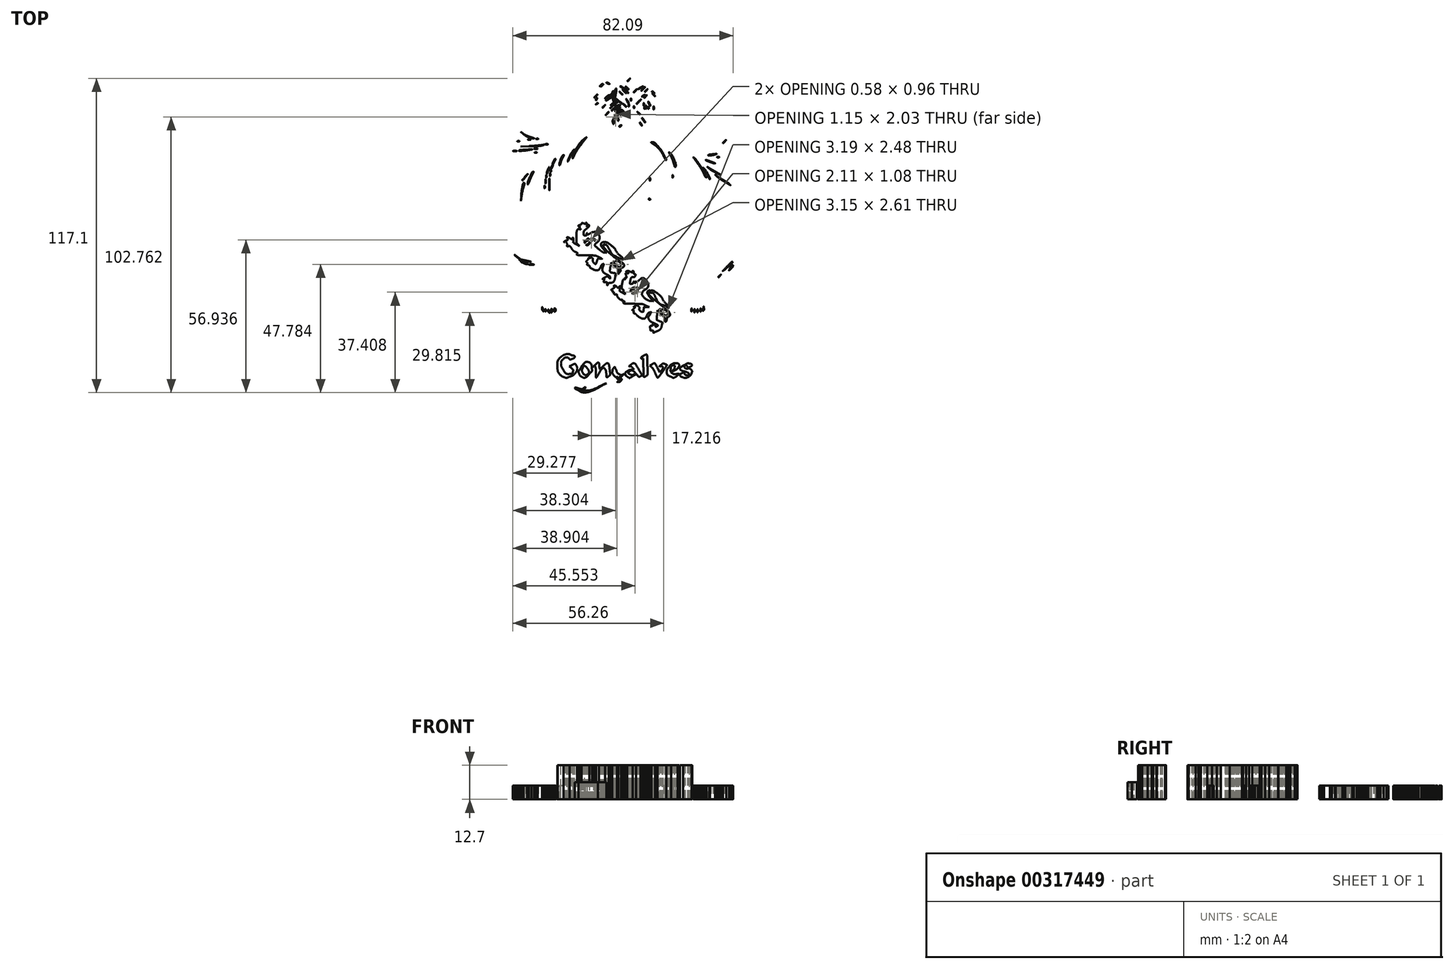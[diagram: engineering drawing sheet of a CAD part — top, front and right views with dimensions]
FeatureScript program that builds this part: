
annotation { "Feature Type Name" : "Feature", "Feature Type Description" : "" }
export const myFeature = defineFeature(function(context is Context, id is Id, definition is map)
    precondition{}
    {
        {
            var Q0;
            Q0=qCreatedBy(makeId("Top.planeOp"),FACE);
            var sketch = newSketch(context, id + "F0", { "sketchPlane" : qUnion([Q0])});
            skFitSpline(sketch, "E0", {"points": [v(-0.78, -58.9) * mm, v(-2.01, -54.71) * mm, v(-5.14, -53.63) * mm, v(-9.82, -55.77) * mm]});
            skFitSpline(sketch, "E1", {"points": [v(-9.82, -55.77) * mm, v(-12.56, -57.02) * mm, v(-15.5, -57.35) * mm, v(-17, -56.59) * mm]});
            skFitSpline(sketch, "E2", {"points": [v(-17, -56.59) * mm, v(-18.34, -55.9) * mm, v(-18.3, -55.62) * mm, v(-16.9, -55.94) * mm]});
            skFitSpline(sketch, "E3", {"points": [v(-16.9, -55.94) * mm, v(-15.84, -56.18) * mm, v(-15.54, -56.16) * mm, v(-15.17, -55.78) * mm]});
            skFitSpline(sketch, "E4", {"points": [v(-15.17, -55.78) * mm, v(-14.24, -54.85) * mm, v(-15.47, -53.87) * mm, v(-17.6, -53.87) * mm]});
            skFitSpline(sketch, "E5", {"points": [v(-17.6, -53.87) * mm, v(-18.18, -53.87) * mm, v(-20.42, -54.25) * mm, v(-22.58, -54.7) * mm]});
            skFitSpline(sketch, "E6", {"points": [v(-22.58, -54.7) * mm, v(-29.42, -56.14) * mm, v(-33.24, -56.1) * mm, v(-36.26, -54.57) * mm]});
            skFitSpline(sketch, "E7", {"points": [v(-36.26, -54.57) * mm, v(-37.83, -53.78) * mm, v(-39.63, -52.29) * mm, v(-39.63, -51.78) * mm]});
            skFitSpline(sketch, "E8", {"points": [v(-39.63, -51.78) * mm, v(-39.63, -51.6) * mm, v(-39.25, -51.16) * mm, v(-38.77, -50.8) * mm]});
            skFitSpline(sketch, "E9", {"points": [v(-38.77, -50.8) * mm, v(-36.7, -49.28) * mm, v(-35.55, -46.7) * mm, v(-34.68, -41.66) * mm]});
            skFitSpline(sketch, "E10", {"points": [v(-34.68, -41.66) * mm, v(-34, -37.71) * mm, v(-33.1, -36.66) * mm, v(-30.43, -36.66) * mm]});
            skFitSpline(sketch, "E11", {"points": [v(-30.43, -36.66) * mm, v(-28.5, -36.66) * mm, v(-26.08, -38.1) * mm, v(-26.08, -39.26) * mm]});
            skFitSpline(sketch, "E12", {"points": [v(-26.08, -39.26) * mm, v(-26.08, -39.55) * mm, v(-26.35, -40.3) * mm, v(-26.67, -40.93) * mm]});
            skFitSpline(sketch, "E13", {"points": [v(-26.67, -40.93) * mm, v(-26.99, -41.56) * mm, v(-27.17, -42.16) * mm, v(-27.07, -42.26) * mm]});
            skFitSpline(sketch, "E14", {"points": [v(-27.07, -42.26) * mm, v(-26.96, -42.36) * mm, v(-25.75, -42.44) * mm, v(-24.38, -42.44) * mm]});
            skFitSpline(sketch, "E15", {"points": [v(-24.38, -42.44) * mm, v(-22.29, -42.43) * mm, v(-21.74, -42.33) * mm, v(-21.09, -41.84) * mm]});
            skFitSpline(sketch, "E16", {"points": [v(-21.09, -41.84) * mm, v(-19.83, -40.9) * mm, v(-19.9, -40.33) * mm, v(-21.27, -40.33) * mm]});
            skFitSpline(sketch, "E17", {"points": [v(-21.27, -40.33) * mm, v(-22.5, -40.33) * mm, v(-22.69, -40) * mm, v(-22, -39.1) * mm]});
            skFitSpline(sketch, "E18", {"points": [v(-22, -39.1) * mm, v(-21.65, -38.64) * mm, v(-21.52, -38.63) * mm, v(-20.81, -38.97) * mm]});
            skFitSpline(sketch, "E19", {"points": [v(-20.81, -38.97) * mm, v(-20.14, -39.29) * mm, v(-20.02, -39.52) * mm, v(-20.02, -40.44) * mm]});
            skFitSpline(sketch, "E20", {"points": [v(-20.02, -40.44) * mm, v(-20.02, -42.1) * mm, v(-20.93, -42.65) * mm, v(-23.92, -42.8) * mm]});
            skFitSpline(sketch, "E21", {"points": [v(-23.92, -42.8) * mm, v(-28.38, -43.04) * mm, v(-33.52, -40.75) * mm, v(-33.08, -38.72) * mm]});
            skFitSpline(sketch, "E22", {"points": [v(-33.08, -38.72) * mm, v(-33.01, -38.44) * mm, v(-32.8, -38.25) * mm, v(-32.6, -38.29) * mm]});
            skFitSpline(sketch, "E23", {"points": [v(-32.6, -38.29) * mm, v(-32.41, -38.33) * mm, v(-32.33, -38.24) * mm, v(-32.42, -38.1) * mm]});
            skFitSpline(sketch, "E24", {"points": [v(-32.42, -38.1) * mm, v(-32.92, -37.29) * mm, v(-30.11, -36.95) * mm, v(-28.51, -37.62) * mm]});
            skFitSpline(sketch, "E25", {"points": [v(-28.51, -37.62) * mm, v(-27.53, -38.03) * mm, v(-26.56, -39.12) * mm, v(-26.82, -39.53) * mm]});
            skFitSpline(sketch, "E26", {"points": [v(-26.82, -39.53) * mm, v(-27.07, -39.93) * mm, v(-28.17, -39.79) * mm, v(-29.27, -39.2) * mm]});
            skLineSegment(sketch, "E27", {"start": v(-29.27, -39.2) * mm, "end": v(-30.33, -38.63) * mm});
            skLineSegment(sketch, "E28", {"start": v(-30.33, -38.63) * mm, "end": v(-30.61, -39.4) * mm});
            skFitSpline(sketch, "E29", {"points": [v(-30.61, -39.4) * mm, v(-30.77, -39.84) * mm, v(-30.95, -40.33) * mm, v(-31, -40.5) * mm]});
            skFitSpline(sketch, "E30", {"points": [v(-31, -40.5) * mm, v(-31.15, -40.9) * mm, v(-29.82, -41.53) * mm, v(-29.4, -41.28) * mm]});
            skFitSpline(sketch, "E31", {"points": [v(-29.4, -41.28) * mm, v(-29.21, -41.15) * mm, v(-29.18, -41.22) * mm, v(-29.33, -41.46) * mm]});
            skFitSpline(sketch, "E32", {"points": [v(-29.33, -41.46) * mm, v(-29.5, -41.74) * mm, v(-29.43, -41.78) * mm, v(-29.07, -41.65) * mm]});
            skFitSpline(sketch, "E33", {"points": [v(-29.07, -41.65) * mm, v(-28.8, -41.54) * mm, v(-28.27, -41.46) * mm, v(-27.9, -41.46) * mm]});
            skFitSpline(sketch, "E34", {"points": [v(-27.9, -41.46) * mm, v(-27.52, -41.46) * mm, v(-27.21, -41.31) * mm, v(-27.21, -41.14) * mm]});
            skFitSpline(sketch, "E35", {"points": [v(-27.21, -41.14) * mm, v(-27.21, -40.93) * mm, v(-27.53, -40.88) * mm, v(-28.13, -41) * mm]});
            skFitSpline(sketch, "E36", {"points": [v(-28.13, -41) * mm, v(-28.78, -41.12) * mm, v(-28.93, -41.1) * mm, v(-28.62, -40.9) * mm]});
            skFitSpline(sketch, "E37", {"points": [v(-28.62, -40.9) * mm, v(-28.4, -40.74) * mm, v(-27.9, -40.62) * mm, v(-27.55, -40.61) * mm]});
            skFitSpline(sketch, "E38", {"points": [v(-27.55, -40.61) * mm, v(-27.2, -40.61) * mm, v(-26.97, -40.5) * mm, v(-27.05, -40.36) * mm]});
            skFitSpline(sketch, "E39", {"points": [v(-27.05, -40.36) * mm, v(-27.14, -40.22) * mm, v(-27.02, -40.03) * mm, v(-26.79, -39.94) * mm]});
            skFitSpline(sketch, "E40", {"points": [v(-26.79, -39.94) * mm, v(-26.15, -39.7) * mm, v(-26.28, -39.1) * mm, v(-27.14, -38.28) * mm]});
            skFitSpline(sketch, "E41", {"points": [v(-27.14, -38.28) * mm, v(-29.26, -36.26) * mm, v(-32.86, -36.6) * mm, v(-33.66, -38.9) * mm]});
            skFitSpline(sketch, "E42", {"points": [v(-33.66, -38.9) * mm, v(-33.83, -39.39) * mm, v(-33.87, -39.75) * mm, v(-33.76, -39.7) * mm]});
            skFitSpline(sketch, "E43", {"points": [v(-33.76, -39.7) * mm, v(-33.65, -39.65) * mm, v(-33.08, -40.1) * mm, v(-32.5, -40.67) * mm]});
            skFitSpline(sketch, "E44", {"points": [v(-32.5, -40.67) * mm, v(-31.9, -41.26) * mm, v(-31.6, -41.66) * mm, v(-31.84, -41.57) * mm]});
            skFitSpline(sketch, "E45", {"points": [v(-31.84, -41.57) * mm, v(-32.16, -41.45) * mm, v(-32.24, -41.56) * mm, v(-32.16, -41.98) * mm]});
            skFitSpline(sketch, "E46", {"points": [v(-32.16, -41.98) * mm, v(-32.08, -42.38) * mm, v(-32.17, -42.5) * mm, v(-32.44, -42.4) * mm]});
            skFitSpline(sketch, "E47", {"points": [v(-32.44, -42.4) * mm, v(-32.72, -42.3) * mm, v(-32.8, -42.43) * mm, v(-32.71, -42.88) * mm]});
            skFitSpline(sketch, "E48", {"points": [v(-32.71, -42.88) * mm, v(-32.65, -43.23) * mm, v(-32.68, -43.42) * mm, v(-32.8, -43.3) * mm]});
            skFitSpline(sketch, "E49", {"points": [v(-32.8, -43.3) * mm, v(-32.9, -43.2) * mm, v(-33, -42.96) * mm, v(-33, -42.78) * mm]});
            skFitSpline(sketch, "E50", {"points": [v(-33, -42.78) * mm, v(-33, -42.6) * mm, v(-33.38, -42.43) * mm, v(-33.85, -42.4) * mm]});
            skFitSpline(sketch, "E51", {"points": [v(-33.85, -42.4) * mm, v(-34.31, -42.38) * mm, v(-34.53, -42.42) * mm, v(-34.34, -42.5) * mm]});
            skFitSpline(sketch, "E52", {"points": [v(-34.34, -42.5) * mm, v(-34.14, -42.57) * mm, v(-34.08, -42.78) * mm, v(-34.2, -42.96) * mm]});
            skFitSpline(sketch, "E53", {"points": [v(-34.2, -42.96) * mm, v(-34.31, -43.14) * mm, v(-34.41, -43.55) * mm, v(-34.42, -43.86) * mm]});
            skFitSpline(sketch, "E54", {"points": [v(-34.42, -43.86) * mm, v(-34.42, -44.17) * mm, v(-34.53, -44.58) * mm, v(-34.65, -44.77) * mm]});
            skFitSpline(sketch, "E55", {"points": [v(-34.65, -44.77) * mm, v(-34.77, -44.97) * mm, v(-34.78, -45.13) * mm, v(-34.66, -45.13) * mm]});
            skFitSpline(sketch, "E56", {"points": [v(-34.66, -45.13) * mm, v(-34.55, -45.13) * mm, v(-34.7, -45.4) * mm, v(-35, -45.74) * mm]});
            skFitSpline(sketch, "E57", {"points": [v(-35, -45.74) * mm, v(-35.3, -46.08) * mm, v(-35.38, -46.26) * mm, v(-35.19, -46.15) * mm]});
            skFitSpline(sketch, "E58", {"points": [v(-35.19, -46.15) * mm, v(-34.63, -45.82) * mm, v(-34.77, -46.3) * mm, v(-35.47, -47.06) * mm]});
            skFitSpline(sketch, "E59", {"points": [v(-35.47, -47.06) * mm, v(-35.82, -47.44) * mm, v(-35.94, -47.67) * mm, v(-35.75, -47.55) * mm]});
            skFitSpline(sketch, "E60", {"points": [v(-35.75, -47.55) * mm, v(-35.14, -47.2) * mm, v(-35.37, -47.82) * mm, v(-36.1, -48.51) * mm]});
            skFitSpline(sketch, "E61", {"points": [v(-36.1, -48.51) * mm, v(-36.5, -48.88) * mm, v(-36.8, -49.3) * mm, v(-36.8, -49.46) * mm]});
            skFitSpline(sketch, "E62", {"points": [v(-36.8, -49.46) * mm, v(-36.8, -49.6) * mm, v(-36.72, -49.65) * mm, v(-36.62, -49.55) * mm]});
            skFitSpline(sketch, "E63", {"points": [v(-36.62, -49.55) * mm, v(-36.45, -49.38) * mm, v(-35.59, -50.37) * mm, v(-35.5, -50.84) * mm]});
            skFitSpline(sketch, "E64", {"points": [v(-35.5, -50.84) * mm, v(-35.48, -50.96) * mm, v(-35.44, -51.08) * mm, v(-35.4, -51.12) * mm]});
            skFitSpline(sketch, "E65", {"points": [v(-35.4, -51.12) * mm, v(-35.22, -51.33) * mm, v(-35.23, -52.79) * mm, v(-35.43, -52.9) * mm]});
            skFitSpline(sketch, "E66", {"points": [v(-35.43, -52.9) * mm, v(-35.55, -52.98) * mm, v(-35.6, -52.78) * mm, v(-35.54, -52.45) * mm]});
            skFitSpline(sketch, "E67", {"points": [v(-35.54, -52.45) * mm, v(-35.46, -52.08) * mm, v(-35.55, -51.9) * mm, v(-35.76, -51.97) * mm]});
            skFitSpline(sketch, "E68", {"points": [v(-35.76, -51.97) * mm, v(-35.95, -52.04) * mm, v(-36.1, -52.34) * mm, v(-36.1, -52.66) * mm]});
            skFitSpline(sketch, "E69", {"points": [v(-36.1, -52.66) * mm, v(-36.1, -52.97) * mm, v(-36.28, -53.43) * mm, v(-36.5, -53.69) * mm]});
            skFitSpline(sketch, "E70", {"points": [v(-36.5, -53.69) * mm, v(-36.94, -54.23) * mm, v(-36.54, -54.32) * mm, v(-35.96, -53.8) * mm]});
            skFitSpline(sketch, "E71", {"points": [v(-35.96, -53.8) * mm, v(-35.65, -53.53) * mm, v(-35.65, -53.57) * mm, v(-35.98, -54) * mm]});
            skFitSpline(sketch, "E72", {"points": [v(-35.98, -54) * mm, v(-36.34, -54.5) * mm, v(-36.34, -54.53) * mm, v(-35.9, -54.36) * mm]});
            skFitSpline(sketch, "E73", {"points": [v(-35.9, -54.36) * mm, v(-35.62, -54.26) * mm, v(-35.4, -54.28) * mm, v(-35.4, -54.41) * mm]});
            skFitSpline(sketch, "E74", {"points": [v(-35.4, -54.41) * mm, v(-35.4, -54.88) * mm, v(-32.86, -55.29) * mm, v(-29.98, -55.28) * mm]});
            skFitSpline(sketch, "E75", {"points": [v(-29.98, -55.28) * mm, v(-27.92, -55.28) * mm, v(-26.1, -55.07) * mm, v(-23.69, -54.55) * mm]});
            skFitSpline(sketch, "E76", {"points": [v(-23.69, -54.55) * mm, v(-21.82, -54.14) * mm, v(-19.35, -53.76) * mm, v(-18.18, -53.7) * mm]});
            skFitSpline(sketch, "E77", {"points": [v(-18.18, -53.7) * mm, v(-15.67, -53.55) * mm, v(-14.7, -53.92) * mm, v(-14.56, -55.09) * mm]});
            skFitSpline(sketch, "E78", {"points": [v(-14.56, -55.09) * mm, v(-14.49, -55.73) * mm, v(-14.63, -55.93) * mm, v(-15.41, -56.27) * mm]});
            skLineSegment(sketch, "E79", {"start": v(-15.41, -56.27) * mm, "end": v(-16.35, -56.67) * mm});
            skLineSegment(sketch, "E80", {"start": v(-16.35, -56.67) * mm, "end": v(-14.77, -56.69) * mm});
            skFitSpline(sketch, "E81", {"points": [v(-14.77, -56.69) * mm, v(-13.2, -56.7) * mm, v(-11.19, -56.13) * mm, v(-9, -55.07) * mm]});
            skFitSpline(sketch, "E82", {"points": [v(-9, -55.07) * mm, v(-7.1, -54.14) * mm, v(-5.09, -54.06) * mm, v(-3.21, -54.84) * mm]});
            skFitSpline(sketch, "E83", {"points": [v(-3.21, -54.84) * mm, v(-2.94, -54.95) * mm, v(-2.41, -54.7) * mm, v(-1.82, -54.16) * mm]});
            skFitSpline(sketch, "E84", {"points": [v(-1.82, -54.16) * mm, v(-0.8, -53.25) * mm, v(0.28, -53.05) * mm, v(0.55, -53.73) * mm]});
            skFitSpline(sketch, "E85", {"points": [v(0.55, -53.73) * mm, v(0.64, -53.97) * mm, v(0.85, -54.16) * mm, v(1.02, -54.16) * mm]});
            skFitSpline(sketch, "E86", {"points": [v(1.02, -54.16) * mm, v(1.2, -54.16) * mm, v(1.5, -54.33) * mm, v(1.72, -54.54) * mm]});
            skFitSpline(sketch, "E87", {"points": [v(1.72, -54.54) * mm, v(2.04, -54.87) * mm, v(2.34, -54.87) * mm, v(3.55, -54.55) * mm]});
            skFitSpline(sketch, "E88", {"points": [v(3.55, -54.55) * mm, v(5.37, -54.08) * mm, v(6.94, -54.35) * mm, v(9.57, -55.59) * mm]});
            skFitSpline(sketch, "E89", {"points": [v(9.57, -55.59) * mm, v(11.05, -56.28) * mm, v(11.99, -56.52) * mm, v(13.53, -56.6) * mm]});
            skFitSpline(sketch, "E90", {"points": [v(13.53, -56.6) * mm, v(15.18, -56.68) * mm, v(15.4, -56.64) * mm, v(14.78, -56.4) * mm]});
            skFitSpline(sketch, "E91", {"points": [v(14.78, -56.4) * mm, v(13.63, -55.94) * mm, v(13.47, -55.04) * mm, v(14.4, -54.24) * mm]});
            skFitSpline(sketch, "E92", {"points": [v(14.4, -54.24) * mm, v(15.01, -53.71) * mm, v(15.48, -53.6) * mm, v(16.9, -53.6) * mm]});
            skFitSpline(sketch, "E93", {"points": [v(16.9, -53.6) * mm, v(17.86, -53.6) * mm, v(19.47, -53.8) * mm, v(20.48, -54.04) * mm]});
            skFitSpline(sketch, "E94", {"points": [v(20.48, -54.04) * mm, v(24.13, -54.91) * mm, v(26.89, -55.28) * mm, v(29.67, -55.29) * mm]});
            skFitSpline(sketch, "E95", {"points": [v(29.67, -55.29) * mm, v(33, -55.29) * mm, v(35.6, -54.68) * mm, v(35.32, -53.96) * mm]});
            skFitSpline(sketch, "E96", {"points": [v(35.32, -53.96) * mm, v(35.18, -53.6) * mm, v(35.22, -53.58) * mm, v(35.55, -53.85) * mm]});
            skFitSpline(sketch, "E97", {"points": [v(35.55, -53.85) * mm, v(35.9, -54.14) * mm, v(35.95, -54.05) * mm, v(35.9, -53.27) * mm]});
            skFitSpline(sketch, "E98", {"points": [v(35.9, -53.27) * mm, v(35.85, -52.77) * mm, v(35.66, -52.3) * mm, v(35.45, -52.23) * mm]});
            skFitSpline(sketch, "E99", {"points": [v(35.45, -52.23) * mm, v(35.2, -52.15) * mm, v(35.15, -52.24) * mm, v(35.3, -52.5) * mm]});
            skFitSpline(sketch, "E100", {"points": [v(35.3, -52.5) * mm, v(35.48, -52.81) * mm, v(35.45, -52.82) * mm, v(35.14, -52.53) * mm]});
            skFitSpline(sketch, "E101", {"points": [v(35.14, -52.53) * mm, v(34.57, -52) * mm, v(34.19, -52.1) * mm, v(34.63, -52.67) * mm]});
            skFitSpline(sketch, "E102", {"points": [v(34.63, -52.67) * mm, v(34.98, -53.13) * mm, v(34.97, -53.14) * mm, v(34.5, -52.76) * mm]});
            skFitSpline(sketch, "E103", {"points": [v(34.5, -52.76) * mm, v(34, -52.36) * mm, v(34, -52.34) * mm, v(34.5, -51.97) * mm]});
            skFitSpline(sketch, "E104", {"points": [v(34.5, -51.97) * mm, v(34.78, -51.76) * mm, v(35.02, -51.44) * mm, v(35.03, -51.25) * mm]});
            skFitSpline(sketch, "E105", {"points": [v(35.03, -51.25) * mm, v(35.04, -51.06) * mm, v(35.23, -50.95) * mm, v(35.45, -51) * mm]});
            skFitSpline(sketch, "E106", {"points": [v(35.45, -51) * mm, v(35.77, -51.07) * mm, v(35.79, -51.02) * mm, v(35.52, -50.75) * mm]});
            skFitSpline(sketch, "E107", {"points": [v(35.52, -50.75) * mm, v(35.26, -50.47) * mm, v(35.1, -50.47) * mm, v(34.77, -50.74) * mm]});
            skFitSpline(sketch, "E108", {"points": [v(34.77, -50.74) * mm, v(34.44, -51.02) * mm, v(34.37, -51) * mm, v(34.42, -50.65) * mm]});
            skFitSpline(sketch, "E109", {"points": [v(34.42, -50.65) * mm, v(34.45, -50.42) * mm, v(34.56, -50.14) * mm, v(34.66, -50.05) * mm]});
            skFitSpline(sketch, "E110", {"points": [v(34.66, -50.05) * mm, v(34.92, -49.78) * mm, v(34.58, -49.05) * mm, v(34.28, -49.24) * mm]});
            skFitSpline(sketch, "E111", {"points": [v(34.28, -49.24) * mm, v(34.14, -49.33) * mm, v(34.09, -49.5) * mm, v(34.17, -49.64) * mm]});
            skFitSpline(sketch, "E112", {"points": [v(34.17, -49.64) * mm, v(34.25, -49.77) * mm, v(34.17, -49.98) * mm, v(34, -50.09) * mm]});
            skFitSpline(sketch, "E113", {"points": [v(34, -50.09) * mm, v(33.77, -50.23) * mm, v(33.74, -50.17) * mm, v(33.9, -49.92) * mm]});
            skFitSpline(sketch, "E114", {"points": [v(33.9, -49.92) * mm, v(34.06, -49.65) * mm, v(34, -49.6) * mm, v(33.65, -49.73) * mm]});
            skFitSpline(sketch, "E115", {"points": [v(33.65, -49.73) * mm, v(32.97, -49.99) * mm, v(33.07, -49.83) * mm, v(34.07, -49.1) * mm]});
            skFitSpline(sketch, "E116", {"points": [v(34.07, -49.1) * mm, v(34.56, -48.73) * mm, v(34.86, -48.6) * mm, v(34.73, -48.8) * mm]});
            skFitSpline(sketch, "E117", {"points": [v(34.73, -48.8) * mm, v(34.57, -49.06) * mm, v(34.62, -49.1) * mm, v(34.88, -48.93) * mm]});
            skFitSpline(sketch, "E118", {"points": [v(34.88, -48.93) * mm, v(35.15, -48.76) * mm, v(35.2, -48.83) * mm, v(35.07, -49.19) * mm]});
            skFitSpline(sketch, "E119", {"points": [v(35.07, -49.19) * mm, v(34.97, -49.45) * mm, v(35, -49.6) * mm, v(35.14, -49.51) * mm]});
            skFitSpline(sketch, "E120", {"points": [v(35.14, -49.51) * mm, v(35.28, -49.42) * mm, v(35.5, -49.5) * mm, v(35.6, -49.68) * mm]});
            skFitSpline(sketch, "E121", {"points": [v(35.6, -49.68) * mm, v(35.73, -49.89) * mm, v(35.69, -49.93) * mm, v(35.49, -49.81) * mm]});
            skFitSpline(sketch, "E122", {"points": [v(35.49, -49.81) * mm, v(35.28, -49.68) * mm, v(35.22, -49.77) * mm, v(35.33, -50.05) * mm]});
            skFitSpline(sketch, "E123", {"points": [v(35.33, -50.05) * mm, v(35.42, -50.29) * mm, v(35.6, -50.42) * mm, v(35.73, -50.34) * mm]});
            skFitSpline(sketch, "E124", {"points": [v(35.73, -50.34) * mm, v(35.86, -50.26) * mm, v(36.06, -50.35) * mm, v(36.17, -50.53) * mm]});
            skFitSpline(sketch, "E125", {"points": [v(36.17, -50.53) * mm, v(36.3, -50.73) * mm, v(36.25, -50.78) * mm, v(36.05, -50.66) * mm]});
            skFitSpline(sketch, "E126", {"points": [v(36.05, -50.66) * mm, v(35.83, -50.52) * mm, v(35.8, -50.62) * mm, v(35.92, -50.95) * mm]});
            skFitSpline(sketch, "E127", {"points": [v(35.92, -50.95) * mm, v(36.04, -51.28) * mm, v(36.15, -51.33) * mm, v(36.23, -51.1) * mm]});
            skFitSpline(sketch, "E128", {"points": [v(36.23, -51.1) * mm, v(36.3, -50.84) * mm, v(36.46, -50.9) * mm, v(36.74, -51.25) * mm]});
            skFitSpline(sketch, "E129", {"points": [v(36.74, -51.25) * mm, v(37.11, -51.73) * mm, v(37.12, -51.73) * mm, v(36.95, -51.2) * mm]});
            skFitSpline(sketch, "E130", {"points": [v(36.95, -51.2) * mm, v(36.85, -50.88) * mm, v(36.86, -50.71) * mm, v(36.97, -50.82) * mm]});
            skFitSpline(sketch, "E131", {"points": [v(36.97, -50.82) * mm, v(37.3, -51.11) * mm, v(37.38, -52.47) * mm, v(37.05, -52.27) * mm]});
            skFitSpline(sketch, "E132", {"points": [v(37.05, -52.27) * mm, v(36.88, -52.16) * mm, v(36.85, -52.24) * mm, v(37, -52.46) * mm]});
            skFitSpline(sketch, "E133", {"points": [v(37, -52.46) * mm, v(37.14, -52.7) * mm, v(37.11, -52.76) * mm, v(36.9, -52.64) * mm]});
            skFitSpline(sketch, "E134", {"points": [v(36.9, -52.64) * mm, v(36.73, -52.53) * mm, v(36.68, -52.23) * mm, v(36.78, -51.96) * mm]});
            skFitSpline(sketch, "E135", {"points": [v(36.78, -51.96) * mm, v(36.94, -51.53) * mm, v(36.9, -51.52) * mm, v(36.47, -51.87) * mm]});
            skFitSpline(sketch, "E136", {"points": [v(36.47, -51.87) * mm, v(35.93, -52.31) * mm, v(36.15, -52.7) * mm, v(37.06, -52.87) * mm]});
            skFitSpline(sketch, "E137", {"points": [v(37.06, -52.87) * mm, v(37.56, -52.97) * mm, v(37.64, -52.87) * mm, v(37.53, -52.23) * mm]});
            skFitSpline(sketch, "E138", {"points": [v(37.53, -52.23) * mm, v(37.42, -51.5) * mm, v(37.43, -51.5) * mm, v(37.84, -52.02) * mm]});
            skFitSpline(sketch, "E139", {"points": [v(37.84, -52.02) * mm, v(38.07, -52.32) * mm, v(38.26, -52.42) * mm, v(38.26, -52.24) * mm]});
            skFitSpline(sketch, "E140", {"points": [v(38.26, -52.24) * mm, v(38.26, -52.05) * mm, v(38.26, -51.84) * mm, v(38.26, -51.76) * mm]});
            skFitSpline(sketch, "E141", {"points": [v(38.26, -51.76) * mm, v(38.26, -51.68) * mm, v(38.19, -51.63) * mm, v(38.1, -51.64) * mm]});
            skFitSpline(sketch, "E142", {"points": [v(38.1, -51.64) * mm, v(38, -51.65) * mm, v(37.76, -51.42) * mm, v(37.55, -51.14) * mm]});
            skFitSpline(sketch, "E143", {"points": [v(37.55, -51.14) * mm, v(37.35, -50.86) * mm, v(37.05, -50.63) * mm, v(36.9, -50.63) * mm]});
            skFitSpline(sketch, "E144", {"points": [v(36.9, -50.63) * mm, v(36.63, -50.63) * mm, v(34.88, -48.42) * mm, v(34.88, -48.07) * mm]});
            skFitSpline(sketch, "E145", {"points": [v(34.88, -48.07) * mm, v(34.88, -47.99) * mm, v(35.03, -48) * mm, v(35.23, -48.12) * mm]});
            skFitSpline(sketch, "E146", {"points": [v(35.23, -48.12) * mm, v(35.42, -48.23) * mm, v(35.3, -48) * mm, v(34.95, -47.62) * mm]});
            skFitSpline(sketch, "E147", {"points": [v(34.95, -47.62) * mm, v(34.25, -46.86) * mm, v(34.1, -46.4) * mm, v(34.66, -46.7) * mm]});
            skFitSpline(sketch, "E148", {"points": [v(34.66, -46.7) * mm, v(34.86, -46.8) * mm, v(34.74, -46.6) * mm, v(34.4, -46.24) * mm]});
            skFitSpline(sketch, "E149", {"points": [v(34.4, -46.24) * mm, v(34.05, -45.88) * mm, v(33.5, -45.57) * mm, v(33.15, -45.54) * mm]});
            skFitSpline(sketch, "E150", {"points": [v(33.15, -45.54) * mm, v(32.58, -45.5) * mm, v(32.58, -45.53) * mm, v(33.3, -46.05) * mm]});
            skFitSpline(sketch, "E151", {"points": [v(33.3, -46.05) * mm, v(33.93, -46.51) * mm, v(34, -46.67) * mm, v(33.69, -47.04) * mm]});
            skFitSpline(sketch, "E152", {"points": [v(33.69, -47.04) * mm, v(33.37, -47.43) * mm, v(33.4, -47.46) * mm, v(33.88, -47.28) * mm]});
            skFitSpline(sketch, "E153", {"points": [v(33.88, -47.28) * mm, v(34.19, -47.17) * mm, v(34.34, -47.16) * mm, v(34.23, -47.27) * mm]});
            skFitSpline(sketch, "E154", {"points": [v(34.23, -47.27) * mm, v(34.12, -47.38) * mm, v(34.16, -47.62) * mm, v(34.31, -47.8) * mm]});
            skFitSpline(sketch, "E155", {"points": [v(34.31, -47.8) * mm, v(34.5, -48.04) * mm, v(34.4, -48.3) * mm, v(33.98, -48.68) * mm]});
            skFitSpline(sketch, "E156", {"points": [v(33.98, -48.68) * mm, v(33.64, -48.98) * mm, v(33.47, -49.04) * mm, v(33.6, -48.82) * mm]});
            skFitSpline(sketch, "E157", {"points": [v(33.6, -48.82) * mm, v(33.78, -48.52) * mm, v(33.72, -48.46) * mm, v(33.39, -48.59) * mm]});
            skFitSpline(sketch, "E158", {"points": [v(33.39, -48.59) * mm, v(33.05, -48.72) * mm, v(32.97, -48.62) * mm, v(33.05, -48.2) * mm]});
            skFitSpline(sketch, "E159", {"points": [v(33.05, -48.2) * mm, v(33.14, -47.74) * mm, v(33.04, -47.67) * mm, v(32.53, -47.81) * mm]});
            skFitSpline(sketch, "E160", {"points": [v(32.53, -47.81) * mm, v(32.1, -47.93) * mm, v(32.03, -47.9) * mm, v(32.3, -47.72) * mm]});
            skFitSpline(sketch, "E161", {"points": [v(32.3, -47.72) * mm, v(32.62, -47.5) * mm, v(32.62, -47.43) * mm, v(32.3, -47.3) * mm]});
            skFitSpline(sketch, "E162", {"points": [v(32.3, -47.3) * mm, v(31.99, -47.17) * mm, v(32, -47.14) * mm, v(32.32, -47.12) * mm]});
            skFitSpline(sketch, "E163", {"points": [v(32.32, -47.12) * mm, v(32.62, -47.1) * mm, v(32.58, -46.99) * mm, v(32.18, -46.68) * mm]});
            skFitSpline(sketch, "E164", {"points": [v(32.18, -46.68) * mm, v(31.81, -46.4) * mm, v(31.78, -46.3) * mm, v(32.08, -46.4) * mm]});
            skFitSpline(sketch, "E165", {"points": [v(32.08, -46.4) * mm, v(32.36, -46.5) * mm, v(32.52, -46.4) * mm, v(32.52, -46.11) * mm]});
            skFitSpline(sketch, "E166", {"points": [v(32.52, -46.11) * mm, v(32.52, -45.83) * mm, v(32.36, -45.72) * mm, v(32.08, -45.82) * mm]});
            skFitSpline(sketch, "E167", {"points": [v(32.08, -45.82) * mm, v(31.78, -45.92) * mm, v(31.81, -45.83) * mm, v(32.18, -45.55) * mm]});
            skFitSpline(sketch, "E168", {"points": [v(32.18, -45.55) * mm, v(32.82, -45.05) * mm, v(33.05, -44.16) * mm, v(32.47, -44.38) * mm]});
            skFitSpline(sketch, "E169", {"points": [v(32.47, -44.38) * mm, v(32.21, -44.48) * mm, v(32.13, -44.35) * mm, v(32.2, -43.95) * mm]});
            skFitSpline(sketch, "E170", {"points": [v(32.2, -43.95) * mm, v(32.28, -43.53) * mm, v(32.2, -43.42) * mm, v(31.89, -43.54) * mm]});
            skFitSpline(sketch, "E171", {"points": [v(31.89, -43.54) * mm, v(31.65, -43.63) * mm, v(31.53, -43.6) * mm, v(31.62, -43.45) * mm]});
            skFitSpline(sketch, "E172", {"points": [v(31.62, -43.45) * mm, v(31.7, -43.31) * mm, v(31.62, -43.15) * mm, v(31.43, -43.08) * mm]});
            skFitSpline(sketch, "E173", {"points": [v(31.43, -43.08) * mm, v(31.22, -43.01) * mm, v(31.28, -42.9) * mm, v(31.59, -42.78) * mm]});
            skFitSpline(sketch, "E174", {"points": [v(31.59, -42.78) * mm, v(31.92, -42.66) * mm, v(32.02, -42.7) * mm, v(31.89, -42.9) * mm]});
            skFitSpline(sketch, "E175", {"points": [v(31.89, -42.9) * mm, v(31.77, -43.1) * mm, v(31.84, -43.17) * mm, v(32.06, -43.1) * mm]});
            skFitSpline(sketch, "E176", {"points": [v(32.06, -43.1) * mm, v(32.26, -43.03) * mm, v(32.46, -42.75) * mm, v(32.5, -42.48) * mm]});
            skFitSpline(sketch, "E177", {"points": [v(32.5, -42.48) * mm, v(32.55, -42.17) * mm, v(32.44, -42.03) * mm, v(32.22, -42.11) * mm]});
            skFitSpline(sketch, "E178", {"points": [v(32.22, -42.11) * mm, v(31.72, -42.3) * mm, v(31.82, -41.18) * mm, v(32.37, -40.4) * mm]});
            skFitSpline(sketch, "E179", {"points": [v(32.37, -40.4) * mm, v(32.61, -40.05) * mm, v(32.9, -39.85) * mm, v(33, -39.95) * mm]});
            skFitSpline(sketch, "E180", {"points": [v(33, -39.95) * mm, v(33.32, -40.28) * mm, v(33.2, -40.65) * mm, v(32.83, -40.43) * mm]});
            skFitSpline(sketch, "E181", {"points": [v(32.83, -40.43) * mm, v(32.55, -40.27) * mm, v(32.55, -40.3) * mm, v(32.81, -40.64) * mm]});
            skFitSpline(sketch, "E182", {"points": [v(32.81, -40.64) * mm, v(33.07, -40.96) * mm, v(33.14, -42.16) * mm, v(32.9, -42.16) * mm]});
            skFitSpline(sketch, "E183", {"points": [v(32.9, -42.16) * mm, v(32.88, -42.16) * mm, v(32.81, -42.4) * mm, v(32.76, -42.67) * mm]});
            skFitSpline(sketch, "E184", {"points": [v(32.76, -42.67) * mm, v(32.69, -43.05) * mm, v(32.75, -43.1) * mm, v(33.02, -42.89) * mm]});
            skFitSpline(sketch, "E185", {"points": [v(33.02, -42.89) * mm, v(33.22, -42.72) * mm, v(33.45, -42.66) * mm, v(33.54, -42.75) * mm]});
            skFitSpline(sketch, "E186", {"points": [v(33.54, -42.75) * mm, v(33.77, -42.99) * mm, v(33.64, -42.24) * mm, v(33.37, -41.8) * mm]});
            skFitSpline(sketch, "E187", {"points": [v(33.37, -41.8) * mm, v(33.24, -41.6) * mm, v(33.3, -41.46) * mm, v(33.5, -41.46) * mm]});
            skFitSpline(sketch, "E188", {"points": [v(33.5, -41.46) * mm, v(33.77, -41.46) * mm, v(33.78, -41.37) * mm, v(33.54, -41.14) * mm]});
            skFitSpline(sketch, "E189", {"points": [v(33.54, -41.14) * mm, v(33.37, -40.97) * mm, v(33.29, -40.66) * mm, v(33.36, -40.46) * mm]});
            skFitSpline(sketch, "E190", {"points": [v(33.36, -40.46) * mm, v(33.44, -40.26) * mm, v(33.37, -40.02) * mm, v(33.2, -39.92) * mm]});
            skFitSpline(sketch, "E191", {"points": [v(33.2, -39.92) * mm, v(33.04, -39.81) * mm, v(32.9, -39.44) * mm, v(32.9, -39.08) * mm]});
            skFitSpline(sketch, "E192", {"points": [v(32.9, -39.08) * mm, v(32.9, -38.72) * mm, v(32.7, -38.26) * mm, v(32.48, -38.07) * mm]});
            skFitSpline(sketch, "E193", {"points": [v(32.48, -38.07) * mm, v(32.16, -37.8) * mm, v(32.05, -37.8) * mm, v(32.05, -38.05) * mm]});
            skFitSpline(sketch, "E194", {"points": [v(32.05, -38.05) * mm, v(32.05, -38.24) * mm, v(31.9, -38.3) * mm, v(31.73, -38.18) * mm]});
            skFitSpline(sketch, "E195", {"points": [v(31.73, -38.18) * mm, v(31.52, -38.06) * mm, v(31.48, -38.1) * mm, v(31.6, -38.31) * mm]});
            skFitSpline(sketch, "E196", {"points": [v(31.6, -38.31) * mm, v(31.72, -38.5) * mm, v(31.93, -38.57) * mm, v(32.07, -38.48) * mm]});
            skFitSpline(sketch, "E197", {"points": [v(32.07, -38.48) * mm, v(32.22, -38.4) * mm, v(32.34, -38.63) * mm, v(32.34, -39.02) * mm]});
            skFitSpline(sketch, "E198", {"points": [v(32.34, -39.02) * mm, v(32.34, -40.78) * mm, v(27.73, -42.87) * mm, v(23.87, -42.86) * mm]});
            skFitSpline(sketch, "E199", {"points": [v(23.87, -42.86) * mm, v(20.4, -42.85) * mm, v(18.6, -41.67) * mm, v(19.2, -39.8) * mm]});
            skFitSpline(sketch, "E200", {"points": [v(19.2, -39.8) * mm, v(19.3, -39.48) * mm, v(19.65, -39.14) * mm, v(19.97, -39.04) * mm]});
            skFitSpline(sketch, "E201", {"points": [v(19.97, -39.04) * mm, v(20.91, -38.74) * mm, v(20, -38.36) * mm, v(18.34, -38.36) * mm]});
            skFitSpline(sketch, "E202", {"points": [v(18.34, -38.36) * mm, v(16.62, -38.35) * mm, v(15.97, -38.55) * mm, v(11.73, -40.42) * mm]});
            skFitSpline(sketch, "E203", {"points": [v(11.73, -40.42) * mm, v(8.77, -41.73) * mm, v(8.26, -41.86) * mm, v(5.92, -41.97) * mm]});
            skFitSpline(sketch, "E204", {"points": [v(5.92, -41.97) * mm, v(3.75, -42.07) * mm, v(3.14, -42) * mm, v(2, -41.48) * mm]});
            skFitSpline(sketch, "E205", {"points": [v(2, -41.48) * mm, v(1.24, -41.15) * mm, v(0.45, -40.63) * mm, v(0.23, -40.31) * mm]});
            skFitSpline(sketch, "E206", {"points": [v(0.23, -40.31) * mm, v(-0.16, -39.75) * mm, v(-0.18, -39.76) * mm, v(-1.1, -40.57) * mm]});
            skFitSpline(sketch, "E207", {"points": [v(-1.1, -40.57) * mm, v(-2.5, -41.79) * mm, v(-3.76, -42.1) * mm, v(-6.71, -41.97) * mm]});
            skFitSpline(sketch, "E208", {"points": [v(-6.71, -41.97) * mm, v(-9.1, -41.86) * mm, v(-9.52, -41.75) * mm, v(-12.47, -40.39) * mm]});
            skFitSpline(sketch, "E209", {"points": [v(-12.47, -40.39) * mm, v(-16.3, -38.62) * mm, v(-17.7, -38.24) * mm, v(-19.73, -38.41) * mm]});
            skFitSpline(sketch, "E210", {"points": [v(-19.73, -38.41) * mm, v(-21.38, -38.55) * mm, v(-21.6, -38.25) * mm, v(-20.07, -37.96) * mm]});
            skFitSpline(sketch, "E211", {"points": [v(-20.07, -37.96) * mm, v(-18.6, -37.68) * mm, v(-16.32, -38.25) * mm, v(-13.25, -39.65) * mm]});
            skFitSpline(sketch, "E212", {"points": [v(-13.25, -39.65) * mm, v(-9.9, -41.18) * mm, v(-8.06, -41.73) * mm, v(-6.33, -41.73) * mm]});
            skFitSpline(sketch, "E213", {"points": [v(-6.33, -41.73) * mm, v(-5.1, -41.73) * mm, v(-5.14, -41.7) * mm, v(-7.6, -40.87) * mm]});
            skFitSpline(sketch, "E214", {"points": [v(-7.6, -40.87) * mm, v(-15.53, -38.2) * mm, v(-20.56, -32.24) * mm, v(-22.46, -23.25) * mm]});
            skFitSpline(sketch, "E215", {"points": [v(-22.46, -23.25) * mm, v(-22.85, -21.4) * mm, v(-23.04, -18.95) * mm, v(-23.17, -14.17) * mm]});
            skLineSegment(sketch, "E216", {"start": v(-23.17, -14.17) * mm, "end": v(-23.35, -7.63) * mm});
            skLineSegment(sketch, "E217", {"start": v(-23.35, -7.63) * mm, "end": v(-24.18, -8.87) * mm});
            skFitSpline(sketch, "E218", {"points": [v(-24.18, -8.87) * mm, v(-25.72, -11.2) * mm, v(-28.2, -12.66) * mm, v(-31.37, -13.09) * mm]});
            skFitSpline(sketch, "E219", {"points": [v(-31.37, -13.09) * mm, v(-32.83, -13.28) * mm, v(-32.84, -13.29) * mm, v(-32.4, -13.95) * mm]});
            skFitSpline(sketch, "E220", {"points": [v(-32.4, -13.95) * mm, v(-32.16, -14.31) * mm, v(-32, -14.9) * mm, v(-32.06, -15.26) * mm]});
            skFitSpline(sketch, "E221", {"points": [v(-32.06, -15.26) * mm, v(-32.15, -15.87) * mm, v(-32.28, -15.92) * mm, v(-34.05, -15.92) * mm]});
            skLineSegment(sketch, "E222", {"start": v(-34.05, -15.92) * mm, "end": v(-35.95, -15.92) * mm});
            skLineSegment(sketch, "E223", {"start": v(-35.95, -15.92) * mm, "end": v(-37.42, -18.84) * mm});
            skFitSpline(sketch, "E224", {"points": [v(-37.42, -18.84) * mm, v(-38.77, -21.52) * mm, v(-38.9, -21.92) * mm, v(-38.9, -23.77) * mm]});
            skFitSpline(sketch, "E225", {"points": [v(-38.9, -23.77) * mm, v(-38.92, -25.68) * mm, v(-38.89, -25.8) * mm, v(-38.26, -25.89) * mm]});
            skFitSpline(sketch, "E226", {"points": [v(-38.26, -25.89) * mm, v(-37.15, -26.04) * mm, v(-35.41, -23.9) * mm, v(-33.32, -19.79) * mm]});
            skFitSpline(sketch, "E227", {"points": [v(-33.32, -19.79) * mm, v(-31.1, -15.42) * mm, v(-30.3, -14.36) * mm, v(-29.2, -14.36) * mm]});
            skFitSpline(sketch, "E228", {"points": [v(-29.2, -14.36) * mm, v(-27.86, -14.36) * mm, v(-27.33, -15.61) * mm, v(-27.04, -19.52) * mm]});
            skFitSpline(sketch, "E229", {"points": [v(-27.04, -19.52) * mm, v(-26.87, -21.77) * mm, v(-26.73, -22.25) * mm, v(-25.97, -23.35) * mm]});
            skFitSpline(sketch, "E230", {"points": [v(-25.97, -23.35) * mm, v(-25.49, -24.04) * mm, v(-24.8, -24.91) * mm, v(-24.44, -25.28) * mm]});
            skFitSpline(sketch, "E231", {"points": [v(-24.44, -25.28) * mm, v(-24, -25.73) * mm, v(-23.85, -26.13) * mm, v(-23.97, -26.5) * mm]});
            skFitSpline(sketch, "E232", {"points": [v(-23.97, -26.5) * mm, v(-24.21, -27.27) * mm, v(-23.4, -28.52) * mm, v(-21.3, -30.58) * mm]});
            skFitSpline(sketch, "E233", {"points": [v(-21.3, -30.58) * mm, v(-20.36, -31.5) * mm, v(-19.6, -32.4) * mm, v(-19.6, -32.56) * mm]});
            skFitSpline(sketch, "E234", {"points": [v(-19.6, -32.56) * mm, v(-19.62, -32.96) * mm, v(-21.5, -34.12) * mm, v(-22.14, -34.12) * mm]});
            skFitSpline(sketch, "E235", {"points": [v(-22.14, -34.12) * mm, v(-22.43, -34.12) * mm, v(-22.74, -34.25) * mm, v(-22.84, -34.4) * mm]});
            skFitSpline(sketch, "E236", {"points": [v(-22.84, -34.4) * mm, v(-22.93, -34.55) * mm, v(-23.42, -34.68) * mm, v(-23.91, -34.68) * mm]});
            skFitSpline(sketch, "E237", {"points": [v(-23.91, -34.68) * mm, v(-24.4, -34.68) * mm, v(-25.7, -34.74) * mm, v(-26.79, -34.82) * mm]});
            skFitSpline(sketch, "E238", {"points": [v(-26.79, -34.82) * mm, v(-27.88, -34.9) * mm, v(-29.65, -34.83) * mm, v(-30.74, -34.67) * mm]});
            skFitSpline(sketch, "E239", {"points": [v(-30.74, -34.67) * mm, v(-32.4, -34.42) * mm, v(-32.92, -34.2) * mm, v(-33.99, -33.3) * mm]});
            skFitSpline(sketch, "E240", {"points": [v(-33.99, -33.3) * mm, v(-34.68, -32.7) * mm, v(-35.3, -32.04) * mm, v(-35.34, -31.8) * mm]});
            skFitSpline(sketch, "E241", {"points": [v(-35.34, -31.8) * mm, v(-35.39, -31.57) * mm, v(-34.53, -30.7) * mm, v(-33.32, -29.78) * mm]});
            skFitSpline(sketch, "E242", {"points": [v(-33.32, -29.78) * mm, v(-31.16, -28.13) * mm, v(-30.65, -27.47) * mm, v(-31.16, -26.96) * mm]});
            skFitSpline(sketch, "E243", {"points": [v(-31.16, -26.96) * mm, v(-31.6, -26.52) * mm, v(-31.5, -25.49) * mm, v(-31, -25.07) * mm]});
            skFitSpline(sketch, "E244", {"points": [v(-31, -25.07) * mm, v(-30.76, -24.87) * mm, v(-30.32, -24.23) * mm, v(-30.03, -23.66) * mm]});
            skFitSpline(sketch, "E245", {"points": [v(-30.03, -23.66) * mm, v(-29.73, -23.09) * mm, v(-29.28, -22.54) * mm, v(-29.02, -22.44) * mm]});
            skFitSpline(sketch, "E246", {"points": [v(-29.02, -22.44) * mm, v(-28.6, -22.28) * mm, v(-28.57, -21.97) * mm, v(-28.74, -20.07) * mm]});
            skFitSpline(sketch, "E247", {"points": [v(-28.74, -20.07) * mm, v(-28.97, -17.53) * mm, v(-29.16, -16.62) * mm, v(-29.47, -16.62) * mm]});
            skFitSpline(sketch, "E248", {"points": [v(-29.47, -16.62) * mm, v(-29.6, -16.62) * mm, v(-30.6, -18.38) * mm, v(-31.7, -20.53) * mm]});
            skFitSpline(sketch, "E249", {"points": [v(-31.7, -20.53) * mm, v(-33.91, -24.82) * mm, v(-35.18, -26.52) * mm, v(-36.83, -27.36) * mm]});
            skFitSpline(sketch, "E250", {"points": [v(-36.83, -27.36) * mm, v(-38.2, -28.06) * mm, v(-38.8, -28.05) * mm, v(-39.73, -27.33) * mm]});
            skFitSpline(sketch, "E251", {"points": [v(-39.73, -27.33) * mm, v(-41.56, -25.89) * mm, v(-41.33, -22.83) * mm, v(-39.03, -18.07) * mm]});
            skFitSpline(sketch, "E252", {"points": [v(-39.03, -18.07) * mm, v(-38.25, -16.47) * mm, v(-37.66, -15.12) * mm, v(-37.7, -15.09) * mm]});
            skFitSpline(sketch, "E253", {"points": [v(-37.7, -15.09) * mm, v(-37.76, -15.05) * mm, v(-38.27, -14.74) * mm, v(-38.84, -14.4) * mm]});
            skFitSpline(sketch, "E254", {"points": [v(-38.84, -14.4) * mm, v(-40.24, -13.56) * mm, v(-43.5, -10.01) * mm, v(-44.67, -8.06) * mm]});
            skFitSpline(sketch, "E255", {"points": [v(-44.67, -8.06) * mm, v(-46.84, -4.43) * mm, v(-47.82, -0.62) * mm, v(-47.82, 4.27) * mm]});
            skFitSpline(sketch, "E256", {"points": [v(-47.82, 4.27) * mm, v(-47.82, 7.67) * mm, v(-47.3, 10.55) * mm, v(-46.26, 12.9) * mm]});
            skLineSegment(sketch, "E257", {"start": v(-46.26, 12.9) * mm, "end": v(-45.62, 14.36) * mm});
            skLineSegment(sketch, "E258", {"start": v(-45.62, 14.36) * mm, "end": v(-46.79, 13.69) * mm});
            skFitSpline(sketch, "E259", {"points": [v(-46.79, 13.69) * mm, v(-47.43, 13.32) * mm, v(-48.12, 13.02) * mm, v(-48.32, 13.02) * mm]});
            skFitSpline(sketch, "E260", {"points": [v(-48.32, 13.02) * mm, v(-49, 13) * mm, v(-49.17, 14.24) * mm, v(-48.77, 16.4) * mm]});
            skFitSpline(sketch, "E261", {"points": [v(-48.77, 16.4) * mm, v(-48.27, 19.12) * mm, v(-48.02, 19.67) * mm, v(-46.95, 20.32) * mm]});
            skFitSpline(sketch, "E262", {"points": [v(-46.95, 20.32) * mm, v(-46.43, 20.64) * mm, v(-46.2, 20.93) * mm, v(-46.38, 21.04) * mm]});
            skFitSpline(sketch, "E263", {"points": [v(-46.38, 21.04) * mm, v(-46.83, 21.32) * mm, v(-46.75, 22.8) * mm, v(-46.22, 23.82) * mm]});
            skFitSpline(sketch, "E264", {"points": [v(-46.22, 23.82) * mm, v(-45.46, 25.31) * mm, v(-43.6, 27.38) * mm, v(-42.35, 28.1) * mm]});
            skFitSpline(sketch, "E265", {"points": [v(-42.35, 28.1) * mm, v(-41.61, 28.53) * mm, v(-40.5, 28.85) * mm, v(-39.35, 28.96) * mm]});
            skFitSpline(sketch, "E266", {"points": [v(-39.35, 28.96) * mm, v(-37.05, 29.19) * mm, v(-36.03, 29.57) * mm, v(-35.8, 30.28) * mm]});
            skFitSpline(sketch, "E267", {"points": [v(-35.8, 30.28) * mm, v(-35.52, 31.17) * mm, v(-35.81, 31.16) * mm, v(-37.44, 30.25) * mm]});
            skFitSpline(sketch, "E268", {"points": [v(-37.44, 30.25) * mm, v(-39.32, 29.18) * mm, v(-40.27, 29.16) * mm, v(-42.22, 30.14) * mm]});
            skFitSpline(sketch, "E269", {"points": [v(-42.22, 30.14) * mm, v(-44.1, 31.09) * mm, v(-44.71, 31.6) * mm, v(-44.71, 32.2) * mm]});
            skFitSpline(sketch, "E270", {"points": [v(-44.71, 32.2) * mm, v(-44.71, 32.87) * mm, v(-43.6, 33.82) * mm, v(-42.32, 34.27) * mm]});
            skFitSpline(sketch, "E271", {"points": [v(-42.32, 34.27) * mm, v(-40.67, 34.84) * mm, v(-40.74, 35.27) * mm, v(-42.41, 34.93) * mm]});
            skFitSpline(sketch, "E272", {"points": [v(-42.41, 34.93) * mm, v(-44.12, 34.58) * mm, v(-45.2, 34.96) * mm, v(-46.41, 36.35) * mm]});
            skLineSegment(sketch, "E273", {"start": v(-46.41, 36.35) * mm, "end": v(-47.27, 37.32) * mm});
            skLineSegment(sketch, "E274", {"start": v(-47.27, 37.32) * mm, "end": v(-46.2, 38.05) * mm});
            skFitSpline(sketch, "E275", {"points": [v(-46.2, 38.05) * mm, v(-45.61, 38.44) * mm, v(-44.83, 39) * mm, v(-44.46, 39.3) * mm]});
            skFitSpline(sketch, "E276", {"points": [v(-44.46, 39.3) * mm, v(-43.58, 39.99) * mm, v(-42.14, 39.96) * mm, v(-40.73, 39.24) * mm]});
            skFitSpline(sketch, "E277", {"points": [v(-40.73, 39.24) * mm, v(-40.1, 38.92) * mm, v(-39.44, 38.71) * mm, v(-39.26, 38.77) * mm]});
            skFitSpline(sketch, "E278", {"points": [v(-39.26, 38.77) * mm, v(-39.07, 38.83) * mm, v(-39.52, 39.15) * mm, v(-40.24, 39.47) * mm]});
            skFitSpline(sketch, "E279", {"points": [v(-40.24, 39.47) * mm, v(-41.36, 39.96) * mm, v(-42.17, 40.76) * mm, v(-42.17, 41.35) * mm]});
            skFitSpline(sketch, "E280", {"points": [v(-42.17, 41.35) * mm, v(-42.17, 41.6) * mm, v(-39.41, 42.93) * mm, v(-38.9, 42.93) * mm]});
            skFitSpline(sketch, "E281", {"points": [v(-38.9, 42.93) * mm, v(-38.64, 42.93) * mm, v(-38.26, 43.15) * mm, v(-38.07, 43.42) * mm]});
            skFitSpline(sketch, "E282", {"points": [v(-38.07, 43.42) * mm, v(-37.73, 43.87) * mm, v(-37.65, 43.88) * mm, v(-36.72, 43.43) * mm]});
            skFitSpline(sketch, "E283", {"points": [v(-36.72, 43.43) * mm, v(-36, 43.09) * mm, v(-35.64, 42.68) * mm, v(-35.4, 41.89) * mm]});
            skFitSpline(sketch, "E284", {"points": [v(-35.4, 41.89) * mm, v(-34.93, 40.43) * mm, v(-34.34, 39.54) * mm, v(-33.84, 39.54) * mm]});
            skFitSpline(sketch, "E285", {"points": [v(-33.84, 39.54) * mm, v(-33.23, 39.54) * mm, v(-33.33, 40.05) * mm, v(-34.13, 41) * mm]});
            skFitSpline(sketch, "E286", {"points": [v(-34.13, 41) * mm, v(-35.06, 42.1) * mm, v(-35.02, 42.53) * mm, v(-33.94, 42.9) * mm]});
            skFitSpline(sketch, "E287", {"points": [v(-33.94, 42.9) * mm, v(-31.9, 43.61) * mm, v(-30.7, 43.26) * mm, v(-26.8, 40.86) * mm]});
            skFitSpline(sketch, "E288", {"points": [v(-26.8, 40.86) * mm, v(-25.38, 39.98) * mm, v(-24.88, 39.82) * mm, v(-23.5, 39.82) * mm]});
            skFitSpline(sketch, "E289", {"points": [v(-23.5, 39.82) * mm, v(-22.04, 39.82) * mm, v(-21.7, 39.95) * mm, v(-19.96, 41.15) * mm]});
            skFitSpline(sketch, "E290", {"points": [v(-19.96, 41.15) * mm, v(-18.9, 41.87) * mm, v(-17.55, 42.75) * mm, v(-16.96, 43.09) * mm]});
            skLineSegment(sketch, "E291", {"start": v(-16.96, 43.09) * mm, "end": v(-15.87, 43.7) * mm});
            skLineSegment(sketch, "E292", {"start": v(-15.87, 43.7) * mm, "end": v(-16.73, 44.14) * mm});
            skFitSpline(sketch, "E293", {"points": [v(-16.73, 44.14) * mm, v(-17.46, 44.5) * mm, v(-17.66, 44.5) * mm, v(-18.1, 44.18) * mm]});
            skFitSpline(sketch, "E294", {"points": [v(-18.1, 44.18) * mm, v(-19.32, 43.25) * mm, v(-22.13, 44.05) * mm, v(-22.13, 45.33) * mm]});
            skFitSpline(sketch, "E295", {"points": [v(-22.13, 45.33) * mm, v(-22.13, 45.98) * mm, v(-22.24, 46.03) * mm, v(-23.43, 46.03) * mm]});
            skFitSpline(sketch, "E296", {"points": [v(-23.43, 46.03) * mm, v(-25.2, 46.03) * mm, v(-26.4, 46.67) * mm, v(-27.47, 48.15) * mm]});
            skFitSpline(sketch, "E297", {"points": [v(-27.47, 48.15) * mm, v(-28, 48.9) * mm, v(-28.95, 49.7) * mm, v(-29.83, 50.18) * mm]});
            skFitSpline(sketch, "E298", {"points": [v(-29.83, 50.18) * mm, v(-31.36, 51) * mm, v(-31.55, 51.27) * mm, v(-33.26, 55.05) * mm]});
            skFitSpline(sketch, "E299", {"points": [v(-33.26, 55.05) * mm, v(-33.65, 55.9) * mm, v(-33.9, 56.65) * mm, v(-33.84, 56.71) * mm]});
            skFitSpline(sketch, "E300", {"points": [v(-33.84, 56.71) * mm, v(-33.64, 56.92) * mm, v(-31.9, 54.95) * mm, v(-31.02, 53.5) * mm]});
            skFitSpline(sketch, "E301", {"points": [v(-31.02, 53.5) * mm, v(-30.33, 52.36) * mm, v(-29.92, 52.02) * mm, v(-28.77, 51.6) * mm]});
            skFitSpline(sketch, "E302", {"points": [v(-28.77, 51.6) * mm, v(-27.93, 51.3) * mm, v(-26.93, 50.63) * mm, v(-26.3, 49.97) * mm]});
            skFitSpline(sketch, "E303", {"points": [v(-26.3, 49.97) * mm, v(-25.18, 48.77) * mm, v(-24.13, 48.4) * mm, v(-24.66, 49.4) * mm]});
            skFitSpline(sketch, "E304", {"points": [v(-24.66, 49.4) * mm, v(-25.04, 50.1) * mm, v(-25.04, 50.14) * mm, v(-24.51, 50.67) * mm]});
            skFitSpline(sketch, "E305", {"points": [v(-24.51, 50.67) * mm, v(-24.2, 50.97) * mm, v(-23.54, 51.11) * mm, v(-22.4, 51.11) * mm]});
            skFitSpline(sketch, "E306", {"points": [v(-22.4, 51.11) * mm, v(-20.92, 51.11) * mm, v(-20.72, 51.18) * mm, v(-20.72, 51.67) * mm]});
            skFitSpline(sketch, "E307", {"points": [v(-20.72, 51.67) * mm, v(-20.72, 52.92) * mm, v(-17.87, 52.63) * mm, v(-15.18, 51.1) * mm]});
            skFitSpline(sketch, "E308", {"points": [v(-15.18, 51.1) * mm, v(-13.68, 50.23) * mm, v(-12.93, 50.03) * mm, v(-13.27, 50.59) * mm]});
            skFitSpline(sketch, "E309", {"points": [v(-13.27, 50.59) * mm, v(-13.6, 51.12) * mm, v(-13.45, 52.44) * mm, v(-13, 53.14) * mm]});
            skFitSpline(sketch, "E310", {"points": [v(-13, 53.14) * mm, v(-12.7, 53.59) * mm, v(-12.65, 53.93) * mm, v(-12.83, 54.22) * mm]});
            skFitSpline(sketch, "E311", {"points": [v(-12.83, 54.22) * mm, v(-13.48, 55.25) * mm, v(-13.11, 56) * mm, v(-10.98, 58.08) * mm]});
            skFitSpline(sketch, "E312", {"points": [v(-10.98, 58.08) * mm, v(-8.6, 60.39) * mm, v(-7.97, 60.57) * mm, v(-5.41, 59.7) * mm]});
            skFitSpline(sketch, "E313", {"points": [v(-5.41, 59.7) * mm, v(-4.44, 59.37) * mm, v(-3.97, 59.33) * mm, v(-3.54, 59.56) * mm]});
            skFitSpline(sketch, "E314", {"points": [v(-3.54, 59.56) * mm, v(-2.75, 59.98) * mm, v(-1.65, 59.93) * mm, v(-0.67, 59.43) * mm]});
            skFitSpline(sketch, "E315", {"points": [v(-0.67, 59.43) * mm, v(0.11, 59.03) * mm, v(0.22, 59.04) * mm, v(1.28, 59.75) * mm]});
            skFitSpline(sketch, "E316", {"points": [v(1.28, 59.75) * mm, v(3.58, 61.27) * mm, v(6.53, 60.48) * mm, v(8.82, 57.71) * mm]});
            skFitSpline(sketch, "E317", {"points": [v(8.82, 57.71) * mm, v(9.41, 57) * mm, v(10.22, 56.1) * mm, v(10.6, 55.74) * mm]});
            skFitSpline(sketch, "E318", {"points": [v(10.6, 55.74) * mm, v(11, 55.36) * mm, v(11.6, 54.79) * mm, v(11.94, 54.46) * mm]});
            skFitSpline(sketch, "E319", {"points": [v(11.94, 54.46) * mm, v(12.29, 54.13) * mm, v(12.64, 53.46) * mm, v(12.74, 52.97) * mm]});
            skFitSpline(sketch, "E320", {"points": [v(12.74, 52.97) * mm, v(12.84, 52.4) * mm, v(13.19, 51.92) * mm, v(13.73, 51.61) * mm]});
            skFitSpline(sketch, "E321", {"points": [v(13.73, 51.61) * mm, v(14.5, 51.17) * mm, v(14.62, 51.17) * mm, v(15.81, 51.7) * mm]});
            skFitSpline(sketch, "E322", {"points": [v(15.81, 51.7) * mm, v(17.1, 52.27) * mm, v(18.31, 52.21) * mm, v(18.72, 51.57) * mm]});
            skFitSpline(sketch, "E323", {"points": [v(18.72, 51.57) * mm, v(18.92, 51.26) * mm, v(20.89, 50.62) * mm, v(22.52, 50.34) * mm]});
            skFitSpline(sketch, "E324", {"points": [v(22.52, 50.34) * mm, v(23.03, 50.25) * mm, v(23.73, 50.46) * mm, v(24.6, 50.97) * mm]});
            skFitSpline(sketch, "E325", {"points": [v(24.6, 50.97) * mm, v(25.72, 51.63) * mm, v(26.11, 51.71) * mm, v(27.25, 51.56) * mm]});
            skFitSpline(sketch, "E326", {"points": [v(27.25, 51.56) * mm, v(28, 51.46) * mm, v(28.8, 51.46) * mm, v(29.04, 51.55) * mm]});
            skFitSpline(sketch, "E327", {"points": [v(29.04, 51.55) * mm, v(29.28, 51.65) * mm, v(29.82, 52.61) * mm, v(30.24, 53.7) * mm]});
            skFitSpline(sketch, "E328", {"points": [v(30.24, 53.7) * mm, v(31, 55.7) * mm, v(31.8, 56.46) * mm, v(32.74, 56.1) * mm]});
            skFitSpline(sketch, "E329", {"points": [v(32.74, 56.1) * mm, v(33.4, 55.85) * mm, v(33.3, 54.78) * mm, v(32.64, 54.78) * mm]});
            skFitSpline(sketch, "E330", {"points": [v(32.64, 54.78) * mm, v(32.24, 54.78) * mm, v(31.94, 54.37) * mm, v(31.5, 53.2) * mm]});
            skFitSpline(sketch, "E331", {"points": [v(31.5, 53.2) * mm, v(30.33, 50.06) * mm, v(30.26, 49.98) * mm, v(28.5, 49.98) * mm]});
            skFitSpline(sketch, "E332", {"points": [v(28.5, 49.98) * mm, v(26.65, 49.98) * mm, v(26.03, 49.7) * mm, v(24.72, 48.22) * mm]});
            skFitSpline(sketch, "E333", {"points": [v(24.72, 48.22) * mm, v(23.91, 47.31) * mm, v(23.5, 47.08) * mm, v(22.45, 46.96) * mm]});
            skFitSpline(sketch, "E334", {"points": [v(22.45, 46.96) * mm, v(21.4, 46.85) * mm, v(21.08, 46.66) * mm, v(20.7, 46.01) * mm]});
            skFitSpline(sketch, "E335", {"points": [v(20.7, 46.01) * mm, v(20.1, 44.98) * mm, v(19.11, 44.74) * mm, v(17.21, 45.17) * mm]});
            skFitSpline(sketch, "E336", {"points": [v(17.21, 45.17) * mm, v(15.97, 45.44) * mm, v(15.6, 45.44) * mm, v(15.14, 45.12) * mm]});
            skFitSpline(sketch, "E337", {"points": [v(15.14, 45.12) * mm, v(14.63, 44.76) * mm, v(14.73, 44.64) * mm, v(16.82, 43.26) * mm]});
            skFitSpline(sketch, "E338", {"points": [v(16.82, 43.26) * mm, v(18.95, 41.85) * mm, v(20.43, 40.38) * mm, v(23.1, 37) * mm]});
            skFitSpline(sketch, "E339", {"points": [v(23.1, 37) * mm, v(24.97, 34.63) * mm, v(25.86, 34.77) * mm, v(27.52, 37.72) * mm]});
            skFitSpline(sketch, "E340", {"points": [v(27.52, 37.72) * mm, v(28.2, 38.94) * mm, v(28.59, 39.3) * mm, v(29.67, 39.7) * mm]});
            skFitSpline(sketch, "E341", {"points": [v(29.67, 39.7) * mm, v(31.15, 40.27) * mm, v(31.46, 40.08) * mm, v(31.5, 38.55) * mm]});
            skFitSpline(sketch, "E342", {"points": [v(31.5, 38.55) * mm, v(31.52, 37.82) * mm, v(31.56, 37.78) * mm, v(31.77, 38.27) * mm]});
            skFitSpline(sketch, "E343", {"points": [v(31.77, 38.27) * mm, v(31.9, 38.58) * mm, v(32.1, 39.3) * mm, v(32.18, 39.87) * mm]});
            skFitSpline(sketch, "E344", {"points": [v(32.18, 39.87) * mm, v(32.28, 40.43) * mm, v(32.6, 41.21) * mm, v(32.9, 41.6) * mm]});
            skFitSpline(sketch, "E345", {"points": [v(32.9, 41.6) * mm, v(33.49, 42.34) * mm, v(35.16, 43.1) * mm, v(35.16, 42.63) * mm]});
            skFitSpline(sketch, "E346", {"points": [v(35.16, 42.63) * mm, v(35.16, 42.48) * mm, v(35.05, 42.36) * mm, v(34.92, 42.36) * mm]});
            skFitSpline(sketch, "E347", {"points": [v(34.92, 42.36) * mm, v(34.79, 42.36) * mm, v(34.8, 41.63) * mm, v(34.93, 40.74) * mm]});
            skFitSpline(sketch, "E348", {"points": [v(34.93, 40.74) * mm, v(35.07, 39.85) * mm, v(35.13, 38.92) * mm, v(35.07, 38.67) * mm]});
            skFitSpline(sketch, "E349", {"points": [v(35.07, 38.67) * mm, v(34.97, 38.28) * mm, v(35.11, 38.26) * mm, v(36.11, 38.47) * mm]});
            skFitSpline(sketch, "E350", {"points": [v(36.11, 38.47) * mm, v(37.52, 38.78) * mm, v(37.84, 38.8) * mm, v(39.13, 38.74) * mm]});
            skLineSegment(sketch, "E351", {"start": v(39.13, 38.74) * mm, "end": v(40.14, 38.7) * mm});
            skLineSegment(sketch, "E352", {"start": v(40.14, 38.7) * mm, "end": v(39.95, 37.35) * mm});
            skFitSpline(sketch, "E353", {"points": [v(39.95, 37.35) * mm, v(39.84, 36.62) * mm, v(39.66, 35.8) * mm, v(39.55, 35.55) * mm]});
            skFitSpline(sketch, "E354", {"points": [v(39.55, 35.55) * mm, v(39.44, 35.3) * mm, v(39.49, 35) * mm, v(39.65, 34.9) * mm]});
            skFitSpline(sketch, "E355", {"points": [v(39.65, 34.9) * mm, v(39.85, 34.78) * mm, v(39.8, 34.47) * mm, v(39.48, 34) * mm]});
            skFitSpline(sketch, "E356", {"points": [v(39.48, 34) * mm, v(39.23, 33.6) * mm, v(38.98, 32.95) * mm, v(38.94, 32.53) * mm]});
            skFitSpline(sketch, "E357", {"points": [v(38.94, 32.53) * mm, v(38.82, 31.31) * mm, v(38.34, 29.68) * mm, v(37.99, 29.25) * mm]});
            skFitSpline(sketch, "E358", {"points": [v(37.99, 29.25) * mm, v(37.8, 29.03) * mm, v(37.38, 28.8) * mm, v(37.04, 28.73) * mm]});
            skFitSpline(sketch, "E359", {"points": [v(37.04, 28.73) * mm, v(36.65, 28.65) * mm, v(36.78, 28.6) * mm, v(37.4, 28.57) * mm]});
            skFitSpline(sketch, "E360", {"points": [v(37.4, 28.57) * mm, v(38.63, 28.52) * mm, v(40.29, 27.39) * mm, v(40.96, 26.14) * mm]});
            skFitSpline(sketch, "E361", {"points": [v(40.96, 26.14) * mm, v(41.4, 25.34) * mm, v(41.42, 25.06) * mm, v(41.13, 24.44) * mm]});
            skFitSpline(sketch, "E362", {"points": [v(41.13, 24.44) * mm, v(40.83, 23.78) * mm, v(40.88, 23.59) * mm, v(41.5, 22.84) * mm]});
            skFitSpline(sketch, "E363", {"points": [v(41.5, 22.84) * mm, v(41.9, 22.38) * mm, v(42.21, 21.77) * mm, v(42.21, 21.48) * mm]});
            skFitSpline(sketch, "E364", {"points": [v(42.21, 21.48) * mm, v(42.21, 21.2) * mm, v(42.6, 20.58) * mm, v(43.06, 20.11) * mm]});
            skFitSpline(sketch, "E365", {"points": [v(43.06, 20.11) * mm, v(43.98, 19.19) * mm, v(44.15, 18.1) * mm, v(43.57, 16.82) * mm]});
            skFitSpline(sketch, "E366", {"points": [v(43.57, 16.82) * mm, v(43.32, 16.27) * mm, v(43.09, 16.12) * mm, v(42.65, 16.24) * mm]});
            skFitSpline(sketch, "E367", {"points": [v(42.65, 16.24) * mm, v(42.33, 16.32) * mm, v(41.84, 16.4) * mm, v(41.57, 16.4) * mm]});
            skFitSpline(sketch, "E368", {"points": [v(41.57, 16.4) * mm, v(41.29, 16.4) * mm, v(40.75, 16.71) * mm, v(40.37, 17.1) * mm]});
            skFitSpline(sketch, "E369", {"points": [v(40.37, 17.1) * mm, v(39.72, 17.74) * mm, v(39.67, 17.75) * mm, v(39.67, 17.22) * mm]});
            skFitSpline(sketch, "E370", {"points": [v(39.67, 17.22) * mm, v(39.67, 16.14) * mm, v(40.62, 14.85) * mm, v(43.91, 11.43) * mm]});
            skFitSpline(sketch, "E371", {"points": [v(43.91, 11.43) * mm, v(46.36, 8.89) * mm, v(47.47, 7.5) * mm, v(48.14, 6.13) * mm]});
            skFitSpline(sketch, "E372", {"points": [v(48.14, 6.13) * mm, v(49.04, 4.3) * mm, v(49.06, 4.23) * mm, v(48.93, 1.1) * mm]});
            skFitSpline(sketch, "E373", {"points": [v(48.93, 1.1) * mm, v(48.78, -2.55) * mm, v(48.25, -4.1) * mm, v(45.5, -8.95) * mm]});
            skFitSpline(sketch, "E374", {"points": [v(45.5, -8.95) * mm, v(44.64, -10.45) * mm, v(43.79, -12.32) * mm, v(43.6, -13.1) * mm]});
            skFitSpline(sketch, "E375", {"points": [v(43.6, -13.1) * mm, v(43.15, -14.95) * mm, v(42.86, -15.5) * mm, v(42.3, -15.5) * mm]});
            skFitSpline(sketch, "E376", {"points": [v(42.3, -15.5) * mm, v(41.62, -15.5) * mm, v(39.37, -14.35) * mm, v(39.2, -13.93) * mm]});
            skFitSpline(sketch, "E377", {"points": [v(39.2, -13.93) * mm, v(39.11, -13.69) * mm, v(38.74, -13.93) * mm, v(38.11, -14.62) * mm]});
            skLineSegment(sketch, "E378", {"start": v(38.11, -14.62) * mm, "end": v(37.16, -15.67) * mm});
            skLineSegment(sketch, "E379", {"start": v(37.16, -15.67) * mm, "end": v(38.44, -18.23) * mm});
            skFitSpline(sketch, "E380", {"points": [v(38.44, -18.23) * mm, v(40.9, -23.17) * mm, v(40.77, -27.13) * mm, v(38.14, -27.8) * mm]});
            skFitSpline(sketch, "E381", {"points": [v(38.14, -27.8) * mm, v(37.68, -27.9) * mm, v(36.97, -27.74) * mm, v(36.12, -27.33) * mm]});
            skFitSpline(sketch, "E382", {"points": [v(36.12, -27.33) * mm, v(34.44, -26.52) * mm, v(32.82, -24.34) * mm, v(30.6, -19.9) * mm]});
            skFitSpline(sketch, "E383", {"points": [v(30.6, -19.9) * mm, v(28.63, -16) * mm, v(28.35, -15.96) * mm, v(28.16, -19.57) * mm]});
            skFitSpline(sketch, "E384", {"points": [v(28.16, -19.57) * mm, v(28.04, -21.83) * mm, v(28.07, -22) * mm, v(28.77, -22.84) * mm]});
            skFitSpline(sketch, "E385", {"points": [v(28.77, -22.84) * mm, v(29.18, -23.32) * mm, v(29.51, -23.88) * mm, v(29.51, -24.08) * mm]});
            skFitSpline(sketch, "E386", {"points": [v(29.51, -24.08) * mm, v(29.51, -24.27) * mm, v(29.77, -24.67) * mm, v(30.08, -24.95) * mm]});
            skFitSpline(sketch, "E387", {"points": [v(30.08, -24.95) * mm, v(30.7, -25.5) * mm, v(30.8, -26.25) * mm, v(30.37, -27.05) * mm]});
            skFitSpline(sketch, "E388", {"points": [v(30.37, -27.05) * mm, v(30.14, -27.47) * mm, v(30.32, -27.78) * mm, v(31.32, -28.7) * mm]});
            skFitSpline(sketch, "E389", {"points": [v(31.32, -28.7) * mm, v(32, -29.32) * mm, v(33.06, -30.17) * mm, v(33.7, -30.6) * mm]});
            skFitSpline(sketch, "E390", {"points": [v(33.7, -30.6) * mm, v(35.01, -31.46) * mm, v(34.99, -31.7) * mm, v(33.42, -33.23) * mm]});
            skFitSpline(sketch, "E391", {"points": [v(33.42, -33.23) * mm, v(32.18, -34.44) * mm, v(30.8, -34.78) * mm, v(27.11, -34.77) * mm]});
            skFitSpline(sketch, "E392", {"points": [v(27.11, -34.77) * mm, v(22.86, -34.76) * mm, v(22.52, -34.73) * mm, v(22.32, -34.4) * mm]});
            skFitSpline(sketch, "E393", {"points": [v(22.32, -34.4) * mm, v(22.22, -34.25) * mm, v(21.8, -34.12) * mm, v(21.38, -34.11) * mm]});
            skFitSpline(sketch, "E394", {"points": [v(21.38, -34.11) * mm, v(20.97, -34.1) * mm, v(20.18, -33.74) * mm, v(19.64, -33.3) * mm]});
            skLineSegment(sketch, "E395", {"start": v(19.64, -33.3) * mm, "end": v(18.66, -32.48) * mm});
            skLineSegment(sketch, "E396", {"start": v(18.66, -32.48) * mm, "end": v(20.98, -30.06) * mm});
            skFitSpline(sketch, "E397", {"points": [v(20.98, -30.06) * mm, v(23.1, -27.85) * mm, v(23.3, -27.54) * mm, v(23.3, -26.51) * mm]});
            skFitSpline(sketch, "E398", {"points": [v(23.3, -26.51) * mm, v(23.3, -25.65) * mm, v(23.46, -25.28) * mm, v(23.94, -24.97) * mm]});
            skFitSpline(sketch, "E399", {"points": [v(23.94, -24.97) * mm, v(24.29, -24.74) * mm, v(24.82, -24.1) * mm, v(25.11, -23.55) * mm]});
            skFitSpline(sketch, "E400", {"points": [v(25.11, -23.55) * mm, v(25.4, -23) * mm, v(25.75, -22.55) * mm, v(25.86, -22.55) * mm]});
            skFitSpline(sketch, "E401", {"points": [v(25.86, -22.55) * mm, v(25.98, -22.55) * mm, v(26.16, -21.44) * mm, v(26.27, -20.08) * mm]});
            skFitSpline(sketch, "E402", {"points": [v(26.27, -20.08) * mm, v(26.59, -15.9) * mm, v(27.2, -14.36) * mm, v(28.54, -14.36) * mm]});
            skFitSpline(sketch, "E403", {"points": [v(28.54, -14.36) * mm, v(29.5, -14.36) * mm, v(30.75, -16) * mm, v(32.49, -19.5) * mm]});
            skFitSpline(sketch, "E404", {"points": [v(32.49, -19.5) * mm, v(34.81, -24.17) * mm, v(36.24, -25.93) * mm, v(37.68, -25.93) * mm]});
            skFitSpline(sketch, "E405", {"points": [v(37.68, -25.93) * mm, v(39.11, -25.93) * mm, v(38.59, -22.45) * mm, v(36.56, -18.5) * mm]});
            skFitSpline(sketch, "E406", {"points": [v(36.56, -18.5) * mm, v(35.24, -15.94) * mm, v(35.22, -15.92) * mm, v(34.2, -15.95) * mm]});
            skLineSegment(sketch, "E407", {"start": v(34.2, -15.95) * mm, "end": v(33.18, -15.98) * mm});
            skLineSegment(sketch, "E408", {"start": v(33.18, -15.98) * mm, "end": v(33.18, -14.39) * mm});
            skFitSpline(sketch, "E409", {"points": [v(33.18, -14.39) * mm, v(33.18, -12.44) * mm, v(33.61, -11.76) * mm, v(35.44, -10.84) * mm]});
            skFitSpline(sketch, "E410", {"points": [v(35.44, -10.84) * mm, v(36.95, -10.07) * mm, v(37.44, -9.57) * mm, v(36.67, -9.57) * mm]});
            skFitSpline(sketch, "E411", {"points": [v(36.67, -9.57) * mm, v(36.4, -9.57) * mm, v(35.46, -10.07) * mm, v(34.58, -10.68) * mm]});
            skFitSpline(sketch, "E412", {"points": [v(34.58, -10.68) * mm, v(31.01, -13.18) * mm, v(26.95, -12.83) * mm, v(23.76, -9.72) * mm]});
            skLineSegment(sketch, "E413", {"start": v(23.76, -9.72) * mm, "end": v(22.54, -8.54) * mm});
            skLineSegment(sketch, "E414", {"start": v(22.54, -8.54) * mm, "end": v(22.34, -14.6) * mm});
            skFitSpline(sketch, "E415", {"points": [v(22.34, -14.6) * mm, v(22.23, -17.94) * mm, v(21.96, -21.65) * mm, v(21.73, -22.84) * mm]});
            skFitSpline(sketch, "E416", {"points": [v(21.73, -22.84) * mm, v(19.98, -32.11) * mm, v(14.68, -38.33) * mm, v(6.24, -41.07) * mm]});
            skLineSegment(sketch, "E417", {"start": v(6.24, -41.07) * mm, "end": v(4.25, -41.71) * mm});
            skLineSegment(sketch, "E418", {"start": v(4.25, -41.71) * mm, "end": v(5.67, -41.72) * mm});
            skFitSpline(sketch, "E419", {"points": [v(5.67, -41.72) * mm, v(7.5, -41.74) * mm, v(8.76, -41.38) * mm, v(12.02, -39.88) * mm]});
            skFitSpline(sketch, "E420", {"points": [v(12.02, -39.88) * mm, v(17.05, -37.58) * mm, v(19.5, -37.33) * mm, v(21.1, -38.93) * mm]});
            skFitSpline(sketch, "E421", {"points": [v(21.1, -38.93) * mm, v(22.11, -39.94) * mm, v(21.93, -40.33) * mm, v(20.47, -40.33) * mm]});
            skFitSpline(sketch, "E422", {"points": [v(20.47, -40.33) * mm, v(19.24, -40.33) * mm, v(19.15, -40.47) * mm, v(19.78, -41.37) * mm]});
            skFitSpline(sketch, "E423", {"points": [v(19.78, -41.37) * mm, v(20.43, -42.3) * mm, v(24.15, -42.92) * mm, v(26.04, -42.41) * mm]});
            skLineSegment(sketch, "E424", {"start": v(26.04, -42.41) * mm, "end": v(26.66, -42.25) * mm});
            skLineSegment(sketch, "E425", {"start": v(26.66, -42.25) * mm, "end": v(25.93, -40.77) * mm});
            skFitSpline(sketch, "E426", {"points": [v(25.93, -40.77) * mm, v(25.23, -39.34) * mm, v(25.23, -39.26) * mm, v(25.7, -38.55) * mm]});
            skFitSpline(sketch, "E427", {"points": [v(25.7, -38.55) * mm, v(26.4, -37.48) * mm, v(28.29, -36.66) * mm, v(30.05, -36.66) * mm]});
            skFitSpline(sketch, "E428", {"points": [v(30.05, -36.66) * mm, v(31.36, -36.66) * mm, v(31.66, -36.77) * mm, v(32.47, -37.58) * mm]});
            skFitSpline(sketch, "E429", {"points": [v(32.47, -37.58) * mm, v(33.42, -38.54) * mm, v(33.47, -38.67) * mm, v(34.45, -43.86) * mm]});
            skFitSpline(sketch, "E430", {"points": [v(34.45, -43.86) * mm, v(35.13, -47.43) * mm, v(37.08, -50.75) * mm, v(38.87, -51.4) * mm]});
            skFitSpline(sketch, "E431", {"points": [v(38.87, -51.4) * mm, v(39.46, -51.62) * mm, v(37.22, -53.8) * mm, v(35.58, -54.59) * mm]});
            skFitSpline(sketch, "E432", {"points": [v(35.58, -54.59) * mm, v(32.4, -56.13) * mm, v(27.94, -56.12) * mm, v(21.33, -54.58) * mm]});
            skFitSpline(sketch, "E433", {"points": [v(21.33, -54.58) * mm, v(19.7, -54.2) * mm, v(17.77, -53.88) * mm, v(17.04, -53.88) * mm]});
            skFitSpline(sketch, "E434", {"points": [v(17.04, -53.88) * mm, v(14.79, -53.87) * mm, v(13.53, -54.78) * mm, v(14.48, -55.73) * mm]});
            skFitSpline(sketch, "E435", {"points": [v(14.48, -55.73) * mm, v(14.93, -56.18) * mm, v(15.86, -56.17) * mm, v(17.24, -55.7) * mm]});
            skFitSpline(sketch, "E436", {"points": [v(17.24, -55.7) * mm, v(17.7, -55.55) * mm, v(17.67, -55.62) * mm, v(17.1, -56.1) * mm]});
            skFitSpline(sketch, "E437", {"points": [v(17.1, -56.1) * mm, v(15.52, -57.4) * mm, v(12.34, -57.26) * mm, v(8.9, -55.7) * mm]});
            skFitSpline(sketch, "E438", {"points": [v(8.9, -55.7) * mm, v(6.86, -54.78) * mm, v(6.38, -54.67) * mm, v(4.84, -54.77) * mm]});
            skFitSpline(sketch, "E439", {"points": [v(4.84, -54.77) * mm, v(2.12, -54.94) * mm, v(0.83, -56.14) * mm, v(0.02, -59.24) * mm]});
            skLineSegment(sketch, "E440", {"start": v(0.02, -59.24) * mm, "end": v(-0.3, -60.5) * mm});
            skLineSegment(sketch, "E441", {"start": v(-0.3, -60.5) * mm, "end": v(-0.78, -58.9) * mm});
            skLineSegment(sketch, "E442", {"start": v(-0.78, -58.9) * mm, "end": v(-0.78, -58.9) * mm});
            skFitSpline(sketch, "E443", {"points": [v(1.1, -56) * mm, v(1.56, -55.36) * mm, v(1.6, -55.22) * mm, v(1.24, -55.35) * mm]});
            skFitSpline(sketch, "E444", {"points": [v(1.24, -55.35) * mm, v(0.9, -55.49) * mm, v(0.83, -55.39) * mm, v(0.94, -54.94) * mm]});
            skFitSpline(sketch, "E445", {"points": [v(0.94, -54.94) * mm, v(1.04, -54.57) * mm, v(0.99, -54.42) * mm, v(0.8, -54.53) * mm]});
            skFitSpline(sketch, "E446", {"points": [v(0.8, -54.53) * mm, v(0.64, -54.63) * mm, v(0.44, -54.45) * mm, v(0.36, -54.13) * mm]});
            skFitSpline(sketch, "E447", {"points": [v(0.36, -54.13) * mm, v(0.18, -53.46) * mm, v(-0.82, -53.48) * mm, v(-0.83, -54.16) * mm]});
            skFitSpline(sketch, "E448", {"points": [v(-0.83, -54.16) * mm, v(-0.84, -54.41) * mm, v(-1.05, -54.54) * mm, v(-1.36, -54.49) * mm]});
            skFitSpline(sketch, "E449", {"points": [v(-1.36, -54.49) * mm, v(-1.74, -54.42) * mm, v(-1.84, -54.52) * mm, v(-1.72, -54.84) * mm]});
            skFitSpline(sketch, "E450", {"points": [v(-1.72, -54.84) * mm, v(-1.6, -55.13) * mm, v(-1.7, -55.29) * mm, v(-1.98, -55.29) * mm]});
            skFitSpline(sketch, "E451", {"points": [v(-1.98, -55.29) * mm, v(-2.22, -55.29) * mm, v(-2.33, -55.41) * mm, v(-2.23, -55.57) * mm]});
            skFitSpline(sketch, "E452", {"points": [v(-2.23, -55.57) * mm, v(-2.14, -55.73) * mm, v(-1.93, -55.78) * mm, v(-1.79, -55.7) * mm]});
            skFitSpline(sketch, "E453", {"points": [v(-1.79, -55.7) * mm, v(-1.64, -55.6) * mm, v(-1.55, -55.63) * mm, v(-1.58, -55.76) * mm]});
            skFitSpline(sketch, "E454", {"points": [v(-1.58, -55.76) * mm, v(-1.62, -55.89) * mm, v(-1.42, -56.37) * mm, v(-1.15, -56.84) * mm]});
            skLineSegment(sketch, "E455", {"start": v(-1.15, -56.84) * mm, "end": v(-0.65, -57.68) * mm});
            skLineSegment(sketch, "E456", {"start": v(-0.65, -57.68) * mm, "end": v(-0.8, -56.7) * mm});
            skFitSpline(sketch, "E457", {"points": [v(-0.8, -56.7) * mm, v(-0.92, -56) * mm, v(-0.89, -55.83) * mm, v(-0.69, -56.13) * mm]});
            skFitSpline(sketch, "E458", {"points": [v(-0.69, -56.13) * mm, v(-0.47, -56.47) * mm, v(-0.4, -56.41) * mm, v(-0.39, -55.85) * mm]});
            skLineSegment(sketch, "E459", {"start": v(-0.39, -55.85) * mm, "end": v(-0.37, -55.14) * mm});
            skLineSegment(sketch, "E460", {"start": v(-0.37, -55.14) * mm, "end": v(-0.1, -55.8) * mm});
            skFitSpline(sketch, "E461", {"points": [v(-0.1, -55.8) * mm, v(0.04, -56.16) * mm, v(0.1, -56.8) * mm, v(0, -57.21) * mm]});
            skFitSpline(sketch, "E462", {"points": [v(0, -57.21) * mm, v(-0.14, -57.9) * mm, v(-0.13, -57.92) * mm, v(0.19, -57.4) * mm]});
            skFitSpline(sketch, "E463", {"points": [v(0.19, -57.4) * mm, v(0.38, -57.1) * mm, v(0.8, -56.47) * mm, v(1.1, -56) * mm]});
            skFitSpline(sketch, "E464", {"points": [v(-36.39, -52.73) * mm, v(-36.45, -52.42) * mm, v(-36.25, -52.02) * mm, v(-35.92, -51.8) * mm]});
            skFitSpline(sketch, "E465", {"points": [v(-35.92, -51.8) * mm, v(-35.56, -51.54) * mm, v(-35.47, -51.32) * mm, v(-35.66, -51.2) * mm]});
            skFitSpline(sketch, "E466", {"points": [v(-35.66, -51.2) * mm, v(-35.83, -51.1) * mm, v(-35.9, -50.9) * mm, v(-35.83, -50.78) * mm]});
            skFitSpline(sketch, "E467", {"points": [v(-35.83, -50.78) * mm, v(-35.75, -50.66) * mm, v(-35.88, -50.4) * mm, v(-36.1, -50.2) * mm]});
            skFitSpline(sketch, "E468", {"points": [v(-36.1, -50.2) * mm, v(-36.34, -50.01) * mm, v(-36.53, -49.97) * mm, v(-36.53, -50.1) * mm]});
            skFitSpline(sketch, "E469", {"points": [v(-36.53, -50.1) * mm, v(-36.53, -50.24) * mm, v(-36.64, -50.17) * mm, v(-36.78, -49.96) * mm]});
            skFitSpline(sketch, "E470", {"points": [v(-36.78, -49.96) * mm, v(-36.96, -49.67) * mm, v(-37.14, -49.78) * mm, v(-37.53, -50.44) * mm]});
            skFitSpline(sketch, "E471", {"points": [v(-37.53, -50.44) * mm, v(-37.81, -50.92) * mm, v(-38.11, -51.26) * mm, v(-38.2, -51.2) * mm]});
            skFitSpline(sketch, "E472", {"points": [v(-38.2, -51.2) * mm, v(-38.3, -51.15) * mm, v(-38.58, -51.26) * mm, v(-38.85, -51.45) * mm]});
            skFitSpline(sketch, "E473", {"points": [v(-38.85, -51.45) * mm, v(-39.29, -51.78) * mm, v(-39.25, -51.89) * mm, v(-38.38, -52.72) * mm]});
            skFitSpline(sketch, "E474", {"points": [v(-38.38, -52.72) * mm, v(-37.84, -53.25) * mm, v(-37.36, -53.52) * mm, v(-37.26, -53.35) * mm]});
            skFitSpline(sketch, "E475", {"points": [v(-37.26, -53.35) * mm, v(-37.16, -53.2) * mm, v(-37.21, -52.99) * mm, v(-37.37, -52.89) * mm]});
            skFitSpline(sketch, "E476", {"points": [v(-37.37, -52.89) * mm, v(-37.53, -52.79) * mm, v(-37.58, -52.57) * mm, v(-37.48, -52.4) * mm]});
            skFitSpline(sketch, "E477", {"points": [v(-37.48, -52.4) * mm, v(-37.35, -52.2) * mm, v(-37.42, -52.18) * mm, v(-37.66, -52.32) * mm]});
            skFitSpline(sketch, "E478", {"points": [v(-37.66, -52.32) * mm, v(-37.92, -52.48) * mm, v(-37.96, -52.44) * mm, v(-37.8, -52.18) * mm]});
            skFitSpline(sketch, "E479", {"points": [v(-37.8, -52.18) * mm, v(-37.64, -51.92) * mm, v(-37.68, -51.88) * mm, v(-37.94, -52.04) * mm]});
            skFitSpline(sketch, "E480", {"points": [v(-37.94, -52.04) * mm, v(-38.19, -52.2) * mm, v(-38.24, -52.16) * mm, v(-38.1, -51.92) * mm]});
            skFitSpline(sketch, "E481", {"points": [v(-38.1, -51.92) * mm, v(-37.73, -51.33) * mm, v(-36.83, -52.39) * mm, v(-36.99, -53.24) * mm]});
            skFitSpline(sketch, "E482", {"points": [v(-36.99, -53.24) * mm, v(-37.1, -53.86) * mm, v(-37.05, -53.91) * mm, v(-36.7, -53.62) * mm]});
            skFitSpline(sketch, "E483", {"points": [v(-36.7, -53.62) * mm, v(-36.47, -53.43) * mm, v(-36.33, -53.03) * mm, v(-36.39, -52.73) * mm]});
            skFitSpline(sketch, "E484", {"points": [v(-38.22, -52.6) * mm, v(-38.77, -52.02) * mm, v(-38.82, -51.83) * mm, v(-38.52, -51.54) * mm]});
            skFitSpline(sketch, "E485", {"points": [v(-38.52, -51.54) * mm, v(-38.22, -51.26) * mm, v(-38.18, -51.28) * mm, v(-38.29, -51.62) * mm]});
            skFitSpline(sketch, "E486", {"points": [v(-38.29, -51.62) * mm, v(-38.37, -51.85) * mm, v(-38.17, -52.33) * mm, v(-37.85, -52.68) * mm]});
            skFitSpline(sketch, "E487", {"points": [v(-37.85, -52.68) * mm, v(-37.53, -53.02) * mm, v(-37.34, -53.31) * mm, v(-37.42, -53.31) * mm]});
            skFitSpline(sketch, "E488", {"points": [v(-37.42, -53.31) * mm, v(-37.5, -53.31) * mm, v(-37.86, -53) * mm, v(-38.22, -52.6) * mm]});
            skFitSpline(sketch, "E489", {"points": [v(-37.17, -51.69) * mm, v(-37.56, -51.26) * mm, v(-37.56, -51.12) * mm, v(-37.21, -50.65) * mm]});
            skFitSpline(sketch, "E490", {"points": [v(-37.21, -50.65) * mm, v(-36.92, -50.26) * mm, v(-36.8, -50.21) * mm, v(-36.8, -50.5) * mm]});
            skFitSpline(sketch, "E491", {"points": [v(-36.8, -50.5) * mm, v(-36.8, -50.84) * mm, v(-36.76, -50.84) * mm, v(-36.56, -50.53) * mm]});
            skFitSpline(sketch, "E492", {"points": [v(-36.56, -50.53) * mm, v(-36.39, -50.26) * mm, v(-36.26, -50.24) * mm, v(-36.12, -50.46) * mm]});
            skFitSpline(sketch, "E493", {"points": [v(-36.12, -50.46) * mm, v(-36.02, -50.63) * mm, v(-36.08, -50.77) * mm, v(-36.26, -50.77) * mm]});
            skFitSpline(sketch, "E494", {"points": [v(-36.26, -50.77) * mm, v(-36.51, -50.77) * mm, v(-36.52, -50.87) * mm, v(-36.28, -51.16) * mm]});
            skFitSpline(sketch, "E495", {"points": [v(-36.28, -51.16) * mm, v(-35.74, -51.8) * mm, v(-36.6, -52.31) * mm, v(-37.17, -51.69) * mm]});
            skFitSpline(sketch, "E496", {"points": [v(-36.54, -51.17) * mm, v(-36.73, -50.95) * mm, v(-37, -50.85) * mm, v(-37.14, -50.94) * mm]});
            skFitSpline(sketch, "E497", {"points": [v(-37.14, -50.94) * mm, v(-37.3, -51.04) * mm, v(-37.27, -51.26) * mm, v(-37.07, -51.5) * mm]});
            skFitSpline(sketch, "E498", {"points": [v(-37.07, -51.5) * mm, v(-36.9, -51.71) * mm, v(-36.63, -51.82) * mm, v(-36.48, -51.73) * mm]});
            skFitSpline(sketch, "E499", {"points": [v(-36.48, -51.73) * mm, v(-36.32, -51.63) * mm, v(-36.35, -51.4) * mm, v(-36.54, -51.17) * mm]});
            skFitSpline(sketch, "E500", {"points": [v(36.7, -53.62) * mm, v(36.78, -53.49) * mm, v(36.67, -53.23) * mm, v(36.45, -53.04) * mm]});
            skFitSpline(sketch, "E501", {"points": [v(36.45, -53.04) * mm, v(36.13, -52.78) * mm, v(36.07, -52.81) * mm, v(36.15, -53.22) * mm]});
            skFitSpline(sketch, "E502", {"points": [v(36.15, -53.22) * mm, v(36.2, -53.5) * mm, v(36.25, -53.77) * mm, v(36.27, -53.8) * mm]});
            skFitSpline(sketch, "E503", {"points": [v(36.27, -53.8) * mm, v(36.31, -53.96) * mm, v(36.54, -53.86) * mm, v(36.7, -53.62) * mm]});
            skFitSpline(sketch, "E504", {"points": [v(36.3, -51.67) * mm, v(36.45, -51.49) * mm, v(36.5, -51.4) * mm, v(36.4, -51.47) * mm]});
            skFitSpline(sketch, "E505", {"points": [v(36.4, -51.47) * mm, v(36.3, -51.54) * mm, v(35.94, -51.46) * mm, v(35.61, -51.29) * mm]});
            skFitSpline(sketch, "E506", {"points": [v(35.61, -51.29) * mm, v(35.29, -51.12) * mm, v(35.11, -51.08) * mm, v(35.23, -51.2) * mm]});
            skFitSpline(sketch, "E507", {"points": [v(35.23, -51.2) * mm, v(35.34, -51.32) * mm, v(35.31, -51.57) * mm, v(35.16, -51.75) * mm]});
            skFitSpline(sketch, "E508", {"points": [v(35.16, -51.75) * mm, v(34.96, -52) * mm, v(35.05, -52.07) * mm, v(35.45, -52.04) * mm]});
            skFitSpline(sketch, "E509", {"points": [v(35.45, -52.04) * mm, v(35.76, -52.02) * mm, v(36.14, -51.85) * mm, v(36.3, -51.67) * mm]});
            skFitSpline(sketch, "E510", {"points": [v(33.78, -47.69) * mm, v(33.32, -47.35) * mm, v(33.25, -47.15) * mm, v(33.49, -46.9) * mm]});
            skFitSpline(sketch, "E511", {"points": [v(33.49, -46.9) * mm, v(33.73, -46.67) * mm, v(33.67, -46.51) * mm, v(33.25, -46.3) * mm]});
            skFitSpline(sketch, "E512", {"points": [v(33.25, -46.3) * mm, v(32.77, -46.03) * mm, v(32.7, -46.08) * mm, v(32.73, -46.62) * mm]});
            skFitSpline(sketch, "E513", {"points": [v(32.73, -46.62) * mm, v(32.74, -46.96) * mm, v(32.95, -47.4) * mm, v(33.18, -47.59) * mm]});
            skFitSpline(sketch, "E514", {"points": [v(33.18, -47.59) * mm, v(33.42, -47.78) * mm, v(33.48, -47.94) * mm, v(33.32, -47.94) * mm]});
            skFitSpline(sketch, "E515", {"points": [v(33.32, -47.94) * mm, v(33.17, -47.95) * mm, v(33.23, -48.07) * mm, v(33.45, -48.22) * mm]});
            skFitSpline(sketch, "E516", {"points": [v(33.45, -48.22) * mm, v(34.14, -48.65) * mm, v(34.43, -48.18) * mm, v(33.78, -47.69) * mm]});
            skFitSpline(sketch, "E517", {"points": [v(34, -45.2) * mm, v(34.38, -45.5) * mm, v(34.4, -45.48) * mm, v(34.14, -45.13) * mm]});
            skFitSpline(sketch, "E518", {"points": [v(34.14, -45.13) * mm, v(33.96, -44.9) * mm, v(33.86, -44.48) * mm, v(33.9, -44.2) * mm]});
            skFitSpline(sketch, "E519", {"points": [v(33.9, -44.2) * mm, v(33.98, -43.68) * mm, v(33.6, -43.34) * mm, v(32.88, -43.28) * mm]});
            skFitSpline(sketch, "E520", {"points": [v(32.88, -43.28) * mm, v(32.34, -43.24) * mm, v(32.27, -43.91) * mm, v(32.8, -44.11) * mm]});
            skFitSpline(sketch, "E521", {"points": [v(32.8, -44.11) * mm, v(33, -44.19) * mm, v(33.1, -44.53) * mm, v(33.03, -44.88) * mm]});
            skFitSpline(sketch, "E522", {"points": [v(33.03, -44.88) * mm, v(32.94, -45.35) * mm, v(33, -45.43) * mm, v(33.24, -45.18) * mm]});
            skFitSpline(sketch, "E523", {"points": [v(33.24, -45.18) * mm, v(33.48, -44.94) * mm, v(33.67, -44.94) * mm, v(34, -45.2) * mm]});
            skFitSpline(sketch, "E524", {"points": [v(33.25, -44.7) * mm, v(33.37, -44.58) * mm, v(33.33, -44.31) * mm, v(33.17, -44.12) * mm]});
            skFitSpline(sketch, "E525", {"points": [v(33.17, -44.12) * mm, v(32.96, -43.87) * mm, v(32.96, -43.7) * mm, v(33.17, -43.58) * mm]});
            skFitSpline(sketch, "E526", {"points": [v(33.17, -43.58) * mm, v(33.33, -43.48) * mm, v(33.47, -43.44) * mm, v(33.49, -43.49) * mm]});
            skFitSpline(sketch, "E527", {"points": [v(33.49, -43.49) * mm, v(33.67, -44.24) * mm, v(33.64, -44.6) * mm, v(33.37, -44.75) * mm]});
            skFitSpline(sketch, "E528", {"points": [v(33.37, -44.75) * mm, v(33.19, -44.85) * mm, v(33.14, -44.83) * mm, v(33.25, -44.7) * mm]});
            skLineSegment(sketch, "E529", {"start": v(33.25, -44.7) * mm, "end": v(33.25, -44.7) * mm});
            skFitSpline(sketch, "E530", {"points": [v(-32.4, -41.6) * mm, v(-32.44, -41.38) * mm, v(-32.7, -40.94) * mm, v(-32.99, -40.62) * mm]});
            skFitSpline(sketch, "E531", {"points": [v(-32.99, -40.62) * mm, v(-33.37, -40.2) * mm, v(-33.6, -40.13) * mm, v(-33.87, -40.35) * mm]});
            skFitSpline(sketch, "E532", {"points": [v(-33.87, -40.35) * mm, v(-34.23, -40.65) * mm, v(-34.32, -41.8) * mm, v(-33.96, -41.58) * mm]});
            skFitSpline(sketch, "E533", {"points": [v(-33.96, -41.58) * mm, v(-33.85, -41.52) * mm, v(-33.62, -41.64) * mm, v(-33.43, -41.87) * mm]});
            skFitSpline(sketch, "E534", {"points": [v(-33.43, -41.87) * mm, v(-33.04, -42.34) * mm, v(-32.32, -42.15) * mm, v(-32.4, -41.6) * mm]});
            skFitSpline(sketch, "E535", {"points": [v(-33.55, -41.47) * mm, v(-33.82, -41.17) * mm, v(-33.95, -40.78) * mm, v(-33.83, -40.6) * mm]});
            skFitSpline(sketch, "E536", {"points": [v(-33.83, -40.6) * mm, v(-33.62, -40.25) * mm, v(-33.09, -40.91) * mm, v(-32.96, -41.67) * mm]});
            skFitSpline(sketch, "E537", {"points": [v(-32.96, -41.67) * mm, v(-32.89, -42.14) * mm, v(-32.97, -42.12) * mm, v(-33.55, -41.47) * mm]});
            skFitSpline(sketch, "E538", {"points": [v(32.8, -41.45) * mm, v(32.76, -40.84) * mm, v(32.2, -40.65) * mm, v(32.19, -41.25) * mm]});
            skFitSpline(sketch, "E539", {"points": [v(32.19, -41.25) * mm, v(32.18, -41.52) * mm, v(32.54, -41.98) * mm, v(32.8, -42.02) * mm]});
            skFitSpline(sketch, "E540", {"points": [v(32.8, -42.02) * mm, v(32.8, -42.02) * mm, v(32.8, -41.77) * mm, v(32.8, -41.45) * mm]});
            skFitSpline(sketch, "E541", {"points": [v(29.41, -41.32) * mm, v(30.14, -41.01) * mm, v(30.37, -40.77) * mm, v(30.25, -40.44) * mm]});
            skFitSpline(sketch, "E542", {"points": [v(30.25, -40.44) * mm, v(30.15, -40.2) * mm, v(30, -39.69) * mm, v(29.9, -39.31) * mm]});
            skFitSpline(sketch, "E543", {"points": [v(29.9, -39.31) * mm, v(29.7, -38.5) * mm, v(29.75, -38.5) * mm, v(28.6, -39.2) * mm]});
            skFitSpline(sketch, "E544", {"points": [v(28.6, -39.2) * mm, v(27.41, -39.92) * mm, v(26.13, -39.95) * mm, v(26.13, -39.26) * mm]});
            skFitSpline(sketch, "E545", {"points": [v(26.13, -39.26) * mm, v(26.13, -38.7) * mm, v(26.64, -38.07) * mm, v(27.08, -38.07) * mm]});
            skFitSpline(sketch, "E546", {"points": [v(27.08, -38.07) * mm, v(27.23, -38.07) * mm, v(27.27, -38.15) * mm, v(27.16, -38.26) * mm]});
            skFitSpline(sketch, "E547", {"points": [v(27.16, -38.26) * mm, v(26.86, -38.56) * mm, v(27.54, -39.18) * mm, v(27.99, -39) * mm]});
            skFitSpline(sketch, "E548", {"points": [v(27.99, -39) * mm, v(28.33, -38.88) * mm, v(28.33, -38.77) * mm, v(28.04, -38.39) * mm]});
            skFitSpline(sketch, "E549", {"points": [v(28.04, -38.39) * mm, v(27.72, -37.97) * mm, v(27.73, -37.97) * mm, v(28.2, -38.33) * mm]});
            skFitSpline(sketch, "E550", {"points": [v(28.2, -38.33) * mm, v(28.5, -38.58) * mm, v(28.78, -38.63) * mm, v(28.9, -38.47) * mm]});
            skFitSpline(sketch, "E551", {"points": [v(28.9, -38.47) * mm, v(29.32, -37.86) * mm, v(29.91, -38.28) * mm, v(30.3, -39.46) * mm]});
            skFitSpline(sketch, "E552", {"points": [v(30.3, -39.46) * mm, v(30.67, -40.54) * mm, v(30.77, -40.64) * mm, v(31.06, -40.24) * mm]});
            skFitSpline(sketch, "E553", {"points": [v(31.06, -40.24) * mm, v(31.25, -39.98) * mm, v(31.5, -39.87) * mm, v(31.63, -39.98) * mm]});
            skFitSpline(sketch, "E554", {"points": [v(31.63, -39.98) * mm, v(31.76, -40.1) * mm, v(31.77, -40.02) * mm, v(31.65, -39.82) * mm]});
            skFitSpline(sketch, "E555", {"points": [v(31.65, -39.82) * mm, v(31.53, -39.61) * mm, v(31.4, -39.13) * mm, v(31.36, -38.75) * mm]});
            skFitSpline(sketch, "E556", {"points": [v(31.36, -38.75) * mm, v(31.32, -38.37) * mm, v(31.21, -37.98) * mm, v(31.12, -37.9) * mm]});
            skFitSpline(sketch, "E557", {"points": [v(31.12, -37.9) * mm, v(30.87, -37.64) * mm, v(28.67, -37.48) * mm, v(28.67, -37.72) * mm]});
            skFitSpline(sketch, "E558", {"points": [v(28.67, -37.72) * mm, v(28.67, -37.83) * mm, v(28.35, -37.95) * mm, v(27.96, -37.97) * mm]});
            skFitSpline(sketch, "E559", {"points": [v(27.96, -37.97) * mm, v(27.54, -38) * mm, v(27.33, -37.9) * mm, v(27.44, -37.71) * mm]});
            skFitSpline(sketch, "E560", {"points": [v(27.44, -37.71) * mm, v(27.66, -37.36) * mm, v(27.06, -37.68) * mm, v(26.34, -38.3) * mm]});
            skFitSpline(sketch, "E561", {"points": [v(26.34, -38.3) * mm, v(25.8, -38.76) * mm, v(25.66, -40.05) * mm, v(26.14, -40.05) * mm]});
            skFitSpline(sketch, "E562", {"points": [v(26.14, -40.05) * mm, v(26.3, -40.05) * mm, v(26.36, -40.17) * mm, v(26.27, -40.33) * mm]});
            skFitSpline(sketch, "E563", {"points": [v(26.27, -40.33) * mm, v(26.17, -40.5) * mm, v(26.45, -40.61) * mm, v(26.94, -40.61) * mm]});
            skFitSpline(sketch, "E564", {"points": [v(26.94, -40.61) * mm, v(27.4, -40.61) * mm, v(27.87, -40.74) * mm, v(27.97, -40.9) * mm]});
            skFitSpline(sketch, "E565", {"points": [v(27.97, -40.9) * mm, v(28.09, -41.1) * mm, v(27.9, -41.13) * mm, v(27.42, -41.01) * mm]});
            skFitSpline(sketch, "E566", {"points": [v(27.42, -41.01) * mm, v(26.99, -40.9) * mm, v(26.7, -40.95) * mm, v(26.7, -41.13) * mm]});
            skFitSpline(sketch, "E567", {"points": [v(26.7, -41.13) * mm, v(26.7, -41.29) * mm, v(27.04, -41.47) * mm, v(27.47, -41.54) * mm]});
            skFitSpline(sketch, "E568", {"points": [v(27.47, -41.54) * mm, v(27.9, -41.6) * mm, v(28.28, -41.67) * mm, v(28.32, -41.7) * mm]});
            skFitSpline(sketch, "E569", {"points": [v(28.32, -41.7) * mm, v(28.37, -41.72) * mm, v(28.86, -41.55) * mm, v(29.41, -41.32) * mm]});
            skFitSpline(sketch, "E570", {"points": [v(-30.9, -39.13) * mm, v(-30.53, -38) * mm, v(-30.35, -37.87) * mm, v(-29.8, -38.41) * mm]});
            skFitSpline(sketch, "E571", {"points": [v(-29.8, -38.41) * mm, v(-29.54, -38.68) * mm, v(-29.36, -38.64) * mm, v(-28.97, -38.23) * mm]});
            skFitSpline(sketch, "E572", {"points": [v(-28.97, -38.23) * mm, v(-28.5, -37.73) * mm, v(-28.5, -37.72) * mm, v(-28.98, -37.88) * mm]});
            skFitSpline(sketch, "E573", {"points": [v(-28.98, -37.88) * mm, v(-29.25, -37.97) * mm, v(-29.47, -37.93) * mm, v(-29.47, -37.78) * mm]});
            skFitSpline(sketch, "E574", {"points": [v(-29.47, -37.78) * mm, v(-29.47, -37.25) * mm, v(-31.43, -37.48) * mm, v(-31.94, -38.08) * mm]});
            skFitSpline(sketch, "E575", {"points": [v(-31.94, -38.08) * mm, v(-32.43, -38.65) * mm, v(-32.7, -39.87) * mm, v(-32.27, -39.61) * mm]});
            skFitSpline(sketch, "E576", {"points": [v(-32.27, -39.61) * mm, v(-32.15, -39.53) * mm, v(-31.97, -39.74) * mm, v(-31.86, -40.07) * mm]});
            skFitSpline(sketch, "E577", {"points": [v(-31.86, -40.07) * mm, v(-31.63, -40.8) * mm, v(-31.34, -40.52) * mm, v(-30.9, -39.13) * mm]});
            skFitSpline(sketch, "E578", {"points": [v(-20.44, -39.75) * mm, v(-20.44, -39.23) * mm, v(-21.32, -39.11) * mm, v(-21.8, -39.58) * mm]});
            skFitSpline(sketch, "E579", {"points": [v(-21.8, -39.58) * mm, v(-22.22, -40.01) * mm, v(-22.19, -40.05) * mm, v(-21.35, -40.05) * mm]});
            skFitSpline(sketch, "E580", {"points": [v(-21.35, -40.05) * mm, v(-20.85, -40.05) * mm, v(-20.44, -39.91) * mm, v(-20.44, -39.75) * mm]});
            skFitSpline(sketch, "E581", {"points": [v(21.26, -39.7) * mm, v(21.2, -39.5) * mm, v(20.9, -39.34) * mm, v(20.62, -39.34) * mm]});
            skFitSpline(sketch, "E582", {"points": [v(20.62, -39.34) * mm, v(20.34, -39.34) * mm, v(20.05, -39.5) * mm, v(19.99, -39.7) * mm]});
            skFitSpline(sketch, "E583", {"points": [v(19.99, -39.7) * mm, v(19.91, -39.92) * mm, v(20.15, -40.05) * mm, v(20.62, -40.05) * mm]});
            skFitSpline(sketch, "E584", {"points": [v(20.62, -40.05) * mm, v(21.1, -40.05) * mm, v(21.33, -39.92) * mm, v(21.26, -39.7) * mm]});
            skFitSpline(sketch, "E585", {"points": [v(-27.65, -38.9) * mm, v(-27.74, -38.75) * mm, v(-27.94, -38.7) * mm, v(-28.08, -38.8) * mm]});
            skFitSpline(sketch, "E586", {"points": [v(-28.08, -38.8) * mm, v(-28.23, -38.88) * mm, v(-28.28, -39.08) * mm, v(-28.19, -39.22) * mm]});
            skFitSpline(sketch, "E587", {"points": [v(-28.19, -39.22) * mm, v(-28.1, -39.37) * mm, v(-27.9, -39.42) * mm, v(-27.75, -39.33) * mm]});
            skFitSpline(sketch, "E588", {"points": [v(-27.75, -39.33) * mm, v(-27.6, -39.23) * mm, v(-27.56, -39.04) * mm, v(-27.65, -38.9) * mm]});
            skFitSpline(sketch, "E589", {"points": [v(-28.3, -38.42) * mm, v(-27.95, -37.98) * mm, v(-27.96, -37.97) * mm, v(-28.41, -38.32) * mm]});
            skFitSpline(sketch, "E590", {"points": [v(-28.41, -38.32) * mm, v(-28.68, -38.53) * mm, v(-28.9, -38.75) * mm, v(-28.9, -38.81) * mm]});
            skFitSpline(sketch, "E591", {"points": [v(-28.9, -38.81) * mm, v(-28.9, -39.04) * mm, v(-28.67, -38.9) * mm, v(-28.3, -38.42) * mm]});
            skFitSpline(sketch, "E592", {"points": [v(13.62, -36.6) * mm, v(16.63, -34.1) * mm, v(19.58, -29.52) * mm, v(20.53, -25.86) * mm]});
            skLineSegment(sketch, "E593", {"start": v(20.53, -25.86) * mm, "end": v(20.89, -24.5) * mm});
            skLineSegment(sketch, "E594", {"start": v(20.89, -24.5) * mm, "end": v(16.38, -19.93) * mm});
            skFitSpline(sketch, "E595", {"points": [v(16.38, -19.93) * mm, v(13.9, -17.41) * mm, v(5.9, -9.35) * mm, v(-1.39, -2.02) * mm]});
            skLineSegment(sketch, "E596", {"start": v(-1.39, -2.02) * mm, "end": v(-14.65, 11.32) * mm});
            skLineSegment(sketch, "E597", {"start": v(-14.65, 11.32) * mm, "end": v(-18.67, 11.32) * mm});
            skLineSegment(sketch, "E598", {"start": v(-18.67, 11.32) * mm, "end": v(-22.7, 11.32) * mm});
            skLineSegment(sketch, "E599", {"start": v(-22.7, 11.32) * mm, "end": v(-22.7, 3.06) * mm});
            skLineSegment(sketch, "E600", {"start": v(-22.7, 3.06) * mm, "end": v(-22.7, -5.19) * mm});
            skLineSegment(sketch, "E601", {"start": v(-22.7, -5.19) * mm, "end": v(-6, -21.9) * mm});
            skFitSpline(sketch, "E602", {"points": [v(-6, -21.9) * mm, v(10.57, -38.46) * mm, v(10.71, -38.6) * mm, v(11.43, -38.2) * mm]});
            skFitSpline(sketch, "E603", {"points": [v(11.43, -38.2) * mm, v(11.83, -38) * mm, v(12.82, -37.27) * mm, v(13.62, -36.6) * mm]});
            skFitSpline(sketch, "E604", {"points": [v(10.89, -34.8) * mm, v(10.89, -34.45) * mm, v(10.56, -34.29) * mm, v(10, -34.36) * mm]});
            skFitSpline(sketch, "E605", {"points": [v(10, -34.36) * mm, v(9.9, -34.37) * mm, v(9.76, -34) * mm, v(9.7, -33.54) * mm]});
            skFitSpline(sketch, "E606", {"points": [v(9.7, -33.54) * mm, v(9.6, -32.84) * mm, v(9.68, -32.67) * mm, v(10.23, -32.53) * mm]});
            skFitSpline(sketch, "E607", {"points": [v(10.23, -32.53) * mm, v(10.59, -32.44) * mm, v(10.8, -32.24) * mm, v(10.7, -32.09) * mm]});
            skFitSpline(sketch, "E608", {"points": [v(10.7, -32.09) * mm, v(10.61, -31.93) * mm, v(10.8, -31.95) * mm, v(11.14, -32.13) * mm]});
            skFitSpline(sketch, "E609", {"points": [v(11.14, -32.13) * mm, v(11.46, -32.3) * mm, v(11.73, -32.58) * mm, v(11.73, -32.73) * mm]});
            skFitSpline(sketch, "E610", {"points": [v(11.73, -32.73) * mm, v(11.73, -32.9) * mm, v(11.86, -32.94) * mm, v(12.02, -32.85) * mm]});
            skFitSpline(sketch, "E611", {"points": [v(12.02, -32.85) * mm, v(12.54, -32.52) * mm, v(12.3, -32.16) * mm, v(11.17, -31.58) * mm]});
            skFitSpline(sketch, "E612", {"points": [v(11.17, -31.58) * mm, v(9.77, -30.87) * mm, v(9, -29.53) * mm, v(9.44, -28.58) * mm]});
            skFitSpline(sketch, "E613", {"points": [v(9.44, -28.58) * mm, v(9.97, -27.42) * mm, v(9.08, -27.82) * mm, v(8.26, -29.1) * mm]});
            skFitSpline(sketch, "E614", {"points": [v(8.26, -29.1) * mm, v(8, -29.54) * mm, v(7.6, -29.89) * mm, v(7.4, -29.89) * mm]});
            skFitSpline(sketch, "E615", {"points": [v(7.4, -29.89) * mm, v(6.87, -29.89) * mm, v(5.2, -29.03) * mm, v(4.55, -28.42) * mm]});
            skFitSpline(sketch, "E616", {"points": [v(4.55, -28.42) * mm, v(4.25, -28.14) * mm, v(3.9, -27.91) * mm, v(3.78, -27.91) * mm]});
            skFitSpline(sketch, "E617", {"points": [v(3.78, -27.91) * mm, v(3.65, -27.91) * mm, v(3.55, -27.66) * mm, v(3.55, -27.35) * mm]});
            skFitSpline(sketch, "E618", {"points": [v(3.55, -27.35) * mm, v(3.55, -27.04) * mm, v(3.4, -26.78) * mm, v(3.2, -26.77) * mm]});
            skFitSpline(sketch, "E619", {"points": [v(3.2, -26.77) * mm, v(3, -26.77) * mm, v(3.13, -26.52) * mm, v(3.48, -26.23) * mm]});
            skFitSpline(sketch, "E620", {"points": [v(3.48, -26.23) * mm, v(3.91, -25.87) * mm, v(4, -25.66) * mm, v(3.76, -25.57) * mm]});
            skFitSpline(sketch, "E621", {"points": [v(3.76, -25.57) * mm, v(3.55, -25.49) * mm, v(3.7, -25.32) * mm, v(4.11, -25.15) * mm]});
            skFitSpline(sketch, "E622", {"points": [v(4.11, -25.15) * mm, v(4.66, -24.93) * mm, v(4.94, -24.97) * mm, v(5.32, -25.31) * mm]});
            skFitSpline(sketch, "E623", {"points": [v(5.32, -25.31) * mm, v(5.6, -25.56) * mm, v(5.76, -25.92) * mm, v(5.69, -26.12) * mm]});
            skFitSpline(sketch, "E624", {"points": [v(5.69, -26.12) * mm, v(5.56, -26.45) * mm, v(6.5, -27.35) * mm, v(6.98, -27.35) * mm]});
            skFitSpline(sketch, "E625", {"points": [v(6.98, -27.35) * mm, v(7.1, -27.35) * mm, v(7.22, -26.93) * mm, v(7.27, -26.43) * mm]});
            skFitSpline(sketch, "E626", {"points": [v(7.27, -26.43) * mm, v(7.35, -25.57) * mm, v(7.43, -25.51) * mm, v(8.35, -25.56) * mm]});
            skLineSegment(sketch, "E627", {"start": v(8.35, -25.56) * mm, "end": v(9.33, -25.62) * mm});
            skLineSegment(sketch, "E628", {"start": v(9.33, -25.62) * mm, "end": v(8.06, -25) * mm});
            skFitSpline(sketch, "E629", {"points": [v(8.06, -25) * mm, v(7.05, -24.52) * mm, v(6.22, -24.39) * mm, v(3.94, -24.35) * mm]});
            skFitSpline(sketch, "E630", {"points": [v(3.94, -24.35) * mm, v(0.94, -24.3) * mm, v(-0.24, -24.1) * mm, v(0.03, -23.66) * mm]});
            skFitSpline(sketch, "E631", {"points": [v(0.03, -23.66) * mm, v(0.12, -23.51) * mm, v(0, -23.4) * mm, v(-0.24, -23.4) * mm]});
            skFitSpline(sketch, "E632", {"points": [v(-0.24, -23.4) * mm, v(-0.49, -23.4) * mm, v(-0.68, -23.27) * mm, v(-0.68, -23.11) * mm]});
            skFitSpline(sketch, "E633", {"points": [v(-0.68, -23.11) * mm, v(-0.68, -22.96) * mm, v(-0.83, -22.83) * mm, v(-1, -22.83) * mm]});
            skFitSpline(sketch, "E634", {"points": [v(-1, -22.83) * mm, v(-1.34, -22.83) * mm, v(-2.66, -21.43) * mm, v(-2.66, -21.07) * mm]});
            skFitSpline(sketch, "E635", {"points": [v(-2.66, -21.07) * mm, v(-2.66, -20.95) * mm, v(-2.91, -20.85) * mm, v(-3.22, -20.85) * mm]});
            skFitSpline(sketch, "E636", {"points": [v(-3.22, -20.85) * mm, v(-3.54, -20.85) * mm, v(-3.79, -20.67) * mm, v(-3.79, -20.43) * mm]});
            skFitSpline(sketch, "E637", {"points": [v(-3.79, -20.43) * mm, v(-3.79, -20.2) * mm, v(-3.92, -20) * mm, v(-4.07, -20) * mm]});
            skFitSpline(sketch, "E638", {"points": [v(-4.07, -20) * mm, v(-4.23, -20) * mm, v(-4.35, -19.82) * mm, v(-4.35, -19.58) * mm]});
            skFitSpline(sketch, "E639", {"points": [v(-4.35, -19.58) * mm, v(-4.35, -19.35) * mm, v(-4.51, -19.16) * mm, v(-4.7, -19.15) * mm]});
            skFitSpline(sketch, "E640", {"points": [v(-4.7, -19.15) * mm, v(-4.9, -19.14) * mm, v(-4.7, -18.95) * mm, v(-4.27, -18.71) * mm]});
            skFitSpline(sketch, "E641", {"points": [v(-4.27, -18.71) * mm, v(-3.84, -18.48) * mm, v(-3.56, -18.17) * mm, v(-3.66, -18.02) * mm]});
            skFitSpline(sketch, "E642", {"points": [v(-3.66, -18.02) * mm, v(-3.9, -17.64) * mm, v(-3.12, -17.68) * mm, v(-2.73, -18.08) * mm]});
            skFitSpline(sketch, "E643", {"points": [v(-2.73, -18.08) * mm, v(-2.48, -18.32) * mm, v(-2.3, -18.32) * mm, v(-1.98, -18.05) * mm]});
            skFitSpline(sketch, "E644", {"points": [v(-1.98, -18.05) * mm, v(-1.6, -17.75) * mm, v(-1.56, -17.83) * mm, v(-1.63, -18.66) * mm]});
            skFitSpline(sketch, "E645", {"points": [v(-1.63, -18.66) * mm, v(-1.7, -19.52) * mm, v(-1.58, -19.7) * mm, v(-0.65, -20.2) * mm]});
            skFitSpline(sketch, "E646", {"points": [v(-0.65, -20.2) * mm, v(0.08, -20.6) * mm, v(0.35, -20.66) * mm, v(0.25, -20.4) * mm]});
            skFitSpline(sketch, "E647", {"points": [v(0.25, -20.4) * mm, v(0.17, -20.18) * mm, v(-0.02, -20) * mm, v(-0.18, -20) * mm]});
            skFitSpline(sketch, "E648", {"points": [v(-0.18, -20) * mm, v(-0.34, -20) * mm, v(-0.4, -19.82) * mm, v(-0.3, -19.6) * mm]});
            skFitSpline(sketch, "E649", {"points": [v(-0.3, -19.6) * mm, v(-0.22, -19.37) * mm, v(-0.26, -19.11) * mm, v(-0.4, -19.03) * mm]});
            skFitSpline(sketch, "E650", {"points": [v(-0.4, -19.03) * mm, v(-0.82, -18.76) * mm, v(-0.27, -15.21) * mm, v(0.2, -15.21) * mm]});
            skFitSpline(sketch, "E651", {"points": [v(0.2, -15.21) * mm, v(0.35, -15.21) * mm, v(0.4, -15.08) * mm, v(0.3, -14.93) * mm]});
            skFitSpline(sketch, "E652", {"points": [v(0.3, -14.93) * mm, v(0.2, -14.77) * mm, v(0.32, -14.65) * mm, v(0.55, -14.65) * mm]});
            skFitSpline(sketch, "E653", {"points": [v(0.55, -14.65) * mm, v(0.88, -14.65) * mm, v(0.92, -14.47) * mm, v(0.73, -13.8) * mm]});
            skFitSpline(sketch, "E654", {"points": [v(0.73, -13.8) * mm, v(0.51, -13.04) * mm, v(0.55, -12.95) * mm, v(1.1, -12.95) * mm]});
            skFitSpline(sketch, "E655", {"points": [v(1.1, -12.95) * mm, v(1.55, -12.94) * mm, v(1.61, -12.88) * mm, v(1.33, -12.7) * mm]});
            skFitSpline(sketch, "E656", {"points": [v(1.33, -12.7) * mm, v(0.72, -12.31) * mm, v(1.43, -12.07) * mm, v(2.26, -12.38) * mm]});
            skFitSpline(sketch, "E657", {"points": [v(2.26, -12.38) * mm, v(2.73, -12.56) * mm, v(2.98, -12.56) * mm, v(2.98, -12.38) * mm]});
            skFitSpline(sketch, "E658", {"points": [v(2.98, -12.38) * mm, v(2.98, -12.23) * mm, v(3.11, -12.1) * mm, v(3.27, -12.1) * mm]});
            skFitSpline(sketch, "E659", {"points": [v(3.27, -12.1) * mm, v(3.42, -12.1) * mm, v(3.55, -12.35) * mm, v(3.55, -12.65) * mm]});
            skFitSpline(sketch, "E660", {"points": [v(3.55, -12.65) * mm, v(3.55, -12.94) * mm, v(3.68, -13.23) * mm, v(3.85, -13.29) * mm]});
            skFitSpline(sketch, "E661", {"points": [v(3.85, -13.29) * mm, v(4.25, -13.42) * mm, v(3.87, -14.36) * mm, v(3.41, -14.36) * mm]});
            skFitSpline(sketch, "E662", {"points": [v(3.41, -14.36) * mm, v(2.9, -14.36) * mm, v(2.45, -15) * mm, v(2.25, -16.01) * mm]});
            skFitSpline(sketch, "E663", {"points": [v(2.25, -16.01) * mm, v(2.1, -16.78) * mm, v(2.15, -16.9) * mm, v(2.64, -16.9) * mm]});
            skFitSpline(sketch, "E664", {"points": [v(2.64, -16.9) * mm, v(2.95, -16.9) * mm, v(3.3, -16.68) * mm, v(3.4, -16.42) * mm]});
            skFitSpline(sketch, "E665", {"points": [v(3.4, -16.42) * mm, v(3.55, -16) * mm, v(3.62, -16) * mm, v(3.84, -16.35) * mm]});
            skFitSpline(sketch, "E666", {"points": [v(3.84, -16.35) * mm, v(4.06, -16.7) * mm, v(4.1, -16.7) * mm, v(4.1, -16.36) * mm]});
            skFitSpline(sketch, "E667", {"points": [v(4.1, -16.36) * mm, v(4.11, -16.14) * mm, v(4.19, -16.04) * mm, v(4.27, -16.12) * mm]});
            skFitSpline(sketch, "E668", {"points": [v(4.27, -16.12) * mm, v(4.36, -16.21) * mm, v(4.75, -16.12) * mm, v(5.14, -15.92) * mm]});
            skFitSpline(sketch, "E669", {"points": [v(5.14, -15.92) * mm, v(7.28, -14.8) * mm, v(9.01, -17.62) * mm, v(7.28, -19.4) * mm]});
            skFitSpline(sketch, "E670", {"points": [v(7.28, -19.4) * mm, v(7.01, -19.67) * mm, v(6.76, -20.08) * mm, v(6.73, -20.31) * mm]});
            skFitSpline(sketch, "E671", {"points": [v(6.73, -20.31) * mm, v(6.61, -21.01) * mm, v(8.99, -23.13) * mm, v(10.07, -23.3) * mm]});
            skLineSegment(sketch, "E672", {"start": v(10.07, -23.3) * mm, "end": v(11.03, -23.44) * mm});
            skLineSegment(sketch, "E673", {"start": v(11.03, -23.44) * mm, "end": v(10.14, -22.5) * mm});
            skFitSpline(sketch, "E674", {"points": [v(10.14, -22.5) * mm, v(9.66, -21.98) * mm, v(9.13, -21.3) * mm, v(8.97, -20.99) * mm]});
            skFitSpline(sketch, "E675", {"points": [v(8.97, -20.99) * mm, v(8.57, -20.21) * mm, v(9.04, -19.44) * mm, v(9.9, -19.44) * mm]});
            skFitSpline(sketch, "E676", {"points": [v(9.9, -19.44) * mm, v(10.7, -19.44) * mm, v(13.83, -21.72) * mm, v(14.32, -22.64) * mm]});
            skFitSpline(sketch, "E677", {"points": [v(14.32, -22.64) * mm, v(14.5, -22.98) * mm, v(15, -23.67) * mm, v(15.44, -24.18) * mm]});
            skFitSpline(sketch, "E678", {"points": [v(15.44, -24.18) * mm, v(16.27, -25.13) * mm, v(16.57, -25.98) * mm, v(15.9, -25.44) * mm]});
            skFitSpline(sketch, "E679", {"points": [v(15.9, -25.44) * mm, v(15.7, -25.29) * mm, v(15.07, -25) * mm, v(14.48, -24.82) * mm]});
            skFitSpline(sketch, "E680", {"points": [v(14.48, -24.82) * mm, v(13.36, -24.46) * mm, v(12.48, -23.48) * mm, v(11.48, -21.49) * mm]});
            skFitSpline(sketch, "E681", {"points": [v(11.48, -21.49) * mm, v(11.1, -20.74) * mm, v(10.68, -20.29) * mm, v(10.36, -20.29) * mm]});
            skFitSpline(sketch, "E682", {"points": [v(10.36, -20.29) * mm, v(8.84, -20.29) * mm, v(9.74, -21.51) * mm, v(13.7, -24.8) * mm]});
            skFitSpline(sketch, "E683", {"points": [v(13.7, -24.8) * mm, v(15.38, -26.21) * mm, v(16.83, -27.55) * mm, v(16.92, -27.78) * mm]});
            skFitSpline(sketch, "E684", {"points": [v(16.92, -27.78) * mm, v(17.12, -28.3) * mm, v(16.88, -28.95) * mm, v(16.4, -29.13) * mm]});
            skFitSpline(sketch, "E685", {"points": [v(16.4, -29.13) * mm, v(16.2, -29.21) * mm, v(15.97, -29.66) * mm, v(15.87, -30.14) * mm]});
            skFitSpline(sketch, "E686", {"points": [v(15.87, -30.14) * mm, v(15.78, -30.62) * mm, v(15.58, -31.01) * mm, v(15.44, -31.01) * mm]});
            skFitSpline(sketch, "E687", {"points": [v(15.44, -31.01) * mm, v(15.3, -31.01) * mm, v(15.23, -30.78) * mm, v(15.3, -30.5) * mm]});
            skFitSpline(sketch, "E688", {"points": [v(15.3, -30.5) * mm, v(15.4, -30.15) * mm, v(14.95, -29.43) * mm, v(13.94, -28.33) * mm]});
            skLineSegment(sketch, "E689", {"start": v(13.94, -28.33) * mm, "end": v(12.44, -26.68) * mm});
            skLineSegment(sketch, "E690", {"start": v(12.44, -26.68) * mm, "end": v(12.3, -28.21) * mm});
            skFitSpline(sketch, "E691", {"points": [v(12.3, -28.21) * mm, v(12.1, -30.19) * mm, v(12.18, -30.4) * mm, v(13.29, -30.86) * mm]});
            skFitSpline(sketch, "E692", {"points": [v(13.29, -30.86) * mm, v(14.09, -31.2) * mm, v(14.19, -31.34) * mm, v(14.06, -32.04) * mm]});
            skFitSpline(sketch, "E693", {"points": [v(14.06, -32.04) * mm, v(13.83, -33.27) * mm, v(13.17, -34.1) * mm, v(11.97, -34.67) * mm]});
            skFitSpline(sketch, "E694", {"points": [v(11.97, -34.67) * mm, v(11.1, -35.1) * mm, v(10.89, -35.12) * mm, v(10.89, -34.8) * mm]});
            skLineSegment(sketch, "E695", {"start": v(10.89, -34.8) * mm, "end": v(10.89, -34.8) * mm});
            skFitSpline(sketch, "E696", {"points": [v(16.25, -28.23) * mm, v(16.25, -27.56) * mm, v(15.05, -26.55) * mm, v(14.14, -26.45) * mm]});
            skFitSpline(sketch, "E697", {"points": [v(14.14, -26.45) * mm, v(13.6, -26.38) * mm, v(13.14, -26.4) * mm, v(13.14, -26.47) * mm]});
            skFitSpline(sketch, "E698", {"points": [v(13.14, -26.47) * mm, v(13.14, -26.55) * mm, v(13.55, -27.03) * mm, v(14.05, -27.54) * mm]});
            skFitSpline(sketch, "E699", {"points": [v(14.05, -27.54) * mm, v(14.87, -28.4) * mm, v(16.25, -28.83) * mm, v(16.25, -28.23) * mm]});
            skFitSpline(sketch, "E700", {"points": [v(4.4, -20.01) * mm, v(5.08, -19.48) * mm, v(5.08, -19.47) * mm, v(4.47, -19.63) * mm]});
            skFitSpline(sketch, "E701", {"points": [v(4.47, -19.63) * mm, v(4.12, -19.72) * mm, v(3.83, -19.9) * mm, v(3.83, -20.02) * mm]});
            skFitSpline(sketch, "E702", {"points": [v(3.83, -20.02) * mm, v(3.83, -20.15) * mm, v(3.6, -20.3) * mm, v(3.34, -20.38) * mm]});
            skFitSpline(sketch, "E703", {"points": [v(3.34, -20.38) * mm, v(2.99, -20.47) * mm, v(2.97, -20.51) * mm, v(3.27, -20.53) * mm]});
            skFitSpline(sketch, "E704", {"points": [v(3.27, -20.53) * mm, v(3.5, -20.55) * mm, v(4, -20.31) * mm, v(4.4, -20.01) * mm]});
            skFitSpline(sketch, "E705", {"points": [v(3.65, -18.79) * mm, v(3.75, -18.9) * mm, v(3.83, -18.82) * mm, v(3.83, -18.64) * mm]});
            skFitSpline(sketch, "E706", {"points": [v(3.83, -18.64) * mm, v(3.83, -18.46) * mm, v(3.75, -18.31) * mm, v(3.64, -18.31) * mm]});
            skFitSpline(sketch, "E707", {"points": [v(3.64, -18.31) * mm, v(3.33, -18.31) * mm, v(2.42, -19.22) * mm, v(2.42, -19.53) * mm]});
            skFitSpline(sketch, "E708", {"points": [v(2.42, -19.53) * mm, v(2.42, -19.69) * mm, v(2.66, -19.54) * mm, v(2.94, -19.2) * mm]});
            skFitSpline(sketch, "E709", {"points": [v(2.94, -19.2) * mm, v(3.23, -18.88) * mm, v(3.55, -18.69) * mm, v(3.65, -18.79) * mm]});
            skFitSpline(sketch, "E710", {"points": [v(5.06, -18.44) * mm, v(4.97, -18.2) * mm, v(4.83, -18.07) * mm, v(4.76, -18.14) * mm]});
            skFitSpline(sketch, "E711", {"points": [v(4.76, -18.14) * mm, v(4.68, -18.22) * mm, v(4.7, -18.41) * mm, v(4.8, -18.58) * mm]});
            skFitSpline(sketch, "E712", {"points": [v(4.8, -18.58) * mm, v(5.09, -19.03) * mm, v(5.25, -18.94) * mm, v(5.06, -18.44) * mm]});
            skFitSpline(sketch, "E713", {"points": [v(-6.33, -17.19) * mm, v(-6.37, -16.95) * mm, v(-6.38, -16.67) * mm, v(-6.36, -16.55) * mm]});
            skFitSpline(sketch, "E714", {"points": [v(-6.36, -16.55) * mm, v(-6.33, -16.37) * mm, v(-6.94, -16.23) * mm, v(-7.49, -16.3) * mm]});
            skFitSpline(sketch, "E715", {"points": [v(-7.49, -16.3) * mm, v(-7.58, -16.3) * mm, v(-7.6, -15.98) * mm, v(-7.52, -15.58) * mm]});
            skFitSpline(sketch, "E716", {"points": [v(-7.52, -15.58) * mm, v(-7.42, -15.07) * mm, v(-7.48, -14.9) * mm, v(-7.7, -15.04) * mm]});
            skFitSpline(sketch, "E717", {"points": [v(-7.7, -15.04) * mm, v(-7.88, -15.15) * mm, v(-8.02, -15.18) * mm, v(-8.02, -15.1) * mm]});
            skFitSpline(sketch, "E718", {"points": [v(-8.02, -15.1) * mm, v(-8.02, -15.01) * mm, v(-7.63, -14.74) * mm, v(-7.15, -14.5) * mm]});
            skFitSpline(sketch, "E719", {"points": [v(-7.15, -14.5) * mm, v(-6.34, -14.07) * mm, v(-6.24, -14.08) * mm, v(-5.74, -14.53) * mm]});
            skFitSpline(sketch, "E720", {"points": [v(-5.74, -14.53) * mm, v(-5.26, -14.96) * mm, v(-5.2, -14.96) * mm, v(-5.2, -14.57) * mm]});
            skFitSpline(sketch, "E721", {"points": [v(-5.2, -14.57) * mm, v(-5.2, -14.32) * mm, v(-5.7, -13.84) * mm, v(-6.31, -13.5) * mm]});
            skFitSpline(sketch, "E722", {"points": [v(-6.31, -13.5) * mm, v(-7.55, -12.8) * mm, v(-8.18, -11.64) * mm, v(-7.9, -10.56) * mm]});
            skFitSpline(sketch, "E723", {"points": [v(-7.9, -10.56) * mm, v(-7.65, -9.52) * mm, v(-8.22, -9.68) * mm, v(-8.9, -10.84) * mm]});
            skFitSpline(sketch, "E724", {"points": [v(-8.9, -10.84) * mm, v(-9.27, -11.44) * mm, v(-9.7, -11.82) * mm, v(-10.06, -11.82) * mm]});
            skFitSpline(sketch, "E725", {"points": [v(-10.06, -11.82) * mm, v(-10.7, -11.82) * mm, v(-12.82, -10.71) * mm, v(-12.82, -10.38) * mm]});
            skFitSpline(sketch, "E726", {"points": [v(-12.82, -10.38) * mm, v(-12.82, -10.26) * mm, v(-13.07, -10.09) * mm, v(-13.37, -10) * mm]});
            skFitSpline(sketch, "E727", {"points": [v(-13.37, -10) * mm, v(-13.68, -9.9) * mm, v(-13.86, -9.65) * mm, v(-13.77, -9.44) * mm]});
            skFitSpline(sketch, "E728", {"points": [v(-13.77, -9.44) * mm, v(-13.7, -9.23) * mm, v(-13.77, -8.97) * mm, v(-13.95, -8.86) * mm]});
            skFitSpline(sketch, "E729", {"points": [v(-13.95, -8.86) * mm, v(-14.18, -8.72) * mm, v(-14.15, -8.53) * mm, v(-13.85, -8.2) * mm]});
            skFitSpline(sketch, "E730", {"points": [v(-13.85, -8.2) * mm, v(-13.61, -7.94) * mm, v(-13.4, -7.6) * mm, v(-13.39, -7.45) * mm]});
            skFitSpline(sketch, "E731", {"points": [v(-13.39, -7.45) * mm, v(-13.36, -7.3) * mm, v(-13.15, -7.2) * mm, v(-12.91, -7.26) * mm]});
            skFitSpline(sketch, "E732", {"points": [v(-12.91, -7.26) * mm, v(-12.64, -7.31) * mm, v(-12.56, -7.22) * mm, v(-12.68, -7.02) * mm]});
            skFitSpline(sketch, "E733", {"points": [v(-12.68, -7.02) * mm, v(-12.84, -6.77) * mm, v(-12.74, -6.76) * mm, v(-12.29, -7) * mm]});
            skFitSpline(sketch, "E734", {"points": [v(-12.29, -7) * mm, v(-11.95, -7.19) * mm, v(-11.7, -7.6) * mm, v(-11.7, -7.96) * mm]});
            skFitSpline(sketch, "E735", {"points": [v(-11.7, -7.96) * mm, v(-11.7, -8.47) * mm, v(-10.64, -9.55) * mm, v(-10.45, -9.23) * mm]});
            skFitSpline(sketch, "E736", {"points": [v(-10.45, -9.23) * mm, v(-10.42, -9.18) * mm, v(-10.27, -8.76) * mm, v(-10.11, -8.3) * mm]});
            skFitSpline(sketch, "E737", {"points": [v(-10.11, -8.3) * mm, v(-9.88, -7.59) * mm, v(-9.7, -7.46) * mm, v(-9, -7.5) * mm]});
            skFitSpline(sketch, "E738", {"points": [v(-9, -7.5) * mm, v(-8.24, -7.56) * mm, v(-8.28, -7.5) * mm, v(-9.43, -6.95) * mm]});
            skFitSpline(sketch, "E739", {"points": [v(-9.43, -6.95) * mm, v(-10.45, -6.46) * mm, v(-11.26, -6.33) * mm, v(-13.53, -6.3) * mm]});
            skFitSpline(sketch, "E740", {"points": [v(-13.53, -6.3) * mm, v(-16.39, -6.25) * mm, v(-17.72, -6.02) * mm, v(-17.47, -5.6) * mm]});
            skFitSpline(sketch, "E741", {"points": [v(-17.47, -5.6) * mm, v(-17.4, -5.48) * mm, v(-17.7, -5.22) * mm, v(-18.14, -5.02) * mm]});
            skFitSpline(sketch, "E742", {"points": [v(-18.14, -5.02) * mm, v(-18.58, -4.83) * mm, v(-19.24, -4.24) * mm, v(-19.6, -3.7) * mm]});
            skFitSpline(sketch, "E743", {"points": [v(-19.6, -3.7) * mm, v(-20.05, -3.05) * mm, v(-20.42, -2.8) * mm, v(-20.77, -2.89) * mm]});
            skFitSpline(sketch, "E744", {"points": [v(-20.77, -2.89) * mm, v(-21.11, -2.98) * mm, v(-21.29, -2.87) * mm, v(-21.3, -2.55) * mm]});
            skFitSpline(sketch, "E745", {"points": [v(-21.3, -2.55) * mm, v(-21.3, -1.96) * mm, v(-21.99, -1.05) * mm, v(-22.23, -1.3) * mm]});
            skFitSpline(sketch, "E746", {"points": [v(-22.23, -1.3) * mm, v(-22.33, -1.4) * mm, v(-22.42, -1.39) * mm, v(-22.42, -1.28) * mm]});
            skFitSpline(sketch, "E747", {"points": [v(-22.42, -1.28) * mm, v(-22.42, -1.17) * mm, v(-22.08, -0.96) * mm, v(-21.68, -0.8) * mm]});
            skFitSpline(sketch, "E748", {"points": [v(-21.68, -0.8) * mm, v(-21.2, -0.62) * mm, v(-21, -0.38) * mm, v(-21.1, -0.1) * mm]});
            skFitSpline(sketch, "E749", {"points": [v(-21.1, -0.1) * mm, v(-21.3, 0.39) * mm, v(-20.9, 0.43) * mm, v(-20.1, 0) * mm]});
            skFitSpline(sketch, "E750", {"points": [v(-20.1, 0) * mm, v(-19.66, -0.24) * mm, v(-19.47, -0.22) * mm, v(-19.28, 0.07) * mm]});
            skFitSpline(sketch, "E751", {"points": [v(-19.28, 0.07) * mm, v(-19.1, 0.35) * mm, v(-19.03, 0.26) * mm, v(-19, -0.25) * mm]});
            skFitSpline(sketch, "E752", {"points": [v(-19, -0.25) * mm, v(-18.98, -0.64) * mm, v(-18.98, -1.1) * mm, v(-19, -1.26) * mm]});
            skFitSpline(sketch, "E753", {"points": [v(-19, -1.26) * mm, v(-19.01, -1.42) * mm, v(-18.49, -1.86) * mm, v(-17.83, -2.22) * mm]});
            skLineSegment(sketch, "E754", {"start": v(-17.83, -2.22) * mm, "end": v(-16.63, -2.88) * mm});
            skLineSegment(sketch, "E755", {"start": v(-16.63, -2.88) * mm, "end": v(-17.24, -2.2) * mm});
            skFitSpline(sketch, "E756", {"points": [v(-17.24, -2.2) * mm, v(-17.76, -1.62) * mm, v(-17.84, -1.22) * mm, v(-17.8, 0.49) * mm]});
            skFitSpline(sketch, "E757", {"points": [v(-17.8, 0.49) * mm, v(-17.73, 2.48) * mm, v(-17.31, 3.42) * mm, v(-16.47, 3.42) * mm]});
            skFitSpline(sketch, "E758", {"points": [v(-16.47, 3.42) * mm, v(-16.22, 3.42) * mm, v(-16.22, 3.52) * mm, v(-16.49, 3.84) * mm]});
            skFitSpline(sketch, "E759", {"points": [v(-16.49, 3.84) * mm, v(-16.68, 4.07) * mm, v(-16.73, 4.27) * mm, v(-16.6, 4.27) * mm]});
            skFitSpline(sketch, "E760", {"points": [v(-16.6, 4.27) * mm, v(-16.46, 4.27) * mm, v(-16.54, 4.4) * mm, v(-16.76, 4.54) * mm]});
            skFitSpline(sketch, "E761", {"points": [v(-16.76, 4.54) * mm, v(-17.1, 4.75) * mm, v(-17.08, 4.84) * mm, v(-16.57, 5.02) * mm]});
            skFitSpline(sketch, "E762", {"points": [v(-16.57, 5.02) * mm, v(-16.23, 5.15) * mm, v(-15.92, 5.38) * mm, v(-15.87, 5.53) * mm]});
            skFitSpline(sketch, "E763", {"points": [v(-15.87, 5.53) * mm, v(-15.82, 5.69) * mm, v(-15.72, 5.8) * mm, v(-15.64, 5.78) * mm]});
            skFitSpline(sketch, "E764", {"points": [v(-15.64, 5.78) * mm, v(-15.56, 5.76) * mm, v(-15.22, 5.65) * mm, v(-14.87, 5.55) * mm]});
            skFitSpline(sketch, "E765", {"points": [v(-14.87, 5.55) * mm, v(-14.43, 5.42) * mm, v(-14.23, 5.47) * mm, v(-14.22, 5.73) * mm]});
            skFitSpline(sketch, "E766", {"points": [v(-14.22, 5.73) * mm, v(-14.22, 5.96) * mm, v(-14.1, 5.91) * mm, v(-13.92, 5.6) * mm]});
            skFitSpline(sketch, "E767", {"points": [v(-13.92, 5.6) * mm, v(-13.77, 5.33) * mm, v(-13.73, 4.95) * mm, v(-13.85, 4.75) * mm]});
            skFitSpline(sketch, "E768", {"points": [v(-13.85, 4.75) * mm, v(-13.99, 4.52) * mm, v(-13.9, 4.53) * mm, v(-13.58, 4.8) * mm]});
            skFitSpline(sketch, "E769", {"points": [v(-13.58, 4.8) * mm, v(-13.27, 5.04) * mm, v(-13.1, 5.07) * mm, v(-13.1, 4.86) * mm]});
            skFitSpline(sketch, "E770", {"points": [v(-13.1, 4.86) * mm, v(-13.1, 4.57) * mm, v(-13.54, 4.1) * mm, v(-14.63, 3.2) * mm]});
            skFitSpline(sketch, "E771", {"points": [v(-14.63, 3.2) * mm, v(-14.88, 3) * mm, v(-15.08, 2.45) * mm, v(-15.08, 2) * mm]});
            skFitSpline(sketch, "E772", {"points": [v(-15.08, 2) * mm, v(-15.08, 1.35) * mm, v(-14.95, 1.16) * mm, v(-14.51, 1.16) * mm]});
            skFitSpline(sketch, "E773", {"points": [v(-14.51, 1.16) * mm, v(-14.17, 1.16) * mm, v(-13.95, 1.35) * mm, v(-13.94, 1.65) * mm]});
            skFitSpline(sketch, "E774", {"points": [v(-13.94, 1.65) * mm, v(-13.94, 2) * mm, v(-13.87, 2.04) * mm, v(-13.72, 1.8) * mm]});
            skFitSpline(sketch, "E775", {"points": [v(-13.72, 1.8) * mm, v(-13.55, 1.54) * mm, v(-13.35, 1.54) * mm, v(-12.8, 1.83) * mm]});
            skFitSpline(sketch, "E776", {"points": [v(-12.8, 1.83) * mm, v(-11.75, 2.37) * mm, v(-10.24, 2.34) * mm, v(-9.81, 1.78) * mm]});
            skFitSpline(sketch, "E777", {"points": [v(-9.81, 1.78) * mm, v(-9.28, 1.07) * mm, v(-9.35, -0.62) * mm, v(-9.94, -1.26) * mm]});
            skFitSpline(sketch, "E778", {"points": [v(-9.94, -1.26) * mm, v(-10.96, -2.36) * mm, v(-10.9, -2.71) * mm, v(-9.44, -3.97) * mm]});
            skFitSpline(sketch, "E779", {"points": [v(-9.44, -3.97) * mm, v(-8.68, -4.62) * mm, v(-7.72, -5.2) * mm, v(-7.3, -5.26) * mm]});
            skLineSegment(sketch, "E780", {"start": v(-7.3, -5.26) * mm, "end": v(-6.54, -5.36) * mm});
            skLineSegment(sketch, "E781", {"start": v(-6.54, -5.36) * mm, "end": v(-7.56, -4.17) * mm});
            skFitSpline(sketch, "E782", {"points": [v(-7.56, -4.17) * mm, v(-8.13, -3.51) * mm, v(-8.59, -2.77) * mm, v(-8.59, -2.52) * mm]});
            skFitSpline(sketch, "E783", {"points": [v(-8.59, -2.52) * mm, v(-8.59, -1.92) * mm, v(-8.04, -1.38) * mm, v(-7.44, -1.38) * mm]});
            skFitSpline(sketch, "E784", {"points": [v(-7.44, -1.38) * mm, v(-6.68, -1.38) * mm, v(-3.72, -3.54) * mm, v(-3.1, -4.56) * mm]});
            skFitSpline(sketch, "E785", {"points": [v(-3.1, -4.56) * mm, v(-2.78, -5.07) * mm, v(-2.23, -5.78) * mm, v(-1.88, -6.12) * mm]});
            skFitSpline(sketch, "E786", {"points": [v(-1.88, -6.12) * mm, v(-0.6, -7.39) * mm, v(-1.3, -7.56) * mm, v(-3.48, -6.5) * mm]});
            skFitSpline(sketch, "E787", {"points": [v(-3.48, -6.5) * mm, v(-4.17, -6.17) * mm, v(-4.75, -5.5) * mm, v(-5.47, -4.2) * mm]});
            skFitSpline(sketch, "E788", {"points": [v(-5.47, -4.2) * mm, v(-6.18, -2.93) * mm, v(-6.69, -2.34) * mm, v(-7.12, -2.28) * mm]});
            skFitSpline(sketch, "E789", {"points": [v(-7.12, -2.28) * mm, v(-7.51, -2.22) * mm, v(-7.74, -2.34) * mm, v(-7.74, -2.6) * mm]});
            skFitSpline(sketch, "E790", {"points": [v(-7.74, -2.6) * mm, v(-7.74, -3.08) * mm, v(-3.93, -6.77) * mm, v(-2.02, -8.14) * mm]});
            skFitSpline(sketch, "E791", {"points": [v(-2.02, -8.14) * mm, v(-0.4, -9.3) * mm, v(-0.03, -10.28) * mm, v(-0.95, -11.02) * mm]});
            skFitSpline(sketch, "E792", {"points": [v(-0.95, -11.02) * mm, v(-1.3, -11.3) * mm, v(-1.5, -11.64) * mm, v(-1.41, -11.79) * mm]});
            skFitSpline(sketch, "E793", {"points": [v(-1.41, -11.79) * mm, v(-1.32, -11.93) * mm, v(-1.5, -12.35) * mm, v(-1.79, -12.71) * mm]});
            skLineSegment(sketch, "E794", {"start": v(-1.79, -12.71) * mm, "end": v(-2.33, -13.37) * mm});
            skLineSegment(sketch, "E795", {"start": v(-2.33, -13.37) * mm, "end": v(-2.18, -12.6) * mm});
            skFitSpline(sketch, "E796", {"points": [v(-2.18, -12.6) * mm, v(-2.06, -11.98) * mm, v(-2.28, -11.58) * mm, v(-3.44, -10.38) * mm]});
            skLineSegment(sketch, "E797", {"start": v(-3.44, -10.38) * mm, "end": v(-4.84, -8.9) * mm});
            skLineSegment(sketch, "E798", {"start": v(-4.84, -8.9) * mm, "end": v(-5.04, -10.23) * mm});
            skFitSpline(sketch, "E799", {"points": [v(-5.04, -10.23) * mm, v(-5.3, -12) * mm, v(-5.07, -12.6) * mm, v(-4.03, -12.82) * mm]});
            skFitSpline(sketch, "E800", {"points": [v(-4.03, -12.82) * mm, v(-3.22, -13) * mm, v(-3.17, -13.08) * mm, v(-3.32, -14) * mm]});
            skFitSpline(sketch, "E801", {"points": [v(-3.32, -14) * mm, v(-3.55, -15.4) * mm, v(-4.24, -16.33) * mm, v(-5.2, -16.52) * mm]});
            skFitSpline(sketch, "E802", {"points": [v(-5.2, -16.52) * mm, v(-5.65, -16.61) * mm, v(-6.07, -16.9) * mm, v(-6.14, -17.15) * mm]});
            skFitSpline(sketch, "E803", {"points": [v(-6.14, -17.15) * mm, v(-6.24, -17.52) * mm, v(-6.28, -17.53) * mm, v(-6.33, -17.19) * mm]});
            skFitSpline(sketch, "E804", {"points": [v(-1.34, -10.25) * mm, v(-1.07, -9.53) * mm, v(-2.42, -8.37) * mm, v(-3.39, -8.48) * mm]});
            skLineSegment(sketch, "E805", {"start": v(-3.39, -8.48) * mm, "end": v(-4.2, -8.58) * mm});
            skLineSegment(sketch, "E806", {"start": v(-4.2, -8.58) * mm, "end": v(-3.14, -9.64) * mm});
            skFitSpline(sketch, "E807", {"points": [v(-3.14, -9.64) * mm, v(-1.97, -10.8) * mm, v(-1.6, -10.92) * mm, v(-1.34, -10.25) * mm]});
            skFitSpline(sketch, "E808", {"points": [v(-13.1, -2.08) * mm, v(-12.9, -1.84) * mm, v(-12.82, -1.57) * mm, v(-12.92, -1.47) * mm]});
            skFitSpline(sketch, "E809", {"points": [v(-12.92, -1.47) * mm, v(-13.02, -1.37) * mm, v(-13.1, -1.44) * mm, v(-13.1, -1.63) * mm]});
            skFitSpline(sketch, "E810", {"points": [v(-13.1, -1.63) * mm, v(-13.1, -1.81) * mm, v(-13.39, -2.08) * mm, v(-13.74, -2.22) * mm]});
            skFitSpline(sketch, "E811", {"points": [v(-13.74, -2.22) * mm, v(-14.17, -2.4) * mm, v(-14.22, -2.48) * mm, v(-13.91, -2.5) * mm]});
            skFitSpline(sketch, "E812", {"points": [v(-13.91, -2.5) * mm, v(-13.66, -2.5) * mm, v(-13.3, -2.32) * mm, v(-13.1, -2.08) * mm]});
            skFitSpline(sketch, "E813", {"points": [v(-14.6, -1.05) * mm, v(-14.7, -0.82) * mm, v(-14.76, -0.89) * mm, v(-14.77, -1.22) * mm]});
            skFitSpline(sketch, "E814", {"points": [v(-14.77, -1.22) * mm, v(-14.79, -1.51) * mm, v(-14.72, -1.68) * mm, v(-14.62, -1.59) * mm]});
            skFitSpline(sketch, "E815", {"points": [v(-14.62, -1.59) * mm, v(-14.53, -1.5) * mm, v(-14.52, -1.25) * mm, v(-14.6, -1.05) * mm]});
            skLineSegment(sketch, "E816", {"start": v(-14.6, -1.05) * mm, "end": v(-14.6, -1.05) * mm});
            skFitSpline(sketch, "E817", {"points": [v(-13.64, -0.7) * mm, v(-13.5, -0.78) * mm, v(-13.38, -0.64) * mm, v(-13.38, -0.38) * mm]});
            skFitSpline(sketch, "E818", {"points": [v(-13.38, -0.38) * mm, v(-13.38, 0.01) * mm, v(-13.46, 0.04) * mm, v(-13.8, -0.25) * mm]});
            skFitSpline(sketch, "E819", {"points": [v(-13.8, -0.25) * mm, v(-14.04, -0.45) * mm, v(-14.22, -0.75) * mm, v(-14.2, -0.92) * mm]});
            skFitSpline(sketch, "E820", {"points": [v(-14.2, -0.92) * mm, v(-14.2, -1.12) * mm, v(-14.13, -1.1) * mm, v(-14.04, -0.89) * mm]});
            skFitSpline(sketch, "E821", {"points": [v(-14.04, -0.89) * mm, v(-13.96, -0.7) * mm, v(-13.78, -0.6) * mm, v(-13.64, -0.7) * mm]});
            skFitSpline(sketch, "E822", {"points": [v(-12.16, -0.38) * mm, v(-12.25, -0.14) * mm, v(-12.39, 0) * mm, v(-12.46, -0.08) * mm]});
            skFitSpline(sketch, "E823", {"points": [v(-12.46, -0.08) * mm, v(-12.53, -0.15) * mm, v(-12.51, -0.35) * mm, v(-12.4, -0.52) * mm]});
            skFitSpline(sketch, "E824", {"points": [v(-12.4, -0.52) * mm, v(-12.13, -0.97) * mm, v(-11.97, -0.88) * mm, v(-12.16, -0.38) * mm]});
            skFitSpline(sketch, "E825", {"points": [v(-10.84, -0.53) * mm, v(-10.84, -0.38) * mm, v(-10.98, -0.25) * mm, v(-11.14, -0.25) * mm]});
            skFitSpline(sketch, "E826", {"points": [v(-11.14, -0.25) * mm, v(-11.3, -0.25) * mm, v(-11.36, -0.38) * mm, v(-11.27, -0.53) * mm]});
            skFitSpline(sketch, "E827", {"points": [v(-11.27, -0.53) * mm, v(-11.17, -0.69) * mm, v(-11.04, -0.82) * mm, v(-10.97, -0.82) * mm]});
            skFitSpline(sketch, "E828", {"points": [v(-10.97, -0.82) * mm, v(-10.9, -0.82) * mm, v(-10.84, -0.69) * mm, v(-10.84, -0.53) * mm]});
            skFitSpline(sketch, "E829", {"points": [v(31.65, -37.36) * mm, v(31.33, -37.11) * mm, v(30.56, -36.96) * mm, v(29.81, -36.98) * mm]});
            skLineSegment(sketch, "E830", {"start": v(29.81, -36.98) * mm, "end": v(28.53, -37.02) * mm});
            skLineSegment(sketch, "E831", {"start": v(28.53, -37.02) * mm, "end": v(29.85, -37.2) * mm});
            skFitSpline(sketch, "E832", {"points": [v(29.85, -37.2) * mm, v(30.59, -37.3) * mm, v(31.27, -37.48) * mm, v(31.38, -37.59) * mm]});
            skFitSpline(sketch, "E833", {"points": [v(31.38, -37.59) * mm, v(31.5, -37.7) * mm, v(31.72, -37.78) * mm, v(31.89, -37.78) * mm]});
            skFitSpline(sketch, "E834", {"points": [v(31.89, -37.78) * mm, v(32.06, -37.77) * mm, v(31.95, -37.58) * mm, v(31.65, -37.36) * mm]});
            skFitSpline(sketch, "E835", {"points": [v(-28.4, -34.13) * mm, v(-28.1, -33.29) * mm, v(-28.16, -31.22) * mm, v(-28.51, -31.1) * mm]});
            skFitSpline(sketch, "E836", {"points": [v(-28.51, -31.1) * mm, v(-28.85, -30.99) * mm, v(-29.83, -34.05) * mm, v(-29.59, -34.44) * mm]});
            skFitSpline(sketch, "E837", {"points": [v(-29.59, -34.44) * mm, v(-29.32, -34.88) * mm, v(-28.6, -34.7) * mm, v(-28.4, -34.13) * mm]});
            skFitSpline(sketch, "E838", {"points": [v(-26.61, -32) * mm, v(-26.66, -30.6) * mm, v(-26.64, -29.53) * mm, v(-26.56, -29.6) * mm]});
            skFitSpline(sketch, "E839", {"points": [v(-26.56, -29.6) * mm, v(-26.43, -29.73) * mm, v(-26.12, -32.62) * mm, v(-26.1, -33.93) * mm]});
            skFitSpline(sketch, "E840", {"points": [v(-26.1, -33.93) * mm, v(-26.09, -34.3) * mm, v(-25.9, -34.41) * mm, v(-25.45, -34.35) * mm]});
            skFitSpline(sketch, "E841", {"points": [v(-25.45, -34.35) * mm, v(-24.93, -34.28) * mm, v(-24.83, -34.11) * mm, v(-24.9, -33.42) * mm]});
            skFitSpline(sketch, "E842", {"points": [v(-24.9, -33.42) * mm, v(-24.96, -32.95) * mm, v(-25.13, -32.41) * mm, v(-25.3, -32.21) * mm]});
            skFitSpline(sketch, "E843", {"points": [v(-25.3, -32.21) * mm, v(-25.46, -32.01) * mm, v(-25.53, -31.78) * mm, v(-25.44, -31.69) * mm]});
            skFitSpline(sketch, "E844", {"points": [v(-25.44, -31.69) * mm, v(-25.35, -31.6) * mm, v(-25.45, -30.97) * mm, v(-25.65, -30.28) * mm]});
            skFitSpline(sketch, "E845", {"points": [v(-25.65, -30.28) * mm, v(-25.87, -29.57) * mm, v(-25.92, -28.97) * mm, v(-25.77, -28.88) * mm]});
            skFitSpline(sketch, "E846", {"points": [v(-25.77, -28.88) * mm, v(-25.63, -28.8) * mm, v(-25.52, -28.94) * mm, v(-25.52, -29.2) * mm]});
            skFitSpline(sketch, "E847", {"points": [v(-25.52, -29.2) * mm, v(-25.52, -29.9) * mm, v(-24.38, -33.63) * mm, v(-24.05, -34.04) * mm]});
            skFitSpline(sketch, "E848", {"points": [v(-24.05, -34.04) * mm, v(-23.85, -34.3) * mm, v(-23.61, -34.3) * mm, v(-23.23, -34.1) * mm]});
            skFitSpline(sketch, "E849", {"points": [v(-23.23, -34.1) * mm, v(-22.72, -33.83) * mm, v(-22.74, -33.73) * mm, v(-23.65, -31.92) * mm]});
            skFitSpline(sketch, "E850", {"points": [v(-23.65, -31.92) * mm, v(-24.18, -30.88) * mm, v(-24.77, -29.55) * mm, v(-24.95, -28.97) * mm]});
            skFitSpline(sketch, "E851", {"points": [v(-24.95, -28.97) * mm, v(-25.16, -28.3) * mm, v(-25.4, -27.98) * mm, v(-25.6, -28.1) * mm]});
            skFitSpline(sketch, "E852", {"points": [v(-25.6, -28.1) * mm, v(-25.78, -28.21) * mm, v(-26.37, -28.35) * mm, v(-26.92, -28.4) * mm]});
            skFitSpline(sketch, "E853", {"points": [v(-26.92, -28.4) * mm, v(-27.47, -28.46) * mm, v(-28, -28.6) * mm, v(-28.12, -28.7) * mm]});
            skFitSpline(sketch, "E854", {"points": [v(-28.12, -28.7) * mm, v(-28.49, -29.07) * mm, v(-28.5, -30.8) * mm, v(-28.13, -30.94) * mm]});
            skFitSpline(sketch, "E855", {"points": [v(-28.13, -30.94) * mm, v(-27.88, -31.02) * mm, v(-27.78, -30.7) * mm, v(-27.78, -29.86) * mm]});
            skFitSpline(sketch, "E856", {"points": [v(-27.78, -29.86) * mm, v(-27.78, -29.2) * mm, v(-27.71, -28.73) * mm, v(-27.63, -28.81) * mm]});
            skFitSpline(sketch, "E857", {"points": [v(-27.63, -28.81) * mm, v(-27.33, -29.1) * mm, v(-27.23, -30.99) * mm, v(-27.5, -31.16) * mm]});
            skFitSpline(sketch, "E858", {"points": [v(-27.5, -31.16) * mm, v(-27.81, -31.35) * mm, v(-27.88, -34.2) * mm, v(-27.58, -34.5) * mm]});
            skFitSpline(sketch, "E859", {"points": [v(-27.58, -34.5) * mm, v(-27.47, -34.61) * mm, v(-27.19, -34.67) * mm, v(-26.95, -34.62) * mm]});
            skFitSpline(sketch, "E860", {"points": [v(-26.95, -34.62) * mm, v(-26.6, -34.55) * mm, v(-26.54, -34.1) * mm, v(-26.61, -32) * mm]});
            skFitSpline(sketch, "E861", {"points": [v(26.9, -34.46) * mm, v(27.15, -34.3) * mm, v(27.17, -33.63) * mm, v(26.97, -31.71) * mm]});
            skFitSpline(sketch, "E862", {"points": [v(26.97, -31.71) * mm, v(26.82, -30.32) * mm, v(26.7, -29.02) * mm, v(26.7, -28.83) * mm]});
            skFitSpline(sketch, "E863", {"points": [v(26.7, -28.83) * mm, v(26.7, -28.63) * mm, v(26.56, -28.47) * mm, v(26.4, -28.47) * mm]});
            skFitSpline(sketch, "E864", {"points": [v(26.4, -28.47) * mm, v(26.23, -28.47) * mm, v(26.1, -29.06) * mm, v(26.1, -29.82) * mm]});
            skFitSpline(sketch, "E865", {"points": [v(26.1, -29.82) * mm, v(26.1, -30.55) * mm, v(26.04, -31.76) * mm, v(25.95, -32.5) * mm]});
            skFitSpline(sketch, "E866", {"points": [v(25.95, -32.5) * mm, v(25.72, -34.4) * mm, v(26.02, -35.01) * mm, v(26.9, -34.46) * mm]});
            skFitSpline(sketch, "E867", {"points": [v(28.74, -34.53) * mm, v(29.08, -34.4) * mm, v(29.04, -34.04) * mm, v(28.49, -32.36) * mm]});
            skFitSpline(sketch, "E868", {"points": [v(28.49, -32.36) * mm, v(28.12, -31.25) * mm, v(27.75, -29.93) * mm, v(27.65, -29.41) * mm]});
            skFitSpline(sketch, "E869", {"points": [v(27.65, -29.41) * mm, v(27.55, -28.9) * mm, v(27.36, -28.47) * mm, v(27.22, -28.47) * mm]});
            skFitSpline(sketch, "E870", {"points": [v(27.22, -28.47) * mm, v(26.91, -28.47) * mm, v(26.91, -28.41) * mm, v(27.27, -31.3) * mm]});
            skFitSpline(sketch, "E871", {"points": [v(27.27, -31.3) * mm, v(27.7, -34.77) * mm, v(27.75, -34.9) * mm, v(28.74, -34.53) * mm]});
            skFitSpline(sketch, "E872", {"points": [v(-29.47, -32) * mm, v(-28.28, -28.44) * mm, v(-28.24, -28.2) * mm, v(-28.88, -28.2) * mm]});
            skFitSpline(sketch, "E873", {"points": [v(-28.88, -28.2) * mm, v(-29.5, -28.2) * mm, v(-31.02, -30.62) * mm, v(-30.56, -30.9) * mm]});
            skFitSpline(sketch, "E874", {"points": [v(-30.56, -30.9) * mm, v(-30.2, -31.12) * mm, v(-30.17, -31.09) * mm, v(-29.49, -29.6) * mm]});
            skFitSpline(sketch, "E875", {"points": [v(-29.49, -29.6) * mm, v(-29.17, -28.9) * mm, v(-29, -28.65) * mm, v(-29.1, -29.04) * mm]});
            skFitSpline(sketch, "E876", {"points": [v(-29.1, -29.04) * mm, v(-29.2, -29.43) * mm, v(-29.3, -29.96) * mm, v(-29.3, -30.22) * mm]});
            skFitSpline(sketch, "E877", {"points": [v(-29.3, -30.22) * mm, v(-29.3, -30.48) * mm, v(-29.39, -30.64) * mm, v(-29.48, -30.59) * mm]});
            skFitSpline(sketch, "E878", {"points": [v(-29.48, -30.59) * mm, v(-29.72, -30.43) * mm, v(-31.45, -34.03) * mm, v(-31.23, -34.24) * mm]});
            skFitSpline(sketch, "E879", {"points": [v(-31.23, -34.24) * mm, v(-30.71, -34.76) * mm, v(-30.16, -34.06) * mm, v(-29.47, -32) * mm]});
            skFitSpline(sketch, "E880", {"points": [v(23.98, -32.55) * mm, v(24.43, -31.12) * mm, v(24.4, -30.45) * mm, v(23.91, -30.45) * mm]});
            skFitSpline(sketch, "E881", {"points": [v(23.91, -30.45) * mm, v(23.8, -30.45) * mm, v(23.36, -31.16) * mm, v(22.93, -32.03) * mm]});
            skFitSpline(sketch, "E882", {"points": [v(22.93, -32.03) * mm, v(22.34, -33.23) * mm, v(22.23, -33.7) * mm, v(22.47, -33.99) * mm]});
            skFitSpline(sketch, "E883", {"points": [v(22.47, -33.99) * mm, v(23, -34.62) * mm, v(23.47, -34.17) * mm, v(23.98, -32.55) * mm]});
            skFitSpline(sketch, "E884", {"points": [v(25.43, -33.75) * mm, v(25.52, -33.4) * mm, v(25.53, -32.76) * mm, v(25.46, -32.35) * mm]});
            skFitSpline(sketch, "E885", {"points": [v(25.46, -32.35) * mm, v(25.38, -31.93) * mm, v(25.44, -31.52) * mm, v(25.58, -31.43) * mm]});
            skFitSpline(sketch, "E886", {"points": [v(25.58, -31.43) * mm, v(25.95, -31.2) * mm, v(25.92, -28.2) * mm, v(25.55, -28.2) * mm]});
            skFitSpline(sketch, "E887", {"points": [v(25.55, -28.2) * mm, v(25.38, -28.2) * mm, v(25.32, -28.31) * mm, v(25.4, -28.45) * mm]});
            skFitSpline(sketch, "E888", {"points": [v(25.4, -28.45) * mm, v(25.5, -28.6) * mm, v(25.44, -28.8) * mm, v(25.28, -28.9) * mm]});
            skFitSpline(sketch, "E889", {"points": [v(25.28, -28.9) * mm, v(25.13, -29) * mm, v(25, -28.81) * mm, v(25, -28.5) * mm]});
            skFitSpline(sketch, "E890", {"points": [v(25, -28.5) * mm, v(25, -27.97) * mm, v(24.84, -27.86) * mm, v(24.25, -27.93) * mm]});
            skFitSpline(sketch, "E891", {"points": [v(24.25, -27.93) * mm, v(24.15, -27.95) * mm, v(23.97, -27.79) * mm, v(23.83, -27.58) * mm]});
            skFitSpline(sketch, "E892", {"points": [v(23.83, -27.58) * mm, v(23.65, -27.3) * mm, v(23.6, -27.3) * mm, v(23.6, -27.56) * mm]});
            skFitSpline(sketch, "E893", {"points": [v(23.6, -27.56) * mm, v(23.59, -27.76) * mm, v(22.61, -28.94) * mm, v(21.42, -30.18) * mm]});
            skFitSpline(sketch, "E894", {"points": [v(21.42, -30.18) * mm, v(19.8, -31.87) * mm, v(19.34, -32.53) * mm, v(19.58, -32.77) * mm]});
            skFitSpline(sketch, "E895", {"points": [v(19.58, -32.77) * mm, v(19.82, -33) * mm, v(20.06, -32.88) * mm, v(20.54, -32.27) * mm]});
            skFitSpline(sketch, "E896", {"points": [v(20.54, -32.27) * mm, v(20.9, -31.82) * mm, v(21.15, -31.34) * mm, v(21.11, -31.21) * mm]});
            skFitSpline(sketch, "E897", {"points": [v(21.11, -31.21) * mm, v(21.07, -31.08) * mm, v(21.14, -31.04) * mm, v(21.26, -31.11) * mm]});
            skFitSpline(sketch, "E898", {"points": [v(21.26, -31.11) * mm, v(21.39, -31.2) * mm, v(22.03, -30.48) * mm, v(22.68, -29.52) * mm]});
            skFitSpline(sketch, "E899", {"points": [v(22.68, -29.52) * mm, v(23.33, -28.57) * mm, v(23.87, -27.91) * mm, v(23.86, -28.06) * mm]});
            skFitSpline(sketch, "E900", {"points": [v(23.86, -28.06) * mm, v(23.86, -28.21) * mm, v(23.67, -28.57) * mm, v(23.46, -28.85) * mm]});
            skFitSpline(sketch, "E901", {"points": [v(23.46, -28.85) * mm, v(23.24, -29.14) * mm, v(23.14, -29.59) * mm, v(23.23, -29.84) * mm]});
            skFitSpline(sketch, "E902", {"points": [v(23.23, -29.84) * mm, v(23.32, -30.1) * mm, v(23.3, -30.22) * mm, v(23.17, -30.1) * mm]});
            skFitSpline(sketch, "E903", {"points": [v(23.17, -30.1) * mm, v(23.05, -30) * mm, v(22.59, -30.38) * mm, v(22.14, -30.95) * mm]});
            skFitSpline(sketch, "E904", {"points": [v(22.14, -30.95) * mm, v(21.7, -31.53) * mm, v(21.13, -32.22) * mm, v(20.88, -32.48) * mm]});
            skFitSpline(sketch, "E905", {"points": [v(20.88, -32.48) * mm, v(20.38, -33) * mm, v(20.52, -33.84) * mm, v(21.1, -33.84) * mm]});
            skFitSpline(sketch, "E906", {"points": [v(21.1, -33.84) * mm, v(21.56, -33.84) * mm, v(22.75, -31.93) * mm, v(23.6, -29.82) * mm]});
            skFitSpline(sketch, "E907", {"points": [v(23.6, -29.82) * mm, v(24.24, -28.23) * mm, v(24.73, -27.66) * mm, v(24.16, -29.16) * mm]});
            skFitSpline(sketch, "E908", {"points": [v(24.16, -29.16) * mm, v(23.86, -29.95) * mm, v(23.97, -30.45) * mm, v(24.45, -30.45) * mm]});
            skFitSpline(sketch, "E909", {"points": [v(24.45, -30.45) * mm, v(24.6, -30.45) * mm, v(24.72, -30.16) * mm, v(24.72, -29.81) * mm]});
            skFitSpline(sketch, "E910", {"points": [v(24.72, -29.81) * mm, v(24.72, -29.32) * mm, v(24.78, -29.27) * mm, v(24.98, -29.59) * mm]});
            skFitSpline(sketch, "E911", {"points": [v(24.98, -29.59) * mm, v(25.13, -29.82) * mm, v(25.18, -30.1) * mm, v(25.1, -30.23) * mm]});
            skFitSpline(sketch, "E912", {"points": [v(25.1, -30.23) * mm, v(24.78, -30.75) * mm, v(23.93, -34.09) * mm, v(24.08, -34.24) * mm]});
            skFitSpline(sketch, "E913", {"points": [v(24.08, -34.24) * mm, v(24.48, -34.64) * mm, v(25.28, -34.35) * mm, v(25.43, -33.75) * mm]});
            skFitSpline(sketch, "E914", {"points": [v(30.64, -33.96) * mm, v(30.64, -33.73) * mm, v(30.34, -33.22) * mm, v(29.97, -32.85) * mm]});
            skFitSpline(sketch, "E915", {"points": [v(29.97, -32.85) * mm, v(29.6, -32.48) * mm, v(29.35, -32.12) * mm, v(29.42, -32.05) * mm]});
            skFitSpline(sketch, "E916", {"points": [v(29.42, -32.05) * mm, v(29.49, -31.98) * mm, v(29.3, -31.37) * mm, v(29, -30.7) * mm]});
            skFitSpline(sketch, "E917", {"points": [v(29, -30.7) * mm, v(28.7, -30.02) * mm, v(28.33, -29.14) * mm, v(28.16, -28.76) * mm]});
            skFitSpline(sketch, "E918", {"points": [v(28.16, -28.76) * mm, v(27.45, -27.1) * mm, v(27.85, -29.28) * mm, v(28.7, -31.8) * mm]});
            skFitSpline(sketch, "E919", {"points": [v(28.7, -31.8) * mm, v(29.4, -33.81) * mm, v(29.72, -34.4) * mm, v(30.12, -34.4) * mm]});
            skFitSpline(sketch, "E920", {"points": [v(30.12, -34.4) * mm, v(30.4, -34.4) * mm, v(30.64, -34.2) * mm, v(30.64, -33.96) * mm]});
            skFitSpline(sketch, "E921", {"points": [v(-31.77, -33.74) * mm, v(-31.6, -33.53) * mm, v(-31.53, -33.28) * mm, v(-31.64, -33.18) * mm]});
            skFitSpline(sketch, "E922", {"points": [v(-31.64, -33.18) * mm, v(-31.74, -33.07) * mm, v(-31.7, -33) * mm, v(-31.55, -33) * mm]});
            skFitSpline(sketch, "E923", {"points": [v(-31.55, -33) * mm, v(-31.17, -33) * mm, v(-30.26, -31.36) * mm, v(-30.55, -31.18) * mm]});
            skFitSpline(sketch, "E924", {"points": [v(-30.55, -31.18) * mm, v(-30.69, -31.1) * mm, v(-31.09, -31.38) * mm, v(-31.44, -31.8) * mm]});
            skFitSpline(sketch, "E925", {"points": [v(-31.44, -31.8) * mm, v(-31.8, -32.22) * mm, v(-32.28, -32.78) * mm, v(-32.5, -33.04) * mm]});
            skFitSpline(sketch, "E926", {"points": [v(-32.5, -33.04) * mm, v(-32.9, -33.5) * mm, v(-32.79, -34.12) * mm, v(-32.31, -34.12) * mm]});
            skFitSpline(sketch, "E927", {"points": [v(-32.31, -34.12) * mm, v(-32.18, -34.12) * mm, v(-31.94, -33.95) * mm, v(-31.77, -33.74) * mm]});
            skFitSpline(sketch, "E928", {"points": [v(31.96, -33.9) * mm, v(32.19, -33.75) * mm, v(31.92, -33.19) * mm, v(31.09, -32.08) * mm]});
            skFitSpline(sketch, "E929", {"points": [v(31.09, -32.08) * mm, v(30.42, -31.19) * mm, v(29.78, -30.55) * mm, v(29.65, -30.67) * mm]});
            skFitSpline(sketch, "E930", {"points": [v(29.65, -30.67) * mm, v(29.53, -30.78) * mm, v(29.52, -30.7) * mm, v(29.63, -30.5) * mm]});
            skFitSpline(sketch, "E931", {"points": [v(29.63, -30.5) * mm, v(29.75, -30.3) * mm, v(29.63, -29.82) * mm, v(29.37, -29.43) * mm]});
            skFitSpline(sketch, "E932", {"points": [v(29.37, -29.43) * mm, v(29.12, -29.03) * mm, v(28.97, -28.64) * mm, v(29.05, -28.56) * mm]});
            skFitSpline(sketch, "E933", {"points": [v(29.05, -28.56) * mm, v(29.13, -28.49) * mm, v(29.4, -28.82) * mm, v(29.65, -29.3) * mm]});
            skFitSpline(sketch, "E934", {"points": [v(29.65, -29.3) * mm, v(29.9, -29.79) * mm, v(30.23, -30.1) * mm, v(30.4, -30) * mm]});
            skFitSpline(sketch, "E935", {"points": [v(30.4, -30) * mm, v(30.58, -29.9) * mm, v(30.54, -29.66) * mm, v(30.28, -29.36) * mm]});
            skFitSpline(sketch, "E936", {"points": [v(30.28, -29.36) * mm, v(29.14, -28.03) * mm, v(29.64, -28.28) * mm, v(30.9, -29.67) * mm]});
            skFitSpline(sketch, "E937", {"points": [v(30.9, -29.67) * mm, v(31.72, -30.57) * mm, v(32.52, -31.3) * mm, v(32.68, -31.3) * mm]});
            skFitSpline(sketch, "E938", {"points": [v(32.68, -31.3) * mm, v(32.84, -31.3) * mm, v(33.14, -31.52) * mm, v(33.34, -31.8) * mm]});
            skFitSpline(sketch, "E939", {"points": [v(33.34, -31.8) * mm, v(33.63, -32.18) * mm, v(33.78, -32.21) * mm, v(34.06, -31.94) * mm]});
            skFitSpline(sketch, "E940", {"points": [v(34.06, -31.94) * mm, v(34.26, -31.74) * mm, v(34.36, -31.55) * mm, v(34.3, -31.5) * mm]});
            skFitSpline(sketch, "E941", {"points": [v(34.3, -31.5) * mm, v(34.23, -31.44) * mm, v(33.54, -30.95) * mm, v(32.76, -30.39) * mm]});
            skFitSpline(sketch, "E942", {"points": [v(32.76, -30.39) * mm, v(31.98, -29.83) * mm, v(30.98, -28.98) * mm, v(30.53, -28.51) * mm]});
            skFitSpline(sketch, "E943", {"points": [v(30.53, -28.51) * mm, v(29.75, -27.7) * mm, v(29.28, -27.65) * mm, v(28.44, -28.34) * mm]});
            skFitSpline(sketch, "E944", {"points": [v(28.44, -28.34) * mm, v(28.32, -28.44) * mm, v(29.74, -31.58) * mm, v(30.53, -32.92) * mm]});
            skFitSpline(sketch, "E945", {"points": [v(30.53, -32.92) * mm, v(31.25, -34.16) * mm, v(31.4, -34.26) * mm, v(31.96, -33.9) * mm]});
            skFitSpline(sketch, "E946", {"points": [v(-21.32, -33.45) * mm, v(-21.07, -33.16) * mm, v(-21.1, -32.98) * mm, v(-21.43, -32.7) * mm]});
            skFitSpline(sketch, "E947", {"points": [v(-21.43, -32.7) * mm, v(-22.01, -32.22) * mm, v(-24.67, -28.22) * mm, v(-24.67, -27.83) * mm]});
            skFitSpline(sketch, "E948", {"points": [v(-24.67, -27.83) * mm, v(-24.67, -27.66) * mm, v(-24.28, -28.15) * mm, v(-23.79, -28.91) * mm]});
            skFitSpline(sketch, "E949", {"points": [v(-23.79, -28.91) * mm, v(-22.82, -30.44) * mm, v(-21.57, -32.02) * mm, v(-21.57, -31.7) * mm]});
            skFitSpline(sketch, "E950", {"points": [v(-21.57, -31.7) * mm, v(-21.57, -31.6) * mm, v(-21.38, -31.66) * mm, v(-21.15, -31.85) * mm]});
            skFitSpline(sketch, "E951", {"points": [v(-21.15, -31.85) * mm, v(-20.93, -32.04) * mm, v(-20.77, -32.3) * mm, v(-20.8, -32.42) * mm]});
            skFitSpline(sketch, "E952", {"points": [v(-20.8, -32.42) * mm, v(-20.86, -32.65) * mm, v(-20.73, -32.7) * mm, v(-20.1, -32.7) * mm]});
            skFitSpline(sketch, "E953", {"points": [v(-20.1, -32.7) * mm, v(-19.93, -32.7) * mm, v(-20.67, -31.79) * mm, v(-21.76, -30.66) * mm]});
            skFitSpline(sketch, "E954", {"points": [v(-21.76, -30.66) * mm, v(-22.85, -29.54) * mm, v(-23.9, -28.32) * mm, v(-24.1, -27.95) * mm]});
            skFitSpline(sketch, "E955", {"points": [v(-24.1, -27.95) * mm, v(-24.34, -27.49) * mm, v(-24.53, -27.37) * mm, v(-24.74, -27.58) * mm]});
            skFitSpline(sketch, "E956", {"points": [v(-24.74, -27.58) * mm, v(-25.11, -27.95) * mm, v(-24.11, -30.74) * mm, v(-22.95, -32.56) * mm]});
            skFitSpline(sketch, "E957", {"points": [v(-22.95, -32.56) * mm, v(-22.1, -33.92) * mm, v(-21.83, -34.06) * mm, v(-21.32, -33.45) * mm]});
            skFitSpline(sketch, "E958", {"points": [v(-31.84, -31.5) * mm, v(-30.43, -29.59) * mm, v(-29.64, -28.21) * mm, v(-29.84, -28.01) * mm]});
            skFitSpline(sketch, "E959", {"points": [v(-29.84, -28.01) * mm, v(-29.9, -27.94) * mm, v(-30.2, -28.26) * mm, v(-30.5, -28.71) * mm]});
            skFitSpline(sketch, "E960", {"points": [v(-30.5, -28.71) * mm, v(-31.24, -29.88) * mm, v(-33.09, -31.86) * mm, v(-33.42, -31.86) * mm]});
            skFitSpline(sketch, "E961", {"points": [v(-33.42, -31.86) * mm, v(-33.58, -31.86) * mm, v(-33.7, -32.06) * mm, v(-33.7, -32.3) * mm]});
            skFitSpline(sketch, "E962", {"points": [v(-33.7, -32.3) * mm, v(-33.7, -32.58) * mm, v(-33.84, -32.66) * mm, v(-34.06, -32.53) * mm]});
            skFitSpline(sketch, "E963", {"points": [v(-34.06, -32.53) * mm, v(-34.3, -32.39) * mm, v(-34.29, -32.47) * mm, v(-34.02, -32.8) * mm]});
            skFitSpline(sketch, "E964", {"points": [v(-34.02, -32.8) * mm, v(-33.8, -33.06) * mm, v(-33.52, -33.27) * mm, v(-33.39, -33.27) * mm]});
            skFitSpline(sketch, "E965", {"points": [v(-33.39, -33.27) * mm, v(-33.25, -33.27) * mm, v(-32.55, -32.48) * mm, v(-31.84, -31.5) * mm]});
            skFitSpline(sketch, "E966", {"points": [v(33.14, -32.9) * mm, v(33.58, -32.37) * mm, v(31.65, -30.46) * mm, v(31.17, -30.94) * mm]});
            skFitSpline(sketch, "E967", {"points": [v(31.17, -30.94) * mm, v(30.92, -31.19) * mm, v(31.05, -31.51) * mm, v(31.66, -32.25) * mm]});
            skFitSpline(sketch, "E968", {"points": [v(31.66, -32.25) * mm, v(32.59, -33.36) * mm, v(32.71, -33.42) * mm, v(33.14, -32.9) * mm]});
            skFitSpline(sketch, "E969", {"points": [v(-33.56, -31.5) * mm, v(-33.26, -31.16) * mm, v(-33.04, -30.77) * mm, v(-33.08, -30.64) * mm]});
            skFitSpline(sketch, "E970", {"points": [v(-33.08, -30.64) * mm, v(-33.12, -30.51) * mm, v(-33.04, -30.48) * mm, v(-32.9, -30.57) * mm]});
            skFitSpline(sketch, "E971", {"points": [v(-32.9, -30.57) * mm, v(-32.61, -30.74) * mm, v(-30.32, -28.38) * mm, v(-30.32, -27.9) * mm]});
            skFitSpline(sketch, "E972", {"points": [v(-30.32, -27.9) * mm, v(-30.32, -27.74) * mm, v(-30.75, -28.04) * mm, v(-31.28, -28.57) * mm]});
            skFitSpline(sketch, "E973", {"points": [v(-31.28, -28.57) * mm, v(-31.8, -29.1) * mm, v(-32.82, -29.95) * mm, v(-33.53, -30.46) * mm]});
            skFitSpline(sketch, "E974", {"points": [v(-33.53, -30.46) * mm, v(-34.79, -31.36) * mm, v(-35.22, -32.14) * mm, v(-34.47, -32.14) * mm]});
            skFitSpline(sketch, "E975", {"points": [v(-34.47, -32.14) * mm, v(-34.27, -32.14) * mm, v(-33.86, -31.86) * mm, v(-33.56, -31.5) * mm]});
            skFitSpline(sketch, "E976", {"points": [v(31.01, -30.28) * mm, v(30.88, -29.93) * mm, v(30.8, -29.92) * mm, v(30.62, -30.2) * mm]});
            skFitSpline(sketch, "E977", {"points": [v(30.62, -30.2) * mm, v(30.36, -30.63) * mm, v(30.57, -31.1) * mm, v(30.93, -30.87) * mm]});
            skFitSpline(sketch, "E978", {"points": [v(30.93, -30.87) * mm, v(31.07, -30.78) * mm, v(31.1, -30.52) * mm, v(31.01, -30.28) * mm]});
            skFitSpline(sketch, "E979", {"points": [v(-25.13, -27.33) * mm, v(-24.34, -26.7) * mm, v(-24.18, -25.97) * mm, v(-24.73, -25.43) * mm]});
            skFitSpline(sketch, "E980", {"points": [v(-24.73, -25.43) * mm, v(-25.28, -24.88) * mm, v(-25.65, -25.04) * mm, v(-25.14, -25.6) * mm]});
            skFitSpline(sketch, "E981", {"points": [v(-25.14, -25.6) * mm, v(-24.62, -26.18) * mm, v(-24.54, -26.67) * mm, v(-24.93, -26.9) * mm]});
            skFitSpline(sketch, "E982", {"points": [v(-24.93, -26.9) * mm, v(-25.07, -27) * mm, v(-25.12, -26.82) * mm, v(-25.05, -26.53) * mm]});
            skFitSpline(sketch, "E983", {"points": [v(-25.05, -26.53) * mm, v(-24.85, -25.78) * mm, v(-25.33, -25.58) * mm, v(-27.46, -25.51) * mm]});
            skFitSpline(sketch, "E984", {"points": [v(-27.46, -25.51) * mm, v(-28.5, -25.48) * mm, v(-29.6, -25.36) * mm, v(-29.94, -25.24) * mm]});
            skFitSpline(sketch, "E985", {"points": [v(-29.94, -25.24) * mm, v(-30.4, -25.08) * mm, v(-30.63, -25.18) * mm, v(-30.87, -25.63) * mm]});
            skFitSpline(sketch, "E986", {"points": [v(-30.87, -25.63) * mm, v(-31.15, -26.15) * mm, v(-31.07, -26.35) * mm, v(-30.35, -27.07) * mm]});
            skFitSpline(sketch, "E987", {"points": [v(-30.35, -27.07) * mm, v(-29.6, -27.83) * mm, v(-29.34, -27.91) * mm, v(-27.7, -27.91) * mm]});
            skFitSpline(sketch, "E988", {"points": [v(-27.7, -27.91) * mm, v(-26.28, -27.91) * mm, v(-25.71, -27.78) * mm, v(-25.13, -27.33) * mm]});
            skFitSpline(sketch, "E989", {"points": [v(-28.15, -27.44) * mm, v(-28.26, -27.34) * mm, v(-28.34, -27.05) * mm, v(-28.33, -26.8) * mm]});
            skFitSpline(sketch, "E990", {"points": [v(-28.33, -26.8) * mm, v(-28.33, -26.44) * mm, v(-28.27, -26.45) * mm, v(-28.03, -26.87) * mm]});
            skFitSpline(sketch, "E991", {"points": [v(-28.03, -26.87) * mm, v(-27.72, -27.4) * mm, v(-27.8, -27.78) * mm, v(-28.15, -27.44) * mm]});
            skFitSpline(sketch, "E992", {"points": [v(-27.2, -26.94) * mm, v(-27.21, -26.33) * mm, v(-27.13, -26.19) * mm, v(-26.9, -26.42) * mm]});
            skFitSpline(sketch, "E993", {"points": [v(-26.9, -26.42) * mm, v(-26.68, -26.64) * mm, v(-26.68, -26.87) * mm, v(-26.9, -27.25) * mm]});
            skFitSpline(sketch, "E994", {"points": [v(-26.9, -27.25) * mm, v(-27.16, -27.7) * mm, v(-27.2, -27.67) * mm, v(-27.2, -26.94) * mm]});
            skFitSpline(sketch, "E995", {"points": [v(-29.43, -26.78) * mm, v(-29.43, -26.4) * mm, v(-29.36, -26.23) * mm, v(-29.28, -26.43) * mm]});
            skFitSpline(sketch, "E996", {"points": [v(-29.28, -26.43) * mm, v(-29.2, -26.62) * mm, v(-29.2, -26.94) * mm, v(-29.28, -27.13) * mm]});
            skFitSpline(sketch, "E997", {"points": [v(-29.28, -27.13) * mm, v(-29.36, -27.33) * mm, v(-29.43, -27.17) * mm, v(-29.43, -26.78) * mm]});
            skFitSpline(sketch, "E998", {"points": [v(-26.08, -26.64) * mm, v(-26.08, -26.22) * mm, v(-25.96, -25.98) * mm, v(-25.8, -26.08) * mm]});
            skFitSpline(sketch, "E999", {"points": [v(-25.8, -26.08) * mm, v(-25.65, -26.17) * mm, v(-25.52, -26.43) * mm, v(-25.52, -26.64) * mm]});
            skFitSpline(sketch, "E1000", {"points": [v(-25.52, -26.64) * mm, v(-25.52, -26.85) * mm, v(-25.65, -27.1) * mm, v(-25.8, -27.2) * mm]});
            skFitSpline(sketch, "E1001", {"points": [v(-25.8, -27.2) * mm, v(-25.96, -27.3) * mm, v(-26.08, -27.06) * mm, v(-26.08, -26.64) * mm]});
            skFitSpline(sketch, "E1002", {"points": [v(-30.41, -26.88) * mm, v(-30.52, -26.77) * mm, v(-30.6, -26.42) * mm, v(-30.58, -26.1) * mm]});
            skFitSpline(sketch, "E1003", {"points": [v(-30.58, -26.1) * mm, v(-30.57, -25.56) * mm, v(-30.54, -25.57) * mm, v(-30.3, -26.19) * mm]});
            skFitSpline(sketch, "E1004", {"points": [v(-30.3, -26.19) * mm, v(-30.02, -26.88) * mm, v(-30.07, -27.21) * mm, v(-30.41, -26.88) * mm]});
            skFitSpline(sketch, "E1005", {"points": [v(29.23, -27.49) * mm, v(30.23, -26.97) * mm, v(30.58, -26.03) * mm, v(29.98, -25.44) * mm]});
            skFitSpline(sketch, "E1006", {"points": [v(29.98, -25.44) * mm, v(29.62, -25.07) * mm, v(29.42, -25.06) * mm, v(28.7, -25.36) * mm]});
            skFitSpline(sketch, "E1007", {"points": [v(28.7, -25.36) * mm, v(28.23, -25.55) * mm, v(27.12, -25.67) * mm, v(26.22, -25.61) * mm]});
            skFitSpline(sketch, "E1008", {"points": [v(26.22, -25.61) * mm, v(24.6, -25.51) * mm, v(24.58, -25.52) * mm, v(24.43, -26.36) * mm]});
            skFitSpline(sketch, "E1009", {"points": [v(24.43, -26.36) * mm, v(24.3, -27.07) * mm, v(24.24, -27.12) * mm, v(24.07, -26.67) * mm]});
            skFitSpline(sketch, "E1010", {"points": [v(24.07, -26.67) * mm, v(23.93, -26.32) * mm, v(24.03, -25.94) * mm, v(24.36, -25.57) * mm]});
            skFitSpline(sketch, "E1011", {"points": [v(24.36, -25.57) * mm, v(24.72, -25.16) * mm, v(24.74, -25.04) * mm, v(24.45, -25.13) * mm]});
            skFitSpline(sketch, "E1012", {"points": [v(24.45, -25.13) * mm, v(23.24, -25.52) * mm, v(23.4, -26.86) * mm, v(24.74, -27.55) * mm]});
            skFitSpline(sketch, "E1013", {"points": [v(24.74, -27.55) * mm, v(25.68, -28.03) * mm, v(28.24, -28) * mm, v(29.23, -27.49) * mm]});
            skFitSpline(sketch, "E1014", {"points": [v(26.18, -26.92) * mm, v(26.19, -26.46) * mm, v(26.25, -26.3) * mm, v(26.32, -26.57) * mm]});
            skFitSpline(sketch, "E1015", {"points": [v(26.32, -26.57) * mm, v(26.4, -26.85) * mm, v(26.39, -27.23) * mm, v(26.31, -27.42) * mm]});
            skFitSpline(sketch, "E1016", {"points": [v(26.31, -27.42) * mm, v(26.23, -27.61) * mm, v(26.18, -27.39) * mm, v(26.18, -26.92) * mm]});
            skLineSegment(sketch, "E1017", {"start": v(26.18, -26.92) * mm, "end": v(26.18, -26.92) * mm});
            skFitSpline(sketch, "E1018", {"points": [v(27.31, -26.92) * mm, v(27.32, -26.46) * mm, v(27.38, -26.3) * mm, v(27.45, -26.57) * mm]});
            skFitSpline(sketch, "E1019", {"points": [v(27.45, -26.57) * mm, v(27.52, -26.85) * mm, v(27.52, -27.23) * mm, v(27.44, -27.42) * mm]});
            skFitSpline(sketch, "E1020", {"points": [v(27.44, -27.42) * mm, v(27.36, -27.61) * mm, v(27.3, -27.39) * mm, v(27.31, -26.92) * mm]});
            skFitSpline(sketch, "E1021", {"points": [v(25.05, -26.64) * mm, v(25.06, -26.17) * mm, v(25.12, -26.02) * mm, v(25.2, -26.3) * mm]});
            skFitSpline(sketch, "E1022", {"points": [v(25.2, -26.3) * mm, v(25.27, -26.57) * mm, v(25.26, -26.95) * mm, v(25.18, -27.14) * mm]});
            skFitSpline(sketch, "E1023", {"points": [v(25.18, -27.14) * mm, v(25.1, -27.33) * mm, v(25.05, -27.1) * mm, v(25.05, -26.64) * mm]});
            skFitSpline(sketch, "E1024", {"points": [v(28.44, -26.64) * mm, v(28.45, -26.17) * mm, v(28.5, -26.02) * mm, v(28.58, -26.3) * mm]});
            skFitSpline(sketch, "E1025", {"points": [v(28.58, -26.3) * mm, v(28.65, -26.57) * mm, v(28.65, -26.95) * mm, v(28.57, -27.14) * mm]});
            skFitSpline(sketch, "E1026", {"points": [v(28.57, -27.14) * mm, v(28.5, -27.33) * mm, v(28.43, -27.1) * mm, v(28.44, -26.64) * mm]});
            skLineSegment(sketch, "E1027", {"start": v(28.44, -26.64) * mm, "end": v(28.44, -26.64) * mm});
            skFitSpline(sketch, "E1028", {"points": [v(29.48, -26.15) * mm, v(29.6, -25.37) * mm, v(29.65, -25.33) * mm, v(29.74, -25.9) * mm]});
            skFitSpline(sketch, "E1029", {"points": [v(29.74, -25.9) * mm, v(29.8, -26.26) * mm, v(29.73, -26.68) * mm, v(29.59, -26.82) * mm]});
            skFitSpline(sketch, "E1030", {"points": [v(29.59, -26.82) * mm, v(29.43, -26.98) * mm, v(29.39, -26.72) * mm, v(29.48, -26.15) * mm]});
            skFitSpline(sketch, "E1031", {"points": [v(-26.44, -25.2) * mm, v(-25.64, -24.98) * mm, v(-25.62, -24.26) * mm, v(-26.39, -23.3) * mm]});
            skFitSpline(sketch, "E1032", {"points": [v(-26.39, -23.3) * mm, v(-26.96, -22.56) * mm, v(-27.8, -22.36) * mm, v(-28.75, -22.72) * mm]});
            skFitSpline(sketch, "E1033", {"points": [v(-28.75, -22.72) * mm, v(-29.26, -22.92) * mm, v(-30.17, -24.49) * mm, v(-29.92, -24.74) * mm]});
            skFitSpline(sketch, "E1034", {"points": [v(-29.92, -24.74) * mm, v(-29.83, -24.83) * mm, v(-29.75, -24.72) * mm, v(-29.75, -24.5) * mm]});
            skFitSpline(sketch, "E1035", {"points": [v(-29.75, -24.5) * mm, v(-29.75, -24.17) * mm, v(-29.7, -24.17) * mm, v(-29.45, -24.52) * mm]});
            skFitSpline(sketch, "E1036", {"points": [v(-29.45, -24.52) * mm, v(-29.21, -24.86) * mm, v(-29.19, -24.82) * mm, v(-29.32, -24.34) * mm]});
            skFitSpline(sketch, "E1037", {"points": [v(-29.32, -24.34) * mm, v(-29.42, -23.99) * mm, v(-29.35, -23.63) * mm, v(-29.16, -23.52) * mm]});
            skFitSpline(sketch, "E1038", {"points": [v(-29.16, -23.52) * mm, v(-28.95, -23.39) * mm, v(-28.9, -23.43) * mm, v(-29, -23.6) * mm]});
            skFitSpline(sketch, "E1039", {"points": [v(-29, -23.6) * mm, v(-29.1, -23.78) * mm, v(-29.07, -24.24) * mm, v(-28.92, -24.64) * mm]});
            skFitSpline(sketch, "E1040", {"points": [v(-28.92, -24.64) * mm, v(-28.63, -25.4) * mm, v(-27.85, -25.57) * mm, v(-26.44, -25.2) * mm]});
            skLineSegment(sketch, "E1041", {"start": v(-26.44, -25.2) * mm, "end": v(-26.44, -25.2) * mm});
            skFitSpline(sketch, "E1042", {"points": [v(27.92, -25.2) * mm, v(28.17, -25.1) * mm, v(28.28, -24.86) * mm, v(28.18, -24.6) * mm]});
            skFitSpline(sketch, "E1043", {"points": [v(28.18, -24.6) * mm, v(28.06, -24.28) * mm, v(28.11, -24.22) * mm, v(28.37, -24.37) * mm]});
            skFitSpline(sketch, "E1044", {"points": [v(28.37, -24.37) * mm, v(28.64, -24.54) * mm, v(28.68, -24.42) * mm, v(28.54, -23.92) * mm]});
            skFitSpline(sketch, "E1045", {"points": [v(28.54, -23.92) * mm, v(28.36, -23.25) * mm, v(28.36, -23.25) * mm, v(28.79, -23.96) * mm]});
            skFitSpline(sketch, "E1046", {"points": [v(28.79, -23.96) * mm, v(29.02, -24.35) * mm, v(29.22, -24.52) * mm, v(29.22, -24.35) * mm]});
            skFitSpline(sketch, "E1047", {"points": [v(29.22, -24.35) * mm, v(29.23, -24.18) * mm, v(28.97, -23.7) * mm, v(28.65, -23.3) * mm]});
            skFitSpline(sketch, "E1048", {"points": [v(28.65, -23.3) * mm, v(28.07, -22.56) * mm, v(26.91, -22.3) * mm, v(26.25, -22.76) * mm]});
            skFitSpline(sketch, "E1049", {"points": [v(26.25, -22.76) * mm, v(25.8, -23.08) * mm, v(25, -24.32) * mm, v(25, -24.7) * mm]});
            skFitSpline(sketch, "E1050", {"points": [v(25, -24.7) * mm, v(25, -25.23) * mm, v(26.97, -25.57) * mm, v(27.92, -25.2) * mm]});
            skFitSpline(sketch, "E1051", {"points": [v(-32.58, -14.83) * mm, v(-32.58, -14.09) * mm, v(-33.11, -13.53) * mm, v(-34.51, -12.82) * mm]});
            skFitSpline(sketch, "E1052", {"points": [v(-34.51, -12.82) * mm, v(-35.73, -12.2) * mm, v(-35.39, -11.88) * mm, v(-33.42, -11.77) * mm]});
            skLineSegment(sketch, "E1053", {"start": v(-33.42, -11.77) * mm, "end": v(-31.87, -11.68) * mm});
            skLineSegment(sketch, "E1054", {"start": v(-31.87, -11.68) * mm, "end": v(-31.91, -10.7) * mm});
            skFitSpline(sketch, "E1055", {"points": [v(-31.91, -10.7) * mm, v(-31.94, -10.15) * mm, v(-32.05, -9.36) * mm, v(-32.16, -8.94) * mm]});
            skFitSpline(sketch, "E1056", {"points": [v(-32.16, -8.94) * mm, v(-32.27, -8.51) * mm, v(-32.27, -7.83) * mm, v(-32.17, -7.43) * mm]});
            skFitSpline(sketch, "E1057", {"points": [v(-32.17, -7.43) * mm, v(-32, -6.73) * mm, v(-31.9, -6.7) * mm, v(-30.45, -6.79) * mm]});
            skLineSegment(sketch, "E1058", {"start": v(-30.45, -6.79) * mm, "end": v(-28.9, -6.88) * mm});
            skLineSegment(sketch, "E1059", {"start": v(-28.9, -6.88) * mm, "end": v(-28.9, -5.98) * mm});
            skFitSpline(sketch, "E1060", {"points": [v(-28.9, -5.98) * mm, v(-28.9, -4.85) * mm, v(-28.37, -3.64) * mm, v(-27.87, -3.64) * mm]});
            skFitSpline(sketch, "E1061", {"points": [v(-27.87, -3.64) * mm, v(-27.44, -3.64) * mm, v(-27.4, -3.38) * mm, v(-27.75, -2.83) * mm]});
            skFitSpline(sketch, "E1062", {"points": [v(-27.75, -2.83) * mm, v(-27.95, -2.52) * mm, v(-28.04, -2.56) * mm, v(-28.19, -3.04) * mm]});
            skFitSpline(sketch, "E1063", {"points": [v(-28.19, -3.04) * mm, v(-28.43, -3.8) * mm, v(-28.7, -3.8) * mm, v(-29.05, -3) * mm]});
            skFitSpline(sketch, "E1064", {"points": [v(-29.05, -3) * mm, v(-29.52, -1.94) * mm, v(-30.14, -2.24) * mm, v(-30.5, -3.7) * mm]});
            skFitSpline(sketch, "E1065", {"points": [v(-30.5, -3.7) * mm, v(-30.88, -5.2) * mm, v(-31.08, -5.61) * mm, v(-31.47, -5.61) * mm]});
            skFitSpline(sketch, "E1066", {"points": [v(-31.47, -5.61) * mm, v(-31.61, -5.61) * mm, v(-31.58, -5.36) * mm, v(-31.39, -5.06) * mm]});
            skFitSpline(sketch, "E1067", {"points": [v(-31.39, -5.06) * mm, v(-30.95, -4.36) * mm, v(-31.5, -3.61) * mm, v(-32.12, -4.07) * mm]});
            skFitSpline(sketch, "E1068", {"points": [v(-32.12, -4.07) * mm, v(-33.71, -5.24) * mm, v(-34.2, -5.46) * mm, v(-35.16, -5.46) * mm]});
            skFitSpline(sketch, "E1069", {"points": [v(-35.16, -5.46) * mm, v(-35.8, -5.46) * mm, v(-36.43, -5.26) * mm, v(-36.72, -4.97) * mm]});
            skFitSpline(sketch, "E1070", {"points": [v(-36.72, -4.97) * mm, v(-37.19, -4.51) * mm, v(-37.16, -4.49) * mm, v(-36.2, -4.49) * mm]});
            skFitSpline(sketch, "E1071", {"points": [v(-36.2, -4.49) * mm, v(-34.95, -4.49) * mm, v(-33.99, -3.58) * mm, v(-34.46, -2.85) * mm]});
            skFitSpline(sketch, "E1072", {"points": [v(-34.46, -2.85) * mm, v(-34.63, -2.58) * mm, v(-34.98, -2.4) * mm, v(-35.24, -2.45) * mm]});
            skFitSpline(sketch, "E1073", {"points": [v(-35.24, -2.45) * mm, v(-35.5, -2.5) * mm, v(-36.09, -2.22) * mm, v(-36.56, -1.82) * mm]});
            skFitSpline(sketch, "E1074", {"points": [v(-36.56, -1.82) * mm, v(-37.03, -1.42) * mm, v(-37.52, -1.1) * mm, v(-37.66, -1.1) * mm]});
            skFitSpline(sketch, "E1075", {"points": [v(-37.66, -1.1) * mm, v(-37.79, -1.1) * mm, v(-38.27, -0.78) * mm, v(-38.73, -0.4) * mm]});
            skLineSegment(sketch, "E1076", {"start": v(-38.73, -0.4) * mm, "end": v(-39.56, 0.3) * mm});
            skLineSegment(sketch, "E1077", {"start": v(-39.56, 0.3) * mm, "end": v(-39.5, -0.6) * mm});
            skFitSpline(sketch, "E1078", {"points": [v(-39.5, -0.6) * mm, v(-39.45, -1.35) * mm, v(-39.19, -1.7) * mm, v(-38.1, -2.44) * mm]});
            skFitSpline(sketch, "E1079", {"points": [v(-38.1, -2.44) * mm, v(-37.35, -2.94) * mm, v(-36.92, -3.36) * mm, v(-37.14, -3.36) * mm]});
            skFitSpline(sketch, "E1080", {"points": [v(-37.14, -3.36) * mm, v(-37.36, -3.36) * mm, v(-38.08, -2.96) * mm, v(-38.73, -2.49) * mm]});
            skFitSpline(sketch, "E1081", {"points": [v(-38.73, -2.49) * mm, v(-39.38, -2) * mm, v(-39.91, -1.77) * mm, v(-39.91, -1.95) * mm]});
            skFitSpline(sketch, "E1082", {"points": [v(-39.91, -1.95) * mm, v(-39.91, -2.3) * mm, v(-41, -2.23) * mm, v(-41.96, -1.81) * mm]});
            skFitSpline(sketch, "E1083", {"points": [v(-41.96, -1.81) * mm, v(-42.41, -1.62) * mm, v(-42.43, -1.68) * mm, v(-42.16, -2.4) * mm]});
            skFitSpline(sketch, "E1084", {"points": [v(-42.16, -2.4) * mm, v(-41.4, -4.39) * mm, v(-39.37, -6.07) * mm, v(-36.73, -6.9) * mm]});
            skFitSpline(sketch, "E1085", {"points": [v(-36.73, -6.9) * mm, v(-36.07, -7.1) * mm, v(-35.76, -7.28) * mm, v(-36.02, -7.29) * mm]});
            skFitSpline(sketch, "E1086", {"points": [v(-36.02, -7.29) * mm, v(-37.15, -7.33) * mm, v(-39.68, -6.09) * mm, v(-40.86, -4.9) * mm]});
            skFitSpline(sketch, "E1087", {"points": [v(-40.86, -4.9) * mm, v(-41.8, -3.96) * mm, v(-42.24, -3.7) * mm, v(-42.72, -3.83) * mm]});
            skFitSpline(sketch, "E1088", {"points": [v(-42.72, -3.83) * mm, v(-43.33, -4) * mm, v(-43.33, -4) * mm, v(-42.52, -4.88) * mm]});
            skFitSpline(sketch, "E1089", {"points": [v(-42.52, -4.88) * mm, v(-42.07, -5.36) * mm, v(-41.36, -6.35) * mm, v(-40.95, -7.07) * mm]});
            skFitSpline(sketch, "E1090", {"points": [v(-40.95, -7.07) * mm, v(-40.54, -7.8) * mm, v(-39.66, -8.85) * mm, v(-39, -9.42) * mm]});
            skFitSpline(sketch, "E1091", {"points": [v(-39, -9.42) * mm, v(-37.72, -10.53) * mm, v(-38.03, -10.5) * mm, v(-39.56, -9.37) * mm]});
            skFitSpline(sketch, "E1092", {"points": [v(-39.56, -9.37) * mm, v(-40.48, -8.7) * mm, v(-40.48, -8.7) * mm, v(-40.48, -9.3) * mm]});
            skFitSpline(sketch, "E1093", {"points": [v(-40.48, -9.3) * mm, v(-40.48, -10.2) * mm, v(-39.45, -11.48) * mm, v(-38.23, -12.1) * mm]});
            skFitSpline(sketch, "E1094", {"points": [v(-38.23, -12.1) * mm, v(-37.64, -12.4) * mm, v(-36.75, -13.16) * mm, v(-36.26, -13.77) * mm]});
            skFitSpline(sketch, "E1095", {"points": [v(-36.26, -13.77) * mm, v(-35.45, -14.8) * mm, v(-34.64, -15.2) * mm, v(-32.79, -15.46) * mm]});
            skFitSpline(sketch, "E1096", {"points": [v(-32.79, -15.46) * mm, v(-32.67, -15.48) * mm, v(-32.58, -15.2) * mm, v(-32.58, -14.83) * mm]});
            skFitSpline(sketch, "E1097", {"points": [v(-35.19, -9.65) * mm, v(-34.84, -9.58) * mm, v(-34.27, -9.58) * mm, v(-33.92, -9.65) * mm]});
            skFitSpline(sketch, "E1098", {"points": [v(-33.92, -9.65) * mm, v(-33.57, -9.72) * mm, v(-33.85, -9.77) * mm, v(-34.55, -9.77) * mm]});
            skFitSpline(sketch, "E1099", {"points": [v(-34.55, -9.77) * mm, v(-35.25, -9.77) * mm, v(-35.54, -9.72) * mm, v(-35.19, -9.65) * mm]});
            skFitSpline(sketch, "E1100", {"points": [v(-37.58, -9.14) * mm, v(-38.09, -8.93) * mm, v(-38.5, -8.68) * mm, v(-38.5, -8.6) * mm]});
            skFitSpline(sketch, "E1101", {"points": [v(-38.5, -8.6) * mm, v(-38.5, -8.53) * mm, v(-38.09, -8.63) * mm, v(-37.58, -8.84) * mm]});
            skFitSpline(sketch, "E1102", {"points": [v(-37.58, -8.84) * mm, v(-37.08, -9.04) * mm, v(-36.48, -9.28) * mm, v(-36.24, -9.37) * mm]});
            skFitSpline(sketch, "E1103", {"points": [v(-36.24, -9.37) * mm, v(-35.87, -9.5) * mm, v(-35.87, -9.52) * mm, v(-36.24, -9.53) * mm]});
            skFitSpline(sketch, "E1104", {"points": [v(-36.24, -9.53) * mm, v(-36.48, -9.54) * mm, v(-37.08, -9.36) * mm, v(-37.58, -9.14) * mm]});
            skFitSpline(sketch, "E1105", {"points": [v(-36.39, -8.58) * mm, v(-36.54, -8.53) * mm, v(-37.03, -8.4) * mm, v(-37.48, -8.3) * mm]});
            skFitSpline(sketch, "E1106", {"points": [v(-37.48, -8.3) * mm, v(-39.08, -7.95) * mm, v(-38.03, -7.94) * mm, v(-36.24, -8.3) * mm]});
            skFitSpline(sketch, "E1107", {"points": [v(-36.24, -8.3) * mm, v(-35.24, -8.5) * mm, v(-34.8, -8.67) * mm, v(-35.26, -8.67) * mm]});
            skFitSpline(sketch, "E1108", {"points": [v(-35.26, -8.67) * mm, v(-35.72, -8.67) * mm, v(-36.23, -8.63) * mm, v(-36.39, -8.58) * mm]});
            skFitSpline(sketch, "E1109", {"points": [v(-40.08, -6.86) * mm, v(-40.8, -6.2) * mm, v(-40.88, -6.07) * mm, v(-40.3, -6.5) * mm]});
            skFitSpline(sketch, "E1110", {"points": [v(-40.3, -6.5) * mm, v(-39.82, -6.87) * mm, v(-39.19, -7.32) * mm, v(-38.9, -7.5) * mm]});
            skFitSpline(sketch, "E1111", {"points": [v(-38.9, -7.5) * mm, v(-38.6, -7.69) * mm, v(-38.5, -7.85) * mm, v(-38.67, -7.86) * mm]});
            skFitSpline(sketch, "E1112", {"points": [v(-38.67, -7.86) * mm, v(-38.83, -7.86) * mm, v(-39.47, -7.42) * mm, v(-40.08, -6.86) * mm]});
            skFitSpline(sketch, "E1113", {"points": [v(37.65, -14.55) * mm, v(38.02, -14.21) * mm, v(38.52, -13.56) * mm, v(38.77, -13.1) * mm]});
            skLineSegment(sketch, "E1114", {"start": v(38.77, -13.1) * mm, "end": v(39.21, -12.25) * mm});
            skLineSegment(sketch, "E1115", {"start": v(39.21, -12.25) * mm, "end": v(39.47, -13.13) * mm});
            skFitSpline(sketch, "E1116", {"points": [v(39.47, -13.13) * mm, v(39.65, -13.72) * mm, v(40.05, -14.16) * mm, v(40.7, -14.47) * mm]});
            skFitSpline(sketch, "E1117", {"points": [v(40.7, -14.47) * mm, v(41.23, -14.72) * mm, v(41.71, -14.93) * mm, v(41.77, -14.93) * mm]});
            skFitSpline(sketch, "E1118", {"points": [v(41.77, -14.93) * mm, v(42.15, -14.93) * mm, v(42.15, -13.8) * mm, v(41.77, -12.5) * mm]});
            skFitSpline(sketch, "E1119", {"points": [v(41.77, -12.5) * mm, v(41.53, -11.67) * mm, v(41.4, -10.86) * mm, v(41.5, -10.72) * mm]});
            skFitSpline(sketch, "E1120", {"points": [v(41.5, -10.72) * mm, v(41.58, -10.57) * mm, v(41.4, -10.37) * mm, v(41.08, -10.27) * mm]});
            skFitSpline(sketch, "E1121", {"points": [v(41.08, -10.27) * mm, v(40.74, -10.16) * mm, v(40.6, -9.96) * mm, v(40.71, -9.76) * mm]});
            skFitSpline(sketch, "E1122", {"points": [v(40.71, -9.76) * mm, v(40.82, -9.57) * mm, v(39.84, -10.37) * mm, v(38.53, -11.52) * mm]});
            skLineSegment(sketch, "E1123", {"start": v(38.53, -11.52) * mm, "end": v(36.15, -13.62) * mm});
            skLineSegment(sketch, "E1124", {"start": v(36.15, -13.62) * mm, "end": v(38.37, -11.34) * mm});
            skFitSpline(sketch, "E1125", {"points": [v(38.37, -11.34) * mm, v(39.59, -10.09) * mm, v(40.51, -8.94) * mm, v(40.42, -8.79) * mm]});
            skFitSpline(sketch, "E1126", {"points": [v(40.42, -8.79) * mm, v(40.33, -8.64) * mm, v(40.5, -8) * mm, v(40.8, -7.38) * mm]});
            skFitSpline(sketch, "E1127", {"points": [v(40.8, -7.38) * mm, v(41.2, -6.55) * mm, v(41.85, -5.92) * mm, v(43.17, -5.1) * mm]});
            skFitSpline(sketch, "E1128", {"points": [v(43.17, -5.1) * mm, v(44.17, -4.46) * mm, v(45.09, -3.78) * mm, v(45.2, -3.58) * mm]});
            skFitSpline(sketch, "E1129", {"points": [v(45.2, -3.58) * mm, v(45.32, -3.38) * mm, v(45.16, -3.44) * mm, v(44.85, -3.7) * mm]});
            skFitSpline(sketch, "E1130", {"points": [v(44.85, -3.7) * mm, v(44.06, -4.4) * mm, v(43.39, -4.33) * mm, v(43.02, -3.51) * mm]});
            skLineSegment(sketch, "E1131", {"start": v(43.02, -3.51) * mm, "end": v(42.7, -2.82) * mm});
            skLineSegment(sketch, "E1132", {"start": v(42.7, -2.82) * mm, "end": v(41.54, -4.02) * mm});
            skFitSpline(sketch, "E1133", {"points": [v(41.54, -4.02) * mm, v(40.9, -4.68) * mm, v(40.7, -4.84) * mm, v(41.1, -4.36) * mm]});
            skFitSpline(sketch, "E1134", {"points": [v(41.1, -4.36) * mm, v(41.94, -3.36) * mm, v(42.6, -2.33) * mm, v(42.88, -1.52) * mm]});
            skFitSpline(sketch, "E1135", {"points": [v(42.88, -1.52) * mm, v(43, -1.21) * mm, v(42.67, -1.47) * mm, v(42.17, -2.09) * mm]});
            skFitSpline(sketch, "E1136", {"points": [v(42.17, -2.09) * mm, v(40.98, -3.56) * mm, v(39, -5.5) * mm, v(38.3, -5.87) * mm]});
            skFitSpline(sketch, "E1137", {"points": [v(38.3, -5.87) * mm, v(38, -6.04) * mm, v(38.78, -5.16) * mm, v(40.04, -3.92) * mm]});
            skFitSpline(sketch, "E1138", {"points": [v(40.04, -3.92) * mm, v(41.3, -2.69) * mm, v(42.24, -1.6) * mm, v(42.14, -1.5) * mm]});
            skFitSpline(sketch, "E1139", {"points": [v(42.14, -1.5) * mm, v(42.03, -1.39) * mm, v(41.36, -1.93) * mm, v(40.64, -2.68) * mm]});
            skFitSpline(sketch, "E1140", {"points": [v(40.64, -2.68) * mm, v(39.86, -3.5) * mm, v(39.68, -3.63) * mm, v(40.2, -3) * mm]});
            skFitSpline(sketch, "E1141", {"points": [v(40.2, -3) * mm, v(41.03, -2) * mm, v(41.06, -1.89) * mm, v(40.65, -1.27) * mm]});
            skFitSpline(sketch, "E1142", {"points": [v(40.65, -1.27) * mm, v(40.42, -0.9) * mm, v(40.2, -0.12) * mm, v(40.18, 0.49) * mm]});
            skLineSegment(sketch, "E1143", {"start": v(40.18, 0.49) * mm, "end": v(40.14, 1.58) * mm});
            skLineSegment(sketch, "E1144", {"start": v(40.14, 1.58) * mm, "end": v(39.74, 0.6) * mm});
            skFitSpline(sketch, "E1145", {"points": [v(39.74, 0.6) * mm, v(38.91, -1.45) * mm, v(38.1, -2.2) * mm, v(35.9, -2.91) * mm]});
            skFitSpline(sketch, "E1146", {"points": [v(35.9, -2.91) * mm, v(35.42, -3.07) * mm, v(35.41, -3.14) * mm, v(35.8, -3.71) * mm]});
            skFitSpline(sketch, "E1147", {"points": [v(35.8, -3.71) * mm, v(36.03, -4.08) * mm, v(36.62, -4.41) * mm, v(37.17, -4.5) * mm]});
            skLineSegment(sketch, "E1148", {"start": v(37.17, -4.5) * mm, "end": v(38.12, -4.66) * mm});
            skLineSegment(sketch, "E1149", {"start": v(38.12, -4.66) * mm, "end": v(37.37, -5.03) * mm});
            skFitSpline(sketch, "E1150", {"points": [v(37.37, -5.03) * mm, v(36.73, -5.35) * mm, v(36.37, -5.31) * mm, v(34.75, -4.77) * mm]});
            skFitSpline(sketch, "E1151", {"points": [v(34.75, -4.77) * mm, v(32.8, -4.13) * mm, v(31.6, -4.17) * mm, v(31.3, -4.91) * mm]});
            skFitSpline(sketch, "E1152", {"points": [v(31.3, -4.91) * mm, v(31.22, -5.13) * mm, v(31.36, -5.53) * mm, v(31.62, -5.8) * mm]});
            skFitSpline(sketch, "E1153", {"points": [v(31.62, -5.8) * mm, v(31.89, -6.05) * mm, v(32.03, -6.5) * mm, v(31.95, -6.8) * mm]});
            skFitSpline(sketch, "E1154", {"points": [v(31.95, -6.8) * mm, v(31.85, -7.2) * mm, v(31.93, -7.3) * mm, v(32.24, -7.19) * mm]});
            skFitSpline(sketch, "E1155", {"points": [v(32.24, -7.19) * mm, v(32.48, -7.1) * mm, v(33.14, -7.27) * mm, v(33.7, -7.57) * mm]});
            skFitSpline(sketch, "E1156", {"points": [v(33.7, -7.57) * mm, v(34.27, -7.87) * mm, v(35.2, -8.2) * mm, v(35.75, -8.28) * mm]});
            skFitSpline(sketch, "E1157", {"points": [v(35.75, -8.28) * mm, v(36.31, -8.37) * mm, v(37, -8.7) * mm, v(37.28, -9) * mm]});
            skFitSpline(sketch, "E1158", {"points": [v(37.28, -9) * mm, v(37.77, -9.54) * mm, v(37.77, -9.59) * mm, v(37.25, -10.16) * mm]});
            skFitSpline(sketch, "E1159", {"points": [v(37.25, -10.16) * mm, v(36.95, -10.49) * mm, v(36.1, -11.06) * mm, v(35.36, -11.44) * mm]});
            skFitSpline(sketch, "E1160", {"points": [v(35.36, -11.44) * mm, v(33.93, -12.17) * mm, v(33.47, -12.9) * mm, v(33.46, -14.45) * mm]});
            skLineSegment(sketch, "E1161", {"start": v(33.46, -14.45) * mm, "end": v(33.46, -15.35) * mm});
            skLineSegment(sketch, "E1162", {"start": v(33.46, -15.35) * mm, "end": v(35.23, -15.26) * mm});
            skFitSpline(sketch, "E1163", {"points": [v(35.23, -15.26) * mm, v(36.56, -15.18) * mm, v(37.16, -15) * mm, v(37.65, -14.55) * mm]});
            skLineSegment(sketch, "E1164", {"start": v(37.65, -14.55) * mm, "end": v(37.65, -14.55) * mm});
            skFitSpline(sketch, "E1165", {"points": [v(35.16, -14.26) * mm, v(35.16, -14.2) * mm, v(35.38, -13.98) * mm, v(35.65, -13.76) * mm]});
            skFitSpline(sketch, "E1166", {"points": [v(35.65, -13.76) * mm, v(36.1, -13.41) * mm, v(36.1, -13.42) * mm, v(35.76, -13.87) * mm]});
            skFitSpline(sketch, "E1167", {"points": [v(35.76, -13.87) * mm, v(35.39, -14.34) * mm, v(35.16, -14.49) * mm, v(35.16, -14.26) * mm]});
            skFitSpline(sketch, "E1168", {"points": [v(38.4, -10.46) * mm, v(39.32, -9.5) * mm, v(40.12, -8.72) * mm, v(40.17, -8.72) * mm]});
            skFitSpline(sketch, "E1169", {"points": [v(40.17, -8.72) * mm, v(40.48, -8.72) * mm, v(39.2, -10.17) * mm, v(38.06, -11.1) * mm]});
            skFitSpline(sketch, "E1170", {"points": [v(38.06, -11.1) * mm, v(36.76, -12.16) * mm, v(36.77, -12.14) * mm, v(38.4, -10.46) * mm]});
            skFitSpline(sketch, "E1171", {"points": [v(39.34, -11.38) * mm, v(39.7, -10.68) * mm, v(40.52, -9.95) * mm, v(40.52, -10.33) * mm]});
            skFitSpline(sketch, "E1172", {"points": [v(40.52, -10.33) * mm, v(40.52, -10.48) * mm, v(40.19, -10.9) * mm, v(39.78, -11.28) * mm]});
            skFitSpline(sketch, "E1173", {"points": [v(39.78, -11.28) * mm, v(39.11, -11.9) * mm, v(39.07, -11.9) * mm, v(39.34, -11.38) * mm]});
            skFitSpline(sketch, "E1174", {"points": [v(30.67, -4.98) * mm, v(30.86, -4.63) * mm, v(31.15, -4.25) * mm, v(31.32, -4.14) * mm]});
            skFitSpline(sketch, "E1175", {"points": [v(31.32, -4.14) * mm, v(31.85, -3.78) * mm, v(34, -3.9) * mm, v(35.04, -4.34) * mm]});
            skLineSegment(sketch, "E1176", {"start": v(35.04, -4.34) * mm, "end": v(36.03, -4.75) * mm});
            skLineSegment(sketch, "E1177", {"start": v(36.03, -4.75) * mm, "end": v(35.45, -4.02) * mm});
            skFitSpline(sketch, "E1178", {"points": [v(35.45, -4.02) * mm, v(34.72, -3.08) * mm, v(34.72, -2.51) * mm, v(35.45, -2.51) * mm]});
            skFitSpline(sketch, "E1179", {"points": [v(35.45, -2.51) * mm, v(37.2, -2.51) * mm, v(39.2, -0.38) * mm, v(39.8, 2.15) * mm]});
            skLineSegment(sketch, "E1180", {"start": v(39.8, 2.15) * mm, "end": v(40, 3) * mm});
            skLineSegment(sketch, "E1181", {"start": v(40, 3) * mm, "end": v(39.06, 2.13) * mm});
            skFitSpline(sketch, "E1182", {"points": [v(39.06, 2.13) * mm, v(38.54, 1.65) * mm, v(37.8, 1.05) * mm, v(37.42, 0.79) * mm]});
            skFitSpline(sketch, "E1183", {"points": [v(37.42, 0.79) * mm, v(37.03, 0.52) * mm, v(36.1, -0.13) * mm, v(35.34, -0.68) * mm]});
            skFitSpline(sketch, "E1184", {"points": [v(35.34, -0.68) * mm, v(33.36, -2.1) * mm, v(31.27, -1.94) * mm, v(30.4, -0.3) * mm]});
            skFitSpline(sketch, "E1185", {"points": [v(30.4, -0.3) * mm, v(30.16, 0.11) * mm, v(30.28, 0.16) * mm, v(31.37, 0.07) * mm]});
            skFitSpline(sketch, "E1186", {"points": [v(31.37, 0.07) * mm, v(32.44, -0.01) * mm, v(32.72, 0.1) * mm, v(33.46, 0.83) * mm]});
            skFitSpline(sketch, "E1187", {"points": [v(33.46, 0.83) * mm, v(34.62, 2) * mm, v(34.54, 2.29) * mm, v(33.05, 2.29) * mm]});
            skFitSpline(sketch, "E1188", {"points": [v(33.05, 2.29) * mm, v(32.35, 2.29) * mm, v(31.27, 2.5) * mm, v(30.64, 2.75) * mm]});
            skFitSpline(sketch, "E1189", {"points": [v(30.64, 2.75) * mm, v(30, 3) * mm, v(29.42, 3.13) * mm, v(29.33, 3.04) * mm]});
            skFitSpline(sketch, "E1190", {"points": [v(29.33, 3.04) * mm, v(29.24, 2.95) * mm, v(29.5, 2.8) * mm, v(29.9, 2.7) * mm]});
            skFitSpline(sketch, "E1191", {"points": [v(29.9, 2.7) * mm, v(30.77, 2.48) * mm, v(30.83, 2.05) * mm, v(30.12, 1.13) * mm]});
            skFitSpline(sketch, "E1192", {"points": [v(30.12, 1.13) * mm, v(29.58, 0.43) * mm, v(29.47, -2.1) * mm, v(29.93, -3.16) * mm]});
            skFitSpline(sketch, "E1193", {"points": [v(29.93, -3.16) * mm, v(30.05, -3.44) * mm, v(30.08, -4.1) * mm, v(29.99, -4.64) * mm]});
            skFitSpline(sketch, "E1194", {"points": [v(29.99, -4.64) * mm, v(29.8, -5.75) * mm, v(30.18, -5.93) * mm, v(30.67, -4.98) * mm]});
            skFitSpline(sketch, "E1195", {"points": [v(-33.32, -4.23) * mm, v(-32.56, -3.78) * mm, v(-31.71, -3.49) * mm, v(-31.42, -3.57) * mm]});
            skFitSpline(sketch, "E1196", {"points": [v(-31.42, -3.57) * mm, v(-31.05, -3.66) * mm, v(-30.88, -3.56) * mm, v(-30.88, -3.25) * mm]});
            skFitSpline(sketch, "E1197", {"points": [v(-30.88, -3.25) * mm, v(-30.88, -2.48) * mm, v(-29.82, -1.6) * mm, v(-29.25, -1.91) * mm]});
            skFitSpline(sketch, "E1198", {"points": [v(-29.25, -1.91) * mm, v(-28.81, -2.15) * mm, v(-28.77, -2.05) * mm, v(-28.86, -1.1) * mm]});
            skFitSpline(sketch, "E1199", {"points": [v(-28.86, -1.1) * mm, v(-28.91, -0.52) * mm, v(-28.82, 0.05) * mm, v(-28.65, 0.15) * mm]});
            skFitSpline(sketch, "E1200", {"points": [v(-28.65, 0.15) * mm, v(-28.48, 0.26) * mm, v(-28.34, 0.66) * mm, v(-28.34, 1.03) * mm]});
            skFitSpline(sketch, "E1201", {"points": [v(-28.34, 1.03) * mm, v(-28.34, 1.9) * mm, v(-27.5, 1.96) * mm, v(-26.01, 1.2) * mm]});
            skFitSpline(sketch, "E1202", {"points": [v(-26.01, 1.2) * mm, v(-25, 0.68) * mm, v(-24.98, 0.68) * mm, v(-25.25, 1.2) * mm]});
            skFitSpline(sketch, "E1203", {"points": [v(-25.25, 1.2) * mm, v(-25.72, 2.05) * mm, v(-27.07, 2.57) * mm, v(-28.82, 2.56) * mm]});
            skFitSpline(sketch, "E1204", {"points": [v(-28.82, 2.56) * mm, v(-30.22, 2.55) * mm, v(-30.6, 2.42) * mm, v(-31.44, 1.71) * mm]});
            skLineSegment(sketch, "E1205", {"start": v(-31.44, 1.71) * mm, "end": v(-32.42, 0.87) * mm});
            skLineSegment(sketch, "E1206", {"start": v(-32.42, 0.87) * mm, "end": v(-31.84, 0.3) * mm});
            skFitSpline(sketch, "E1207", {"points": [v(-31.84, 0.3) * mm, v(-30.98, -0.56) * mm, v(-30.21, -0.16) * mm, v(-30.4, 1.05) * mm]});
            skFitSpline(sketch, "E1208", {"points": [v(-30.4, 1.05) * mm, v(-30.61, 2.3) * mm, v(-30.17, 2.52) * mm, v(-29.63, 1.47) * mm]});
            skFitSpline(sketch, "E1209", {"points": [v(-29.63, 1.47) * mm, v(-28.36, -0.97) * mm, v(-32.25, -3.14) * mm, v(-34.5, -1.25) * mm]});
            skFitSpline(sketch, "E1210", {"points": [v(-34.5, -1.25) * mm, v(-35.31, -0.56) * mm, v(-35.33, -0.55) * mm, v(-35.82, -1.1) * mm]});
            skFitSpline(sketch, "E1211", {"points": [v(-35.82, -1.1) * mm, v(-36.26, -1.58) * mm, v(-36.27, -1.67) * mm, v(-35.89, -1.82) * mm]});
            skFitSpline(sketch, "E1212", {"points": [v(-35.89, -1.82) * mm, v(-35.65, -1.9) * mm, v(-35.23, -1.94) * mm, v(-34.95, -1.9) * mm]});
            skFitSpline(sketch, "E1213", {"points": [v(-34.95, -1.9) * mm, v(-34.64, -1.84) * mm, v(-34.28, -2.1) * mm, v(-34.01, -2.57) * mm]});
            skFitSpline(sketch, "E1214", {"points": [v(-34.01, -2.57) * mm, v(-33.6, -3.3) * mm, v(-33.61, -3.37) * mm, v(-34.4, -4.2) * mm]});
            skFitSpline(sketch, "E1215", {"points": [v(-34.4, -4.2) * mm, v(-35.42, -5.26) * mm, v(-35.1, -5.28) * mm, v(-33.32, -4.23) * mm]});
            skFitSpline(sketch, "E1216", {"points": [v(24.63, -3.71) * mm, v(24.56, -3.44) * mm, v(24.5, -3.6) * mm, v(24.49, -4.06) * mm]});
            skFitSpline(sketch, "E1217", {"points": [v(24.49, -4.06) * mm, v(24.48, -4.53) * mm, v(24.54, -4.75) * mm, v(24.62, -4.56) * mm]});
            skFitSpline(sketch, "E1218", {"points": [v(24.62, -4.56) * mm, v(24.7, -4.37) * mm, v(24.7, -3.99) * mm, v(24.63, -3.71) * mm]});
            skFitSpline(sketch, "E1219", {"points": [v(25.84, -1.6) * mm, v(25.84, -1.2) * mm, v(25.32, -1.63) * mm, v(24.96, -2.31) * mm]});
            skFitSpline(sketch, "E1220", {"points": [v(24.96, -2.31) * mm, v(24.64, -2.93) * mm, v(24.64, -2.93) * mm, v(25.24, -2.4) * mm]});
            skFitSpline(sketch, "E1221", {"points": [v(25.24, -2.4) * mm, v(25.57, -2.1) * mm, v(25.84, -1.74) * mm, v(25.84, -1.6) * mm]});
            skFitSpline(sketch, "E1222", {"points": [v(-27.93, -1.35) * mm, v(-28.45, -0.35) * mm, v(-28.74, -0.42) * mm, v(-28.47, -1.49) * mm]});
            skFitSpline(sketch, "E1223", {"points": [v(-28.47, -1.49) * mm, v(-28.36, -1.9) * mm, v(-28.1, -2.23) * mm, v(-27.88, -2.23) * mm]});
            skFitSpline(sketch, "E1224", {"points": [v(-27.88, -2.23) * mm, v(-27.55, -2.23) * mm, v(-27.56, -2.08) * mm, v(-27.93, -1.35) * mm]});
            skFitSpline(sketch, "E1225", {"points": [v(33.9, -1.1) * mm, v(34.12, -1.1) * mm, v(34.74, -0.7) * mm, v(35.3, -0.21) * mm]});
            skFitSpline(sketch, "E1226", {"points": [v(35.3, -0.21) * mm, v(36.28, 0.65) * mm, v(36.3, 0.68) * mm, v(35.73, 1.07) * mm]});
            skFitSpline(sketch, "E1227", {"points": [v(35.73, 1.07) * mm, v(35.42, 1.3) * mm, v(35.15, 1.75) * mm, v(35.15, 2.1) * mm]});
            skFitSpline(sketch, "E1228", {"points": [v(35.15, 2.1) * mm, v(35.14, 2.55) * mm, v(34.97, 2.37) * mm, v(34.5, 1.44) * mm]});
            skFitSpline(sketch, "E1229", {"points": [v(34.5, 1.44) * mm, v(33.95, 0.37) * mm, v(33.64, 0.1) * mm, v(32.5, -0.29) * mm]});
            skLineSegment(sketch, "E1230", {"start": v(32.5, -0.29) * mm, "end": v(31.13, -0.74) * mm});
            skLineSegment(sketch, "E1231", {"start": v(31.13, -0.74) * mm, "end": v(31.94, -1.04) * mm});
            skFitSpline(sketch, "E1232", {"points": [v(31.94, -1.04) * mm, v(32.4, -1.2) * mm, v(32.93, -1.28) * mm, v(33.13, -1.22) * mm]});
            skFitSpline(sketch, "E1233", {"points": [v(33.13, -1.22) * mm, v(33.34, -1.15) * mm, v(33.69, -1.1) * mm, v(33.9, -1.1) * mm]});
            skFitSpline(sketch, "E1234", {"points": [v(29.58, 1.2) * mm, v(30.3, 2.05) * mm, v(30.2, 2.29) * mm, v(29.1, 2.29) * mm]});
            skFitSpline(sketch, "E1235", {"points": [v(29.1, 2.29) * mm, v(28.3, 2.29) * mm, v(28.1, 2.18) * mm, v(28.1, 1.74) * mm]});
            skFitSpline(sketch, "E1236", {"points": [v(28.1, 1.74) * mm, v(28.1, 1.44) * mm, v(27.98, 1.11) * mm, v(27.82, 1.02) * mm]});
            skFitSpline(sketch, "E1237", {"points": [v(27.82, 1.02) * mm, v(27.66, 0.92) * mm, v(27.54, 0.71) * mm, v(27.54, 0.55) * mm]});
            skFitSpline(sketch, "E1238", {"points": [v(27.54, 0.55) * mm, v(27.54, 0.07) * mm, v(29.03, 0.55) * mm, v(29.58, 1.2) * mm]});
            skFitSpline(sketch, "E1239", {"points": [v(-18.1, 11.64) * mm, v(-13.95, 11.66) * mm, v(-13.26, 11.72) * mm, v(-14.51, 11.93) * mm]});
            skFitSpline(sketch, "E1240", {"points": [v(-14.51, 11.93) * mm, v(-15.37, 12.07) * mm, v(-16.44, 12.2) * mm, v(-16.89, 12.23) * mm]});
            skFitSpline(sketch, "E1241", {"points": [v(-16.89, 12.23) * mm, v(-17.34, 12.24) * mm, v(-17.93, 12.48) * mm, v(-18.2, 12.75) * mm]});
            skFitSpline(sketch, "E1242", {"points": [v(-18.2, 12.75) * mm, v(-18.46, 13.01) * mm, v(-18.9, 13.35) * mm, v(-19.17, 13.5) * mm]});
            skFitSpline(sketch, "E1243", {"points": [v(-19.17, 13.5) * mm, v(-19.8, 13.85) * mm, v(-20.31, 16.41) * mm, v(-19.82, 16.72) * mm]});
            skFitSpline(sketch, "E1244", {"points": [v(-19.82, 16.72) * mm, v(-19.63, 16.83) * mm, v(-19.35, 16.84) * mm, v(-19.18, 16.74) * mm]});
            skFitSpline(sketch, "E1245", {"points": [v(-19.18, 16.74) * mm, v(-19.02, 16.64) * mm, v(-18.55, 16.6) * mm, v(-18.14, 16.64) * mm]});
            skFitSpline(sketch, "E1246", {"points": [v(-18.14, 16.64) * mm, v(-17.73, 16.68) * mm, v(-17.3, 16.58) * mm, v(-17.2, 16.42) * mm]});
            skFitSpline(sketch, "E1247", {"points": [v(-17.2, 16.42) * mm, v(-17.1, 16.25) * mm, v(-16.58, 16.12) * mm, v(-16.05, 16.12) * mm]});
            skFitSpline(sketch, "E1248", {"points": [v(-16.05, 16.12) * mm, v(-15.51, 16.12) * mm, v(-15.08, 15.99) * mm, v(-15.08, 15.83) * mm]});
            skFitSpline(sketch, "E1249", {"points": [v(-15.08, 15.83) * mm, v(-15.08, 15.48) * mm, v(-13.92, 15.47) * mm, v(-13, 15.82) * mm]});
            skFitSpline(sketch, "E1250", {"points": [v(-13, 15.82) * mm, v(-12.59, 15.98) * mm, v(-12.26, 16.35) * mm, v(-12.2, 16.74) * mm]});
            skFitSpline(sketch, "E1251", {"points": [v(-12.2, 16.74) * mm, v(-12.14, 17.22) * mm, v(-11.93, 17.39) * mm, v(-11.4, 17.39) * mm]});
            skFitSpline(sketch, "E1252", {"points": [v(-11.4, 17.39) * mm, v(-10.22, 17.39) * mm, v(-10.27, 17.87) * mm, v(-11.54, 18.68) * mm]});
            skFitSpline(sketch, "E1253", {"points": [v(-11.54, 18.68) * mm, v(-13.01, 19.61) * mm, v(-13.57, 20.92) * mm, v(-13.14, 22.45) * mm]});
            skFitSpline(sketch, "E1254", {"points": [v(-13.14, 22.45) * mm, v(-12.79, 23.74) * mm, v(-13.02, 23.89) * mm, v(-15.46, 23.83) * mm]});
            skFitSpline(sketch, "E1255", {"points": [v(-15.46, 23.83) * mm, v(-17.23, 23.78) * mm, v(-17.38, 23.82) * mm, v(-17.25, 24.32) * mm]});
            skFitSpline(sketch, "E1256", {"points": [v(-17.25, 24.32) * mm, v(-17.13, 24.77) * mm, v(-17.2, 24.8) * mm, v(-17.63, 24.58) * mm]});
            skFitSpline(sketch, "E1257", {"points": [v(-17.63, 24.58) * mm, v(-17.92, 24.42) * mm, v(-18.35, 24.02) * mm, v(-18.59, 23.68) * mm]});
            skFitSpline(sketch, "E1258", {"points": [v(-18.59, 23.68) * mm, v(-18.95, 23.15) * mm, v(-19.14, 23.1) * mm, v(-19.8, 23.34) * mm]});
            skFitSpline(sketch, "E1259", {"points": [v(-19.8, 23.34) * mm, v(-20.52, 23.6) * mm, v(-20.64, 23.52) * mm, v(-21.39, 22.4) * mm]});
            skFitSpline(sketch, "E1260", {"points": [v(-21.39, 22.4) * mm, v(-22, 21.47) * mm, v(-22.33, 21.22) * mm, v(-22.73, 21.35) * mm]});
            skFitSpline(sketch, "E1261", {"points": [v(-22.73, 21.35) * mm, v(-23.18, 21.5) * mm, v(-23.26, 21.37) * mm, v(-23.26, 20.58) * mm]});
            skFitSpline(sketch, "E1262", {"points": [v(-23.26, 20.58) * mm, v(-23.27, 19.4) * mm, v(-23.78, 17.53) * mm, v(-24.1, 17.53) * mm]});
            skFitSpline(sketch, "E1263", {"points": [v(-24.1, 17.53) * mm, v(-24.23, 17.53) * mm, v(-24.27, 17.28) * mm, v(-24.2, 16.97) * mm]});
            skFitSpline(sketch, "E1264", {"points": [v(-24.2, 16.97) * mm, v(-24.11, 16.66) * mm, v(-24.24, 15.91) * mm, v(-24.48, 15.3) * mm]});
            skFitSpline(sketch, "E1265", {"points": [v(-24.48, 15.3) * mm, v(-24.73, 14.7) * mm, v(-24.84, 14.11) * mm, v(-24.73, 14) * mm]});
            skFitSpline(sketch, "E1266", {"points": [v(-24.73, 14) * mm, v(-24.62, 13.88) * mm, v(-24.82, 13.88) * mm, v(-25.17, 13.98) * mm]});
            skFitSpline(sketch, "E1267", {"points": [v(-25.17, 13.98) * mm, v(-25.62, 14.12) * mm, v(-25.8, 14.06) * mm, v(-25.8, 13.79) * mm]});
            skFitSpline(sketch, "E1268", {"points": [v(-25.8, 13.79) * mm, v(-25.8, 13.57) * mm, v(-26.12, 13.1) * mm, v(-26.5, 12.73) * mm]});
            skFitSpline(sketch, "E1269", {"points": [v(-26.5, 12.73) * mm, v(-27.11, 12.16) * mm, v(-27.3, 12.12) * mm, v(-27.92, 12.4) * mm]});
            skFitSpline(sketch, "E1270", {"points": [v(-27.92, 12.4) * mm, v(-28.32, 12.58) * mm, v(-28.71, 12.9) * mm, v(-28.8, 13.13) * mm]});
            skFitSpline(sketch, "E1271", {"points": [v(-28.8, 13.13) * mm, v(-28.88, 13.36) * mm, v(-29.11, 13.48) * mm, v(-29.31, 13.4) * mm]});
            skFitSpline(sketch, "E1272", {"points": [v(-29.31, 13.4) * mm, v(-29.83, 13.2) * mm, v(-30.41, 15.52) * mm, v(-30.21, 17) * mm]});
            skFitSpline(sketch, "E1273", {"points": [v(-30.21, 17) * mm, v(-30.07, 18.1) * mm, v(-30.08, 18.14) * mm, v(-30.32, 17.35) * mm]});
            skFitSpline(sketch, "E1274", {"points": [v(-30.32, 17.35) * mm, v(-30.66, 16.28) * mm, v(-31.32, 15.96) * mm, v(-32.12, 16.5) * mm]});
            skFitSpline(sketch, "E1275", {"points": [v(-32.12, 16.5) * mm, v(-32.76, 16.92) * mm, v(-32.86, 16.81) * mm, v(-33.78, 14.85) * mm]});
            skFitSpline(sketch, "E1276", {"points": [v(-33.78, 14.85) * mm, v(-34.37, 13.6) * mm, v(-35.05, 13.11) * mm, v(-35.66, 13.5) * mm]});
            skFitSpline(sketch, "E1277", {"points": [v(-35.66, 13.5) * mm, v(-36.09, 13.77) * mm, v(-36.14, 13.72) * mm, v(-36.03, 13.16) * mm]});
            skFitSpline(sketch, "E1278", {"points": [v(-36.03, 13.16) * mm, v(-35.9, 12.46) * mm, v(-36.51, 11.07) * mm, v(-37.21, 10.49) * mm]});
            skFitSpline(sketch, "E1279", {"points": [v(-37.21, 10.49) * mm, v(-37.46, 10.29) * mm, v(-37.66, 9.88) * mm, v(-37.66, 9.6) * mm]});
            skFitSpline(sketch, "E1280", {"points": [v(-37.66, 9.6) * mm, v(-37.66, 9.3) * mm, v(-37.73, 9.06) * mm, v(-37.82, 9.06) * mm]});
            skFitSpline(sketch, "E1281", {"points": [v(-37.82, 9.06) * mm, v(-38.26, 9.06) * mm, v(-39.1, 9.72) * mm, v(-39.41, 10.32) * mm]});
            skFitSpline(sketch, "E1282", {"points": [v(-39.41, 10.32) * mm, v(-39.72, 10.91) * mm, v(-39.77, 10.6) * mm, v(-39.76, 8.02) * mm]});
            skLineSegment(sketch, "E1283", {"start": v(-39.76, 8.02) * mm, "end": v(-39.75, 5.02) * mm});
            skLineSegment(sketch, "E1284", {"start": v(-39.75, 5.02) * mm, "end": v(-38.55, 4.67) * mm});
            skFitSpline(sketch, "E1285", {"points": [v(-38.55, 4.67) * mm, v(-37.9, 4.48) * mm, v(-37.06, 4.12) * mm, v(-36.7, 3.88) * mm]});
            skFitSpline(sketch, "E1286", {"points": [v(-36.7, 3.88) * mm, v(-36.06, 3.47) * mm, v(-36, 3.5) * mm, v(-35.36, 4.5) * mm]});
            skFitSpline(sketch, "E1287", {"points": [v(-35.36, 4.5) * mm, v(-34.93, 5.17) * mm, v(-34.13, 5.82) * mm, v(-33.07, 6.34) * mm]});
            skFitSpline(sketch, "E1288", {"points": [v(-33.07, 6.34) * mm, v(-31.3, 7.23) * mm, v(-31.04, 7.81) * mm, v(-32, 8.77) * mm]});
            skFitSpline(sketch, "E1289", {"points": [v(-32, 8.77) * mm, v(-32.6, 9.37) * mm, v(-33.32, 9.29) * mm, v(-33.9, 8.56) * mm]});
            skFitSpline(sketch, "E1290", {"points": [v(-33.9, 8.56) * mm, v(-34.19, 8.2) * mm, v(-34.33, 8.2) * mm, v(-34.68, 8.49) * mm]});
            skFitSpline(sketch, "E1291", {"points": [v(-34.68, 8.49) * mm, v(-35.3, 9) * mm, v(-35.22, 9.9) * mm, v(-34.5, 10.67) * mm]});
            skFitSpline(sketch, "E1292", {"points": [v(-34.5, 10.67) * mm, v(-33.74, 11.47) * mm, v(-32.79, 11.5) * mm, v(-31.57, 10.74) * mm]});
            skFitSpline(sketch, "E1293", {"points": [v(-31.57, 10.74) * mm, v(-30.73, 10.23) * mm, v(-29.47, 8.24) * mm, v(-29.47, 7.44) * mm]});
            skFitSpline(sketch, "E1294", {"points": [v(-29.47, 7.44) * mm, v(-29.47, 7.27) * mm, v(-28.76, 6.8) * mm, v(-27.9, 6.4) * mm]});
            skFitSpline(sketch, "E1295", {"points": [v(-27.9, 6.4) * mm, v(-25.97, 5.52) * mm, v(-24.37, 4.29) * mm, v(-23.82, 3.26) * mm]});
            skFitSpline(sketch, "E1296", {"points": [v(-23.82, 3.26) * mm, v(-23.44, 2.54) * mm, v(-23.4, 2.85) * mm, v(-23.33, 7.04) * mm]});
            skLineSegment(sketch, "E1297", {"start": v(-23.33, 7.04) * mm, "end": v(-23.25, 11.6) * mm});
            skLineSegment(sketch, "E1298", {"start": v(-23.25, 11.6) * mm, "end": v(-18.1, 11.64) * mm});
            skFitSpline(sketch, "E1299", {"points": [v(-31.47, 4.26) * mm, v(-31.06, 4.88) * mm, v(-31.07, 4.9) * mm, v(-31.74, 4.7) * mm]});
            skFitSpline(sketch, "E1300", {"points": [v(-31.74, 4.7) * mm, v(-32.65, 4.41) * mm, v(-33.14, 4) * mm, v(-33.14, 3.53) * mm]});
            skFitSpline(sketch, "E1301", {"points": [v(-33.14, 3.53) * mm, v(-33.14, 2.97) * mm, v(-32, 3.46) * mm, v(-31.47, 4.26) * mm]});
            skFitSpline(sketch, "E1302", {"points": [v(26.17, 7.8) * mm, v(26.47, 7.9) * mm, v(26.91, 8.48) * mm, v(27.16, 9.08) * mm]});
            skFitSpline(sketch, "E1303", {"points": [v(27.16, 9.08) * mm, v(27.97, 11.13) * mm, v(29.95, 12.14) * mm, v(31.5, 11.31) * mm]});
            skFitSpline(sketch, "E1304", {"points": [v(31.5, 11.31) * mm, v(31.96, 11.07) * mm, v(32.07, 11.15) * mm, v(32.28, 11.95) * mm]});
            skFitSpline(sketch, "E1305", {"points": [v(32.28, 11.95) * mm, v(32.59, 13.07) * mm, v(32.54, 13.18) * mm, v(31.63, 13.41) * mm]});
            skFitSpline(sketch, "E1306", {"points": [v(31.63, 13.41) * mm, v(31.14, 13.53) * mm, v(30.67, 13.4) * mm, v(30.1, 13) * mm]});
            skFitSpline(sketch, "E1307", {"points": [v(30.1, 13) * mm, v(29.66, 12.66) * mm, v(29.07, 12.44) * mm, v(28.78, 12.5) * mm]});
            skFitSpline(sketch, "E1308", {"points": [v(28.78, 12.5) * mm, v(28.12, 12.62) * mm, v(26.98, 14.6) * mm, v(26.98, 15.62) * mm]});
            skFitSpline(sketch, "E1309", {"points": [v(26.98, 15.62) * mm, v(26.97, 16.74) * mm, v(26.1, 16.63) * mm, v(25.16, 15.41) * mm]});
            skFitSpline(sketch, "E1310", {"points": [v(25.16, 15.41) * mm, v(24.74, 14.87) * mm, v(24.01, 14.22) * mm, v(23.53, 13.97) * mm]});
            skFitSpline(sketch, "E1311", {"points": [v(23.53, 13.97) * mm, v(22.7, 13.54) * mm, v(22.64, 13.55) * mm, v(21.98, 14.21) * mm]});
            skFitSpline(sketch, "E1312", {"points": [v(21.98, 14.21) * mm, v(21.56, 14.63) * mm, v(21.22, 15.36) * mm, v(21.13, 16.07) * mm]});
            skFitSpline(sketch, "E1313", {"points": [v(21.13, 16.07) * mm, v(21.03, 16.81) * mm, v(20.83, 17.25) * mm, v(20.58, 17.25) * mm]});
            skFitSpline(sketch, "E1314", {"points": [v(20.58, 17.25) * mm, v(20.36, 17.25) * mm, v(20.1, 17.63) * mm, v(20.02, 18.1) * mm]});
            skFitSpline(sketch, "E1315", {"points": [v(20.02, 18.1) * mm, v(19.9, 18.67) * mm, v(19.68, 18.94) * mm, v(19.32, 18.94) * mm]});
            skFitSpline(sketch, "E1316", {"points": [v(19.32, 18.94) * mm, v(19.03, 18.94) * mm, v(18.79, 18.82) * mm, v(18.79, 18.68) * mm]});
            skFitSpline(sketch, "E1317", {"points": [v(18.79, 18.68) * mm, v(18.79, 18.54) * mm, v(18.45, 18.01) * mm, v(18.03, 17.51) * mm]});
            skLineSegment(sketch, "E1318", {"start": v(18.03, 17.51) * mm, "end": v(17.27, 16.61) * mm});
            skLineSegment(sketch, "E1319", {"start": v(17.27, 16.61) * mm, "end": v(15.9, 18.12) * mm});
            skFitSpline(sketch, "E1320", {"points": [v(15.9, 18.12) * mm, v(14.85, 19.25) * mm, v(14.54, 19.79) * mm, v(14.64, 20.3) * mm]});
            skFitSpline(sketch, "E1321", {"points": [v(14.64, 20.3) * mm, v(14.75, 20.88) * mm, v(14.69, 20.94) * mm, v(14.07, 20.78) * mm]});
            skFitSpline(sketch, "E1322", {"points": [v(14.07, 20.78) * mm, v(13.64, 20.67) * mm, v(13.1, 20.78) * mm, v(12.7, 21.05) * mm]});
            skFitSpline(sketch, "E1323", {"points": [v(12.7, 21.05) * mm, v(12.05, 21.47) * mm, v(12.02, 21.46) * mm, v(12.02, 20.9) * mm]});
            skFitSpline(sketch, "E1324", {"points": [v(12.02, 20.9) * mm, v(12.02, 20.56) * mm, v(11.58, 19.86) * mm, v(11.04, 19.32) * mm]});
            skLineSegment(sketch, "E1325", {"start": v(11.04, 19.32) * mm, "end": v(10.07, 18.35) * mm});
            skLineSegment(sketch, "E1326", {"start": v(10.07, 18.35) * mm, "end": v(10.61, 16.6) * mm});
            skFitSpline(sketch, "E1327", {"points": [v(10.61, 16.6) * mm, v(10.9, 15.63) * mm, v(11.61, 14.12) * mm, v(12.17, 13.22) * mm]});
            skLineSegment(sketch, "E1328", {"start": v(12.17, 13.22) * mm, "end": v(13.19, 11.6) * mm});
            skLineSegment(sketch, "E1329", {"start": v(13.19, 11.6) * mm, "end": v(17.82, 11.6) * mm});
            skLineSegment(sketch, "E1330", {"start": v(17.82, 11.6) * mm, "end": v(22.46, 11.6) * mm});
            skLineSegment(sketch, "E1331", {"start": v(22.46, 11.6) * mm, "end": v(22.46, 7.95) * mm});
            skLineSegment(sketch, "E1332", {"start": v(22.46, 7.95) * mm, "end": v(22.46, 4.3) * mm});
            skLineSegment(sketch, "E1333", {"start": v(22.46, 4.3) * mm, "end": v(24.05, 5.97) * mm});
            skFitSpline(sketch, "E1334", {"points": [v(24.05, 5.97) * mm, v(24.92, 6.89) * mm, v(25.88, 7.71) * mm, v(26.17, 7.8) * mm]});
            skFitSpline(sketch, "E1335", {"points": [v(28.78, 5.62) * mm, v(28.45, 5.67) * mm, v(27.74, 5.52) * mm, v(27.22, 5.29) * mm]});
            skLineSegment(sketch, "E1336", {"start": v(27.22, 5.29) * mm, "end": v(26.27, 4.87) * mm});
            skLineSegment(sketch, "E1337", {"start": v(26.27, 4.87) * mm, "end": v(27.11, 4.85) * mm});
            skFitSpline(sketch, "E1338", {"points": [v(27.11, 4.85) * mm, v(27.58, 4.83) * mm, v(28.14, 4.7) * mm, v(28.37, 4.56) * mm]});
            skFitSpline(sketch, "E1339", {"points": [v(28.37, 4.56) * mm, v(28.66, 4.38) * mm, v(28.86, 4.47) * mm, v(29.09, 4.92) * mm]});
            skFitSpline(sketch, "E1340", {"points": [v(29.09, 4.92) * mm, v(29.35, 5.45) * mm, v(29.31, 5.54) * mm, v(28.78, 5.62) * mm]});
            skFitSpline(sketch, "E1341", {"points": [v(32.84, 4.96) * mm, v(32.8, 5) * mm, v(32.31, 5.17) * mm, v(31.77, 5.35) * mm]});
            skLineSegment(sketch, "E1342", {"start": v(31.77, 5.35) * mm, "end": v(30.78, 5.67) * mm});
            skLineSegment(sketch, "E1343", {"start": v(30.78, 5.67) * mm, "end": v(31.43, 5.12) * mm});
            skFitSpline(sketch, "E1344", {"points": [v(31.43, 5.12) * mm, v(31.79, 4.82) * mm, v(32.27, 4.65) * mm, v(32.5, 4.74) * mm]});
            skFitSpline(sketch, "E1345", {"points": [v(32.5, 4.74) * mm, v(32.73, 4.82) * mm, v(32.89, 4.93) * mm, v(32.84, 4.96) * mm]});
            skFitSpline(sketch, "E1346", {"points": [v(-40.29, 9.87) * mm, v(-40.4, 11) * mm, v(-40.35, 11.67) * mm, v(-40.1, 12.01) * mm]});
            skFitSpline(sketch, "E1347", {"points": [v(-40.1, 12.01) * mm, v(-39.77, 12.45) * mm, v(-39.7, 12.39) * mm, v(-39.4, 11.38) * mm]});
            skFitSpline(sketch, "E1348", {"points": [v(-39.4, 11.38) * mm, v(-38.93, 9.81) * mm, v(-38.46, 9.75) * mm, v(-37.41, 11.11) * mm]});
            skFitSpline(sketch, "E1349", {"points": [v(-37.41, 11.11) * mm, v(-36.4, 12.42) * mm, v(-36.33, 13.08) * mm, v(-36.99, 14.71) * mm]});
            skFitSpline(sketch, "E1350", {"points": [v(-36.99, 14.71) * mm, v(-37.33, 15.58) * mm, v(-37.37, 16.01) * mm, v(-37.15, 16.48) * mm]});
            skFitSpline(sketch, "E1351", {"points": [v(-37.15, 16.48) * mm, v(-36.87, 17.05) * mm, v(-36.85, 17.01) * mm, v(-36.83, 16.1) * mm]});
            skFitSpline(sketch, "E1352", {"points": [v(-36.83, 16.1) * mm, v(-36.8, 14.99) * mm, v(-35.72, 13.67) * mm, v(-35.04, 13.93) * mm]});
            skFitSpline(sketch, "E1353", {"points": [v(-35.04, 13.93) * mm, v(-34.83, 14.01) * mm, v(-34.34, 14.7) * mm, v(-33.94, 15.47) * mm]});
            skFitSpline(sketch, "E1354", {"points": [v(-33.94, 15.47) * mm, v(-33.28, 16.74) * mm, v(-33.24, 17) * mm, v(-33.51, 18.3) * mm]});
            skFitSpline(sketch, "E1355", {"points": [v(-33.51, 18.3) * mm, v(-33.73, 19.39) * mm, v(-33.71, 20.12) * mm, v(-33.42, 21.33) * mm]});
            skFitSpline(sketch, "E1356", {"points": [v(-33.42, 21.33) * mm, v(-33.21, 22.2) * mm, v(-32.94, 22.98) * mm, v(-32.8, 23.06) * mm]});
            skFitSpline(sketch, "E1357", {"points": [v(-32.8, 23.06) * mm, v(-32.44, 23.3) * mm, v(-32.54, 22.37) * mm, v(-33.04, 20.94) * mm]});
            skFitSpline(sketch, "E1358", {"points": [v(-33.04, 20.94) * mm, v(-33.6, 19.38) * mm, v(-33.42, 18.34) * mm, v(-32.41, 17.34) * mm]});
            skFitSpline(sketch, "E1359", {"points": [v(-32.41, 17.34) * mm, v(-31.56, 16.49) * mm, v(-31.07, 16.6) * mm, v(-30.88, 17.7) * mm]});
            skFitSpline(sketch, "E1360", {"points": [v(-30.88, 17.7) * mm, v(-30.8, 18.17) * mm, v(-30.56, 18.52) * mm, v(-30.31, 18.52) * mm]});
            skFitSpline(sketch, "E1361", {"points": [v(-30.31, 18.52) * mm, v(-30, 18.52) * mm, v(-29.89, 18.14) * mm, v(-29.88, 16.96) * mm]});
            skFitSpline(sketch, "E1362", {"points": [v(-29.88, 16.96) * mm, v(-29.85, 14.97) * mm, v(-29.52, 13.78) * mm, v(-29.03, 13.97) * mm]});
            skFitSpline(sketch, "E1363", {"points": [v(-29.03, 13.97) * mm, v(-28.82, 14.05) * mm, v(-28.58, 13.87) * mm, v(-28.48, 13.58) * mm]});
            skFitSpline(sketch, "E1364", {"points": [v(-28.48, 13.58) * mm, v(-28.39, 13.28) * mm, v(-28.04, 12.95) * mm, v(-27.71, 12.85) * mm]});
            skFitSpline(sketch, "E1365", {"points": [v(-27.71, 12.85) * mm, v(-26.97, 12.61) * mm, v(-26.08, 13.58) * mm, v(-26.08, 14.63) * mm]});
            skFitSpline(sketch, "E1366", {"points": [v(-26.08, 14.63) * mm, v(-26.08, 15.23) * mm, v(-26.02, 15.28) * mm, v(-25.66, 15) * mm]});
            skFitSpline(sketch, "E1367", {"points": [v(-25.66, 15) * mm, v(-25.32, 14.7) * mm, v(-25.2, 14.74) * mm, v(-25.05, 15.15) * mm]});
            skFitSpline(sketch, "E1368", {"points": [v(-25.05, 15.15) * mm, v(-24.79, 15.84) * mm, v(-24.8, 17.28) * mm, v(-25.06, 17.86) * mm]});
            skFitSpline(sketch, "E1369", {"points": [v(-25.06, 17.86) * mm, v(-25.24, 18.24) * mm, v(-25.17, 18.3) * mm, v(-24.71, 18.18) * mm]});
            skFitSpline(sketch, "E1370", {"points": [v(-24.71, 18.18) * mm, v(-24.24, 18.06) * mm, v(-24.1, 18.24) * mm, v(-23.83, 19.2) * mm]});
            skFitSpline(sketch, "E1371", {"points": [v(-23.83, 19.2) * mm, v(-23.46, 20.57) * mm, v(-23.64, 21.35) * mm, v(-24.54, 22.33) * mm]});
            skFitSpline(sketch, "E1372", {"points": [v(-24.54, 22.33) * mm, v(-25.16, 22.99) * mm, v(-25.38, 23.78) * mm, v(-25.28, 24.94) * mm]});
            skFitSpline(sketch, "E1373", {"points": [v(-25.28, 24.94) * mm, v(-25.2, 25.94) * mm, v(-24.75, 25.39) * mm, v(-24.78, 24.3) * mm]});
            skFitSpline(sketch, "E1374", {"points": [v(-24.78, 24.3) * mm, v(-24.8, 23.04) * mm, v(-24.18, 22.23) * mm, v(-22.93, 21.94) * mm]});
            skFitSpline(sketch, "E1375", {"points": [v(-22.93, 21.94) * mm, v(-22.26, 21.78) * mm, v(-22.12, 21.9) * mm, v(-21.6, 22.96) * mm]});
            skFitSpline(sketch, "E1376", {"points": [v(-21.6, 22.96) * mm, v(-21.26, 23.66) * mm, v(-21.09, 24.43) * mm, v(-21.19, 24.8) * mm]});
            skFitSpline(sketch, "E1377", {"points": [v(-21.19, 24.8) * mm, v(-21.39, 25.57) * mm, v(-21.1, 26.84) * mm, v(-20.71, 26.84) * mm]});
            skFitSpline(sketch, "E1378", {"points": [v(-20.71, 26.84) * mm, v(-20.55, 26.84) * mm, v(-20.5, 26.54) * mm, v(-20.6, 26.14) * mm]});
            skFitSpline(sketch, "E1379", {"points": [v(-20.6, 26.14) * mm, v(-20.86, 25.14) * mm, v(-20.53, 24.09) * mm, v(-19.91, 23.89) * mm]});
            skFitSpline(sketch, "E1380", {"points": [v(-19.91, 23.89) * mm, v(-19.56, 23.78) * mm, v(-19.05, 24.02) * mm, v(-18.36, 24.63) * mm]});
            skFitSpline(sketch, "E1381", {"points": [v(-18.36, 24.63) * mm, v(-17.5, 25.4) * mm, v(-17.34, 25.71) * mm, v(-17.34, 26.7) * mm]});
            skFitSpline(sketch, "E1382", {"points": [v(-17.34, 26.7) * mm, v(-17.34, 27.34) * mm, v(-17.15, 28.1) * mm, v(-16.92, 28.4) * mm]});
            skFitSpline(sketch, "E1383", {"points": [v(-16.92, 28.4) * mm, v(-16.52, 28.94) * mm, v(-16.5, 28.94) * mm, v(-16.5, 28.3) * mm]});
            skFitSpline(sketch, "E1384", {"points": [v(-16.5, 28.3) * mm, v(-16.5, 27.94) * mm, v(-16.36, 27.41) * mm, v(-16.2, 27.12) * mm]});
            skFitSpline(sketch, "E1385", {"points": [v(-16.2, 27.12) * mm, v(-15.93, 26.61) * mm, v(-15.85, 26.63) * mm, v(-14.52, 27.46) * mm]});
            skFitSpline(sketch, "E1386", {"points": [v(-14.52, 27.46) * mm, v(-13.75, 27.94) * mm, v(-12.95, 28.7) * mm, v(-12.76, 29.14) * mm]});
            skFitSpline(sketch, "E1387", {"points": [v(-12.76, 29.14) * mm, v(-12.34, 30.09) * mm, v(-12.1, 30.16) * mm, v(-11.9, 29.38) * mm]});
            skFitSpline(sketch, "E1388", {"points": [v(-11.9, 29.38) * mm, v(-11.68, 28.57) * mm, v(-10.95, 28.4) * mm, v(-10.1, 28.95) * mm]});
            skFitSpline(sketch, "E1389", {"points": [v(-10.1, 28.95) * mm, v(-9.43, 29.4) * mm, v(-9.38, 29.56) * mm, v(-9.5, 30.96) * mm]});
            skFitSpline(sketch, "E1390", {"points": [v(-9.5, 30.96) * mm, v(-9.64, 32.7) * mm, v(-9.92, 33.14) * mm, v(-10.38, 32.4) * mm]});
            skFitSpline(sketch, "E1391", {"points": [v(-10.38, 32.4) * mm, v(-11.07, 31.28) * mm, v(-11.42, 30.96) * mm, v(-11, 31.83) * mm]});
            skFitSpline(sketch, "E1392", {"points": [v(-11, 31.83) * mm, v(-10.76, 32.33) * mm, v(-10.44, 32.81) * mm, v(-10.28, 32.9) * mm]});
            skFitSpline(sketch, "E1393", {"points": [v(-10.28, 32.9) * mm, v(-9.89, 33.15) * mm, v(-10.23, 34.38) * mm, v(-11.05, 35.7) * mm]});
            skLineSegment(sketch, "E1394", {"start": v(-11.05, 35.7) * mm, "end": v(-11.74, 36.78) * mm});
            skLineSegment(sketch, "E1395", {"start": v(-11.74, 36.78) * mm, "end": v(-12.69, 35.86) * mm});
            skFitSpline(sketch, "E1396", {"points": [v(-12.69, 35.86) * mm, v(-13.2, 35.36) * mm, v(-14.1, 34.04) * mm, v(-14.66, 32.94) * mm]});
            skFitSpline(sketch, "E1397", {"points": [v(-14.66, 32.94) * mm, v(-15.22, 31.84) * mm, v(-15.6, 31.25) * mm, v(-15.48, 31.64) * mm]});
            skFitSpline(sketch, "E1398", {"points": [v(-15.48, 31.64) * mm, v(-15.12, 32.95) * mm, v(-14.2, 34.51) * mm, v(-13.06, 35.74) * mm]});
            skFitSpline(sketch, "E1399", {"points": [v(-13.06, 35.74) * mm, v(-11.79, 37.12) * mm, v(-11.82, 37.34) * mm, v(-13.46, 38.92) * mm]});
            skLineSegment(sketch, "E1400", {"start": v(-13.46, 38.92) * mm, "end": v(-14.43, 39.85) * mm});
            skLineSegment(sketch, "E1401", {"start": v(-14.43, 39.85) * mm, "end": v(-14.9, 38.6) * mm});
            skFitSpline(sketch, "E1402", {"points": [v(-14.9, 38.6) * mm, v(-15.46, 37.15) * mm, v(-16.51, 36.06) * mm, v(-17.24, 36.2) * mm]});
            skFitSpline(sketch, "E1403", {"points": [v(-17.24, 36.2) * mm, v(-17.53, 36.25) * mm, v(-17.98, 36.74) * mm, v(-18.25, 37.28) * mm]});
            skLineSegment(sketch, "E1404", {"start": v(-18.25, 37.28) * mm, "end": v(-18.75, 38.27) * mm});
            skLineSegment(sketch, "E1405", {"start": v(-18.75, 38.27) * mm, "end": v(-18.75, 36.57) * mm});
            skFitSpline(sketch, "E1406", {"points": [v(-18.75, 36.57) * mm, v(-18.75, 34.43) * mm, v(-19.3, 33.5) * mm, v(-20.41, 33.75) * mm]});
            skFitSpline(sketch, "E1407", {"points": [v(-20.41, 33.75) * mm, v(-21.08, 33.9) * mm, v(-21.3, 33.75) * mm, v(-22.15, 32.57) * mm]});
            skFitSpline(sketch, "E1408", {"points": [v(-22.15, 32.57) * mm, v(-22.68, 31.82) * mm, v(-23.6, 30.33) * mm, v(-24.17, 29.24) * mm]});
            skFitSpline(sketch, "E1409", {"points": [v(-24.17, 29.24) * mm, v(-24.75, 28.15) * mm, v(-25.23, 27.35) * mm, v(-25.23, 27.46) * mm]});
            skFitSpline(sketch, "E1410", {"points": [v(-25.23, 27.46) * mm, v(-25.24, 27.84) * mm, v(-24.55, 29.24) * mm, v(-23.63, 30.72) * mm]});
            skFitSpline(sketch, "E1411", {"points": [v(-23.63, 30.72) * mm, v(-23.12, 31.54) * mm, v(-22.83, 32.2) * mm, v(-22.97, 32.2) * mm]});
            skFitSpline(sketch, "E1412", {"points": [v(-22.97, 32.2) * mm, v(-23.12, 32.2) * mm, v(-23.41, 32.53) * mm, v(-23.62, 32.92) * mm]});
            skLineSegment(sketch, "E1413", {"start": v(-23.62, 32.92) * mm, "end": v(-24, 33.64) * mm});
            skLineSegment(sketch, "E1414", {"start": v(-24, 33.64) * mm, "end": v(-25.16, 32.71) * mm});
            skFitSpline(sketch, "E1415", {"points": [v(-25.16, 32.71) * mm, v(-26.7, 31.47) * mm, v(-28.62, 29.09) * mm, v(-29.86, 26.84) * mm]});
            skFitSpline(sketch, "E1416", {"points": [v(-29.86, 26.84) * mm, v(-31, 24.78) * mm, v(-31.24, 24.74) * mm, v(-30.2, 26.78) * mm]});
            skFitSpline(sketch, "E1417", {"points": [v(-30.2, 26.78) * mm, v(-29.21, 28.74) * mm, v(-27.07, 31.5) * mm, v(-25.49, 32.82) * mm]});
            skFitSpline(sketch, "E1418", {"points": [v(-25.49, 32.82) * mm, v(-24.73, 33.46) * mm, v(-24.16, 34.05) * mm, v(-24.23, 34.12) * mm]});
            skFitSpline(sketch, "E1419", {"points": [v(-24.23, 34.12) * mm, v(-24.3, 34.19) * mm, v(-24.83, 33.85) * mm, v(-25.41, 33.38) * mm]});
            skFitSpline(sketch, "E1420", {"points": [v(-25.41, 33.38) * mm, v(-26, 32.9) * mm, v(-26.59, 32.59) * mm, v(-26.74, 32.68) * mm]});
            skFitSpline(sketch, "E1421", {"points": [v(-26.74, 32.68) * mm, v(-26.9, 32.78) * mm, v(-26.94, 32.72) * mm, v(-26.84, 32.56) * mm]});
            skFitSpline(sketch, "E1422", {"points": [v(-26.84, 32.56) * mm, v(-26.54, 32.09) * mm, v(-27.42, 31.5) * mm, v(-27.87, 31.88) * mm]});
            skFitSpline(sketch, "E1423", {"points": [v(-27.87, 31.88) * mm, v(-28.16, 32.12) * mm, v(-28.25, 32.1) * mm, v(-28.25, 31.79) * mm]});
            skFitSpline(sketch, "E1424", {"points": [v(-28.25, 31.79) * mm, v(-28.25, 31.56) * mm, v(-28.11, 31.47) * mm, v(-27.94, 31.57) * mm]});
            skFitSpline(sketch, "E1425", {"points": [v(-27.94, 31.57) * mm, v(-27.59, 31.79) * mm, v(-29, 30.03) * mm, v(-30.5, 28.4) * mm]});
            skFitSpline(sketch, "E1426", {"points": [v(-30.5, 28.4) * mm, v(-31.7, 27.08) * mm, v(-31.44, 27.53) * mm, v(-29.91, 29.45) * mm]});
            skFitSpline(sketch, "E1427", {"points": [v(-29.91, 29.45) * mm, v(-28.06, 31.76) * mm, v(-29.26, 30.92) * mm, v(-32.74, 27.48) * mm]});
            skFitSpline(sketch, "E1428", {"points": [v(-32.74, 27.48) * mm, v(-34.75, 25.47) * mm, v(-35.52, 24.82) * mm, v(-34.68, 25.82) * mm]});
            skFitSpline(sketch, "E1429", {"points": [v(-34.68, 25.82) * mm, v(-33.91, 26.74) * mm, v(-32.2, 28.5) * mm, v(-30.88, 29.72) * mm]});
            skLineSegment(sketch, "E1430", {"start": v(-30.88, 29.72) * mm, "end": v(-28.48, 31.95) * mm});
            skLineSegment(sketch, "E1431", {"start": v(-28.48, 31.95) * mm, "end": v(-31.73, 30.39) * mm});
            skFitSpline(sketch, "E1432", {"points": [v(-31.73, 30.39) * mm, v(-33.51, 29.53) * mm, v(-35.1, 28.82) * mm, v(-35.24, 28.82) * mm]});
            skFitSpline(sketch, "E1433", {"points": [v(-35.24, 28.82) * mm, v(-35.38, 28.82) * mm, v(-33.3, 29.91) * mm, v(-30.63, 31.25) * mm]});
            skFitSpline(sketch, "E1434", {"points": [v(-30.63, 31.25) * mm, v(-27.96, 32.58) * mm, v(-25.81, 33.72) * mm, v(-25.86, 33.77) * mm]});
            skFitSpline(sketch, "E1435", {"points": [v(-25.86, 33.77) * mm, v(-25.91, 33.82) * mm, v(-27.2, 33.49) * mm, v(-28.74, 33.03) * mm]});
            skFitSpline(sketch, "E1436", {"points": [v(-28.74, 33.03) * mm, v(-30.27, 32.58) * mm, v(-31.72, 32.21) * mm, v(-31.98, 32.23) * mm]});
            skFitSpline(sketch, "E1437", {"points": [v(-31.98, 32.23) * mm, v(-32.23, 32.24) * mm, v(-32.3, 32.29) * mm, v(-32.15, 32.34) * mm]});
            skFitSpline(sketch, "E1438", {"points": [v(-32.15, 32.34) * mm, v(-32, 32.4) * mm, v(-30.19, 32.96) * mm, v(-28.13, 33.6) * mm]});
            skFitSpline(sketch, "E1439", {"points": [v(-28.13, 33.6) * mm, v(-26.07, 34.24) * mm, v(-24.39, 34.85) * mm, v(-24.39, 34.96) * mm]});
            skFitSpline(sketch, "E1440", {"points": [v(-24.39, 34.96) * mm, v(-24.38, 35.08) * mm, v(-24.3, 35.48) * mm, v(-24.2, 35.87) * mm]});
            skFitSpline(sketch, "E1441", {"points": [v(-24.2, 35.87) * mm, v(-24.03, 36.53) * mm, v(-24.06, 36.52) * mm, v(-24.8, 35.66) * mm]});
            skFitSpline(sketch, "E1442", {"points": [v(-24.8, 35.66) * mm, v(-25.7, 34.6) * mm, v(-26.6, 34.48) * mm, v(-28.04, 35.26) * mm]});
            skFitSpline(sketch, "E1443", {"points": [v(-28.04, 35.26) * mm, v(-28.87, 35.7) * mm, v(-29.52, 35.76) * mm, v(-32.56, 35.67) * mm]});
            skFitSpline(sketch, "E1444", {"points": [v(-32.56, 35.67) * mm, v(-34.5, 35.6) * mm, v(-36.67, 35.67) * mm, v(-37.37, 35.82) * mm]});
            skFitSpline(sketch, "E1445", {"points": [v(-37.37, 35.82) * mm, v(-38.34, 36.02) * mm, v(-37.92, 36.05) * mm, v(-35.66, 35.94) * mm]});
            skFitSpline(sketch, "E1446", {"points": [v(-35.66, 35.94) * mm, v(-34.03, 35.86) * mm, v(-31.93, 35.9) * mm, v(-31, 36.04) * mm]});
            skLineSegment(sketch, "E1447", {"start": v(-31, 36.04) * mm, "end": v(-29.33, 36.3) * mm});
            skLineSegment(sketch, "E1448", {"start": v(-29.33, 36.3) * mm, "end": v(-32.01, 36.45) * mm});
            skLineSegment(sketch, "E1449", {"start": v(-32.01, 36.45) * mm, "end": v(-34.7, 36.61) * mm});
            skLineSegment(sketch, "E1450", {"start": v(-34.7, 36.61) * mm, "end": v(-32.05, 36.66) * mm});
            skFitSpline(sketch, "E1451", {"points": [v(-32.05, 36.66) * mm, v(-29.5, 36.72) * mm, v(-29.39, 36.75) * mm, v(-28.61, 37.58) * mm]});
            skLineSegment(sketch, "E1452", {"start": v(-28.61, 37.58) * mm, "end": v(-27.8, 38.44) * mm});
            skLineSegment(sketch, "E1453", {"start": v(-27.8, 38.44) * mm, "end": v(-29.07, 38.25) * mm});
            skFitSpline(sketch, "E1454", {"points": [v(-29.07, 38.25) * mm, v(-30.6, 38.02) * mm, v(-32.84, 38.75) * mm, v(-32.88, 39.5) * mm]});
            skFitSpline(sketch, "E1455", {"points": [v(-32.88, 39.5) * mm, v(-32.9, 39.79) * mm, v(-32.96, 39.83) * mm, v(-33.04, 39.61) * mm]});
            skFitSpline(sketch, "E1456", {"points": [v(-33.04, 39.61) * mm, v(-33.22, 39.19) * mm, v(-34.1, 39.15) * mm, v(-34.83, 39.54) * mm]});
            skFitSpline(sketch, "E1457", {"points": [v(-34.83, 39.54) * mm, v(-35.13, 39.7) * mm, v(-35.55, 40.49) * mm, v(-35.8, 41.34) * mm]});
            skFitSpline(sketch, "E1458", {"points": [v(-35.8, 41.34) * mm, v(-36.12, 42.46) * mm, v(-36.4, 42.9) * mm, v(-36.86, 43.02) * mm]});
            skFitSpline(sketch, "E1459", {"points": [v(-36.86, 43.02) * mm, v(-37.59, 43.21) * mm, v(-37.94, 43.04) * mm, v(-37.94, 42.5) * mm]});
            skFitSpline(sketch, "E1460", {"points": [v(-37.94, 42.5) * mm, v(-37.94, 42.2) * mm, v(-38.16, 42.14) * mm, v(-38.77, 42.26) * mm]});
            skFitSpline(sketch, "E1461", {"points": [v(-38.77, 42.26) * mm, v(-39.76, 42.46) * mm, v(-41.67, 41.43) * mm, v(-41.43, 40.82) * mm]});
            skFitSpline(sketch, "E1462", {"points": [v(-41.43, 40.82) * mm, v(-41.35, 40.61) * mm, v(-40.66, 40.17) * mm, v(-39.9, 39.84) * mm]});
            skFitSpline(sketch, "E1463", {"points": [v(-39.9, 39.84) * mm, v(-38.53, 39.26) * mm, v(-38.1, 38.55) * mm, v(-38.9, 38.24) * mm]});
            skFitSpline(sketch, "E1464", {"points": [v(-38.9, 38.24) * mm, v(-39.12, 38.16) * mm, v(-39.95, 38.37) * mm, v(-40.76, 38.72) * mm]});
            skFitSpline(sketch, "E1465", {"points": [v(-40.76, 38.72) * mm, v(-42.77, 39.59) * mm, v(-43.56, 39.53) * mm, v(-45.02, 38.4) * mm]});
            skFitSpline(sketch, "E1466", {"points": [v(-45.02, 38.4) * mm, v(-45.7, 37.86) * mm, v(-46.33, 37.39) * mm, v(-46.4, 37.33) * mm]});
            skFitSpline(sketch, "E1467", {"points": [v(-46.4, 37.33) * mm, v(-46.48, 37.28) * mm, v(-46.06, 36.8) * mm, v(-45.46, 36.25) * mm]});
            skFitSpline(sketch, "E1468", {"points": [v(-45.46, 36.25) * mm, v(-44.43, 35.3) * mm, v(-44.32, 35.26) * mm, v(-42.5, 35.35) * mm]});
            skFitSpline(sketch, "E1469", {"points": [v(-42.5, 35.35) * mm, v(-40.8, 35.44) * mm, v(-40.62, 35.4) * mm, v(-40.62, 34.9) * mm]});
            skFitSpline(sketch, "E1470", {"points": [v(-40.62, 34.9) * mm, v(-40.62, 34.5) * mm, v(-41.02, 34.2) * mm, v(-42.14, 33.77) * mm]});
            skFitSpline(sketch, "E1471", {"points": [v(-42.14, 33.77) * mm, v(-44.4, 32.9) * mm, v(-44.83, 31.7) * mm, v(-43.1, 31.07) * mm]});
            skFitSpline(sketch, "E1472", {"points": [v(-43.1, 31.07) * mm, v(-42.66, 30.9) * mm, v(-41.83, 30.52) * mm, v(-41.24, 30.2) * mm]});
            skFitSpline(sketch, "E1473", {"points": [v(-41.24, 30.2) * mm, v(-40, 29.52) * mm, v(-39.19, 29.62) * mm, v(-37.57, 30.69) * mm]});
            skFitSpline(sketch, "E1474", {"points": [v(-37.57, 30.69) * mm, v(-36.38, 31.46) * mm, v(-35.31, 31.48) * mm, v(-35.17, 30.73) * mm]});
            skFitSpline(sketch, "E1475", {"points": [v(-35.17, 30.73) * mm, v(-35.02, 29.93) * mm, v(-36.39, 28.92) * mm, v(-38.1, 28.58) * mm]});
            skFitSpline(sketch, "E1476", {"points": [v(-38.1, 28.58) * mm, v(-39.98, 28.2) * mm, v(-41.14, 27.44) * mm, v(-41.57, 26.28) * mm]});
            skFitSpline(sketch, "E1477", {"points": [v(-41.57, 26.28) * mm, v(-41.74, 25.81) * mm, v(-42.03, 25.04) * mm, v(-42.21, 24.57) * mm]});
            skFitSpline(sketch, "E1478", {"points": [v(-42.21, 24.57) * mm, v(-42.43, 23.97) * mm, v(-42.95, 23.5) * mm, v(-43.87, 23.03) * mm]});
            skFitSpline(sketch, "E1479", {"points": [v(-43.87, 23.03) * mm, v(-45.46, 22.22) * mm, v(-45.75, 21.68) * mm, v(-44.9, 21.12) * mm]});
            skLineSegment(sketch, "E1480", {"start": v(-44.9, 21.12) * mm, "end": v(-44.3, 20.7) * mm});
            skLineSegment(sketch, "E1481", {"start": v(-44.3, 20.7) * mm, "end": v(-45.3, 19.59) * mm});
            skFitSpline(sketch, "E1482", {"points": [v(-45.3, 19.59) * mm, v(-46.08, 18.73) * mm, v(-46.36, 18.13) * mm, v(-46.51, 17.02) * mm]});
            skFitSpline(sketch, "E1483", {"points": [v(-46.51, 17.02) * mm, v(-46.64, 16.08) * mm, v(-46.96, 15.27) * mm, v(-47.44, 14.7) * mm]});
            skFitSpline(sketch, "E1484", {"points": [v(-47.44, 14.7) * mm, v(-47.84, 14.23) * mm, v(-48.1, 13.77) * mm, v(-48.02, 13.69) * mm]});
            skFitSpline(sketch, "E1485", {"points": [v(-48.02, 13.69) * mm, v(-47.65, 13.31) * mm, v(-46.1, 14.54) * mm, v(-45.3, 15.85) * mm]});
            skFitSpline(sketch, "E1486", {"points": [v(-45.3, 15.85) * mm, v(-44.11, 17.77) * mm, v(-43.5, 17.68) * mm, v(-43.3, 15.55) * mm]});
            skFitSpline(sketch, "E1487", {"points": [v(-43.3, 15.55) * mm, v(-43.21, 14.7) * mm, v(-42.91, 13.65) * mm, v(-42.63, 13.23) * mm]});
            skFitSpline(sketch, "E1488", {"points": [v(-42.63, 13.23) * mm, v(-42.3, 12.74) * mm, v(-42.17, 12.2) * mm, v(-42.28, 11.78) * mm]});
            skFitSpline(sketch, "E1489", {"points": [v(-42.28, 11.78) * mm, v(-42.4, 11.32) * mm, v(-42.27, 10.96) * mm, v(-41.86, 10.59) * mm]});
            skFitSpline(sketch, "E1490", {"points": [v(-41.86, 10.59) * mm, v(-41.54, 10.3) * mm, v(-41.1, 9.65) * mm, v(-40.9, 9.14) * mm]});
            skFitSpline(sketch, "E1491", {"points": [v(-40.9, 9.14) * mm, v(-40.31, 7.75) * mm, v(-40.1, 8.02) * mm, v(-40.29, 9.87) * mm]});
            skFitSpline(sketch, "E1492", {"points": [v(-38.36, 15.83) * mm, v(-38.25, 17.56) * mm, v(-37.47, 20.82) * mm, v(-37.22, 20.58) * mm]});
            skFitSpline(sketch, "E1493", {"points": [v(-37.22, 20.58) * mm, v(-37.16, 20.51) * mm, v(-37.3, 19.84) * mm, v(-37.53, 19.07) * mm]});
            skFitSpline(sketch, "E1494", {"points": [v(-37.53, 19.07) * mm, v(-37.76, 18.3) * mm, v(-38.07, 16.84) * mm, v(-38.22, 15.83) * mm]});
            skLineSegment(sketch, "E1495", {"start": v(-38.22, 15.83) * mm, "end": v(-38.48, 14) * mm});
            skLineSegment(sketch, "E1496", {"start": v(-38.48, 14) * mm, "end": v(-38.36, 15.83) * mm});
            skFitSpline(sketch, "E1497", {"points": [v(-27.96, 20.2) * mm, v(-27.96, 21.76) * mm, v(-27.9, 22.36) * mm, v(-27.85, 21.54) * mm]});
            skFitSpline(sketch, "E1498", {"points": [v(-27.85, 21.54) * mm, v(-27.8, 20.72) * mm, v(-27.8, 19.45) * mm, v(-27.85, 18.72) * mm]});
            skFitSpline(sketch, "E1499", {"points": [v(-27.85, 18.72) * mm, v(-27.91, 17.99) * mm, v(-27.96, 18.66) * mm, v(-27.96, 20.2) * mm]});
            skFitSpline(sketch, "E1500", {"points": [v(-29.7, 19.22) * mm, v(-29.7, 19.6) * mm, v(-29.64, 19.77) * mm, v(-29.57, 19.57) * mm]});
            skFitSpline(sketch, "E1501", {"points": [v(-29.57, 19.57) * mm, v(-29.49, 19.38) * mm, v(-29.49, 19.06) * mm, v(-29.57, 18.87) * mm]});
            skFitSpline(sketch, "E1502", {"points": [v(-29.57, 18.87) * mm, v(-29.64, 18.67) * mm, v(-29.7, 18.83) * mm, v(-29.7, 19.22) * mm]});
            skFitSpline(sketch, "E1503", {"points": [v(-35.95, 20.36) * mm, v(-35.96, 20.85) * mm, v(-34.1, 24.87) * mm, v(-33.85, 24.87) * mm]});
            skFitSpline(sketch, "E1504", {"points": [v(-33.85, 24.87) * mm, v(-33.76, 24.87) * mm, v(-33.9, 24.45) * mm, v(-34.17, 23.95) * mm]});
            skFitSpline(sketch, "E1505", {"points": [v(-34.17, 23.95) * mm, v(-34.43, 23.44) * mm, v(-34.93, 22.33) * mm, v(-35.3, 21.48) * mm]});
            skFitSpline(sketch, "E1506", {"points": [v(-35.3, 21.48) * mm, v(-35.65, 20.63) * mm, v(-35.94, 20.12) * mm, v(-35.95, 20.36) * mm]});
            skFitSpline(sketch, "E1507", {"points": [v(-29.4, 21.34) * mm, v(-29.4, 21.96) * mm, v(-29.34, 22.18) * mm, v(-29.27, 21.83) * mm]});
            skFitSpline(sketch, "E1508", {"points": [v(-29.27, 21.83) * mm, v(-29.2, 21.48) * mm, v(-29.2, 20.97) * mm, v(-29.28, 20.7) * mm]});
            skFitSpline(sketch, "E1509", {"points": [v(-29.28, 20.7) * mm, v(-29.35, 20.43) * mm, v(-29.4, 20.72) * mm, v(-29.4, 21.34) * mm]});
            skFitSpline(sketch, "E1510", {"points": [v(-37.94, 21.87) * mm, v(-37.94, 21.93) * mm, v(-37.72, 22.15) * mm, v(-37.44, 22.36) * mm]});
            skFitSpline(sketch, "E1511", {"points": [v(-37.44, 22.36) * mm, v(-37, 22.71) * mm, v(-36.99, 22.7) * mm, v(-37.34, 22.25) * mm]});
            skFitSpline(sketch, "E1512", {"points": [v(-37.34, 22.25) * mm, v(-37.7, 21.78) * mm, v(-37.94, 21.64) * mm, v(-37.94, 21.87) * mm]});
            skFitSpline(sketch, "E1513", {"points": [v(-29.14, 23.17) * mm, v(-29.14, 23.56) * mm, v(-29.08, 23.72) * mm, v(-29, 23.52) * mm]});
            skFitSpline(sketch, "E1514", {"points": [v(-29, 23.52) * mm, v(-28.92, 23.33) * mm, v(-28.92, 23.01) * mm, v(-29, 22.82) * mm]});
            skFitSpline(sketch, "E1515", {"points": [v(-29, 22.82) * mm, v(-29.08, 22.63) * mm, v(-29.14, 22.78) * mm, v(-29.14, 23.17) * mm]});
            skFitSpline(sketch, "E1516", {"points": [v(-36.67, 23.45) * mm, v(-36.39, 23.76) * mm, v(-36.1, 24.02) * mm, v(-36.02, 24.02) * mm]});
            skFitSpline(sketch, "E1517", {"points": [v(-36.02, 24.02) * mm, v(-35.94, 24.02) * mm, v(-36.1, 23.76) * mm, v(-36.39, 23.45) * mm]});
            skFitSpline(sketch, "E1518", {"points": [v(-36.39, 23.45) * mm, v(-36.67, 23.14) * mm, v(-36.96, 22.89) * mm, v(-37.04, 22.89) * mm]});
            skFitSpline(sketch, "E1519", {"points": [v(-37.04, 22.89) * mm, v(-37.11, 22.89) * mm, v(-36.95, 23.14) * mm, v(-36.67, 23.45) * mm]});
            skFitSpline(sketch, "E1520", {"points": [v(-27.72, 23.88) * mm, v(-27.72, 24.34) * mm, v(-27.65, 24.5) * mm, v(-27.58, 24.23) * mm]});
            skFitSpline(sketch, "E1521", {"points": [v(-27.58, 24.23) * mm, v(-27.51, 23.95) * mm, v(-27.52, 23.57) * mm, v(-27.6, 23.38) * mm]});
            skFitSpline(sketch, "E1522", {"points": [v(-27.6, 23.38) * mm, v(-27.67, 23.19) * mm, v(-27.73, 23.41) * mm, v(-27.72, 23.88) * mm]});
            skFitSpline(sketch, "E1523", {"points": [v(-28.87, 24.3) * mm, v(-28.88, 24.53) * mm, v(-28.7, 25.1) * mm, v(-28.5, 25.57) * mm]});
            skFitSpline(sketch, "E1524", {"points": [v(-28.5, 25.57) * mm, v(-28, 26.66) * mm, v(-27.99, 26.15) * mm, v(-28.48, 24.87) * mm]});
            skFitSpline(sketch, "E1525", {"points": [v(-28.48, 24.87) * mm, v(-28.7, 24.32) * mm, v(-28.87, 24.07) * mm, v(-28.87, 24.3) * mm]});
            skFitSpline(sketch, "E1526", {"points": [v(-27.47, 25.31) * mm, v(-27.46, 25.64) * mm, v(-27.4, 25.7) * mm, v(-27.3, 25.48) * mm]});
            skFitSpline(sketch, "E1527", {"points": [v(-27.3, 25.48) * mm, v(-27.22, 25.28) * mm, v(-27.23, 25.04) * mm, v(-27.32, 24.94) * mm]});
            skFitSpline(sketch, "E1528", {"points": [v(-27.32, 24.94) * mm, v(-27.42, 24.85) * mm, v(-27.49, 25.01) * mm, v(-27.47, 25.31) * mm]});
            skFitSpline(sketch, "E1529", {"points": [v(-27.19, 26.28) * mm, v(-27.2, 26.5) * mm, v(-27.08, 26.9) * mm, v(-26.93, 27.12) * mm]});
            skFitSpline(sketch, "E1530", {"points": [v(-26.93, 27.12) * mm, v(-26.6, 27.64) * mm, v(-26.6, 27.2) * mm, v(-26.93, 26.42) * mm]});
            skFitSpline(sketch, "E1531", {"points": [v(-26.93, 26.42) * mm, v(-27.1, 26.05) * mm, v(-27.18, 26) * mm, v(-27.19, 26.28) * mm]});
            skFitSpline(sketch, "E1532", {"points": [v(-24.09, 27.55) * mm, v(-24.1, 28.14) * mm, v(-22.84, 31.07) * mm, v(-22.56, 31.07) * mm]});
            skFitSpline(sketch, "E1533", {"points": [v(-22.56, 31.07) * mm, v(-22.47, 31.07) * mm, v(-22.62, 30.66) * mm, v(-22.88, 30.16) * mm]});
            skFitSpline(sketch, "E1534", {"points": [v(-22.88, 30.16) * mm, v(-23.14, 29.65) * mm, v(-23.52, 28.73) * mm, v(-23.71, 28.11) * mm]});
            skFitSpline(sketch, "E1535", {"points": [v(-23.71, 28.11) * mm, v(-23.91, 27.5) * mm, v(-24.08, 27.24) * mm, v(-24.09, 27.55) * mm]});
            skFitSpline(sketch, "E1536", {"points": [v(-26.65, 27.8) * mm, v(-26.65, 28.1) * mm, v(-25.8, 29.66) * mm, v(-25.65, 29.66) * mm]});
            skFitSpline(sketch, "E1537", {"points": [v(-25.65, 29.66) * mm, v(-25.57, 29.66) * mm, v(-25.72, 29.25) * mm, v(-25.97, 28.75) * mm]});
            skFitSpline(sketch, "E1538", {"points": [v(-25.97, 28.75) * mm, v(-26.5, 27.72) * mm, v(-26.65, 27.5) * mm, v(-26.65, 27.8) * mm]});
            skFitSpline(sketch, "E1539", {"points": [v(-21, 28.92) * mm, v(-21, 29.25) * mm, v(-19.39, 32.3) * mm, v(-18.9, 32.9) * mm]});
            skFitSpline(sketch, "E1540", {"points": [v(-18.9, 32.9) * mm, v(-18.64, 33.22) * mm, v(-18.97, 32.46) * mm, v(-19.63, 31.22) * mm]});
            skFitSpline(sketch, "E1541", {"points": [v(-19.63, 31.22) * mm, v(-20.92, 28.77) * mm, v(-21, 28.62) * mm, v(-21, 28.92) * mm]});
            skFitSpline(sketch, "E1542", {"points": [v(-19.13, 30.23) * mm, v(-18.69, 32) * mm, v(-16.07, 36.05) * mm, v(-14.48, 37.43) * mm]});
            skLineSegment(sketch, "E1543", {"start": v(-14.48, 37.43) * mm, "end": v(-13.84, 37.99) * mm});
            skLineSegment(sketch, "E1544", {"start": v(-13.84, 37.99) * mm, "end": v(-14.39, 37.26) * mm});
            skFitSpline(sketch, "E1545", {"points": [v(-14.39, 37.26) * mm, v(-14.69, 36.86) * mm, v(-15.56, 35.71) * mm, v(-16.31, 34.72) * mm]});
            skFitSpline(sketch, "E1546", {"points": [v(-16.31, 34.72) * mm, v(-17.07, 33.72) * mm, v(-18.06, 32.15) * mm, v(-18.5, 31.22) * mm]});
            skFitSpline(sketch, "E1547", {"points": [v(-18.5, 31.22) * mm, v(-18.95, 30.28) * mm, v(-19.23, 29.84) * mm, v(-19.13, 30.23) * mm]});
            skFitSpline(sketch, "E1548", {"points": [v(-33.2, 32.11) * mm, v(-32.99, 32.2) * mm, v(-32.75, 32.19) * mm, v(-32.65, 32.1) * mm]});
            skFitSpline(sketch, "E1549", {"points": [v(-32.65, 32.1) * mm, v(-32.56, 32) * mm, v(-32.72, 31.93) * mm, v(-33.02, 31.94) * mm]});
            skFitSpline(sketch, "E1550", {"points": [v(-33.02, 31.94) * mm, v(-33.35, 31.96) * mm, v(-33.42, 32.02) * mm, v(-33.2, 32.11) * mm]});
            skFitSpline(sketch, "E1551", {"points": [v(-41.25, 32.68) * mm, v(-40.98, 32.75) * mm, v(-40.54, 32.75) * mm, v(-40.27, 32.68) * mm]});
            skFitSpline(sketch, "E1552", {"points": [v(-40.27, 32.68) * mm, v(-40, 32.6) * mm, v(-40.22, 32.55) * mm, v(-40.76, 32.55) * mm]});
            skFitSpline(sketch, "E1553", {"points": [v(-40.76, 32.55) * mm, v(-41.3, 32.55) * mm, v(-41.53, 32.6) * mm, v(-41.25, 32.68) * mm]});
            skFitSpline(sketch, "E1554", {"points": [v(-39.04, 32.87) * mm, v(-38.98, 32.93) * mm, v(-37.78, 33.05) * mm, v(-36.39, 33.13) * mm]});
            skFitSpline(sketch, "E1555", {"points": [v(-36.39, 33.13) * mm, v(-34.51, 33.25) * mm, v(-34.22, 33.23) * mm, v(-35.26, 33.05) * mm]});
            skFitSpline(sketch, "E1556", {"points": [v(-35.26, 33.05) * mm, v(-36.73, 32.8) * mm, v(-39.25, 32.69) * mm, v(-39.04, 32.87) * mm]});
            skFitSpline(sketch, "E1557", {"points": [v(-33.35, 33.53) * mm, v(-33.07, 33.6) * mm, v(-32.7, 33.6) * mm, v(-32.5, 33.52) * mm]});
            skFitSpline(sketch, "E1558", {"points": [v(-32.5, 33.52) * mm, v(-32.3, 33.44) * mm, v(-32.53, 33.38) * mm, v(-33, 33.39) * mm]});
            skFitSpline(sketch, "E1559", {"points": [v(-33, 33.39) * mm, v(-33.46, 33.4) * mm, v(-33.62, 33.46) * mm, v(-33.35, 33.53) * mm]});
            skFitSpline(sketch, "E1560", {"points": [v(-35.4, 34.44) * mm, v(-33.61, 34.56) * mm, v(-31.58, 34.74) * mm, v(-30.88, 34.84) * mm]});
            skFitSpline(sketch, "E1561", {"points": [v(-30.88, 34.84) * mm, v(-29.77, 35) * mm, v(-29.72, 34.98) * mm, v(-30.46, 34.72) * mm]});
            skFitSpline(sketch, "E1562", {"points": [v(-30.46, 34.72) * mm, v(-30.92, 34.56) * mm, v(-32.96, 34.38) * mm, v(-34.97, 34.33) * mm]});
            skLineSegment(sketch, "E1563", {"start": v(-34.97, 34.33) * mm, "end": v(-38.64, 34.22) * mm});
            skLineSegment(sketch, "E1564", {"start": v(-38.64, 34.22) * mm, "end": v(-35.4, 34.44) * mm});
            skFitSpline(sketch, "E1565", {"points": [v(-29.26, 35.21) * mm, v(-29.07, 35.3) * mm, v(-28.75, 35.3) * mm, v(-28.55, 35.21) * mm]});
            skFitSpline(sketch, "E1566", {"points": [v(-28.55, 35.21) * mm, v(-28.36, 35.13) * mm, v(-28.52, 35.07) * mm, v(-28.9, 35.07) * mm]});
            skFitSpline(sketch, "E1567", {"points": [v(-28.9, 35.07) * mm, v(-29.3, 35.07) * mm, v(-29.45, 35.13) * mm, v(-29.26, 35.21) * mm]});
            skFitSpline(sketch, "E1568", {"points": [v(-39.68, 36.35) * mm, v(-39.48, 36.43) * mm, v(-39.24, 36.42) * mm, v(-39.14, 36.32) * mm]});
            skFitSpline(sketch, "E1569", {"points": [v(-39.14, 36.32) * mm, v(-39.05, 36.23) * mm, v(-39.22, 36.16) * mm, v(-39.51, 36.18) * mm]});
            skFitSpline(sketch, "E1570", {"points": [v(-39.51, 36.18) * mm, v(-39.84, 36.2) * mm, v(-39.9, 36.26) * mm, v(-39.68, 36.35) * mm]});
            skFitSpline(sketch, "E1571", {"points": [v(-35.75, 36.9) * mm, v(-35.56, 36.98) * mm, v(-35.24, 36.98) * mm, v(-35.04, 36.9) * mm]});
            skFitSpline(sketch, "E1572", {"points": [v(-35.04, 36.9) * mm, v(-34.85, 36.83) * mm, v(-35, 36.76) * mm, v(-35.4, 36.76) * mm]});
            skFitSpline(sketch, "E1573", {"points": [v(-35.4, 36.76) * mm, v(-35.79, 36.76) * mm, v(-35.94, 36.83) * mm, v(-35.75, 36.9) * mm]});
            skFitSpline(sketch, "E1574", {"points": [v(-32.63, 37.2) * mm, v(-32.42, 37.28) * mm, v(-32.18, 37.27) * mm, v(-32.09, 37.17) * mm]});
            skFitSpline(sketch, "E1575", {"points": [v(-32.09, 37.17) * mm, v(-32, 37.08) * mm, v(-32.16, 37.01) * mm, v(-32.46, 37.02) * mm]});
            skFitSpline(sketch, "E1576", {"points": [v(-32.46, 37.02) * mm, v(-32.79, 37.04) * mm, v(-32.85, 37.1) * mm, v(-32.63, 37.2) * mm]});
            skFitSpline(sketch, "E1577", {"points": [v(-35.56, 37.73) * mm, v(-36.19, 37.96) * mm, v(-37.14, 38.53) * mm, v(-37.67, 39) * mm]});
            skLineSegment(sketch, "E1578", {"start": v(-37.67, 39) * mm, "end": v(-38.64, 39.86) * mm});
            skLineSegment(sketch, "E1579", {"start": v(-38.64, 39.86) * mm, "end": v(-37.6, 39.1) * mm});
            skFitSpline(sketch, "E1580", {"points": [v(-37.6, 39.1) * mm, v(-37.01, 38.7) * mm, v(-35.8, 38.12) * mm, v(-34.91, 37.83) * mm]});
            skFitSpline(sketch, "E1581", {"points": [v(-34.91, 37.83) * mm, v(-34.01, 37.55) * mm, v(-33.53, 37.32) * mm, v(-33.85, 37.32) * mm]});
            skFitSpline(sketch, "E1582", {"points": [v(-33.85, 37.32) * mm, v(-34.16, 37.32) * mm, v(-34.93, 37.51) * mm, v(-35.56, 37.73) * mm]});
            skFitSpline(sketch, "E1583", {"points": [v(28.69, 8.78) * mm, v(28.83, 8.78) * mm, v(28.95, 8.94) * mm, v(28.95, 9.13) * mm]});
            skFitSpline(sketch, "E1584", {"points": [v(28.95, 9.13) * mm, v(28.96, 9.9) * mm, v(29.53, 10.3) * mm, v(30.83, 10.48) * mm]});
            skLineSegment(sketch, "E1585", {"start": v(30.83, 10.48) * mm, "end": v(32.2, 10.65) * mm});
            skLineSegment(sketch, "E1586", {"start": v(32.2, 10.65) * mm, "end": v(31.14, 10.88) * mm});
            skFitSpline(sketch, "E1587", {"points": [v(31.14, 10.88) * mm, v(29.64, 11.2) * mm, v(28.74, 10.88) * mm, v(28.1, 9.83) * mm]});
            skFitSpline(sketch, "E1588", {"points": [v(28.1, 9.83) * mm, v(27.42, 8.73) * mm, v(27.4, 8.38) * mm, v(27.98, 8.6) * mm]});
            skFitSpline(sketch, "E1589", {"points": [v(27.98, 8.6) * mm, v(28.23, 8.7) * mm, v(28.55, 8.78) * mm, v(28.69, 8.78) * mm]});
            skFitSpline(sketch, "E1590", {"points": [v(33.3, 9.23) * mm, v(33.52, 9.8) * mm, v(33.5, 9.92) * mm, v(33.25, 9.85) * mm]});
            skFitSpline(sketch, "E1591", {"points": [v(33.25, 9.85) * mm, v(33.14, 9.83) * mm, v(32.51, 9.9) * mm, v(31.86, 10.02) * mm]});
            skFitSpline(sketch, "E1592", {"points": [v(31.86, 10.02) * mm, v(31.13, 10.15) * mm, v(30.47, 10.12) * mm, v(30.1, 9.92) * mm]});
            skFitSpline(sketch, "E1593", {"points": [v(30.1, 9.92) * mm, v(29.23, 9.46) * mm, v(29.39, 9.16) * mm, v(30.43, 9.28) * mm]});
            skFitSpline(sketch, "E1594", {"points": [v(30.43, 9.28) * mm, v(30.94, 9.34) * mm, v(31.67, 9.26) * mm, v(32.05, 9.1) * mm]});
            skFitSpline(sketch, "E1595", {"points": [v(32.05, 9.1) * mm, v(33.02, 8.7) * mm, v(33.1, 8.72) * mm, v(33.3, 9.23) * mm]});
            skFitSpline(sketch, "E1596", {"points": [v(33.88, 10.6) * mm, v(34.4, 10.81) * mm, v(35.02, 11.35) * mm, v(35.25, 11.8) * mm]});
            skFitSpline(sketch, "E1597", {"points": [v(35.25, 11.8) * mm, v(35.48, 12.23) * mm, v(35.91, 12.82) * mm, v(36.22, 13.1) * mm]});
            skFitSpline(sketch, "E1598", {"points": [v(36.22, 13.1) * mm, v(36.58, 13.41) * mm, v(36.72, 13.83) * mm, v(36.64, 14.27) * mm]});
            skFitSpline(sketch, "E1599", {"points": [v(36.64, 14.27) * mm, v(36.57, 14.64) * mm, v(36.7, 15.3) * mm, v(36.92, 15.74) * mm]});
            skFitSpline(sketch, "E1600", {"points": [v(36.92, 15.74) * mm, v(37.14, 16.18) * mm, v(37.57, 17.05) * mm, v(37.86, 17.67) * mm]});
            skFitSpline(sketch, "E1601", {"points": [v(37.86, 17.67) * mm, v(38.54, 19.07) * mm, v(39.6, 19.24) * mm, v(40.17, 18.04) * mm]});
            skFitSpline(sketch, "E1602", {"points": [v(40.17, 18.04) * mm, v(40.53, 17.3) * mm, v(40.7, 17.2) * mm, v(42.29, 16.84) * mm]});
            skFitSpline(sketch, "E1603", {"points": [v(42.29, 16.84) * mm, v(42.95, 16.7) * mm, v(43.11, 16.78) * mm, v(43.35, 17.4) * mm]});
            skFitSpline(sketch, "E1604", {"points": [v(43.35, 17.4) * mm, v(43.74, 18.43) * mm, v(43.72, 18.53) * mm, v(42.81, 19.56) * mm]});
            skFitSpline(sketch, "E1605", {"points": [v(42.81, 19.56) * mm, v(42.37, 20.07) * mm, v(41.91, 20.9) * mm, v(41.8, 21.4) * mm]});
            skFitSpline(sketch, "E1606", {"points": [v(41.8, 21.4) * mm, v(41.54, 22.6) * mm, v(40.7, 23.16) * mm, v(39.12, 23.2) * mm]});
            skLineSegment(sketch, "E1607", {"start": v(39.12, 23.2) * mm, "end": v(37.84, 23.24) * mm});
            skLineSegment(sketch, "E1608", {"start": v(37.84, 23.24) * mm, "end": v(38.9, 23.44) * mm});
            skFitSpline(sketch, "E1609", {"points": [v(38.9, 23.44) * mm, v(40.38, 23.73) * mm, v(40.45, 23.92) * mm, v(39.28, 24.41) * mm]});
            skFitSpline(sketch, "E1610", {"points": [v(39.28, 24.41) * mm, v(38.35, 24.8) * mm, v(38.26, 24.93) * mm, v(38.26, 25.97) * mm]});
            skFitSpline(sketch, "E1611", {"points": [v(38.26, 25.97) * mm, v(38.26, 27.47) * mm, v(37.39, 28.1) * mm, v(35.6, 27.9) * mm]});
            skFitSpline(sketch, "E1612", {"points": [v(35.6, 27.9) * mm, v(34.58, 27.79) * mm, v(34.39, 27.84) * mm, v(34.46, 28.22) * mm]});
            skFitSpline(sketch, "E1613", {"points": [v(34.46, 28.22) * mm, v(34.51, 28.47) * mm, v(34.56, 28.77) * mm, v(34.57, 28.89) * mm]});
            skFitSpline(sketch, "E1614", {"points": [v(34.57, 28.89) * mm, v(34.58, 29) * mm, v(35.08, 29.1) * mm, v(35.67, 29.1) * mm]});
            skFitSpline(sketch, "E1615", {"points": [v(35.67, 29.1) * mm, v(36.26, 29.1) * mm, v(36.98, 29.27) * mm, v(37.27, 29.48) * mm]});
            skFitSpline(sketch, "E1616", {"points": [v(37.27, 29.48) * mm, v(37.77, 29.85) * mm, v(38.66, 32.18) * mm, v(38.4, 32.45) * mm]});
            skFitSpline(sketch, "E1617", {"points": [v(38.4, 32.45) * mm, v(38.33, 32.52) * mm, v(37.63, 32.6) * mm, v(36.86, 32.62) * mm]});
            skFitSpline(sketch, "E1618", {"points": [v(36.86, 32.62) * mm, v(34.89, 32.7) * mm, v(34.71, 33.05) * mm, v(36.65, 33.05) * mm]});
            skFitSpline(sketch, "E1619", {"points": [v(36.65, 33.05) * mm, v(37.95, 33.05) * mm, v(38.3, 33.16) * mm, v(38.66, 33.67) * mm]});
            skFitSpline(sketch, "E1620", {"points": [v(38.66, 33.67) * mm, v(38.9, 34.02) * mm, v(39.02, 34.56) * mm, v(38.93, 34.92) * mm]});
            skFitSpline(sketch, "E1621", {"points": [v(38.93, 34.92) * mm, v(38.84, 35.29) * mm, v(38.96, 35.83) * mm, v(39.22, 36.2) * mm]});
            skFitSpline(sketch, "E1622", {"points": [v(39.22, 36.2) * mm, v(39.47, 36.56) * mm, v(39.67, 37.13) * mm, v(39.67, 37.47) * mm]});
            skFitSpline(sketch, "E1623", {"points": [v(39.67, 37.47) * mm, v(39.67, 37.98) * mm, v(39.46, 38.14) * mm, v(38.64, 38.3) * mm]});
            skFitSpline(sketch, "E1624", {"points": [v(38.64, 38.3) * mm, v(38, 38.42) * mm, v(37.4, 38.36) * mm, v(37.08, 38.16) * mm]});
            skFitSpline(sketch, "E1625", {"points": [v(37.08, 38.16) * mm, v(36.79, 37.98) * mm, v(36.43, 37.9) * mm, v(36.29, 37.99) * mm]});
            skFitSpline(sketch, "E1626", {"points": [v(36.29, 37.99) * mm, v(36.15, 38.08) * mm, v(35.58, 37.96) * mm, v(35.03, 37.73) * mm]});
            skLineSegment(sketch, "E1627", {"start": v(35.03, 37.73) * mm, "end": v(34.04, 37.32) * mm});
            skLineSegment(sketch, "E1628", {"start": v(34.04, 37.32) * mm, "end": v(34.47, 37.98) * mm});
            skFitSpline(sketch, "E1629", {"points": [v(34.47, 37.98) * mm, v(35.01, 38.8) * mm, v(34.76, 42.08) * mm, v(34.15, 42.08) * mm]});
            skFitSpline(sketch, "E1630", {"points": [v(34.15, 42.08) * mm, v(33.57, 42.08) * mm, v(32.7, 40.64) * mm, v(32.48, 39.31) * mm]});
            skFitSpline(sketch, "E1631", {"points": [v(32.48, 39.31) * mm, v(32.37, 38.64) * mm, v(32, 37.77) * mm, v(31.66, 37.38) * mm]});
            skLineSegment(sketch, "E1632", {"start": v(31.66, 37.38) * mm, "end": v(31.05, 36.66) * mm});
            skLineSegment(sketch, "E1633", {"start": v(31.05, 36.66) * mm, "end": v(31.15, 37.79) * mm});
            skFitSpline(sketch, "E1634", {"points": [v(31.15, 37.79) * mm, v(31.21, 38.4) * mm, v(31.13, 39) * mm, v(30.97, 39.09) * mm]});
            skFitSpline(sketch, "E1635", {"points": [v(30.97, 39.09) * mm, v(30.5, 39.38) * mm, v(29.8, 38.42) * mm, v(29.8, 37.47) * mm]});
            skFitSpline(sketch, "E1636", {"points": [v(29.8, 37.47) * mm, v(29.8, 36.71) * mm, v(29.94, 36.5) * mm, v(30.67, 36.23) * mm]});
            skFitSpline(sketch, "E1637", {"points": [v(30.67, 36.23) * mm, v(31.37, 35.97) * mm, v(31.5, 35.79) * mm, v(31.35, 35.32) * mm]});
            skFitSpline(sketch, "E1638", {"points": [v(31.35, 35.32) * mm, v(31.1, 34.52) * mm, v(31.68, 34.58) * mm, v(33.02, 35.49) * mm]});
            skFitSpline(sketch, "E1639", {"points": [v(33.02, 35.49) * mm, v(33.62, 35.9) * mm, v(34.02, 36.09) * mm, v(33.91, 35.91) * mm]});
            skFitSpline(sketch, "E1640", {"points": [v(33.91, 35.91) * mm, v(33.8, 35.74) * mm, v(33.15, 35.27) * mm, v(32.46, 34.86) * mm]});
            skFitSpline(sketch, "E1641", {"points": [v(32.46, 34.86) * mm, v(31.02, 34.02) * mm, v(30.73, 33.16) * mm, v(31.98, 33.45) * mm]});
            skFitSpline(sketch, "E1642", {"points": [v(31.98, 33.45) * mm, v(32.4, 33.55) * mm, v(33.61, 34.05) * mm, v(34.65, 34.55) * mm]});
            skFitSpline(sketch, "E1643", {"points": [v(34.65, 34.55) * mm, v(35.7, 35.06) * mm, v(36.42, 35.33) * mm, v(36.28, 35.16) * mm]});
            skFitSpline(sketch, "E1644", {"points": [v(36.28, 35.16) * mm, v(35.81, 34.6) * mm, v(33.36, 33.38) * mm, v(31.99, 33.04) * mm]});
            skFitSpline(sketch, "E1645", {"points": [v(31.99, 33.04) * mm, v(30.96, 32.78) * mm, v(30.56, 32.5) * mm, v(30.24, 31.88) * mm]});
            skFitSpline(sketch, "E1646", {"points": [v(30.24, 31.88) * mm, v(29.84, 31.08) * mm, v(29.85, 31.04) * mm, v(30.58, 30.76) * mm]});
            skFitSpline(sketch, "E1647", {"points": [v(30.58, 30.76) * mm, v(31, 30.6) * mm, v(32.04, 30.37) * mm, v(32.9, 30.24) * mm]});
            skLineSegment(sketch, "E1648", {"start": v(32.9, 30.24) * mm, "end": v(34.45, 30.01) * mm});
            skLineSegment(sketch, "E1649", {"start": v(34.45, 30.01) * mm, "end": v(32.96, 29.98) * mm});
            skFitSpline(sketch, "E1650", {"points": [v(32.96, 29.98) * mm, v(32.14, 29.96) * mm, v(31.02, 30.13) * mm, v(30.47, 30.36) * mm]});
            skFitSpline(sketch, "E1651", {"points": [v(30.47, 30.36) * mm, v(29.65, 30.7) * mm, v(29.27, 30.72) * mm, v(28.39, 30.44) * mm]});
            skLineSegment(sketch, "E1652", {"start": v(28.39, 30.44) * mm, "end": v(27.3, 30.1) * mm});
            skLineSegment(sketch, "E1653", {"start": v(27.3, 30.1) * mm, "end": v(28.84, 28.45) * mm});
            skFitSpline(sketch, "E1654", {"points": [v(28.84, 28.45) * mm, v(30.56, 26.6) * mm, v(32.79, 23.4) * mm, v(33.7, 21.48) * mm]});
            skFitSpline(sketch, "E1655", {"points": [v(33.7, 21.48) * mm, v(34.38, 20.09) * mm, v(34.33, 20.15) * mm, v(32, 23.71) * mm]});
            skFitSpline(sketch, "E1656", {"points": [v(32, 23.71) * mm, v(31.13, 25.06) * mm, v(29.24, 27.37) * mm, v(27.81, 28.83) * mm]});
            skFitSpline(sketch, "E1657", {"points": [v(27.81, 28.83) * mm, v(26.38, 30.3) * mm, v(25.37, 31.28) * mm, v(25.56, 31) * mm]});
            skFitSpline(sketch, "E1658", {"points": [v(25.56, 31) * mm, v(25.84, 30.62) * mm, v(25.84, 30.42) * mm, v(25.57, 30.1) * mm]});
            skFitSpline(sketch, "E1659", {"points": [v(25.57, 30.1) * mm, v(25.3, 29.77) * mm, v(25.4, 29.45) * mm, v(26.07, 28.48) * mm]});
            skFitSpline(sketch, "E1660", {"points": [v(26.07, 28.48) * mm, v(28.3, 25.22) * mm, v(29.24, 22.45) * mm, v(29.37, 18.8) * mm]});
            skLineSegment(sketch, "E1661", {"start": v(29.37, 18.8) * mm, "end": v(29.47, 15.98) * mm});
            skLineSegment(sketch, "E1662", {"start": v(29.47, 15.98) * mm, "end": v(29.24, 18.52) * mm});
            skFitSpline(sketch, "E1663", {"points": [v(29.24, 18.52) * mm, v(29.12, 19.91) * mm, v(28.75, 21.88) * mm, v(28.43, 22.89) * mm]});
            skFitSpline(sketch, "E1664", {"points": [v(28.43, 22.89) * mm, v(27.7, 25.12) * mm, v(25.3, 29.3) * mm, v(25, 28.8) * mm]});
            skFitSpline(sketch, "E1665", {"points": [v(25, 28.8) * mm, v(24.84, 28.55) * mm, v(24.73, 28.56) * mm, v(24.56, 28.83) * mm]});
            skFitSpline(sketch, "E1666", {"points": [v(24.56, 28.83) * mm, v(24.4, 29.1) * mm, v(24.27, 29) * mm, v(24.1, 28.52) * mm]});
            skFitSpline(sketch, "E1667", {"points": [v(24.1, 28.52) * mm, v(23.9, 27.99) * mm, v(24.02, 27.6) * mm, v(24.72, 26.61) * mm]});
            skFitSpline(sketch, "E1668", {"points": [v(24.72, 26.61) * mm, v(25.97, 24.84) * mm, v(27, 23.17) * mm, v(26.85, 23.17) * mm]});
            skFitSpline(sketch, "E1669", {"points": [v(26.85, 23.17) * mm, v(26.78, 23.17) * mm, v(26.06, 24.13) * mm, v(25.26, 25.3) * mm]});
            skFitSpline(sketch, "E1670", {"points": [v(25.26, 25.3) * mm, v(23.8, 27.4) * mm, v(23.16, 27.93) * mm, v(23.95, 26.37) * mm]});
            skFitSpline(sketch, "E1671", {"points": [v(23.95, 26.37) * mm, v(24.18, 25.93) * mm, v(24.44, 25.25) * mm, v(24.54, 24.87) * mm]});
            skFitSpline(sketch, "E1672", {"points": [v(24.54, 24.87) * mm, v(24.64, 24.48) * mm, v(24.4, 24.85) * mm, v(24.01, 25.69) * mm]});
            skFitSpline(sketch, "E1673", {"points": [v(24.01, 25.69) * mm, v(23.62, 26.52) * mm, v(23.22, 27.13) * mm, v(23.12, 27.03) * mm]});
            skFitSpline(sketch, "E1674", {"points": [v(23.12, 27.03) * mm, v(23.02, 26.93) * mm, v(22.74, 27) * mm, v(22.51, 27.2) * mm]});
            skFitSpline(sketch, "E1675", {"points": [v(22.51, 27.2) * mm, v(22.16, 27.49) * mm, v(22.12, 27.45) * mm, v(22.28, 26.95) * mm]});
            skFitSpline(sketch, "E1676", {"points": [v(22.28, 26.95) * mm, v(22.9, 24.98) * mm, v(23.29, 22.1) * mm, v(23.26, 19.64) * mm]});
            skLineSegment(sketch, "E1677", {"start": v(23.26, 19.64) * mm, "end": v(23.22, 16.82) * mm});
            skLineSegment(sketch, "E1678", {"start": v(23.22, 16.82) * mm, "end": v(23.01, 20.07) * mm});
            skFitSpline(sketch, "E1679", {"points": [v(23.01, 20.07) * mm, v(22.69, 25.27) * mm, v(21.35, 29.38) * mm, v(19.74, 30.14) * mm]});
            skFitSpline(sketch, "E1680", {"points": [v(19.74, 30.14) * mm, v(19, 30.5) * mm, v(18.94, 30.43) * mm, v(19.36, 29.64) * mm]});
            skFitSpline(sketch, "E1681", {"points": [v(19.36, 29.64) * mm, v(19.99, 28.48) * mm, v(19.38, 29.18) * mm, v(18.41, 30.75) * mm]});
            skFitSpline(sketch, "E1682", {"points": [v(18.41, 30.75) * mm, v(17.85, 31.66) * mm, v(16.47, 33.27) * mm, v(15.34, 34.34) * mm]});
            skFitSpline(sketch, "E1683", {"points": [v(15.34, 34.34) * mm, v(14.21, 35.4) * mm, v(13.27, 36.38) * mm, v(13.25, 36.5) * mm]});
            skFitSpline(sketch, "E1684", {"points": [v(13.25, 36.5) * mm, v(13.23, 36.62) * mm, v(13.2, 37.45) * mm, v(13.17, 38.34) * mm]});
            skLineSegment(sketch, "E1685", {"start": v(13.17, 38.34) * mm, "end": v(13.12, 39.96) * mm});
            skLineSegment(sketch, "E1686", {"start": v(13.12, 39.96) * mm, "end": v(12.29, 38.99) * mm});
            skFitSpline(sketch, "E1687", {"points": [v(12.29, 38.99) * mm, v(11.83, 38.45) * mm, v(11.45, 37.91) * mm, v(11.45, 37.8) * mm]});
            skFitSpline(sketch, "E1688", {"points": [v(11.45, 37.8) * mm, v(11.45, 37.68) * mm, v(11.84, 37.38) * mm, v(12.32, 37.13) * mm]});
            skFitSpline(sketch, "E1689", {"points": [v(12.32, 37.13) * mm, v(12.8, 36.88) * mm, v(13.13, 36.6) * mm, v(13.04, 36.52) * mm]});
            skFitSpline(sketch, "E1690", {"points": [v(13.04, 36.52) * mm, v(12.96, 36.44) * mm, v(12.45, 36.64) * mm, v(11.91, 36.98) * mm]});
            skFitSpline(sketch, "E1691", {"points": [v(11.91, 36.98) * mm, v(10.64, 37.76) * mm, v(10.12, 37.2) * mm, v(11.34, 36.34) * mm]});
            skFitSpline(sketch, "E1692", {"points": [v(11.34, 36.34) * mm, v(12.7, 35.39) * mm, v(14.73, 33.2) * mm, v(15.56, 31.78) * mm]});
            skFitSpline(sketch, "E1693", {"points": [v(15.56, 31.78) * mm, v(16.55, 30.09) * mm, v(17.54, 27.36) * mm, v(17.77, 25.71) * mm]});
            skFitSpline(sketch, "E1694", {"points": [v(17.77, 25.71) * mm, v(17.89, 24.82) * mm, v(17.74, 25.12) * mm, v(17.29, 26.7) * mm]});
            skFitSpline(sketch, "E1695", {"points": [v(17.29, 26.7) * mm, v(16.11, 30.79) * mm, v(14.3, 33.63) * mm, v(11.64, 35.53) * mm]});
            skLineSegment(sketch, "E1696", {"start": v(11.64, 35.53) * mm, "end": v(10.35, 36.45) * mm});
            skLineSegment(sketch, "E1697", {"start": v(10.35, 36.45) * mm, "end": v(9.88, 35.74) * mm});
            skFitSpline(sketch, "E1698", {"points": [v(9.88, 35.74) * mm, v(9.42, 35.04) * mm, v(9.44, 35) * mm, v(10.79, 33.52) * mm]});
            skFitSpline(sketch, "E1699", {"points": [v(10.79, 33.52) * mm, v(12.01, 32.18) * mm, v(13.67, 29.66) * mm, v(13.33, 29.66) * mm]});
            skFitSpline(sketch, "E1700", {"points": [v(13.33, 29.66) * mm, v(13.26, 29.66) * mm, v(12.82, 30.27) * mm, v(12.34, 31) * mm]});
            skFitSpline(sketch, "E1701", {"points": [v(12.34, 31) * mm, v(11.87, 31.74) * mm, v(10.97, 32.84) * mm, v(10.35, 33.45) * mm]});
            skFitSpline(sketch, "E1702", {"points": [v(10.35, 33.45) * mm, v(8.72, 35.04) * mm, v(8.54, 34.2) * mm, v(10.02, 31.91) * mm]});
            skFitSpline(sketch, "E1703", {"points": [v(10.02, 31.91) * mm, v(11.06, 30.31) * mm, v(11.36, 29.66) * mm, v(11.07, 29.66) * mm]});
            skFitSpline(sketch, "E1704", {"points": [v(11.07, 29.66) * mm, v(11.01, 29.66) * mm, v(10.49, 30.44) * mm, v(9.9, 31.4) * mm]});
            skFitSpline(sketch, "E1705", {"points": [v(9.9, 31.4) * mm, v(8.66, 33.4) * mm, v(8.39, 33.26) * mm, v(8.14, 30.51) * mm]});
            skFitSpline(sketch, "E1706", {"points": [v(8.14, 30.51) * mm, v(7.96, 28.58) * mm, v(8.14, 28.42) * mm, v(10.7, 28.17) * mm]});
            skFitSpline(sketch, "E1707", {"points": [v(10.7, 28.17) * mm, v(11.6, 28.08) * mm, v(12.8, 27.77) * mm, v(13.36, 27.47) * mm]});
            skFitSpline(sketch, "E1708", {"points": [v(13.36, 27.47) * mm, v(14.54, 26.86) * mm, v(15.82, 25.34) * mm, v(16.07, 24.26) * mm]});
            skFitSpline(sketch, "E1709", {"points": [v(16.07, 24.26) * mm, v(16.24, 23.53) * mm, v(16.23, 23.52) * mm, v(15.19, 23.76) * mm]});
            skFitSpline(sketch, "E1710", {"points": [v(15.19, 23.76) * mm, v(14.6, 23.9) * mm, v(13.6, 23.94) * mm, v(12.93, 23.84) * mm]});
            skFitSpline(sketch, "E1711", {"points": [v(12.93, 23.84) * mm, v(11.55, 23.65) * mm, v(11.38, 23.13) * mm, v(12.32, 21.94) * mm]});
            skFitSpline(sketch, "E1712", {"points": [v(12.32, 21.94) * mm, v(13, 21.09) * mm, v(13.66, 21) * mm, v(14.9, 21.65) * mm]});
            skFitSpline(sketch, "E1713", {"points": [v(14.9, 21.65) * mm, v(15.72, 22.08) * mm, v(15.76, 22.08) * mm, v(15.54, 21.58) * mm]});
            skFitSpline(sketch, "E1714", {"points": [v(15.54, 21.58) * mm, v(15.06, 20.44) * mm, v(15.05, 19.51) * mm, v(15.51, 19.34) * mm]});
            skFitSpline(sketch, "E1715", {"points": [v(15.51, 19.34) * mm, v(15.76, 19.24) * mm, v(15.97, 19) * mm, v(15.97, 18.8) * mm]});
            skFitSpline(sketch, "E1716", {"points": [v(15.97, 18.8) * mm, v(15.97, 18.6) * mm, v(16.3, 18.23) * mm, v(16.7, 17.96) * mm]});
            skFitSpline(sketch, "E1717", {"points": [v(16.7, 17.96) * mm, v(17.5, 17.44) * mm, v(18.06, 17.68) * mm, v(18.38, 18.7) * mm]});
            skFitSpline(sketch, "E1718", {"points": [v(18.38, 18.7) * mm, v(18.48, 19) * mm, v(18.9, 19.31) * mm, v(19.38, 19.4) * mm]});
            skFitSpline(sketch, "E1719", {"points": [v(19.38, 19.4) * mm, v(19.83, 19.5) * mm, v(20.2, 19.65) * mm, v(20.21, 19.75) * mm]});
            skFitSpline(sketch, "E1720", {"points": [v(20.21, 19.75) * mm, v(20.22, 19.85) * mm, v(20.34, 20.5) * mm, v(20.47, 21.2) * mm]});
            skFitSpline(sketch, "E1721", {"points": [v(20.47, 21.2) * mm, v(20.7, 22.35) * mm, v(20.66, 22.54) * mm, v(19.98, 23.24) * mm]});
            skFitSpline(sketch, "E1722", {"points": [v(19.98, 23.24) * mm, v(19.36, 23.9) * mm, v(19.29, 24.14) * mm, v(19.51, 24.77) * mm]});
            skFitSpline(sketch, "E1723", {"points": [v(19.51, 24.77) * mm, v(19.84, 25.7) * mm, v(20.28, 25.87) * mm, v(20.87, 25.28) * mm]});
            skFitSpline(sketch, "E1724", {"points": [v(20.87, 25.28) * mm, v(21.44, 24.72) * mm, v(21.45, 23.83) * mm, v(20.9, 21) * mm]});
            skFitSpline(sketch, "E1725", {"points": [v(20.9, 21) * mm, v(20.35, 18.1) * mm, v(20.36, 17.8) * mm, v(21.05, 17.8) * mm]});
            skFitSpline(sketch, "E1726", {"points": [v(21.05, 17.8) * mm, v(21.52, 17.8) * mm, v(21.61, 17.62) * mm, v(21.62, 16.61) * mm]});
            skFitSpline(sketch, "E1727", {"points": [v(21.62, 16.61) * mm, v(21.62, 15.88) * mm, v(21.83, 15.14) * mm, v(22.15, 14.73) * mm]});
            skLineSegment(sketch, "E1728", {"start": v(22.15, 14.73) * mm, "end": v(22.67, 14.05) * mm});
            skLineSegment(sketch, "E1729", {"start": v(22.67, 14.05) * mm, "end": v(23.67, 14.67) * mm});
            skFitSpline(sketch, "E1730", {"points": [v(23.67, 14.67) * mm, v(24.23, 15.01) * mm, v(24.84, 15.67) * mm, v(25.04, 16.12) * mm]});
            skFitSpline(sketch, "E1731", {"points": [v(25.04, 16.12) * mm, v(25.35, 16.8) * mm, v(25.56, 16.94) * mm, v(26.26, 16.88) * mm]});
            skFitSpline(sketch, "E1732", {"points": [v(26.26, 16.88) * mm, v(27.1, 16.82) * mm, v(27.12, 16.86) * mm, v(27.2, 18.18) * mm]});
            skFitSpline(sketch, "E1733", {"points": [v(27.2, 18.18) * mm, v(27.28, 19.35) * mm, v(27.17, 19.66) * mm, v(26.43, 20.52) * mm]});
            skFitSpline(sketch, "E1734", {"points": [v(26.43, 20.52) * mm, v(25.52, 21.55) * mm, v(25.46, 21.72) * mm, v(25.73, 22.44) * mm]});
            skFitSpline(sketch, "E1735", {"points": [v(25.73, 22.44) * mm, v(25.94, 23) * mm, v(27.14, 23.04) * mm, v(27.34, 22.5) * mm]});
            skFitSpline(sketch, "E1736", {"points": [v(27.34, 22.5) * mm, v(27.76, 21.43) * mm, v(27.84, 19.34) * mm, v(27.55, 17.6) * mm]});
            skFitSpline(sketch, "E1737", {"points": [v(27.55, 17.6) * mm, v(27.26, 15.86) * mm, v(27.28, 15.54) * mm, v(27.8, 14.34) * mm]});
            skFitSpline(sketch, "E1738", {"points": [v(27.8, 14.34) * mm, v(28.44, 12.84) * mm, v(29, 12.66) * mm, v(30.16, 13.58) * mm]});
            skFitSpline(sketch, "E1739", {"points": [v(30.16, 13.58) * mm, v(30.74, 14.04) * mm, v(31.02, 14.1) * mm, v(31.63, 13.86) * mm]});
            skFitSpline(sketch, "E1740", {"points": [v(31.63, 13.86) * mm, v(32.66, 13.47) * mm, v(32.9, 13.7) * mm, v(32.9, 15.08) * mm]});
            skFitSpline(sketch, "E1741", {"points": [v(32.9, 15.08) * mm, v(32.9, 15.88) * mm, v(32.67, 16.6) * mm, v(32.2, 17.3) * mm]});
            skFitSpline(sketch, "E1742", {"points": [v(32.2, 17.3) * mm, v(31.4, 18.49) * mm, v(31.33, 18.9) * mm, v(31.86, 19.62) * mm]});
            skFitSpline(sketch, "E1743", {"points": [v(31.86, 19.62) * mm, v(32.22, 20.1) * mm, v(32.25, 20.1) * mm, v(32.73, 19.63) * mm]});
            skFitSpline(sketch, "E1744", {"points": [v(32.73, 19.63) * mm, v(33.08, 19.29) * mm, v(33.2, 18.86) * mm, v(33.1, 18.26) * mm]});
            skFitSpline(sketch, "E1745", {"points": [v(33.1, 18.26) * mm, v(33.02, 17.78) * mm, v(33.08, 16.7) * mm, v(33.23, 15.87) * mm]});
            skFitSpline(sketch, "E1746", {"points": [v(33.23, 15.87) * mm, v(33.45, 14.68) * mm, v(33.41, 14.06) * mm, v(33.06, 13) * mm]});
            skFitSpline(sketch, "E1747", {"points": [v(33.06, 13) * mm, v(32.63, 11.66) * mm, v(32.47, 10.19) * mm, v(32.77, 10.19) * mm]});
            skFitSpline(sketch, "E1748", {"points": [v(32.77, 10.19) * mm, v(32.85, 10.19) * mm, v(33.35, 10.37) * mm, v(33.88, 10.6) * mm]});
            skLineSegment(sketch, "E1749", {"start": v(33.88, 10.6) * mm, "end": v(33.88, 10.6) * mm});
            skFitSpline(sketch, "E1750", {"points": [v(37.45, 21.17) * mm, v(35.86, 22.15) * mm, v(34.24, 23.41) * mm, v(35.44, 22.73) * mm]});
            skFitSpline(sketch, "E1751", {"points": [v(35.44, 22.73) * mm, v(36.09, 22.37) * mm, v(39.2, 20.36) * mm, v(39.35, 20.2) * mm]});
            skFitSpline(sketch, "E1752", {"points": [v(39.35, 20.2) * mm, v(39.7, 19.85) * mm, v(39.1, 20.16) * mm, v(37.45, 21.17) * mm]});
            skFitSpline(sketch, "E1753", {"points": [v(31.67, 22.45) * mm, v(31.36, 23.28) * mm, v(29.48, 26.06) * mm, v(29.34, 25.91) * mm]});
            skFitSpline(sketch, "E1754", {"points": [v(29.34, 25.91) * mm, v(29.26, 25.83) * mm, v(29.45, 25.25) * mm, v(29.78, 24.62) * mm]});
            skFitSpline(sketch, "E1755", {"points": [v(29.78, 24.62) * mm, v(30.71, 22.79) * mm, v(30.44, 22.87) * mm, v(29.43, 24.72) * mm]});
            skFitSpline(sketch, "E1756", {"points": [v(29.43, 24.72) * mm, v(28.93, 25.66) * mm, v(28.07, 27.04) * mm, v(27.53, 27.8) * mm]});
            skFitSpline(sketch, "E1757", {"points": [v(27.53, 27.8) * mm, v(27, 28.55) * mm, v(26.36, 29.43) * mm, v(26.13, 29.76) * mm]});
            skFitSpline(sketch, "E1758", {"points": [v(26.13, 29.76) * mm, v(25.85, 30.14) * mm, v(25.83, 30.27) * mm, v(26.06, 30.12) * mm]});
            skFitSpline(sketch, "E1759", {"points": [v(26.06, 30.12) * mm, v(26.26, 30) * mm, v(27.04, 29.03) * mm, v(27.8, 27.96) * mm]});
            skFitSpline(sketch, "E1760", {"points": [v(27.8, 27.96) * mm, v(28.54, 26.89) * mm, v(29.23, 26.08) * mm, v(29.31, 26.17) * mm]});
            skFitSpline(sketch, "E1761", {"points": [v(29.31, 26.17) * mm, v(29.49, 26.34) * mm, v(31.01, 24.35) * mm, v(31.68, 23.08) * mm]});
            skFitSpline(sketch, "E1762", {"points": [v(31.68, 23.08) * mm, v(31.9, 22.63) * mm, v(32.04, 22.22) * mm, v(31.97, 22.15) * mm]});
            skFitSpline(sketch, "E1763", {"points": [v(31.97, 22.15) * mm, v(31.9, 22.08) * mm, v(31.77, 22.21) * mm, v(31.67, 22.45) * mm]});
            skFitSpline(sketch, "E1764", {"points": [v(17.99, 23.17) * mm, v(17.99, 23.56) * mm, v(18.05, 23.72) * mm, v(18.13, 23.52) * mm]});
            skFitSpline(sketch, "E1765", {"points": [v(18.13, 23.52) * mm, v(18.2, 23.33) * mm, v(18.2, 23.01) * mm, v(18.13, 22.82) * mm]});
            skFitSpline(sketch, "E1766", {"points": [v(18.13, 22.82) * mm, v(18.05, 22.63) * mm, v(17.99, 22.78) * mm, v(17.99, 23.17) * mm]});
            skFitSpline(sketch, "E1767", {"points": [v(34.28, 23.38) * mm, v(33.92, 23.83) * mm, v(33.93, 23.84) * mm, v(34.38, 23.5) * mm]});
            skFitSpline(sketch, "E1768", {"points": [v(34.38, 23.5) * mm, v(34.85, 23.12) * mm, v(35, 22.89) * mm, v(34.77, 22.89) * mm]});
            skFitSpline(sketch, "E1769", {"points": [v(34.77, 22.89) * mm, v(34.71, 22.89) * mm, v(34.49, 23.11) * mm, v(34.28, 23.38) * mm]});
            skFitSpline(sketch, "E1770", {"points": [v(34.03, 24.6) * mm, v(33.18, 25.06) * mm, v(32.1, 25.76) * mm, v(31.63, 26.16) * mm]});
            skLineSegment(sketch, "E1771", {"start": v(31.63, 26.16) * mm, "end": v(30.78, 26.89) * mm});
            skLineSegment(sketch, "E1772", {"start": v(30.78, 26.89) * mm, "end": v(31.63, 26.33) * mm});
            skFitSpline(sketch, "E1773", {"points": [v(31.63, 26.33) * mm, v(32.1, 26.03) * mm, v(33.3, 25.32) * mm, v(34.31, 24.76) * mm]});
            skFitSpline(sketch, "E1774", {"points": [v(34.31, 24.76) * mm, v(35.32, 24.2) * mm, v(36.02, 23.75) * mm, v(35.86, 23.75) * mm]});
            skFitSpline(sketch, "E1775", {"points": [v(35.86, 23.75) * mm, v(35.7, 23.75) * mm, v(34.88, 24.13) * mm, v(34.03, 24.6) * mm]});
            skFitSpline(sketch, "E1776", {"points": [v(18.39, 28.19) * mm, v(18.11, 29.08) * mm, v(17.6, 30.35) * mm, v(17.23, 31.01) * mm]});
            skFitSpline(sketch, "E1777", {"points": [v(17.23, 31.01) * mm, v(16.86, 31.67) * mm, v(16.69, 32.14) * mm, v(16.83, 32.05) * mm]});
            skFitSpline(sketch, "E1778", {"points": [v(16.83, 32.05) * mm, v(17.42, 31.69) * mm, v(19.32, 27) * mm, v(19, 26.69) * mm]});
            skFitSpline(sketch, "E1779", {"points": [v(19, 26.69) * mm, v(18.94, 26.62) * mm, v(18.66, 27.3) * mm, v(18.39, 28.19) * mm]});
            skFitSpline(sketch, "E1780", {"points": [v(31.82, 28.58) * mm, v(31, 28.9) * mm, v(30.37, 29.2) * mm, v(30.42, 29.25) * mm]});
            skFitSpline(sketch, "E1781", {"points": [v(30.42, 29.25) * mm, v(30.48, 29.3) * mm, v(31.34, 29.05) * mm, v(32.35, 28.68) * mm]});
            skFitSpline(sketch, "E1782", {"points": [v(32.35, 28.68) * mm, v(33.35, 28.3) * mm, v(33.98, 28) * mm, v(33.75, 28) * mm]});
            skFitSpline(sketch, "E1783", {"points": [v(33.75, 28) * mm, v(33.51, 28) * mm, v(32.65, 28.26) * mm, v(31.82, 28.58) * mm]});
            skFitSpline(sketch, "E1784", {"points": [v(14.72, 30.68) * mm, v(13.9, 32.24) * mm, v(11.9, 34.53) * mm, v(10.6, 35.38) * mm]});
            skFitSpline(sketch, "E1785", {"points": [v(10.6, 35.38) * mm, v(10.17, 35.66) * mm, v(10.06, 35.85) * mm, v(10.31, 35.86) * mm]});
            skFitSpline(sketch, "E1786", {"points": [v(10.31, 35.86) * mm, v(10.94, 35.88) * mm, v(14.03, 32.53) * mm, v(14.94, 30.84) * mm]});
            skFitSpline(sketch, "E1787", {"points": [v(14.94, 30.84) * mm, v(15.38, 30.02) * mm, v(15.7, 29.3) * mm, v(15.64, 29.24) * mm]});
            skFitSpline(sketch, "E1788", {"points": [v(15.64, 29.24) * mm, v(15.58, 29.18) * mm, v(15.17, 29.83) * mm, v(14.72, 30.68) * mm]});
            skFitSpline(sketch, "E1789", {"points": [v(34.82, 30.42) * mm, v(35.03, 30.5) * mm, v(35.27, 30.5) * mm, v(35.36, 30.4) * mm]});
            skFitSpline(sketch, "E1790", {"points": [v(35.36, 30.4) * mm, v(35.46, 30.3) * mm, v(35.3, 30.24) * mm, v(35, 30.25) * mm]});
            skFitSpline(sketch, "E1791", {"points": [v(35, 30.25) * mm, v(34.66, 30.26) * mm, v(34.6, 30.33) * mm, v(34.82, 30.42) * mm]});
            skFitSpline(sketch, "E1792", {"points": [v(31.51, 31.18) * mm, v(31.58, 31.23) * mm, v(32.33, 31.35) * mm, v(33.18, 31.44) * mm]});
            skFitSpline(sketch, "E1793", {"points": [v(33.18, 31.44) * mm, v(34.18, 31.54) * mm, v(34.48, 31.52) * mm, v(34.03, 31.37) * mm]});
            skFitSpline(sketch, "E1794", {"points": [v(34.03, 31.37) * mm, v(33.33, 31.13) * mm, v(31.29, 30.98) * mm, v(31.51, 31.18) * mm]});
            skFitSpline(sketch, "E1795", {"points": [v(37.27, 36.15) * mm, v(37.56, 36.46) * mm, v(37.85, 36.72) * mm, v(37.93, 36.72) * mm]});
            skFitSpline(sketch, "E1796", {"points": [v(37.93, 36.72) * mm, v(38, 36.72) * mm, v(37.84, 36.46) * mm, v(37.56, 36.15) * mm]});
            skFitSpline(sketch, "E1797", {"points": [v(37.56, 36.15) * mm, v(37.28, 35.84) * mm, v(36.98, 35.59) * mm, v(36.9, 35.59) * mm]});
            skFitSpline(sketch, "E1798", {"points": [v(36.9, 35.59) * mm, v(36.83, 35.59) * mm, v(37, 35.84) * mm, v(37.27, 36.15) * mm]});
            skFitSpline(sketch, "E1799", {"points": [v(-3.22, 11.83) * mm, v(-3.22, 12.65) * mm, v(-6.66, 16.01) * mm, v(-7.17, 15.7) * mm]});
            skFitSpline(sketch, "E1800", {"points": [v(-7.17, 15.7) * mm, v(-7.33, 15.6) * mm, v(-7.46, 15.22) * mm, v(-7.46, 14.84) * mm]});
            skFitSpline(sketch, "E1801", {"points": [v(-7.46, 14.84) * mm, v(-7.46, 14.47) * mm, v(-7.65, 14.06) * mm, v(-7.88, 13.93) * mm]});
            skFitSpline(sketch, "E1802", {"points": [v(-7.88, 13.93) * mm, v(-8.34, 13.67) * mm, v(-8.92, 12.03) * mm, v(-8.65, 11.76) * mm]});
            skFitSpline(sketch, "E1803", {"points": [v(-8.65, 11.76) * mm, v(-8.4, 11.51) * mm, v(-3.22, 11.57) * mm, v(-3.22, 11.83) * mm]});
            skFitSpline(sketch, "E1804", {"points": [v(7.93, 13.37) * mm, v(7.44, 14.34) * mm, v(6.96, 15.42) * mm, v(6.87, 15.77) * mm]});
            skFitSpline(sketch, "E1805", {"points": [v(6.87, 15.77) * mm, v(6.78, 16.12) * mm, v(6.59, 16.4) * mm, v(6.45, 16.4) * mm]});
            skFitSpline(sketch, "E1806", {"points": [v(6.45, 16.4) * mm, v(6, 16.4) * mm, v(2.88, 13.41) * mm, v(2.33, 12.48) * mm]});
            skLineSegment(sketch, "E1807", {"start": v(2.33, 12.48) * mm, "end": v(1.82, 11.6) * mm});
            skLineSegment(sketch, "E1808", {"start": v(1.82, 11.6) * mm, "end": v(5.32, 11.6) * mm});
            skLineSegment(sketch, "E1809", {"start": v(5.32, 11.6) * mm, "end": v(8.82, 11.6) * mm});
            skLineSegment(sketch, "E1810", {"start": v(8.82, 11.6) * mm, "end": v(7.93, 13.37) * mm});
            skFitSpline(sketch, "E1811", {"points": [v(11.49, 13.56) * mm, v(10.93, 14.63) * mm, v(10.43, 15.47) * mm, v(10.37, 15.41) * mm]});
            skFitSpline(sketch, "E1812", {"points": [v(10.37, 15.41) * mm, v(10.23, 15.27) * mm, v(12.1, 11.6) * mm, v(12.31, 11.6) * mm]});
            skFitSpline(sketch, "E1813", {"points": [v(12.31, 11.6) * mm, v(12.42, 11.6) * mm, v(12.04, 12.48) * mm, v(11.49, 13.56) * mm]});
            skFitSpline(sketch, "E1814", {"points": [v(2.42, 13.22) * mm, v(2.96, 13.95) * mm, v(4.13, 15.12) * mm, v(5, 15.83) * mm]});
            skFitSpline(sketch, "E1815", {"points": [v(5, 15.83) * mm, v(5.89, 16.53) * mm, v(6.56, 17.15) * mm, v(6.5, 17.2) * mm]});
            skFitSpline(sketch, "E1816", {"points": [v(6.5, 17.2) * mm, v(6.3, 17.4) * mm, v(3.62, 15.27) * mm, v(3.14, 14.54) * mm]});
            skFitSpline(sketch, "E1817", {"points": [v(3.14, 14.54) * mm, v(2.87, 14.14) * mm, v(2.58, 13.89) * mm, v(2.49, 13.98) * mm]});
            skFitSpline(sketch, "E1818", {"points": [v(2.49, 13.98) * mm, v(2.4, 14.07) * mm, v(2.67, 14.51) * mm, v(3.1, 14.96) * mm]});
            skFitSpline(sketch, "E1819", {"points": [v(3.1, 14.96) * mm, v(3.53, 15.41) * mm, v(3.87, 15.88) * mm, v(3.85, 16) * mm]});
            skFitSpline(sketch, "E1820", {"points": [v(3.85, 16) * mm, v(3.83, 16.12) * mm, v(3.98, 16.25) * mm, v(4.18, 16.28) * mm]});
            skFitSpline(sketch, "E1821", {"points": [v(4.18, 16.28) * mm, v(4.39, 16.3) * mm, v(5.04, 16.66) * mm, v(5.64, 17.07) * mm]});
            skFitSpline(sketch, "E1822", {"points": [v(5.64, 17.07) * mm, v(6.24, 17.48) * mm, v(6.85, 17.8) * mm, v(7, 17.8) * mm]});
            skFitSpline(sketch, "E1823", {"points": [v(7, 17.8) * mm, v(7.13, 17.8) * mm, v(7.16, 17.96) * mm, v(7.05, 18.14) * mm]});
            skFitSpline(sketch, "E1824", {"points": [v(7.05, 18.14) * mm, v(6.92, 18.35) * mm, v(6.97, 18.38) * mm, v(7.22, 18.23) * mm]});
            skFitSpline(sketch, "E1825", {"points": [v(7.22, 18.23) * mm, v(7.5, 18.06) * mm, v(7.47, 17.92) * mm, v(7.07, 17.63) * mm]});
            skFitSpline(sketch, "E1826", {"points": [v(7.07, 17.63) * mm, v(6.45, 17.17) * mm, v(6.74, 17.12) * mm, v(7.53, 17.54) * mm]});
            skFitSpline(sketch, "E1827", {"points": [v(7.53, 17.54) * mm, v(7.86, 17.72) * mm, v(8, 17.97) * mm, v(7.87, 18.18) * mm]});
            skFitSpline(sketch, "E1828", {"points": [v(7.87, 18.18) * mm, v(7.55, 18.69) * mm, v(7.51, 19.25) * mm, v(7.81, 19.06) * mm]});
            skFitSpline(sketch, "E1829", {"points": [v(7.81, 19.06) * mm, v(7.96, 18.97) * mm, v(8, 18.8) * mm, v(7.93, 18.66) * mm]});
            skFitSpline(sketch, "E1830", {"points": [v(7.93, 18.66) * mm, v(7.85, 18.53) * mm, v(7.94, 18.37) * mm, v(8.13, 18.3) * mm]});
            skFitSpline(sketch, "E1831", {"points": [v(8.13, 18.3) * mm, v(8.58, 18.14) * mm, v(9.23, 18.37) * mm, v(9.07, 18.62) * mm]});
            skFitSpline(sketch, "E1832", {"points": [v(9.07, 18.62) * mm, v(9.01, 18.72) * mm, v(9.42, 19.1) * mm, v(10, 19.45) * mm]});
            skLineSegment(sketch, "E1833", {"start": v(10, 19.45) * mm, "end": v(11.03, 20.1) * mm});
            skLineSegment(sketch, "E1834", {"start": v(11.03, 20.1) * mm, "end": v(10.18, 19.33) * mm});
            skFitSpline(sketch, "E1835", {"points": [v(10.18, 19.33) * mm, v(9.5, 18.73) * mm, v(9.48, 18.66) * mm, v(10.03, 19) * mm]});
            skFitSpline(sketch, "E1836", {"points": [v(10.03, 19) * mm, v(10.41, 19.23) * mm, v(10.97, 19.75) * mm, v(11.27, 20.15) * mm]});
            skFitSpline(sketch, "E1837", {"points": [v(11.27, 20.15) * mm, v(11.86, 20.94) * mm, v(11.78, 21.54) * mm, v(10.72, 24.3) * mm]});
            skFitSpline(sketch, "E1838", {"points": [v(10.72, 24.3) * mm, v(10.41, 25.1) * mm, v(10.3, 25.88) * mm, v(10.42, 26.36) * mm]});
            skFitSpline(sketch, "E1839", {"points": [v(10.42, 26.36) * mm, v(10.79, 27.8) * mm, v(13.13, 27.2) * mm, v(14.73, 25.24) * mm]});
            skFitSpline(sketch, "E1840", {"points": [v(14.73, 25.24) * mm, v(15.09, 24.8) * mm, v(15.39, 24.6) * mm, v(15.4, 24.77) * mm]});
            skFitSpline(sketch, "E1841", {"points": [v(15.4, 24.77) * mm, v(15.4, 25.28) * mm, v(13.7, 26.88) * mm, v(12.67, 27.3) * mm]});
            skFitSpline(sketch, "E1842", {"points": [v(12.67, 27.3) * mm, v(9.91, 28.46) * mm, v(9.06, 27.08) * mm, v(10.46, 23.74) * mm]});
            skFitSpline(sketch, "E1843", {"points": [v(10.46, 23.74) * mm, v(10.85, 22.81) * mm, v(11.15, 21.64) * mm, v(11.13, 21.13) * mm]});
            skFitSpline(sketch, "E1844", {"points": [v(11.13, 21.13) * mm, v(11.1, 20.23) * mm, v(11.08, 20.24) * mm, v(10.89, 21.34) * mm]});
            skFitSpline(sketch, "E1845", {"points": [v(10.89, 21.34) * mm, v(10.74, 22.14) * mm, v(10.67, 22.26) * mm, v(10.64, 21.73) * mm]});
            skFitSpline(sketch, "E1846", {"points": [v(10.64, 21.73) * mm, v(10.62, 21.33) * mm, v(10.32, 20.76) * mm, v(9.97, 20.46) * mm]});
            skFitSpline(sketch, "E1847", {"points": [v(9.97, 20.46) * mm, v(9.34, 19.93) * mm, v(9.34, 19.93) * mm, v(9.79, 20.5) * mm]});
            skFitSpline(sketch, "E1848", {"points": [v(9.79, 20.5) * mm, v(10.53, 21.4) * mm, v(10.77, 24.05) * mm, v(10.08, 23.62) * mm]});
            skFitSpline(sketch, "E1849", {"points": [v(10.08, 23.62) * mm, v(9.86, 23.48) * mm, v(9.7, 24.55) * mm, v(9.65, 26.35) * mm]});
            skFitSpline(sketch, "E1850", {"points": [v(9.65, 26.35) * mm, v(9.63, 27.08) * mm, v(9.56, 27.7) * mm, v(9.48, 27.7) * mm]});
            skFitSpline(sketch, "E1851", {"points": [v(9.48, 27.7) * mm, v(9.03, 27.78) * mm, v(8.43, 27.94) * mm, v(8.03, 28.1) * mm]});
            skFitSpline(sketch, "E1852", {"points": [v(8.03, 28.1) * mm, v(7.73, 28.22) * mm, v(7.33, 28) * mm, v(6.83, 27.4) * mm]});
            skFitSpline(sketch, "E1853", {"points": [v(6.83, 27.4) * mm, v(5.83, 26.2) * mm, v(5.82, 24.5) * mm, v(6.8, 23.04) * mm]});
            skFitSpline(sketch, "E1854", {"points": [v(6.8, 23.04) * mm, v(7.2, 22.45) * mm, v(7.5, 21.94) * mm, v(7.44, 21.9) * mm]});
            skFitSpline(sketch, "E1855", {"points": [v(7.44, 21.9) * mm, v(7.4, 21.87) * mm, v(6.93, 21.62) * mm, v(6.42, 21.35) * mm]});
            skFitSpline(sketch, "E1856", {"points": [v(6.42, 21.35) * mm, v(5.9, 21.09) * mm, v(5.54, 20.8) * mm, v(5.61, 20.73) * mm]});
            skFitSpline(sketch, "E1857", {"points": [v(5.61, 20.73) * mm, v(5.78, 20.57) * mm, v(8.06, 21.7) * mm, v(8.06, 21.94) * mm]});
            skFitSpline(sketch, "E1858", {"points": [v(8.06, 21.94) * mm, v(8.06, 22.03) * mm, v(7.75, 22.48) * mm, v(7.36, 22.94) * mm]});
            skFitSpline(sketch, "E1859", {"points": [v(7.36, 22.94) * mm, v(6.97, 23.4) * mm, v(6.66, 24) * mm, v(6.67, 24.25) * mm]});
            skFitSpline(sketch, "E1860", {"points": [v(6.67, 24.25) * mm, v(6.68, 24.56) * mm, v(6.79, 24.48) * mm, v(6.97, 24.02) * mm]});
            skFitSpline(sketch, "E1861", {"points": [v(6.97, 24.02) * mm, v(7.46, 22.8) * mm, v(8.08, 22.28) * mm, v(8.6, 22.67) * mm]});
            skFitSpline(sketch, "E1862", {"points": [v(8.6, 22.67) * mm, v(8.98, 22.95) * mm, v(9, 22.94) * mm, v(8.7, 22.6) * mm]});
            skFitSpline(sketch, "E1863", {"points": [v(8.7, 22.6) * mm, v(8.5, 22.4) * mm, v(8.35, 22.06) * mm, v(8.35, 21.87) * mm]});
            skFitSpline(sketch, "E1864", {"points": [v(8.35, 21.87) * mm, v(8.35, 21.68) * mm, v(8.5, 21.47) * mm, v(8.7, 21.4) * mm]});
            skFitSpline(sketch, "E1865", {"points": [v(8.7, 21.4) * mm, v(8.9, 21.33) * mm, v(8.81, 21.32) * mm, v(8.52, 21.36) * mm]});
            skFitSpline(sketch, "E1866", {"points": [v(8.52, 21.36) * mm, v(7.91, 21.46) * mm, v(6.25, 20.67) * mm, v(4.45, 19.44) * mm]});
            skFitSpline(sketch, "E1867", {"points": [v(4.45, 19.44) * mm, v(3.32, 18.67) * mm, v(3.26, 18.57) * mm, v(3.67, 18.11) * mm]});
            skFitSpline(sketch, "E1868", {"points": [v(3.67, 18.11) * mm, v(3.91, 17.84) * mm, v(4.1, 17.44) * mm, v(4.1, 17.22) * mm]});
            skFitSpline(sketch, "E1869", {"points": [v(4.1, 17.22) * mm, v(4.08, 17) * mm, v(3.98, 17.06) * mm, v(3.85, 17.39) * mm]});
            skFitSpline(sketch, "E1870", {"points": [v(3.85, 17.39) * mm, v(3.73, 17.7) * mm, v(3.4, 17.95) * mm, v(3.1, 17.95) * mm]});
            skFitSpline(sketch, "E1871", {"points": [v(3.1, 17.95) * mm, v(2.77, 17.95) * mm, v(2.6, 18.11) * mm, v(2.66, 18.37) * mm]});
            skFitSpline(sketch, "E1872", {"points": [v(2.66, 18.37) * mm, v(2.7, 18.6) * mm, v(2.66, 18.71) * mm, v(2.56, 18.6) * mm]});
            skFitSpline(sketch, "E1873", {"points": [v(2.56, 18.6) * mm, v(2.46, 18.5) * mm, v(2.4, 18.34) * mm, v(2.42, 18.24) * mm]});
            skFitSpline(sketch, "E1874", {"points": [v(2.42, 18.24) * mm, v(2.44, 18.14) * mm, v(2.15, 17.65) * mm, v(1.77, 17.15) * mm]});
            skFitSpline(sketch, "E1875", {"points": [v(1.77, 17.15) * mm, v(1.15, 16.34) * mm, v(1.12, 16.17) * mm, v(1.46, 15.7) * mm]});
            skFitSpline(sketch, "E1876", {"points": [v(1.46, 15.7) * mm, v(1.9, 15.1) * mm, v(1.98, 14.25) * mm, v(1.61, 14.03) * mm]});
            skFitSpline(sketch, "E1877", {"points": [v(1.61, 14.03) * mm, v(1.48, 13.94) * mm, v(1.42, 14.16) * mm, v(1.48, 14.5) * mm]});
            skFitSpline(sketch, "E1878", {"points": [v(1.48, 14.5) * mm, v(1.54, 14.85) * mm, v(1.45, 15.32) * mm, v(1.3, 15.55) * mm]});
            skFitSpline(sketch, "E1879", {"points": [v(1.3, 15.55) * mm, v(1.03, 15.92) * mm, v(0.96, 15.92) * mm, v(0.64, 15.5) * mm]});
            skFitSpline(sketch, "E1880", {"points": [v(0.64, 15.5) * mm, v(0.4, 15.19) * mm, v(0.03, 15.1) * mm, v(-0.52, 15.2) * mm]});
            skFitSpline(sketch, "E1881", {"points": [v(-0.52, 15.2) * mm, v(-1.27, 15.34) * mm, v(-1.32, 15.3) * mm, v(-1.2, 14.62) * mm]});
            skFitSpline(sketch, "E1882", {"points": [v(-1.2, 14.62) * mm, v(-1.1, 14.19) * mm, v(-1.2, 13.83) * mm, v(-1.4, 13.76) * mm]});
            skFitSpline(sketch, "E1883", {"points": [v(-1.4, 13.76) * mm, v(-1.62, 13.67) * mm, v(-1.7, 13.89) * mm, v(-1.64, 14.42) * mm]});
            skFitSpline(sketch, "E1884", {"points": [v(-1.64, 14.42) * mm, v(-1.52, 15.5) * mm, v(-2.22, 16.1) * mm, v(-2.65, 15.3) * mm]});
            skFitSpline(sketch, "E1885", {"points": [v(-2.65, 15.3) * mm, v(-3.02, 14.59) * mm, v(-2.47, 13.6) * mm, v(-1.39, 13.01) * mm]});
            skFitSpline(sketch, "E1886", {"points": [v(-1.39, 13.01) * mm, v(-0.8, 12.7) * mm, v(-0.56, 12.7) * mm, v(0.1, 13.02) * mm]});
            skFitSpline(sketch, "E1887", {"points": [v(0.1, 13.02) * mm, v(1.3, 13.62) * mm, v(1.48, 13.66) * mm, v(0.88, 13.17) * mm]});
            skFitSpline(sketch, "E1888", {"points": [v(0.88, 13.17) * mm, v(0.35, 12.74) * mm, v(0.35, 12.73) * mm, v(0.92, 12.73) * mm]});
            skFitSpline(sketch, "E1889", {"points": [v(0.92, 12.73) * mm, v(1.24, 12.73) * mm, v(1.72, 13.02) * mm, v(1.99, 13.36) * mm]});
            skFitSpline(sketch, "E1890", {"points": [v(1.99, 13.36) * mm, v(2.46, 14) * mm, v(2.46, 14) * mm, v(2.06, 13.3) * mm]});
            skFitSpline(sketch, "E1891", {"points": [v(2.06, 13.3) * mm, v(1.68, 12.65) * mm, v(1.46, 12.58) * mm, v(-0.62, 12.5) * mm]});
            skLineSegment(sketch, "E1892", {"start": v(-0.62, 12.5) * mm, "end": v(-2.88, 12.43) * mm});
            skLineSegment(sketch, "E1893", {"start": v(-2.88, 12.43) * mm, "end": v(-3.46, 13.35) * mm});
            skFitSpline(sketch, "E1894", {"points": [v(-3.46, 13.35) * mm, v(-4.23, 14.6) * mm, v(-5.89, 16.16) * mm, v(-7.52, 17.18) * mm]});
            skFitSpline(sketch, "E1895", {"points": [v(-7.52, 17.18) * mm, v(-8.25, 17.64) * mm, v(-8.77, 18.1) * mm, v(-8.66, 18.2) * mm]});
            skFitSpline(sketch, "E1896", {"points": [v(-8.66, 18.2) * mm, v(-8.55, 18.32) * mm, v(-8.7, 18.31) * mm, v(-9, 18.2) * mm]});
            skFitSpline(sketch, "E1897", {"points": [v(-9, 18.2) * mm, v(-9.4, 18.05) * mm, v(-9.47, 18.09) * mm, v(-9.3, 18.37) * mm]});
            skFitSpline(sketch, "E1898", {"points": [v(-9.3, 18.37) * mm, v(-9.14, 18.62) * mm, v(-9.17, 18.68) * mm, v(-9.38, 18.55) * mm]});
            skFitSpline(sketch, "E1899", {"points": [v(-9.38, 18.55) * mm, v(-10.1, 18.1) * mm, v(-12.54, 20.06) * mm, v(-12.54, 21.09) * mm]});
            skFitSpline(sketch, "E1900", {"points": [v(-12.54, 21.09) * mm, v(-12.54, 21.43) * mm, v(-12.14, 22.7) * mm, v(-11.66, 23.92) * mm]});
            skFitSpline(sketch, "E1901", {"points": [v(-11.66, 23.92) * mm, v(-10.98, 25.6) * mm, v(-10.84, 26.28) * mm, v(-11.03, 26.83) * mm]});
            skFitSpline(sketch, "E1902", {"points": [v(-11.03, 26.83) * mm, v(-11.54, 28.29) * mm, v(-14.4, 27.64) * mm, v(-16.03, 25.7) * mm]});
            skFitSpline(sketch, "E1903", {"points": [v(-16.03, 25.7) * mm, v(-17.28, 24.21) * mm, v(-16.85, 24.22) * mm, v(-15.41, 25.71) * mm]});
            skFitSpline(sketch, "E1904", {"points": [v(-15.41, 25.71) * mm, v(-14.26, 26.9) * mm, v(-13.9, 27.12) * mm, v(-13, 27.12) * mm]});
            skFitSpline(sketch, "E1905", {"points": [v(-13, 27.12) * mm, v(-11.39, 27.12) * mm, v(-11.14, 26.28) * mm, v(-12.08, 23.93) * mm]});
            skFitSpline(sketch, "E1906", {"points": [v(-12.08, 23.93) * mm, v(-13.42, 20.6) * mm, v(-13.1, 19.85) * mm, v(-9.43, 17.93) * mm]});
            skFitSpline(sketch, "E1907", {"points": [v(-9.43, 17.93) * mm, v(-7.28, 16.8) * mm, v(-4.14, 14.12) * mm, v(-3.3, 12.7) * mm]});
            skFitSpline(sketch, "E1908", {"points": [v(-3.3, 12.7) * mm, v(-2.84, 11.92) * mm, v(-2.73, 11.88) * mm, v(-0.7, 11.88) * mm]});
            skLineSegment(sketch, "E1909", {"start": v(-0.7, 11.88) * mm, "end": v(1.43, 11.88) * mm});
            skLineSegment(sketch, "E1910", {"start": v(1.43, 11.88) * mm, "end": v(2.42, 13.22) * mm});
            skFitSpline(sketch, "E1911", {"points": [v(0.02, 13.86) * mm, v(-0.2, 14.22) * mm, v(0.1, 14.7) * mm, v(0.53, 14.7) * mm]});
            skFitSpline(sketch, "E1912", {"points": [v(0.53, 14.7) * mm, v(0.75, 14.7) * mm, v(0.73, 14.61) * mm, v(0.48, 14.45) * mm]});
            skFitSpline(sketch, "E1913", {"points": [v(0.48, 14.45) * mm, v(0.27, 14.32) * mm, v(0.18, 14.06) * mm, v(0.28, 13.9) * mm]});
            skFitSpline(sketch, "E1914", {"points": [v(0.28, 13.9) * mm, v(0.4, 13.72) * mm, v(0.41, 13.58) * mm, v(0.34, 13.58) * mm]});
            skFitSpline(sketch, "E1915", {"points": [v(0.34, 13.58) * mm, v(0.26, 13.58) * mm, v(0.12, 13.7) * mm, v(0.02, 13.86) * mm]});
            skFitSpline(sketch, "E1916", {"points": [v(2.65, 15.75) * mm, v(2.85, 15.83) * mm, v(3.1, 15.82) * mm, v(3.2, 15.72) * mm]});
            skFitSpline(sketch, "E1917", {"points": [v(3.2, 15.72) * mm, v(3.28, 15.63) * mm, v(3.12, 15.56) * mm, v(2.82, 15.57) * mm]});
            skFitSpline(sketch, "E1918", {"points": [v(2.82, 15.57) * mm, v(2.5, 15.59) * mm, v(2.42, 15.65) * mm, v(2.65, 15.75) * mm]});
            skLineSegment(sketch, "E1919", {"start": v(2.65, 15.75) * mm, "end": v(2.65, 15.75) * mm});
            skFitSpline(sketch, "E1920", {"points": [v(4.73, 18.23) * mm, v(4.74, 18.7) * mm, v(4.8, 18.86) * mm, v(4.87, 18.58) * mm]});
            skFitSpline(sketch, "E1921", {"points": [v(4.87, 18.58) * mm, v(4.95, 18.3) * mm, v(4.94, 17.93) * mm, v(4.86, 17.73) * mm]});
            skFitSpline(sketch, "E1922", {"points": [v(4.86, 17.73) * mm, v(4.79, 17.54) * mm, v(4.73, 17.77) * mm, v(4.73, 18.23) * mm]});
            skFitSpline(sketch, "E1923", {"points": [v(6.32, 19.98) * mm, v(6.52, 20.06) * mm, v(6.77, 20.05) * mm, v(6.86, 19.96) * mm]});
            skFitSpline(sketch, "E1924", {"points": [v(6.86, 19.96) * mm, v(6.95, 19.86) * mm, v(6.79, 19.8) * mm, v(6.49, 19.8) * mm]});
            skFitSpline(sketch, "E1925", {"points": [v(6.49, 19.8) * mm, v(6.16, 19.82) * mm, v(6.1, 19.89) * mm, v(6.32, 19.98) * mm]});
            skFitSpline(sketch, "E1926", {"points": [v(7.45, 20.54) * mm, v(7.65, 20.62) * mm, v(7.9, 20.61) * mm, v(7.99, 20.52) * mm]});
            skFitSpline(sketch, "E1927", {"points": [v(7.99, 20.52) * mm, v(8.08, 20.43) * mm, v(7.92, 20.36) * mm, v(7.62, 20.37) * mm]});
            skFitSpline(sketch, "E1928", {"points": [v(7.62, 20.37) * mm, v(7.29, 20.39) * mm, v(7.22, 20.45) * mm, v(7.45, 20.54) * mm]});
            skLineSegment(sketch, "E1929", {"start": v(7.45, 20.54) * mm, "end": v(7.45, 20.54) * mm});
            skFitSpline(sketch, "E1930", {"points": [v(9.43, 22.14) * mm, v(9.32, 22.65) * mm, v(9.36, 22.84) * mm, v(9.54, 22.66) * mm]});
            skFitSpline(sketch, "E1931", {"points": [v(9.54, 22.66) * mm, v(9.69, 22.5) * mm, v(9.76, 22.15) * mm, v(9.7, 21.86) * mm]});
            skFitSpline(sketch, "E1932", {"points": [v(9.7, 21.86) * mm, v(9.62, 21.47) * mm, v(9.55, 21.54) * mm, v(9.43, 22.14) * mm]});
            skFitSpline(sketch, "E1933", {"points": [v(8.3, 23.37) * mm, v(8.5, 23.45) * mm, v(8.74, 23.44) * mm, v(8.83, 23.34) * mm]});
            skFitSpline(sketch, "E1934", {"points": [v(8.83, 23.34) * mm, v(8.93, 23.25) * mm, v(8.76, 23.18) * mm, v(8.46, 23.2) * mm]});
            skFitSpline(sketch, "E1935", {"points": [v(8.46, 23.2) * mm, v(8.14, 23.2) * mm, v(8.07, 23.27) * mm, v(8.3, 23.37) * mm]});
            skLineSegment(sketch, "E1936", {"start": v(8.3, 23.37) * mm, "end": v(8.3, 23.37) * mm});
            skFitSpline(sketch, "E1937", {"points": [v(8.56, 24.54) * mm, v(8.83, 24.82) * mm, v(9.1, 25.01) * mm, v(9.16, 24.97) * mm]});
            skFitSpline(sketch, "E1938", {"points": [v(9.16, 24.97) * mm, v(9.33, 24.84) * mm, v(8.6, 24.02) * mm, v(8.31, 24.02) * mm]});
            skFitSpline(sketch, "E1939", {"points": [v(8.31, 24.02) * mm, v(8.18, 24.02) * mm, v(8.29, 24.25) * mm, v(8.56, 24.54) * mm]});
            skFitSpline(sketch, "E1940", {"points": [v(6.4, 25.31) * mm, v(6.4, 25.64) * mm, v(6.47, 25.7) * mm, v(6.56, 25.48) * mm]});
            skFitSpline(sketch, "E1941", {"points": [v(6.56, 25.48) * mm, v(6.65, 25.28) * mm, v(6.64, 25.04) * mm, v(6.54, 24.94) * mm]});
            skFitSpline(sketch, "E1942", {"points": [v(6.54, 24.94) * mm, v(6.45, 24.85) * mm, v(6.38, 25.01) * mm, v(6.4, 25.31) * mm]});
            skLineSegment(sketch, "E1943", {"start": v(6.4, 25.31) * mm, "end": v(6.4, 25.31) * mm});
            skFitSpline(sketch, "E1944", {"points": [v(7.79, 25.55) * mm, v(7.97, 25.73) * mm, v(8.16, 25.73) * mm, v(8.34, 25.55) * mm]});
            skFitSpline(sketch, "E1945", {"points": [v(8.34, 25.55) * mm, v(8.53, 25.36) * mm, v(8.43, 25.27) * mm, v(8.06, 25.27) * mm]});
            skFitSpline(sketch, "E1946", {"points": [v(8.06, 25.27) * mm, v(7.7, 25.27) * mm, v(7.6, 25.36) * mm, v(7.79, 25.55) * mm]});
            skFitSpline(sketch, "E1947", {"points": [v(6.68, 26.22) * mm, v(6.65, 26.71) * mm, v(7.5, 27.97) * mm, v(7.86, 27.97) * mm]});
            skFitSpline(sketch, "E1948", {"points": [v(7.86, 27.97) * mm, v(8.03, 27.97) * mm, v(7.9, 27.68) * mm, v(7.59, 27.33) * mm]});
            skFitSpline(sketch, "E1949", {"points": [v(7.59, 27.33) * mm, v(7.27, 26.99) * mm, v(6.94, 26.5) * mm, v(6.85, 26.28) * mm]});
            skFitSpline(sketch, "E1950", {"points": [v(6.85, 26.28) * mm, v(6.75, 26) * mm, v(6.7, 25.98) * mm, v(6.68, 26.22) * mm]});
            skFitSpline(sketch, "E1951", {"points": [v(8.06, 27.12) * mm, v(8.06, 27.28) * mm, v(8.2, 27.4) * mm, v(8.36, 27.4) * mm]});
            skFitSpline(sketch, "E1952", {"points": [v(8.36, 27.4) * mm, v(8.53, 27.4) * mm, v(8.58, 27.28) * mm, v(8.49, 27.12) * mm]});
            skFitSpline(sketch, "E1953", {"points": [v(8.49, 27.12) * mm, v(8.4, 26.97) * mm, v(8.26, 26.84) * mm, v(8.19, 26.84) * mm]});
            skFitSpline(sketch, "E1954", {"points": [v(8.19, 26.84) * mm, v(8.12, 26.84) * mm, v(8.06, 26.97) * mm, v(8.06, 27.12) * mm]});
            skFitSpline(sketch, "E1955", {"points": [v(8.62, 13.54) * mm, v(8.16, 14.45) * mm, v(7.7, 15.6) * mm, v(7.6, 16.08) * mm]});
            skFitSpline(sketch, "E1956", {"points": [v(7.6, 16.08) * mm, v(7.5, 16.57) * mm, v(7.33, 16.96) * mm, v(7.2, 16.96) * mm]});
            skFitSpline(sketch, "E1957", {"points": [v(7.2, 16.96) * mm, v(6.88, 16.96) * mm, v(7.91, 14.03) * mm, v(8.65, 12.84) * mm]});
            skFitSpline(sketch, "E1958", {"points": [v(8.65, 12.84) * mm, v(9.57, 11.35) * mm, v(9.56, 11.7) * mm, v(8.62, 13.54) * mm]});
            skFitSpline(sketch, "E1959", {"points": [v(-11.43, 12.58) * mm, v(-9.9, 13.12) * mm, v(-8.59, 14.06) * mm, v(-8.59, 14.6) * mm]});
            skFitSpline(sketch, "E1960", {"points": [v(-8.59, 14.6) * mm, v(-8.59, 14.93) * mm, v(-8.8, 14.86) * mm, v(-9.42, 14.33) * mm]});
            skFitSpline(sketch, "E1961", {"points": [v(-9.42, 14.33) * mm, v(-10.84, 13.14) * mm, v(-12.58, 12.63) * mm, v(-14.73, 12.8) * mm]});
            skFitSpline(sketch, "E1962", {"points": [v(-14.73, 12.8) * mm, v(-16.48, 12.93) * mm, v(-16.56, 12.9) * mm, v(-15.78, 12.56) * mm]});
            skFitSpline(sketch, "E1963", {"points": [v(-15.78, 12.56) * mm, v(-14.65, 12.07) * mm, v(-12.87, 12.07) * mm, v(-11.43, 12.58) * mm]});
            skFitSpline(sketch, "E1964", {"points": [v(-16.78, 13.28) * mm, v(-16.38, 14.02) * mm, v(-16.4, 14.1) * mm, v(-16.99, 13.96) * mm]});
            skFitSpline(sketch, "E1965", {"points": [v(-16.99, 13.96) * mm, v(-17.3, 13.88) * mm, v(-17.76, 14.13) * mm, v(-18.19, 14.62) * mm]});
            skLineSegment(sketch, "E1966", {"start": v(-18.19, 14.62) * mm, "end": v(-18.89, 15.41) * mm});
            skLineSegment(sketch, "E1967", {"start": v(-18.89, 15.41) * mm, "end": v(-18.16, 14.78) * mm});
            skFitSpline(sketch, "E1968", {"points": [v(-18.16, 14.78) * mm, v(-17.3, 14.01) * mm, v(-17.1, 14) * mm, v(-16.23, 14.67) * mm]});
            skFitSpline(sketch, "E1969", {"points": [v(-16.23, 14.67) * mm, v(-15.86, 14.96) * mm, v(-15.3, 15.15) * mm, v(-14.96, 15.1) * mm]});
            skFitSpline(sketch, "E1970", {"points": [v(-14.96, 15.1) * mm, v(-14.64, 15.04) * mm, v(-14.82, 15.13) * mm, v(-15.36, 15.3) * mm]});
            skFitSpline(sketch, "E1971", {"points": [v(-15.36, 15.3) * mm, v(-15.9, 15.46) * mm, v(-16.74, 15.77) * mm, v(-17.21, 15.97) * mm]});
            skFitSpline(sketch, "E1972", {"points": [v(-17.21, 15.97) * mm, v(-17.82, 16.23) * mm, v(-18.23, 16.25) * mm, v(-18.59, 16.05) * mm]});
            skFitSpline(sketch, "E1973", {"points": [v(-18.59, 16.05) * mm, v(-18.96, 15.85) * mm, v(-19.16, 15.87) * mm, v(-19.33, 16.15) * mm]});
            skFitSpline(sketch, "E1974", {"points": [v(-19.33, 16.15) * mm, v(-19.46, 16.35) * mm, v(-19.66, 16.43) * mm, v(-19.78, 16.3) * mm]});
            skFitSpline(sketch, "E1975", {"points": [v(-19.78, 16.3) * mm, v(-19.9, 16.18) * mm, v(-19.84, 15.99) * mm, v(-19.65, 15.87) * mm]});
            skFitSpline(sketch, "E1976", {"points": [v(-19.65, 15.87) * mm, v(-19.44, 15.74) * mm, v(-19.37, 15.44) * mm, v(-19.5, 15.13) * mm]});
            skFitSpline(sketch, "E1977", {"points": [v(-19.5, 15.13) * mm, v(-19.64, 14.74) * mm, v(-19.41, 14.38) * mm, v(-18.58, 13.67) * mm]});
            skFitSpline(sketch, "E1978", {"points": [v(-18.58, 13.67) * mm, v(-17.29, 12.58) * mm, v(-17.17, 12.55) * mm, v(-16.78, 13.28) * mm]});
            skFitSpline(sketch, "E1979", {"points": [v(-1.96, 13) * mm, v(-2.27, 13.12) * mm, v(-2.7, 13.54) * mm, v(-2.9, 13.93) * mm]});
            skFitSpline(sketch, "E1980", {"points": [v(-2.9, 13.93) * mm, v(-3.22, 14.52) * mm, v(-3.21, 14.76) * mm, v(-2.84, 15.49) * mm]});
            skFitSpline(sketch, "E1981", {"points": [v(-2.84, 15.49) * mm, v(-2.42, 16.3) * mm, v(-2.43, 16.39) * mm, v(-3, 17.12) * mm]});
            skFitSpline(sketch, "E1982", {"points": [v(-3, 17.12) * mm, v(-3.57, 17.83) * mm, v(-3.63, 17.85) * mm, v(-3.82, 17.36) * mm]});
            skFitSpline(sketch, "E1983", {"points": [v(-3.82, 17.36) * mm, v(-4, 16.88) * mm, v(-4.03, 16.88) * mm, v(-4.05, 17.32) * mm]});
            skFitSpline(sketch, "E1984", {"points": [v(-4.05, 17.32) * mm, v(-4.08, 18.14) * mm, v(-4.1, 18.22) * mm, v(-4.42, 18.6) * mm]});
            skFitSpline(sketch, "E1985", {"points": [v(-4.42, 18.6) * mm, v(-4.59, 18.8) * mm, v(-4.9, 18.9) * mm, v(-5.1, 18.82) * mm]});
            skFitSpline(sketch, "E1986", {"points": [v(-5.1, 18.82) * mm, v(-5.3, 18.74) * mm, v(-5.45, 18.82) * mm, v(-5.4, 18.98) * mm]});
            skFitSpline(sketch, "E1987", {"points": [v(-5.4, 18.98) * mm, v(-5.3, 19.47) * mm, v(-9.07, 21.42) * mm, v(-9.84, 21.27) * mm]});
            skFitSpline(sketch, "E1988", {"points": [v(-9.84, 21.27) * mm, v(-10.2, 21.2) * mm, v(-10.57, 21.26) * mm, v(-10.66, 21.41) * mm]});
            skFitSpline(sketch, "E1989", {"points": [v(-10.66, 21.41) * mm, v(-10.76, 21.57) * mm, v(-10.5, 21.62) * mm, v(-10.06, 21.53) * mm]});
            skFitSpline(sketch, "E1990", {"points": [v(-10.06, 21.53) * mm, v(-9.38, 21.4) * mm, v(-9.33, 21.44) * mm, v(-9.67, 21.85) * mm]});
            skFitSpline(sketch, "E1991", {"points": [v(-9.67, 21.85) * mm, v(-9.88, 22.1) * mm, v(-9.99, 22.47) * mm, v(-9.9, 22.67) * mm]});
            skFitSpline(sketch, "E1992", {"points": [v(-9.9, 22.67) * mm, v(-9.82, 22.88) * mm, v(-9.75, 22.81) * mm, v(-9.74, 22.5) * mm]});
            skFitSpline(sketch, "E1993", {"points": [v(-9.74, 22.5) * mm, v(-9.72, 22.08) * mm, v(-9.53, 22.2) * mm, v(-8.87, 23.03) * mm]});
            skFitSpline(sketch, "E1994", {"points": [v(-8.87, 23.03) * mm, v(-8.26, 23.8) * mm, v(-8.02, 24.4) * mm, v(-8.02, 25.19) * mm]});
            skFitSpline(sketch, "E1995", {"points": [v(-8.02, 25.19) * mm, v(-8.02, 25.79) * mm, v(-8.15, 26.28) * mm, v(-8.3, 26.28) * mm]});
            skFitSpline(sketch, "E1996", {"points": [v(-8.3, 26.28) * mm, v(-8.46, 26.28) * mm, v(-8.57, 26.37) * mm, v(-8.55, 26.49) * mm]});
            skFitSpline(sketch, "E1997", {"points": [v(-8.55, 26.49) * mm, v(-8.4, 27.42) * mm, v(-9.36, 28.12) * mm, v(-10.42, 27.85) * mm]});
            skFitSpline(sketch, "E1998", {"points": [v(-10.42, 27.85) * mm, v(-11.02, 27.7) * mm, v(-11.05, 27.62) * mm, v(-10.76, 26.86) * mm]});
            skFitSpline(sketch, "E1999", {"points": [v(-10.76, 26.86) * mm, v(-10.6, 26.4) * mm, v(-10.37, 26.08) * mm, v(-10.27, 26.14) * mm]});
            skFitSpline(sketch, "E2000", {"points": [v(-10.27, 26.14) * mm, v(-10.16, 26.2) * mm, v(-10.15, 25.91) * mm, v(-10.24, 25.5) * mm]});
            skFitSpline(sketch, "E2001", {"points": [v(-10.24, 25.5) * mm, v(-10.36, 24.9) * mm, v(-10.42, 24.84) * mm, v(-10.5, 25.26) * mm]});
            skFitSpline(sketch, "E2002", {"points": [v(-10.5, 25.26) * mm, v(-10.63, 25.84) * mm, v(-12.26, 22.1) * mm, v(-12.26, 21.24) * mm]});
            skFitSpline(sketch, "E2003", {"points": [v(-12.26, 21.24) * mm, v(-12.26, 20.52) * mm, v(-11.49, 19.56) * mm, v(-10.5, 19.05) * mm]});
            skFitSpline(sketch, "E2004", {"points": [v(-10.5, 19.05) * mm, v(-9.8, 18.68) * mm, v(-9.6, 18.67) * mm, v(-9.4, 18.98) * mm]});
            skFitSpline(sketch, "E2005", {"points": [v(-9.4, 18.98) * mm, v(-9.24, 19.24) * mm, v(-9.16, 19.25) * mm, v(-9.16, 19.03) * mm]});
            skFitSpline(sketch, "E2006", {"points": [v(-9.16, 19.03) * mm, v(-9.15, 18.84) * mm, v(-8.89, 18.61) * mm, v(-8.57, 18.5) * mm]});
            skFitSpline(sketch, "E2007", {"points": [v(-8.57, 18.5) * mm, v(-8.24, 18.4) * mm, v(-8.05, 18.25) * mm, v(-8.13, 18.17) * mm]});
            skFitSpline(sketch, "E2008", {"points": [v(-8.13, 18.17) * mm, v(-8.22, 18.08) * mm, v(-7.75, 17.67) * mm, v(-7.1, 17.25) * mm]});
            skFitSpline(sketch, "E2009", {"points": [v(-7.1, 17.25) * mm, v(-5.8, 16.42) * mm, v(-2.94, 13.51) * mm, v(-2.94, 13.03) * mm]});
            skFitSpline(sketch, "E2010", {"points": [v(-2.94, 13.03) * mm, v(-2.94, 12.86) * mm, v(-2.6, 12.74) * mm, v(-2.17, 12.75) * mm]});
            skFitSpline(sketch, "E2011", {"points": [v(-2.17, 12.75) * mm, v(-1.48, 12.76) * mm, v(-1.46, 12.8) * mm, v(-1.96, 13) * mm]});
            skFitSpline(sketch, "E2012", {"points": [v(-5.08, 16) * mm, v(-5.38, 16.24) * mm, v(-5.45, 16.35) * mm, v(-5.25, 16.25) * mm]});
            skFitSpline(sketch, "E2013", {"points": [v(-5.25, 16.25) * mm, v(-5.04, 16.14) * mm, v(-4.53, 15.95) * mm, v(-4.12, 15.83) * mm]});
            skFitSpline(sketch, "E2014", {"points": [v(-4.12, 15.83) * mm, v(-3.51, 15.65) * mm, v(-3.48, 15.6) * mm, v(-3.95, 15.58) * mm]});
            skFitSpline(sketch, "E2015", {"points": [v(-3.95, 15.58) * mm, v(-4.27, 15.56) * mm, v(-4.77, 15.75) * mm, v(-5.08, 16) * mm]});
            skFitSpline(sketch, "E2016", {"points": [v(-5.07, 16.7) * mm, v(-5.17, 16.87) * mm, v(-5.2, 17.06) * mm, v(-5.12, 17.14) * mm]});
            skFitSpline(sketch, "E2017", {"points": [v(-5.12, 17.14) * mm, v(-5.05, 17.2) * mm, v(-4.91, 17.07) * mm, v(-4.82, 16.83) * mm]});
            skFitSpline(sketch, "E2018", {"points": [v(-4.82, 16.83) * mm, v(-4.63, 16.34) * mm, v(-4.8, 16.25) * mm, v(-5.07, 16.7) * mm]});
            skFitSpline(sketch, "E2019", {"points": [v(-7.3, 18.8) * mm, v(-7.6, 19.03) * mm, v(-7.71, 19.22) * mm, v(-7.55, 19.22) * mm]});
            skFitSpline(sketch, "E2020", {"points": [v(-7.55, 19.22) * mm, v(-7.38, 19.22) * mm, v(-7.09, 19.03) * mm, v(-6.9, 18.8) * mm]});
            skFitSpline(sketch, "E2021", {"points": [v(-6.9, 18.8) * mm, v(-6.45, 18.27) * mm, v(-6.6, 18.27) * mm, v(-7.3, 18.8) * mm]});
            skLineSegment(sketch, "E2022", {"start": v(-7.3, 18.8) * mm, "end": v(-7.3, 18.8) * mm});
            skFitSpline(sketch, "E2023", {"points": [v(-7.74, 19.79) * mm, v(-8.4, 20) * mm, v(-8.4, 20.01) * mm, v(-7.83, 20.04) * mm]});
            skFitSpline(sketch, "E2024", {"points": [v(-7.83, 20.04) * mm, v(-7.49, 20.06) * mm, v(-7.13, 19.94) * mm, v(-7.03, 19.79) * mm]});
            skFitSpline(sketch, "E2025", {"points": [v(-7.03, 19.79) * mm, v(-6.94, 19.63) * mm, v(-6.9, 19.52) * mm, v(-6.95, 19.53) * mm]});
            skFitSpline(sketch, "E2026", {"points": [v(-6.95, 19.53) * mm, v(-7, 19.55) * mm, v(-7.35, 19.66) * mm, v(-7.74, 19.79) * mm]});
            skFitSpline(sketch, "E2027", {"points": [v(-11.73, 21.02) * mm, v(-11.95, 21.52) * mm, v(-11.95, 21.84) * mm, v(-11.7, 22.22) * mm]});
            skFitSpline(sketch, "E2028", {"points": [v(-11.7, 22.22) * mm, v(-11.41, 22.7) * mm, v(-11.4, 22.7) * mm, v(-11.55, 22.12) * mm]});
            skFitSpline(sketch, "E2029", {"points": [v(-11.55, 22.12) * mm, v(-11.65, 21.78) * mm, v(-11.58, 21.24) * mm, v(-11.41, 20.93) * mm]});
            skFitSpline(sketch, "E2030", {"points": [v(-11.41, 20.93) * mm, v(-11.25, 20.6) * mm, v(-11.18, 20.35) * mm, v(-11.26, 20.35) * mm]});
            skFitSpline(sketch, "E2031", {"points": [v(-11.26, 20.35) * mm, v(-11.35, 20.35) * mm, v(-11.56, 20.65) * mm, v(-11.73, 21.02) * mm]});
            skFitSpline(sketch, "E2032", {"points": [v(-9.72, 20.65) * mm, v(-10.02, 20.85) * mm, v(-9.91, 20.88) * mm, v(-9.3, 20.74) * mm]});
            skFitSpline(sketch, "E2033", {"points": [v(-9.3, 20.74) * mm, v(-8.25, 20.51) * mm, v(-8.03, 20.35) * mm, v(-8.75, 20.35) * mm]});
            skFitSpline(sketch, "E2034", {"points": [v(-8.75, 20.35) * mm, v(-9.05, 20.36) * mm, v(-9.48, 20.49) * mm, v(-9.72, 20.65) * mm]});
            skFitSpline(sketch, "E2035", {"points": [v(-10.95, 22.47) * mm, v(-10.86, 22.7) * mm, v(-10.65, 22.89) * mm, v(-10.5, 22.89) * mm]});
            skFitSpline(sketch, "E2036", {"points": [v(-10.5, 22.89) * mm, v(-10.33, 22.89) * mm, v(-10.36, 22.71) * mm, v(-10.56, 22.47) * mm]});
            skFitSpline(sketch, "E2037", {"points": [v(-10.56, 22.47) * mm, v(-10.76, 22.23) * mm, v(-10.96, 22.04) * mm, v(-11.01, 22.04) * mm]});
            skFitSpline(sketch, "E2038", {"points": [v(-11.01, 22.04) * mm, v(-11.06, 22.04) * mm, v(-11.04, 22.23) * mm, v(-10.95, 22.47) * mm]});
            skFitSpline(sketch, "E2039", {"points": [v(-10.47, 23.61) * mm, v(-10.56, 23.86) * mm, v(-10.5, 24.2) * mm, v(-10.33, 24.36) * mm]});
            skFitSpline(sketch, "E2040", {"points": [v(-10.33, 24.36) * mm, v(-10.12, 24.58) * mm, v(-10.07, 24.5) * mm, v(-10.18, 24.09) * mm]});
            skFitSpline(sketch, "E2041", {"points": [v(-10.18, 24.09) * mm, v(-10.29, 23.68) * mm, v(-10.18, 23.47) * mm, v(-9.81, 23.37) * mm]});
            skFitSpline(sketch, "E2042", {"points": [v(-9.81, 23.37) * mm, v(-9.33, 23.25) * mm, v(-9.33, 23.24) * mm, v(-9.8, 23.2) * mm]});
            skFitSpline(sketch, "E2043", {"points": [v(-9.8, 23.2) * mm, v(-10.07, 23.19) * mm, v(-10.37, 23.37) * mm, v(-10.47, 23.61) * mm]});
            skFitSpline(sketch, "E2044", {"points": [v(-8.87, 25.08) * mm, v(-8.87, 25.25) * mm, v(-9.1, 25.45) * mm, v(-9.36, 25.52) * mm]});
            skFitSpline(sketch, "E2045", {"points": [v(-9.36, 25.52) * mm, v(-9.8, 25.63) * mm, v(-9.8, 25.65) * mm, v(-9.38, 25.68) * mm]});
            skFitSpline(sketch, "E2046", {"points": [v(-9.38, 25.68) * mm, v(-8.87, 25.71) * mm, v(-8.42, 25.22) * mm, v(-8.7, 24.94) * mm]});
            skFitSpline(sketch, "E2047", {"points": [v(-8.7, 24.94) * mm, v(-8.8, 24.85) * mm, v(-8.87, 24.91) * mm, v(-8.87, 25.08) * mm]});
            skFitSpline(sketch, "E2048", {"points": [v(-9.43, 26.98) * mm, v(-9.64, 27.23) * mm, v(-9.66, 27.4) * mm, v(-9.5, 27.4) * mm]});
            skFitSpline(sketch, "E2049", {"points": [v(-9.5, 27.4) * mm, v(-9.34, 27.4) * mm, v(-9.14, 27.22) * mm, v(-9.05, 26.98) * mm]});
            skFitSpline(sketch, "E2050", {"points": [v(-9.05, 26.98) * mm, v(-8.96, 26.75) * mm, v(-8.93, 26.56) * mm, v(-8.98, 26.56) * mm]});
            skFitSpline(sketch, "E2051", {"points": [v(-8.98, 26.56) * mm, v(-9.04, 26.56) * mm, v(-9.24, 26.75) * mm, v(-9.43, 26.98) * mm]});
            skFitSpline(sketch, "E2052", {"points": [v(-10.26, 27.29) * mm, v(-10.24, 27.62) * mm, v(-10.18, 27.68) * mm, v(-10.09, 27.46) * mm]});
            skFitSpline(sketch, "E2053", {"points": [v(-10.09, 27.46) * mm, v(-10, 27.25) * mm, v(-10.02, 27.01) * mm, v(-10.1, 26.92) * mm]});
            skFitSpline(sketch, "E2054", {"points": [v(-10.1, 26.92) * mm, v(-10.2, 26.82) * mm, v(-10.27, 27) * mm, v(-10.26, 27.29) * mm]});
            skFitSpline(sketch, "E2055", {"points": [v(-12.95, 13.6) * mm, v(-12.65, 14.07) * mm, v(-13.3, 14.61) * mm, v(-13.7, 14.22) * mm]});
            skFitSpline(sketch, "E2056", {"points": [v(-13.7, 14.22) * mm, v(-14.02, 13.9) * mm, v(-13.82, 13.3) * mm, v(-13.38, 13.3) * mm]});
            skFitSpline(sketch, "E2057", {"points": [v(-13.38, 13.3) * mm, v(-13.25, 13.3) * mm, v(-13.05, 13.43) * mm, v(-12.95, 13.6) * mm]});
            skFitSpline(sketch, "E2058", {"points": [v(-13.67, 13.86) * mm, v(-13.67, 14.01) * mm, v(-13.53, 14.14) * mm, v(-13.37, 14.14) * mm]});
            skFitSpline(sketch, "E2059", {"points": [v(-13.37, 14.14) * mm, v(-13.2, 14.14) * mm, v(-13.15, 14.01) * mm, v(-13.24, 13.86) * mm]});
            skFitSpline(sketch, "E2060", {"points": [v(-13.24, 13.86) * mm, v(-13.34, 13.7) * mm, v(-13.47, 13.58) * mm, v(-13.54, 13.58) * mm]});
            skFitSpline(sketch, "E2061", {"points": [v(-13.54, 13.58) * mm, v(-13.61, 13.58) * mm, v(-13.67, 13.7) * mm, v(-13.67, 13.86) * mm]});
            skFitSpline(sketch, "E2062", {"points": [v(10.04, 14.53) * mm, v(10.04, 14.96) * mm, v(9.35, 15.34) * mm, v(9.08, 15.06) * mm]});
            skFitSpline(sketch, "E2063", {"points": [v(9.08, 15.06) * mm, v(8.7, 14.7) * mm, v(8.94, 14.14) * mm, v(9.48, 14.14) * mm]});
            skFitSpline(sketch, "E2064", {"points": [v(9.48, 14.14) * mm, v(9.79, 14.14) * mm, v(10.04, 14.32) * mm, v(10.04, 14.53) * mm]});
            skFitSpline(sketch, "E2065", {"points": [v(9.2, 14.72) * mm, v(9.2, 14.89) * mm, v(9.32, 14.94) * mm, v(9.48, 14.85) * mm]});
            skFitSpline(sketch, "E2066", {"points": [v(9.48, 14.85) * mm, v(9.63, 14.75) * mm, v(9.76, 14.62) * mm, v(9.76, 14.55) * mm]});
            skFitSpline(sketch, "E2067", {"points": [v(9.76, 14.55) * mm, v(9.76, 14.48) * mm, v(9.63, 14.42) * mm, v(9.48, 14.42) * mm]});
            skFitSpline(sketch, "E2068", {"points": [v(9.48, 14.42) * mm, v(9.32, 14.42) * mm, v(9.2, 14.56) * mm, v(9.2, 14.72) * mm]});
            skFitSpline(sketch, "E2069", {"points": [v(-7.74, 14.58) * mm, v(-7.74, 14.66) * mm, v(-7.94, 15.13) * mm, v(-8.2, 15.6) * mm]});
            skFitSpline(sketch, "E2070", {"points": [v(-8.2, 15.6) * mm, v(-8.52, 16.25) * mm, v(-8.7, 16.38) * mm, v(-8.87, 16.1) * mm]});
            skFitSpline(sketch, "E2071", {"points": [v(-8.87, 16.1) * mm, v(-9.01, 15.88) * mm, v(-8.92, 15.48) * mm, v(-8.63, 15.09) * mm]});
            skFitSpline(sketch, "E2072", {"points": [v(-8.63, 15.09) * mm, v(-8.2, 14.48) * mm, v(-7.74, 14.22) * mm, v(-7.74, 14.58) * mm]});
            skFitSpline(sketch, "E2073", {"points": [v(-13.18, 15.16) * mm, v(-13.27, 15.25) * mm, v(-13.52, 15.26) * mm, v(-13.72, 15.18) * mm]});
            skFitSpline(sketch, "E2074", {"points": [v(-13.72, 15.18) * mm, v(-13.94, 15.1) * mm, v(-13.88, 15.02) * mm, v(-13.55, 15.01) * mm]});
            skFitSpline(sketch, "E2075", {"points": [v(-13.55, 15.01) * mm, v(-13.25, 15) * mm, v(-13.08, 15.06) * mm, v(-13.18, 15.16) * mm]});
            skLineSegment(sketch, "E2076", {"start": v(-13.18, 15.16) * mm, "end": v(-13.18, 15.16) * mm});
            skLineSegment(sketch, "E2077", {"start": v(-9.22, 16.07) * mm, "end": v(-9.11, 17.02) * mm});
            skLineSegment(sketch, "E2078", {"start": v(-9.11, 17.02) * mm, "end": v(-9.83, 16.5) * mm});
            skFitSpline(sketch, "E2079", {"points": [v(-9.83, 16.5) * mm, v(-10.55, 15.97) * mm, v(-10.73, 15.53) * mm, v(-10.36, 15.17) * mm]});
            skFitSpline(sketch, "E2080", {"points": [v(-10.36, 15.17) * mm, v(-9.91, 14.71) * mm, v(-9.32, 15.18) * mm, v(-9.22, 16.07) * mm]});
            skFitSpline(sketch, "E2081", {"points": [v(-10.14, 15.55) * mm, v(-10.24, 15.7) * mm, v(-10.12, 15.76) * mm, v(-9.87, 15.66) * mm]});
            skFitSpline(sketch, "E2082", {"points": [v(-9.87, 15.66) * mm, v(-9.38, 15.47) * mm, v(-9.3, 15.27) * mm, v(-9.7, 15.27) * mm]});
            skFitSpline(sketch, "E2083", {"points": [v(-9.7, 15.27) * mm, v(-9.84, 15.27) * mm, v(-10.04, 15.4) * mm, v(-10.14, 15.55) * mm]});
            skFitSpline(sketch, "E2084", {"points": [v(-11.75, 15.71) * mm, v(-11.4, 15.96) * mm, v(-11.2, 16.29) * mm, v(-11.3, 16.45) * mm]});
            skFitSpline(sketch, "E2085", {"points": [v(-11.3, 16.45) * mm, v(-11.41, 16.63) * mm, v(-11.27, 16.67) * mm, v(-10.9, 16.56) * mm]});
            skFitSpline(sketch, "E2086", {"points": [v(-10.9, 16.56) * mm, v(-10.59, 16.46) * mm, v(-10.25, 16.5) * mm, v(-10.15, 16.67) * mm]});
            skFitSpline(sketch, "E2087", {"points": [v(-10.15, 16.67) * mm, v(-10.03, 16.85) * mm, v(-10.34, 16.96) * mm, v(-10.97, 16.96) * mm]});
            skFitSpline(sketch, "E2088", {"points": [v(-10.97, 16.96) * mm, v(-11.94, 16.96) * mm, v(-12.34, 16.57) * mm, v(-11.62, 16.33) * mm]});
            skFitSpline(sketch, "E2089", {"points": [v(-11.62, 16.33) * mm, v(-11.42, 16.26) * mm, v(-11.64, 16) * mm, v(-12.11, 15.75) * mm]});
            skFitSpline(sketch, "E2090", {"points": [v(-12.11, 15.75) * mm, v(-12.58, 15.5) * mm, v(-12.83, 15.29) * mm, v(-12.67, 15.28) * mm]});
            skFitSpline(sketch, "E2091", {"points": [v(-12.67, 15.28) * mm, v(-12.51, 15.28) * mm, v(-12.1, 15.47) * mm, v(-11.75, 15.71) * mm]});
            skFitSpline(sketch, "E2092", {"points": [v(-1.97, 16.7) * mm, v(-3, 18.2) * mm, v(-4.59, 19.55) * mm, v(-6.95, 20.96) * mm]});
            skLineSegment(sketch, "E2093", {"start": v(-6.95, 20.96) * mm, "end": v(-8.84, 22.1) * mm});
            skLineSegment(sketch, "E2094", {"start": v(-8.84, 22.1) * mm, "end": v(-8.28, 22.7) * mm});
            skFitSpline(sketch, "E2095", {"points": [v(-8.28, 22.7) * mm, v(-7.97, 23.03) * mm, v(-7.54, 23.87) * mm, v(-7.33, 24.58) * mm]});
            skFitSpline(sketch, "E2096", {"points": [v(-7.33, 24.58) * mm, v(-7.1, 25.28) * mm, v(-6.92, 25.59) * mm, v(-6.91, 25.27) * mm]});
            skFitSpline(sketch, "E2097", {"points": [v(-6.91, 25.27) * mm, v(-6.9, 24.94) * mm, v(-7.2, 24.09) * mm, v(-7.56, 23.37) * mm]});
            skLineSegment(sketch, "E2098", {"start": v(-7.56, 23.37) * mm, "end": v(-8.22, 22.05) * mm});
            skLineSegment(sketch, "E2099", {"start": v(-8.22, 22.05) * mm, "end": v(-6.2, 20.79) * mm});
            skFitSpline(sketch, "E2100", {"points": [v(-6.2, 20.79) * mm, v(-4.3, 19.61) * mm, v(-2.35, 17.8) * mm, v(-1.15, 16.12) * mm]});
            skLineSegment(sketch, "E2101", {"start": v(-1.15, 16.12) * mm, "end": v(-0.65, 15.41) * mm});
            skLineSegment(sketch, "E2102", {"start": v(-0.65, 15.41) * mm, "end": v(0.1, 16.4) * mm});
            skFitSpline(sketch, "E2103", {"points": [v(0.1, 16.4) * mm, v(1.35, 18.06) * mm, v(3.5, 19.94) * mm, v(5.38, 21.04) * mm]});
            skLineSegment(sketch, "E2104", {"start": v(5.38, 21.04) * mm, "end": v(7.17, 22.09) * mm});
            skLineSegment(sketch, "E2105", {"start": v(7.17, 22.09) * mm, "end": v(6.47, 23.12) * mm});
            skFitSpline(sketch, "E2106", {"points": [v(6.47, 23.12) * mm, v(5.9, 23.94) * mm, v(5.78, 24.44) * mm, v(5.86, 25.5) * mm]});
            skFitSpline(sketch, "E2107", {"points": [v(5.86, 25.5) * mm, v(5.9, 26.24) * mm, v(5.85, 26.84) * mm, v(5.74, 26.84) * mm]});
            skFitSpline(sketch, "E2108", {"points": [v(5.74, 26.84) * mm, v(5.62, 26.84) * mm, v(5.5, 26.24) * mm, v(5.48, 25.5) * mm]});
            skLineSegment(sketch, "E2109", {"start": v(5.48, 25.5) * mm, "end": v(5.44, 24.16) * mm});
            skLineSegment(sketch, "E2110", {"start": v(5.44, 24.16) * mm, "end": v(5.24, 25.29) * mm});
            skLineSegment(sketch, "E2111", {"start": v(5.24, 25.29) * mm, "end": v(5.04, 26.42) * mm});
            skLineSegment(sketch, "E2112", {"start": v(5.04, 26.42) * mm, "end": v(4.96, 25.15) * mm});
            skLineSegment(sketch, "E2113", {"start": v(4.96, 25.15) * mm, "end": v(4.88, 23.88) * mm});
            skLineSegment(sketch, "E2114", {"start": v(4.88, 23.88) * mm, "end": v(4.68, 25) * mm});
            skLineSegment(sketch, "E2115", {"start": v(4.68, 25) * mm, "end": v(4.48, 26.14) * mm});
            skLineSegment(sketch, "E2116", {"start": v(4.48, 26.14) * mm, "end": v(4.39, 24.72) * mm});
            skLineSegment(sketch, "E2117", {"start": v(4.39, 24.72) * mm, "end": v(4.3, 23.31) * mm});
            skLineSegment(sketch, "E2118", {"start": v(4.3, 23.31) * mm, "end": v(4.15, 24.44) * mm});
            skLineSegment(sketch, "E2119", {"start": v(4.15, 24.44) * mm, "end": v(4, 25.57) * mm});
            skLineSegment(sketch, "E2120", {"start": v(4, 25.57) * mm, "end": v(3.84, 24.3) * mm});
            skLineSegment(sketch, "E2121", {"start": v(3.84, 24.3) * mm, "end": v(3.67, 23.03) * mm});
            skLineSegment(sketch, "E2122", {"start": v(3.67, 23.03) * mm, "end": v(3.52, 24.12) * mm});
            skFitSpline(sketch, "E2123", {"points": [v(3.52, 24.12) * mm, v(3.38, 25.19) * mm, v(3.4, 25.23) * mm, v(5.5, 26.92) * mm]});
            skFitSpline(sketch, "E2124", {"points": [v(5.5, 26.92) * mm, v(7.63, 28.62) * mm, v(7.64, 28.64) * mm, v(7.7, 30.05) * mm]});
            skFitSpline(sketch, "E2125", {"points": [v(7.7, 30.05) * mm, v(7.73, 30.83) * mm, v(7.82, 31.75) * mm, v(7.9, 32.1) * mm]});
            skFitSpline(sketch, "E2126", {"points": [v(7.9, 32.1) * mm, v(8.03, 32.6) * mm, v(7.96, 32.69) * mm, v(7.5, 32.57) * mm]});
            skFitSpline(sketch, "E2127", {"points": [v(7.5, 32.57) * mm, v(7.19, 32.49) * mm, v(6.93, 32.21) * mm, v(6.93, 31.96) * mm]});
            skFitSpline(sketch, "E2128", {"points": [v(6.93, 31.96) * mm, v(6.93, 31.6) * mm, v(6.88, 31.58) * mm, v(6.68, 31.88) * mm]});
            skFitSpline(sketch, "E2129", {"points": [v(6.68, 31.88) * mm, v(6.34, 32.42) * mm, v(4.97, 31.5) * mm, v(4.93, 30.69) * mm]});
            skFitSpline(sketch, "E2130", {"points": [v(4.93, 30.69) * mm, v(4.9, 30.21) * mm, v(4.87, 30.19) * mm, v(4.77, 30.58) * mm]});
            skFitSpline(sketch, "E2131", {"points": [v(4.77, 30.58) * mm, v(4.7, 30.85) * mm, v(4.53, 31.07) * mm, v(4.4, 31.07) * mm]});
            skFitSpline(sketch, "E2132", {"points": [v(4.4, 31.07) * mm, v(4.15, 31.07) * mm, v(1.97, 29.65) * mm, v(0.4, 28.45) * mm]});
            skLineSegment(sketch, "E2133", {"start": v(0.4, 28.45) * mm, "end": v(-0.6, 27.69) * mm});
            skLineSegment(sketch, "E2134", {"start": v(-0.6, 27.69) * mm, "end": v(-1.88, 28.67) * mm});
            skFitSpline(sketch, "E2135", {"points": [v(-1.88, 28.67) * mm, v(-4.23, 30.46) * mm, v(-6.43, 31.66) * mm, v(-6.67, 31.28) * mm]});
            skFitSpline(sketch, "E2136", {"points": [v(-6.67, 31.28) * mm, v(-6.82, 31.04) * mm, v(-6.89, 31.08) * mm, v(-6.89, 31.43) * mm]});
            skFitSpline(sketch, "E2137", {"points": [v(-6.89, 31.43) * mm, v(-6.9, 32.04) * mm, v(-6.83, 32.04) * mm, v(-5.54, 31.4) * mm]});
            skFitSpline(sketch, "E2138", {"points": [v(-5.54, 31.4) * mm, v(-4.77, 31) * mm, v(-4.31, 30.93) * mm, v(-3.8, 31.12) * mm]});
            skFitSpline(sketch, "E2139", {"points": [v(-3.8, 31.12) * mm, v(-3.24, 31.33) * mm, v(-3.02, 31.25) * mm, v(-2.54, 30.69) * mm]});
            skFitSpline(sketch, "E2140", {"points": [v(-2.54, 30.69) * mm, v(-2.22, 30.31) * mm, v(-1.76, 29.94) * mm, v(-1.53, 29.85) * mm]});
            skFitSpline(sketch, "E2141", {"points": [v(-1.53, 29.85) * mm, v(-1.19, 29.74) * mm, v(-1.2, 29.7) * mm, v(-1.58, 29.69) * mm]});
            skFitSpline(sketch, "E2142", {"points": [v(-1.58, 29.69) * mm, v(-1.84, 29.67) * mm, v(-2.3, 29.97) * mm, v(-2.6, 30.35) * mm]});
            skFitSpline(sketch, "E2143", {"points": [v(-2.6, 30.35) * mm, v(-2.98, 30.84) * mm, v(-3.32, 31) * mm, v(-3.74, 30.89) * mm]});
            skFitSpline(sketch, "E2144", {"points": [v(-3.74, 30.89) * mm, v(-4.26, 30.75) * mm, v(-4.08, 30.54) * mm, v(-2.45, 29.38) * mm]});
            skFitSpline(sketch, "E2145", {"points": [v(-2.45, 29.38) * mm, v(-0.6, 28.07) * mm, v(-0.53, 28.05) * mm, v(0.02, 28.53) * mm]});
            skFitSpline(sketch, "E2146", {"points": [v(0.02, 28.53) * mm, v(0.33, 28.8) * mm, v(1.14, 29.39) * mm, v(1.81, 29.82) * mm]});
            skFitSpline(sketch, "E2147", {"points": [v(1.81, 29.82) * mm, v(2.85, 30.5) * mm, v(2.96, 30.65) * mm, v(2.52, 30.82) * mm]});
            skFitSpline(sketch, "E2148", {"points": [v(2.52, 30.82) * mm, v(2.16, 30.95) * mm, v(1.75, 30.78) * mm, v(1.22, 30.28) * mm]});
            skFitSpline(sketch, "E2149", {"points": [v(1.22, 30.28) * mm, v(0.62, 29.72) * mm, v(0.37, 29.63) * mm, v(0.1, 29.9) * mm]});
            skFitSpline(sketch, "E2150", {"points": [v(0.1, 29.9) * mm, v(-0.16, 30.15) * mm, v(-0.15, 30.3) * mm, v(0.12, 30.58) * mm]});
            skFitSpline(sketch, "E2151", {"points": [v(0.12, 30.58) * mm, v(0.4, 30.86) * mm, v(0.44, 30.84) * mm, v(0.3, 30.44) * mm]});
            skFitSpline(sketch, "E2152", {"points": [v(0.3, 30.44) * mm, v(0.03, 29.75) * mm, v(0.52, 29.82) * mm, v(1.2, 30.58) * mm]});
            skFitSpline(sketch, "E2153", {"points": [v(1.2, 30.58) * mm, v(1.78, 31.23) * mm, v(2.24, 32.2) * mm, v(1.97, 32.2) * mm]});
            skFitSpline(sketch, "E2154", {"points": [v(1.97, 32.2) * mm, v(1.88, 32.2) * mm, v(1.27, 31.83) * mm, v(0.61, 31.38) * mm]});
            skLineSegment(sketch, "E2155", {"start": v(0.61, 31.38) * mm, "end": v(-0.6, 30.55) * mm});
            skLineSegment(sketch, "E2156", {"start": v(-0.6, 30.55) * mm, "end": v(-1.84, 31.37) * mm});
            skFitSpline(sketch, "E2157", {"points": [v(-1.84, 31.37) * mm, v(-3.07, 32.2) * mm, v(-3.68, 32.42) * mm, v(-3.4, 31.97) * mm]});
            skFitSpline(sketch, "E2158", {"points": [v(-3.4, 31.97) * mm, v(-3.31, 31.84) * mm, v(-3.43, 31.73) * mm, v(-3.65, 31.73) * mm]});
            skFitSpline(sketch, "E2159", {"points": [v(-3.65, 31.73) * mm, v(-3.87, 31.73) * mm, v(-3.98, 31.84) * mm, v(-3.9, 31.97) * mm]});
            skFitSpline(sketch, "E2160", {"points": [v(-3.9, 31.97) * mm, v(-3.82, 32.1) * mm, v(-4.2, 32.2) * mm, v(-4.75, 32.2) * mm]});
            skFitSpline(sketch, "E2161", {"points": [v(-4.75, 32.2) * mm, v(-5.52, 32.2) * mm, v(-5.7, 32.3) * mm, v(-5.58, 32.62) * mm]});
            skFitSpline(sketch, "E2162", {"points": [v(-5.58, 32.62) * mm, v(-5.48, 32.9) * mm, v(-5.66, 33.14) * mm, v(-6.09, 33.31) * mm]});
            skFitSpline(sketch, "E2163", {"points": [v(-6.09, 33.31) * mm, v(-6.45, 33.46) * mm, v(-6.56, 33.59) * mm, v(-6.33, 33.6) * mm]});
            skFitSpline(sketch, "E2164", {"points": [v(-6.33, 33.6) * mm, v(-6.1, 33.6) * mm, v(-6.32, 33.87) * mm, v(-6.83, 34.18) * mm]});
            skFitSpline(sketch, "E2165", {"points": [v(-6.83, 34.18) * mm, v(-7.97, 34.87) * mm, v(-8.02, 34.88) * mm, v(-8.02, 34.2) * mm]});
            skFitSpline(sketch, "E2166", {"points": [v(-8.02, 34.2) * mm, v(-8.02, 33.5) * mm, v(-8.54, 33.17) * mm, v(-8.96, 33.6) * mm]});
            skFitSpline(sketch, "E2167", {"points": [v(-8.96, 33.6) * mm, v(-9.21, 33.85) * mm, v(-9.17, 33.89) * mm, v(-8.8, 33.74) * mm]});
            skFitSpline(sketch, "E2168", {"points": [v(-8.8, 33.74) * mm, v(-8.42, 33.6) * mm, v(-8.3, 33.7) * mm, v(-8.3, 34.15) * mm]});
            skFitSpline(sketch, "E2169", {"points": [v(-8.3, 34.15) * mm, v(-8.3, 34.48) * mm, v(-8.45, 34.74) * mm, v(-8.63, 34.74) * mm]});
            skFitSpline(sketch, "E2170", {"points": [v(-8.63, 34.74) * mm, v(-8.81, 34.74) * mm, v(-8.88, 34.83) * mm, v(-8.78, 34.93) * mm]});
            skFitSpline(sketch, "E2171", {"points": [v(-8.78, 34.93) * mm, v(-8.61, 35.1) * mm, v(-10.3, 36.44) * mm, v(-10.67, 36.44) * mm]});
            skFitSpline(sketch, "E2172", {"points": [v(-10.67, 36.44) * mm, v(-10.75, 36.44) * mm, v(-10.47, 35.7) * mm, v(-10.05, 34.78) * mm]});
            skFitSpline(sketch, "E2173", {"points": [v(-10.05, 34.78) * mm, v(-9.44, 33.45) * mm, v(-9.1, 33.05) * mm, v(-8.3, 32.73) * mm]});
            skFitSpline(sketch, "E2174", {"points": [v(-8.3, 32.73) * mm, v(-7.76, 32.52) * mm, v(-7.19, 32.3) * mm, v(-7.03, 32.23) * mm]});
            skFitSpline(sketch, "E2175", {"points": [v(-7.03, 32.23) * mm, v(-6.88, 32.17) * mm, v(-7, 32.42) * mm, v(-7.32, 32.78) * mm]});
            skLineSegment(sketch, "E2176", {"start": v(-7.32, 32.78) * mm, "end": v(-7.88, 33.43) * mm});
            skLineSegment(sketch, "E2177", {"start": v(-7.88, 33.43) * mm, "end": v(-7.14, 32.9) * mm});
            skFitSpline(sketch, "E2178", {"points": [v(-7.14, 32.9) * mm, v(-6.57, 32.47) * mm, v(-6.48, 32.29) * mm, v(-6.77, 32.07) * mm]});
            skFitSpline(sketch, "E2179", {"points": [v(-6.77, 32.07) * mm, v(-6.97, 31.9) * mm, v(-7.2, 31.46) * mm, v(-7.26, 31.07) * mm]});
            skFitSpline(sketch, "E2180", {"points": [v(-7.26, 31.07) * mm, v(-7.36, 30.47) * mm, v(-7.39, 30.5) * mm, v(-7.42, 31.25) * mm]});
            skFitSpline(sketch, "E2181", {"points": [v(-7.42, 31.25) * mm, v(-7.45, 31.88) * mm, v(-7.62, 32.18) * mm, v(-8.02, 32.29) * mm]});
            skFitSpline(sketch, "E2182", {"points": [v(-8.02, 32.29) * mm, v(-8.34, 32.37) * mm, v(-8.6, 32.3) * mm, v(-8.6, 32.1) * mm]});
            skFitSpline(sketch, "E2183", {"points": [v(-8.6, 32.1) * mm, v(-8.62, 31.93) * mm, v(-8.72, 32.01) * mm, v(-8.83, 32.3) * mm]});
            skFitSpline(sketch, "E2184", {"points": [v(-8.83, 32.3) * mm, v(-8.94, 32.59) * mm, v(-9.01, 31.72) * mm, v(-8.98, 30.38) * mm]});
            skFitSpline(sketch, "E2185", {"points": [v(-8.98, 30.38) * mm, v(-8.94, 28.52) * mm, v(-8.8, 27.8) * mm, v(-8.44, 27.4) * mm]});
            skFitSpline(sketch, "E2186", {"points": [v(-8.44, 27.4) * mm, v(-7.73, 26.62) * mm, v(-7.58, 24.59) * mm, v(-8.14, 23.5) * mm]});
            skFitSpline(sketch, "E2187", {"points": [v(-8.14, 23.5) * mm, v(-8.4, 23) * mm, v(-8.71, 22.6) * mm, v(-8.85, 22.6) * mm]});
            skFitSpline(sketch, "E2188", {"points": [v(-8.85, 22.6) * mm, v(-8.98, 22.6) * mm, v(-9.16, 22.42) * mm, v(-9.25, 22.18) * mm]});
            skFitSpline(sketch, "E2189", {"points": [v(-9.25, 22.18) * mm, v(-9.37, 21.88) * mm, v(-8.88, 21.5) * mm, v(-7.5, 20.8) * mm]});
            skFitSpline(sketch, "E2190", {"points": [v(-7.5, 20.8) * mm, v(-5.25, 19.66) * mm, v(-3.7, 18.45) * mm, v(-3.97, 18.02) * mm]});
            skFitSpline(sketch, "E2191", {"points": [v(-3.97, 18.02) * mm, v(-4.08, 17.85) * mm, v(-4.03, 17.8) * mm, v(-3.86, 17.9) * mm]});
            skFitSpline(sketch, "E2192", {"points": [v(-3.86, 17.9) * mm, v(-3.55, 18.1) * mm, v(-1.53, 15.97) * mm, v(-1.53, 15.45) * mm]});
            skFitSpline(sketch, "E2193", {"points": [v(-1.53, 15.45) * mm, v(-1.53, 15.3) * mm, v(-1.45, 15.26) * mm, v(-1.35, 15.36) * mm]});
            skFitSpline(sketch, "E2194", {"points": [v(-1.35, 15.36) * mm, v(-1.25, 15.46) * mm, v(-1.53, 16.06) * mm, v(-1.97, 16.7) * mm]});
            skFitSpline(sketch, "E2195", {"points": [v(-1.25, 20.87) * mm, v(-1.26, 21.27) * mm, v(-1.3, 21.28) * mm, v(-1.53, 20.91) * mm]});
            skFitSpline(sketch, "E2196", {"points": [v(-1.53, 20.91) * mm, v(-1.75, 20.58) * mm, v(-1.8, 20.64) * mm, v(-1.8, 21.2) * mm]});
            skFitSpline(sketch, "E2197", {"points": [v(-1.8, 21.2) * mm, v(-1.81, 22) * mm, v(-3.4, 24.11) * mm, v(-3.81, 23.86) * mm]});
            skFitSpline(sketch, "E2198", {"points": [v(-3.81, 23.86) * mm, v(-3.95, 23.78) * mm, v(-4.07, 23.9) * mm, v(-4.07, 24.14) * mm]});
            skFitSpline(sketch, "E2199", {"points": [v(-4.07, 24.14) * mm, v(-4.07, 24.39) * mm, v(-4.2, 24.58) * mm, v(-4.37, 24.58) * mm]});
            skFitSpline(sketch, "E2200", {"points": [v(-4.37, 24.58) * mm, v(-4.54, 24.58) * mm, v(-4.6, 24.8) * mm, v(-4.51, 25.09) * mm]});
            skFitSpline(sketch, "E2201", {"points": [v(-4.51, 25.09) * mm, v(-4.42, 25.37) * mm, v(-4.64, 26) * mm, v(-5.03, 26.57) * mm]});
            skLineSegment(sketch, "E2202", {"start": v(-5.03, 26.57) * mm, "end": v(-5.7, 27.55) * mm});
            skLineSegment(sketch, "E2203", {"start": v(-5.7, 27.55) * mm, "end": v(-4.95, 28.6) * mm});
            skFitSpline(sketch, "E2204", {"points": [v(-4.95, 28.6) * mm, v(-4.55, 29.18) * mm, v(-4.13, 29.65) * mm, v(-4.04, 29.66) * mm]});
            skFitSpline(sketch, "E2205", {"points": [v(-4.04, 29.66) * mm, v(-3.94, 29.66) * mm, v(-3.52, 29.15) * mm, v(-3.1, 28.51) * mm]});
            skFitSpline(sketch, "E2206", {"points": [v(-3.1, 28.51) * mm, v(-2.5, 27.6) * mm, v(-2.41, 27.28) * mm, v(-2.67, 26.96) * mm]});
            skFitSpline(sketch, "E2207", {"points": [v(-2.67, 26.96) * mm, v(-2.86, 26.74) * mm, v(-3.12, 26.63) * mm, v(-3.25, 26.72) * mm]});
            skFitSpline(sketch, "E2208", {"points": [v(-3.25, 26.72) * mm, v(-3.39, 26.8) * mm, v(-3.43, 26.7) * mm, v(-3.35, 26.49) * mm]});
            skFitSpline(sketch, "E2209", {"points": [v(-3.35, 26.49) * mm, v(-3.27, 26.27) * mm, v(-3.46, 25.87) * mm, v(-3.78, 25.58) * mm]});
            skFitSpline(sketch, "E2210", {"points": [v(-3.78, 25.58) * mm, v(-4.35, 25.06) * mm, v(-4.35, 25.06) * mm, v(-3, 23.62) * mm]});
            skFitSpline(sketch, "E2211", {"points": [v(-3, 23.62) * mm, v(-2.25, 22.83) * mm, v(-1.4, 21.84) * mm, v(-1.13, 21.4) * mm]});
            skLineSegment(sketch, "E2212", {"start": v(-1.13, 21.4) * mm, "end": v(-0.62, 20.63) * mm});
            skLineSegment(sketch, "E2213", {"start": v(-0.62, 20.63) * mm, "end": v(0.18, 21.73) * mm});
            skFitSpline(sketch, "E2214", {"points": [v(0.18, 21.73) * mm, v(1.25, 23.22) * mm, v(1.58, 23.38) * mm, v(1.55, 22.41) * mm]});
            skFitSpline(sketch, "E2215", {"points": [v(1.55, 22.41) * mm, v(1.54, 21.72) * mm, v(1.5, 21.69) * mm, v(1.3, 22.18) * mm]});
            skFitSpline(sketch, "E2216", {"points": [v(1.3, 22.18) * mm, v(1.07, 22.7) * mm, v(1.05, 22.7) * mm, v(1, 22.04) * mm]});
            skFitSpline(sketch, "E2217", {"points": [v(1, 22.04) * mm, v(0.98, 21.66) * mm, v(0.9, 21.5) * mm, v(0.81, 21.72) * mm]});
            skFitSpline(sketch, "E2218", {"points": [v(0.81, 21.72) * mm, v(0.7, 21.98) * mm, v(0.5, 21.86) * mm, v(0.15, 21.31) * mm]});
            skFitSpline(sketch, "E2219", {"points": [v(0.15, 21.31) * mm, v(-0.44, 20.42) * mm, v(-1.25, 20.16) * mm, v(-1.25, 20.87) * mm]});
            skFitSpline(sketch, "E2220", {"points": [v(-3.79, 26.45) * mm, v(-3.79, 27.01) * mm, v(-3.68, 27.14) * mm, v(-3.33, 27) * mm]});
            skFitSpline(sketch, "E2221", {"points": [v(-3.33, 27) * mm, v(-2.97, 26.87) * mm, v(-2.9, 26.96) * mm, v(-3.05, 27.47) * mm]});
            skFitSpline(sketch, "E2222", {"points": [v(-3.05, 27.47) * mm, v(-3.14, 27.82) * mm, v(-3.22, 28.24) * mm, v(-3.22, 28.4) * mm]});
            skFitSpline(sketch, "E2223", {"points": [v(-3.22, 28.4) * mm, v(-3.23, 28.55) * mm, v(-3.36, 28.49) * mm, v(-3.5, 28.25) * mm]});
            skFitSpline(sketch, "E2224", {"points": [v(-3.5, 28.25) * mm, v(-3.72, 27.93) * mm, v(-3.78, 28.02) * mm, v(-3.78, 28.65) * mm]});
            skFitSpline(sketch, "E2225", {"points": [v(-3.78, 28.65) * mm, v(-3.79, 29.45) * mm, v(-3.8, 29.46) * mm, v(-4.35, 28.96) * mm]});
            skFitSpline(sketch, "E2226", {"points": [v(-4.35, 28.96) * mm, v(-4.66, 28.68) * mm, v(-4.92, 28.28) * mm, v(-4.92, 28.07) * mm]});
            skFitSpline(sketch, "E2227", {"points": [v(-4.92, 28.07) * mm, v(-4.92, 27.86) * mm, v(-5.08, 27.68) * mm, v(-5.27, 27.67) * mm]});
            skFitSpline(sketch, "E2228", {"points": [v(-5.27, 27.67) * mm, v(-5.46, 27.66) * mm, v(-5.34, 27.51) * mm, v(-4.99, 27.34) * mm]});
            skFitSpline(sketch, "E2229", {"points": [v(-4.99, 27.34) * mm, v(-4.6, 27.15) * mm, v(-4.35, 26.78) * mm, v(-4.35, 26.37) * mm]});
            skFitSpline(sketch, "E2230", {"points": [v(-4.35, 26.37) * mm, v(-4.35, 26.01) * mm, v(-4.23, 25.71) * mm, v(-4.07, 25.71) * mm]});
            skFitSpline(sketch, "E2231", {"points": [v(-4.07, 25.71) * mm, v(-3.92, 25.71) * mm, v(-3.79, 26.04) * mm, v(-3.79, 26.45) * mm]});
            skFitSpline(sketch, "E2232", {"points": [v(-4.64, 28.24) * mm, v(-4.64, 28.38) * mm, v(-4.5, 28.58) * mm, v(-4.36, 28.67) * mm]});
            skFitSpline(sketch, "E2233", {"points": [v(-4.36, 28.67) * mm, v(-4.2, 28.77) * mm, v(-4.15, 28.66) * mm, v(-4.25, 28.4) * mm]});
            skFitSpline(sketch, "E2234", {"points": [v(-4.25, 28.4) * mm, v(-4.43, 27.92) * mm, v(-4.64, 27.83) * mm, v(-4.64, 28.24) * mm]});
            skFitSpline(sketch, "E2235", {"points": [v(1.8, 22.75) * mm, v(1.62, 23.63) * mm, v(1.87, 24.14) * mm, v(2.75, 24.6) * mm]});
            skFitSpline(sketch, "E2236", {"points": [v(2.75, 24.6) * mm, v(3.21, 24.86) * mm, v(3.26, 24.77) * mm, v(3.23, 23.82) * mm]});
            skFitSpline(sketch, "E2237", {"points": [v(3.23, 23.82) * mm, v(3.2, 22.76) * mm, v(3.2, 22.76) * mm, v(2.98, 23.6) * mm]});
            skLineSegment(sketch, "E2238", {"start": v(2.98, 23.6) * mm, "end": v(2.77, 24.44) * mm});
            skLineSegment(sketch, "E2239", {"start": v(2.77, 24.44) * mm, "end": v(2.7, 23.45) * mm});
            skFitSpline(sketch, "E2240", {"points": [v(2.7, 23.45) * mm, v(2.65, 22.54) * mm, v(2.63, 22.52) * mm, v(2.43, 23.17) * mm]});
            skFitSpline(sketch, "E2241", {"points": [v(2.43, 23.17) * mm, v(2.23, 23.84) * mm, v(2.21, 23.82) * mm, v(2.1, 22.89) * mm]});
            skLineSegment(sketch, "E2242", {"start": v(2.1, 22.89) * mm, "end": v(2, 21.9) * mm});
            skLineSegment(sketch, "E2243", {"start": v(2, 21.9) * mm, "end": v(1.8, 22.75) * mm});
            skFitSpline(sketch, "E2244", {"points": [v(-5.67, 25.55) * mm, v(-6.97, 26.8) * mm, v(-7.17, 26.9) * mm, v(-7.2, 26.36) * mm]});
            skFitSpline(sketch, "E2245", {"points": [v(-7.2, 26.36) * mm, v(-7.2, 26) * mm, v(-7.29, 26.05) * mm, v(-7.5, 26.56) * mm]});
            skFitSpline(sketch, "E2246", {"points": [v(-7.5, 26.56) * mm, v(-7.65, 26.95) * mm, v(-8.05, 27.57) * mm, v(-8.4, 27.95) * mm]});
            skFitSpline(sketch, "E2247", {"points": [v(-8.4, 27.95) * mm, v(-8.73, 28.33) * mm, v(-8.12, 27.96) * mm, v(-7.03, 27.13) * mm]});
            skFitSpline(sketch, "E2248", {"points": [v(-7.03, 27.13) * mm, v(-4.47, 25.16) * mm, v(-4.55, 25.23) * mm, v(-4.82, 25.1) * mm]});
            skFitSpline(sketch, "E2249", {"points": [v(-4.82, 25.1) * mm, v(-4.95, 25.02) * mm, v(-5.33, 25.23) * mm, v(-5.67, 25.55) * mm]});
            skFitSpline(sketch, "E2250", {"points": [v(2.21, 26) * mm, v(1.32, 27.1) * mm, v(1.22, 27.49) * mm, v(1.68, 28.11) * mm]});
            skFitSpline(sketch, "E2251", {"points": [v(1.68, 28.11) * mm, v(2.06, 28.63) * mm, v(2.08, 28.62) * mm, v(1.94, 27.9) * mm]});
            skFitSpline(sketch, "E2252", {"points": [v(1.94, 27.9) * mm, v(1.85, 27.44) * mm, v(1.91, 27.12) * mm, v(2.1, 27.12) * mm]});
            skFitSpline(sketch, "E2253", {"points": [v(2.1, 27.12) * mm, v(2.26, 27.12) * mm, v(2.34, 26.96) * mm, v(2.26, 26.76) * mm]});
            skFitSpline(sketch, "E2254", {"points": [v(2.26, 26.76) * mm, v(2.17, 26.51) * mm, v(2.37, 26.39) * mm, v(2.84, 26.39) * mm]});
            skFitSpline(sketch, "E2255", {"points": [v(2.84, 26.39) * mm, v(3.33, 26.39) * mm, v(3.52, 26.51) * mm, v(3.42, 26.77) * mm]});
            skFitSpline(sketch, "E2256", {"points": [v(3.42, 26.77) * mm, v(3.33, 27) * mm, v(3.4, 27.07) * mm, v(3.57, 26.97) * mm]});
            skFitSpline(sketch, "E2257", {"points": [v(3.57, 26.97) * mm, v(3.77, 26.85) * mm, v(3.84, 27.07) * mm, v(3.78, 27.59) * mm]});
            skFitSpline(sketch, "E2258", {"points": [v(3.78, 27.59) * mm, v(3.73, 28.06) * mm, v(3.54, 28.36) * mm, v(3.32, 28.32) * mm]});
            skFitSpline(sketch, "E2259", {"points": [v(3.32, 28.32) * mm, v(3.12, 28.28) * mm, v(3, 28.4) * mm, v(3.04, 28.6) * mm]});
            skFitSpline(sketch, "E2260", {"points": [v(3.04, 28.6) * mm, v(3.09, 28.8) * mm, v(3, 28.96) * mm, v(2.84, 28.96) * mm]});
            skFitSpline(sketch, "E2261", {"points": [v(2.84, 28.96) * mm, v(2.69, 28.96) * mm, v(2.6, 28.85) * mm, v(2.64, 28.73) * mm]});
            skFitSpline(sketch, "E2262", {"points": [v(2.64, 28.73) * mm, v(2.68, 28.6) * mm, v(2.6, 28.57) * mm, v(2.44, 28.66) * mm]});
            skFitSpline(sketch, "E2263", {"points": [v(2.44, 28.66) * mm, v(2.14, 28.85) * mm, v(2.35, 29.66) * mm, v(2.7, 29.66) * mm]});
            skFitSpline(sketch, "E2264", {"points": [v(2.7, 29.66) * mm, v(2.82, 29.66) * mm, v(3.27, 29.2) * mm, v(3.7, 28.65) * mm]});
            skFitSpline(sketch, "E2265", {"points": [v(3.7, 28.65) * mm, v(4.52, 27.57) * mm, v(4.48, 27.26) * mm, v(3.32, 25.81) * mm]});
            skLineSegment(sketch, "E2266", {"start": v(3.32, 25.81) * mm, "end": v(2.84, 25.2) * mm});
            skLineSegment(sketch, "E2267", {"start": v(2.84, 25.2) * mm, "end": v(2.21, 26) * mm});
            skFitSpline(sketch, "E2268", {"points": [v(3.1, 25.95) * mm, v(3.18, 26.08) * mm, v(3.06, 26.18) * mm, v(2.84, 26.18) * mm]});
            skFitSpline(sketch, "E2269", {"points": [v(2.84, 26.18) * mm, v(2.62, 26.18) * mm, v(2.51, 26.08) * mm, v(2.6, 25.95) * mm]});
            skFitSpline(sketch, "E2270", {"points": [v(2.6, 25.95) * mm, v(2.67, 25.82) * mm, v(2.78, 25.71) * mm, v(2.84, 25.71) * mm]});
            skFitSpline(sketch, "E2271", {"points": [v(2.84, 25.71) * mm, v(2.9, 25.71) * mm, v(3.02, 25.82) * mm, v(3.1, 25.95) * mm]});
            skFitSpline(sketch, "E2272", {"points": [v(-8.5, 30.5) * mm, v(-8.5, 31.2) * mm, v(-8.45, 31.5) * mm, v(-8.39, 31.14) * mm]});
            skFitSpline(sketch, "E2273", {"points": [v(-8.39, 31.14) * mm, v(-8.32, 30.8) * mm, v(-8.32, 30.22) * mm, v(-8.39, 29.87) * mm]});
            skFitSpline(sketch, "E2274", {"points": [v(-8.39, 29.87) * mm, v(-8.45, 29.53) * mm, v(-8.5, 29.81) * mm, v(-8.5, 30.5) * mm]});
            skFitSpline(sketch, "E2275", {"points": [v(-7.94, 30.65) * mm, v(-7.94, 31.43) * mm, v(-7.88, 31.71) * mm, v(-7.82, 31.28) * mm]});
            skFitSpline(sketch, "E2276", {"points": [v(-7.82, 31.28) * mm, v(-7.75, 30.85) * mm, v(-7.76, 30.22) * mm, v(-7.82, 29.87) * mm]});
            skFitSpline(sketch, "E2277", {"points": [v(-7.82, 29.87) * mm, v(-7.9, 29.52) * mm, v(-7.94, 29.88) * mm, v(-7.94, 30.65) * mm]});
            skLineSegment(sketch, "E2278", {"start": v(-7.94, 30.65) * mm, "end": v(-7.94, 30.65) * mm});
            skFitSpline(sketch, "E2279", {"points": [v(7.24, 31.8) * mm, v(7.25, 32.13) * mm, v(7.32, 32.2) * mm, v(7.41, 31.97) * mm]});
            skFitSpline(sketch, "E2280", {"points": [v(7.41, 31.97) * mm, v(7.5, 31.77) * mm, v(7.48, 31.53) * mm, v(7.39, 31.43) * mm]});
            skFitSpline(sketch, "E2281", {"points": [v(7.39, 31.43) * mm, v(7.3, 31.34) * mm, v(7.23, 31.5) * mm, v(7.24, 31.8) * mm]});
            skLineSegment(sketch, "E2282", {"start": v(7.24, 31.8) * mm, "end": v(7.24, 31.8) * mm});
            skFitSpline(sketch, "E2283", {"points": [v(1.16, 16.75) * mm, v(2.04, 17.99) * mm, v(2.09, 18.12) * mm, v(1.44, 17.53) * mm]});
            skFitSpline(sketch, "E2284", {"points": [v(1.44, 17.53) * mm, v(0.74, 16.88) * mm, v(-0.3, 15.27) * mm, v(-0.01, 15.27) * mm]});
            skFitSpline(sketch, "E2285", {"points": [v(-0.01, 15.27) * mm, v(0.05, 15.27) * mm, v(0.58, 15.94) * mm, v(1.16, 16.75) * mm]});
            skFitSpline(sketch, "E2286", {"points": [v(32.5, 19.15) * mm, v(32.16, 19.5) * mm, v(32, 18.93) * mm, v(32.22, 18.18) * mm]});
            skLineSegment(sketch, "E2287", {"start": v(32.22, 18.18) * mm, "end": v(32.45, 17.39) * mm});
            skLineSegment(sketch, "E2288", {"start": v(32.45, 17.39) * mm, "end": v(32.55, 18.19) * mm});
            skFitSpline(sketch, "E2289", {"points": [v(32.55, 18.19) * mm, v(32.61, 18.63) * mm, v(32.59, 19.06) * mm, v(32.5, 19.15) * mm]});
            skFitSpline(sketch, "E2290", {"points": [v(3.56, 19.1) * mm, v(3.77, 19.34) * mm, v(4.3, 19.73) * mm, v(4.75, 19.97) * mm]});
            skFitSpline(sketch, "E2291", {"points": [v(4.75, 19.97) * mm, v(5.2, 20.2) * mm, v(5.5, 20.46) * mm, v(5.41, 20.55) * mm]});
            skFitSpline(sketch, "E2292", {"points": [v(5.41, 20.55) * mm, v(5.25, 20.72) * mm, v(3.09, 19.33) * mm, v(2.81, 18.9) * mm]});
            skFitSpline(sketch, "E2293", {"points": [v(2.81, 18.9) * mm, v(2.55, 18.47) * mm, v(3.19, 18.64) * mm, v(3.56, 19.1) * mm]});
            skFitSpline(sketch, "E2294", {"points": [v(27.26, 21.03) * mm, v(27.26, 21.74) * mm, v(26.92, 22.33) * mm, v(26.52, 22.33) * mm]});
            skFitSpline(sketch, "E2295", {"points": [v(26.52, 22.33) * mm, v(26.05, 22.33) * mm, v(26.02, 21.93) * mm, v(26.42, 21.18) * mm]});
            skFitSpline(sketch, "E2296", {"points": [v(26.42, 21.18) * mm, v(26.76, 20.54) * mm, v(27.26, 20.45) * mm, v(27.26, 21.03) * mm]});
            skFitSpline(sketch, "E2297", {"points": [v(20.65, 24.74) * mm, v(20.57, 24.97) * mm, v(20.37, 25.15) * mm, v(20.2, 25.15) * mm]});
            skFitSpline(sketch, "E2298", {"points": [v(20.2, 25.15) * mm, v(19.8, 25.15) * mm, v(19.85, 23.92) * mm, v(20.27, 23.5) * mm]});
            skFitSpline(sketch, "E2299", {"points": [v(20.27, 23.5) * mm, v(20.55, 23.2) * mm, v(20.64, 23.26) * mm, v(20.72, 23.74) * mm]});
            skFitSpline(sketch, "E2300", {"points": [v(20.72, 23.74) * mm, v(20.77, 24.07) * mm, v(20.74, 24.52) * mm, v(20.65, 24.74) * mm]});
            skFitSpline(sketch, "E2301", {"points": [v(-16.43, 26.62) * mm, v(-16.7, 26.88) * mm, v(-16.77, 26.8) * mm, v(-16.77, 26.28) * mm]});
            skFitSpline(sketch, "E2302", {"points": [v(-16.77, 26.28) * mm, v(-16.77, 25.75) * mm, v(-16.7, 25.67) * mm, v(-16.43, 25.94) * mm]});
            skFitSpline(sketch, "E2303", {"points": [v(-16.43, 25.94) * mm, v(-16.17, 26.2) * mm, v(-16.17, 26.35) * mm, v(-16.43, 26.62) * mm]});
            skFitSpline(sketch, "E2304", {"points": [v(-12.02, 28.22) * mm, v(-11.71, 28.41) * mm, v(-11.72, 28.49) * mm, v(-12.07, 28.62) * mm]});
            skFitSpline(sketch, "E2305", {"points": [v(-12.07, 28.62) * mm, v(-12.3, 28.7) * mm, v(-12.56, 28.6) * mm, v(-12.65, 28.38) * mm]});
            skFitSpline(sketch, "E2306", {"points": [v(-12.65, 28.38) * mm, v(-12.82, 27.92) * mm, v(-12.58, 27.86) * mm, v(-12.02, 28.22) * mm]});
            skFitSpline(sketch, "E2307", {"points": [v(36, 28.53) * mm, v(35.46, 28.89) * mm, v(35.16, 28.89) * mm, v(35.16, 28.53) * mm]});
            skFitSpline(sketch, "E2308", {"points": [v(35.16, 28.53) * mm, v(35.16, 28.38) * mm, v(35.44, 28.25) * mm, v(35.8, 28.26) * mm]});
            skFitSpline(sketch, "E2309", {"points": [v(35.8, 28.26) * mm, v(36.3, 28.26) * mm, v(36.35, 28.31) * mm, v(36, 28.53) * mm]});
            skFitSpline(sketch, "E2310", {"points": [v(19.14, 31.98) * mm, v(19.28, 33.28) * mm, v(19.27, 33.3) * mm, v(18.7, 32.9) * mm]});
            skFitSpline(sketch, "E2311", {"points": [v(18.7, 32.9) * mm, v(18.17, 32.53) * mm, v(18.04, 32.56) * mm, v(17.42, 33.12) * mm]});
            skFitSpline(sketch, "E2312", {"points": [v(17.42, 33.12) * mm, v(17.04, 33.47) * mm, v(16.84, 33.56) * mm, v(16.98, 33.33) * mm]});
            skFitSpline(sketch, "E2313", {"points": [v(16.98, 33.33) * mm, v(17.54, 32.4) * mm, v(18.88, 30.5) * mm, v(18.93, 30.57) * mm]});
            skFitSpline(sketch, "E2314", {"points": [v(18.93, 30.57) * mm, v(18.97, 30.62) * mm, v(19.06, 31.25) * mm, v(19.14, 31.98) * mm]});
            skFitSpline(sketch, "E2315", {"points": [v(5.88, 32.16) * mm, v(8.2, 33.31) * mm, v(8.46, 33.56) * mm, v(8.42, 34.67) * mm]});
            skFitSpline(sketch, "E2316", {"points": [v(8.42, 34.67) * mm, v(8.42, 34.86) * mm, v(8.5, 34.96) * mm, v(8.61, 34.9) * mm]});
            skFitSpline(sketch, "E2317", {"points": [v(8.61, 34.9) * mm, v(8.73, 34.82) * mm, v(9.02, 35.2) * mm, v(9.27, 35.72) * mm]});
            skLineSegment(sketch, "E2318", {"start": v(9.27, 35.72) * mm, "end": v(9.73, 36.68) * mm});
            skLineSegment(sketch, "E2319", {"start": v(9.73, 36.68) * mm, "end": v(8.5, 35.92) * mm});
            skFitSpline(sketch, "E2320", {"points": [v(8.5, 35.92) * mm, v(7.83, 35.5) * mm, v(7.33, 35.11) * mm, v(7.39, 35.05) * mm]});
            skFitSpline(sketch, "E2321", {"points": [v(7.39, 35.05) * mm, v(7.45, 34.99) * mm, v(7.36, 34.77) * mm, v(7.2, 34.57) * mm]});
            skFitSpline(sketch, "E2322", {"points": [v(7.2, 34.57) * mm, v(6.83, 34.13) * mm, v(7.12, 33.52) * mm, v(7.56, 33.8) * mm]});
            skFitSpline(sketch, "E2323", {"points": [v(7.56, 33.8) * mm, v(7.75, 33.91) * mm, v(7.79, 33.85) * mm, v(7.66, 33.64) * mm]});
            skFitSpline(sketch, "E2324", {"points": [v(7.66, 33.64) * mm, v(7.37, 33.18) * mm, v(6.57, 33.84) * mm, v(6.77, 34.37) * mm]});
            skFitSpline(sketch, "E2325", {"points": [v(6.77, 34.37) * mm, v(6.96, 34.85) * mm, v(6.88, 34.84) * mm, v(5.71, 34.28) * mm]});
            skFitSpline(sketch, "E2326", {"points": [v(5.71, 34.28) * mm, v(4.76, 33.83) * mm, v(4.76, 33.82) * mm, v(5.29, 33.29) * mm]});
            skFitSpline(sketch, "E2327", {"points": [v(5.29, 33.29) * mm, v(5.58, 32.99) * mm, v(5.98, 32.82) * mm, v(6.17, 32.92) * mm]});
            skFitSpline(sketch, "E2328", {"points": [v(6.17, 32.92) * mm, v(6.36, 33.01) * mm, v(6.27, 32.9) * mm, v(5.96, 32.65) * mm]});
            skFitSpline(sketch, "E2329", {"points": [v(5.96, 32.65) * mm, v(5.66, 32.4) * mm, v(5.28, 32.21) * mm, v(5.12, 32.23) * mm]});
            skFitSpline(sketch, "E2330", {"points": [v(5.12, 32.23) * mm, v(4.95, 32.24) * mm, v(4.97, 32.3) * mm, v(5.16, 32.38) * mm]});
            skFitSpline(sketch, "E2331", {"points": [v(5.16, 32.38) * mm, v(5.61, 32.57) * mm, v(5.29, 33.33) * mm, v(4.76, 33.33) * mm]});
            skFitSpline(sketch, "E2332", {"points": [v(4.76, 33.33) * mm, v(4.46, 33.33) * mm, v(4.38, 33.15) * mm, v(4.49, 32.73) * mm]});
            skFitSpline(sketch, "E2333", {"points": [v(4.49, 32.73) * mm, v(4.63, 32.18) * mm, v(4.56, 32.14) * mm, v(3.45, 32.27) * mm]});
            skFitSpline(sketch, "E2334", {"points": [v(3.45, 32.27) * mm, v(2.36, 32.4) * mm, v(2.25, 32.34) * mm, v(2.2, 31.76) * mm]});
            skFitSpline(sketch, "E2335", {"points": [v(2.2, 31.76) * mm, v(2.17, 31.35) * mm, v(2.33, 31.07) * mm, v(2.64, 30.99) * mm]});
            skFitSpline(sketch, "E2336", {"points": [v(2.64, 30.99) * mm, v(3.26, 30.83) * mm, v(3, 30.73) * mm, v(5.88, 32.16) * mm]});
            skFitSpline(sketch, "E2337", {"points": [v(3, 31.52) * mm, v(3.02, 31.85) * mm, v(3.09, 31.92) * mm, v(3.18, 31.7) * mm]});
            skFitSpline(sketch, "E2338", {"points": [v(3.18, 31.7) * mm, v(3.26, 31.49) * mm, v(3.25, 31.24) * mm, v(3.16, 31.15) * mm]});
            skFitSpline(sketch, "E2339", {"points": [v(3.16, 31.15) * mm, v(3.06, 31.06) * mm, v(3, 31.22) * mm, v(3, 31.52) * mm]});
            skFitSpline(sketch, "E2340", {"points": [v(0.93, 31.9) * mm, v(1.91, 32.48) * mm, v(2.52, 32.67) * mm, v(3.16, 32.57) * mm]});
            skFitSpline(sketch, "E2341", {"points": [v(3.16, 32.57) * mm, v(3.88, 32.46) * mm, v(4.06, 32.54) * mm, v(4.2, 33.04) * mm]});
            skFitSpline(sketch, "E2342", {"points": [v(4.2, 33.04) * mm, v(4.35, 33.63) * mm, v(4.33, 33.64) * mm, v(3.64, 33.19) * mm]});
            skFitSpline(sketch, "E2343", {"points": [v(3.64, 33.19) * mm, v(3.25, 32.93) * mm, v(2.88, 32.78) * mm, v(2.8, 32.85) * mm]});
            skFitSpline(sketch, "E2344", {"points": [v(2.8, 32.85) * mm, v(2.73, 32.93) * mm, v(3.8, 33.59) * mm, v(5.16, 34.32) * mm]});
            skFitSpline(sketch, "E2345", {"points": [v(5.16, 34.32) * mm, v(8.8, 36.29) * mm, v(10.43, 37.43) * mm, v(11.6, 38.86) * mm]});
            skFitSpline(sketch, "E2346", {"points": [v(11.6, 38.86) * mm, v(12.38, 39.81) * mm, v(12.56, 40.21) * mm, v(12.33, 40.5) * mm]});
            skFitSpline(sketch, "E2347", {"points": [v(12.33, 40.5) * mm, v(12.16, 40.7) * mm, v(12.1, 40.95) * mm, v(12.2, 41.05) * mm]});
            skFitSpline(sketch, "E2348", {"points": [v(12.2, 41.05) * mm, v(12.3, 41.15) * mm, v(12.25, 41.23) * mm, v(12.08, 41.23) * mm]});
            skFitSpline(sketch, "E2349", {"points": [v(12.08, 41.23) * mm, v(11.9, 41.23) * mm, v(11.69, 41.1) * mm, v(11.6, 40.95) * mm]});
            skFitSpline(sketch, "E2350", {"points": [v(11.6, 40.95) * mm, v(11.5, 40.8) * mm, v(11.54, 40.67) * mm, v(11.7, 40.67) * mm]});
            skFitSpline(sketch, "E2351", {"points": [v(11.7, 40.67) * mm, v(11.84, 40.67) * mm, v(11.94, 40.5) * mm, v(11.9, 40.28) * mm]});
            skFitSpline(sketch, "E2352", {"points": [v(11.9, 40.28) * mm, v(11.83, 39.76) * mm, v(11.13, 38.92) * mm, v(10.94, 39.11) * mm]});
            skFitSpline(sketch, "E2353", {"points": [v(10.94, 39.11) * mm, v(10.86, 39.2) * mm, v(10.53, 39.04) * mm, v(10.2, 38.77) * mm]});
            skFitSpline(sketch, "E2354", {"points": [v(10.2, 38.77) * mm, v(9.88, 38.5) * mm, v(10.03, 38.73) * mm, v(10.53, 39.28) * mm]});
            skFitSpline(sketch, "E2355", {"points": [v(10.53, 39.28) * mm, v(11.86, 40.71) * mm, v(11.66, 40.98) * mm, v(10.25, 39.67) * mm]});
            skFitSpline(sketch, "E2356", {"points": [v(10.25, 39.67) * mm, v(9.44, 38.91) * mm, v(9.54, 39.06) * mm, v(10.56, 40.14) * mm]});
            skFitSpline(sketch, "E2357", {"points": [v(10.56, 40.14) * mm, v(11.73, 41.37) * mm, v(11.96, 41.76) * mm, v(11.62, 41.9) * mm]});
            skFitSpline(sketch, "E2358", {"points": [v(11.62, 41.9) * mm, v(11.37, 41.98) * mm, v(11.2, 41.95) * mm, v(11.24, 41.82) * mm]});
            skFitSpline(sketch, "E2359", {"points": [v(11.24, 41.82) * mm, v(11.28, 41.68) * mm, v(11.23, 41.6) * mm, v(11.14, 41.62) * mm]});
            skFitSpline(sketch, "E2360", {"points": [v(11.14, 41.62) * mm, v(11.05, 41.64) * mm, v(10.73, 41.47) * mm, v(10.44, 41.25) * mm]});
            skFitSpline(sketch, "E2361", {"points": [v(10.44, 41.25) * mm, v(10.14, 41.02) * mm, v(10.27, 41.24) * mm, v(10.73, 41.74) * mm]});
            skFitSpline(sketch, "E2362", {"points": [v(10.73, 41.74) * mm, v(11.38, 42.45) * mm, v(11.45, 42.65) * mm, v(11.08, 42.65) * mm]});
            skFitSpline(sketch, "E2363", {"points": [v(11.08, 42.65) * mm, v(10.82, 42.65) * mm, v(10.45, 42.4) * mm, v(10.26, 42.08) * mm]});
            skFitSpline(sketch, "E2364", {"points": [v(10.26, 42.08) * mm, v(10.06, 41.77) * mm, v(9.62, 41.52) * mm, v(9.27, 41.52) * mm]});
            skFitSpline(sketch, "E2365", {"points": [v(9.27, 41.52) * mm, v(8.91, 41.52) * mm, v(8.44, 41.22) * mm, v(8.18, 40.81) * mm]});
            skFitSpline(sketch, "E2366", {"points": [v(8.18, 40.81) * mm, v(7.93, 40.42) * mm, v(7.54, 40.1) * mm, v(7.31, 40.1) * mm]});
            skFitSpline(sketch, "E2367", {"points": [v(7.31, 40.1) * mm, v(7.09, 40.1) * mm, v(6.73, 39.7) * mm, v(6.52, 39.18) * mm]});
            skFitSpline(sketch, "E2368", {"points": [v(6.52, 39.18) * mm, v(6.12, 38.22) * mm, v(5.16, 37.18) * mm, v(4.91, 37.43) * mm]});
            skFitSpline(sketch, "E2369", {"points": [v(4.91, 37.43) * mm, v(4.83, 37.5) * mm, v(4.85, 37) * mm, v(4.96, 36.32) * mm]});
            skLineSegment(sketch, "E2370", {"start": v(4.96, 36.32) * mm, "end": v(5.15, 35.06) * mm});
            skLineSegment(sketch, "E2371", {"start": v(5.15, 35.06) * mm, "end": v(2.22, 33.5) * mm});
            skLineSegment(sketch, "E2372", {"start": v(2.22, 33.5) * mm, "end": v(-0.7, 31.94) * mm});
            skLineSegment(sketch, "E2373", {"start": v(-0.7, 31.94) * mm, "end": v(-2.15, 32.8) * mm});
            skFitSpline(sketch, "E2374", {"points": [v(-2.15, 32.8) * mm, v(-2.94, 33.27) * mm, v(-4.46, 34.09) * mm, v(-5.53, 34.62) * mm]});
            skFitSpline(sketch, "E2375", {"points": [v(-5.53, 34.62) * mm, v(-6.59, 35.16) * mm, v(-7.46, 35.66) * mm, v(-7.46, 35.74) * mm]});
            skFitSpline(sketch, "E2376", {"points": [v(-7.46, 35.74) * mm, v(-7.46, 35.83) * mm, v(-7.22, 35.77) * mm, v(-6.93, 35.6) * mm]});
            skFitSpline(sketch, "E2377", {"points": [v(-6.93, 35.6) * mm, v(-6.64, 35.45) * mm, v(-6.32, 35.4) * mm, v(-6.22, 35.5) * mm]});
            skFitSpline(sketch, "E2378", {"points": [v(-6.22, 35.5) * mm, v(-5.83, 35.9) * mm, v(-6.08, 37.06) * mm, v(-6.68, 37.66) * mm]});
            skFitSpline(sketch, "E2379", {"points": [v(-6.68, 37.66) * mm, v(-7.03, 38.01) * mm, v(-7.48, 38.65) * mm, v(-7.68, 39.09) * mm]});
            skFitSpline(sketch, "E2380", {"points": [v(-7.68, 39.09) * mm, v(-7.87, 39.52) * mm, v(-8.28, 39.94) * mm, v(-8.58, 40.02) * mm]});
            skFitSpline(sketch, "E2381", {"points": [v(-8.58, 40.02) * mm, v(-8.89, 40.1) * mm, v(-9.2, 40.4) * mm, v(-9.3, 40.7) * mm]});
            skFitSpline(sketch, "E2382", {"points": [v(-9.3, 40.7) * mm, v(-9.4, 41) * mm, v(-9.81, 41.31) * mm, v(-10.23, 41.41) * mm]});
            skFitSpline(sketch, "E2383", {"points": [v(-10.23, 41.41) * mm, v(-10.64, 41.51) * mm, v(-11.21, 41.83) * mm, v(-11.5, 42.12) * mm]});
            skFitSpline(sketch, "E2384", {"points": [v(-11.5, 42.12) * mm, v(-12.14, 42.8) * mm, v(-12.44, 42.78) * mm, v(-12.84, 42.05) * mm]});
            skFitSpline(sketch, "E2385", {"points": [v(-12.84, 42.05) * mm, v(-13.01, 41.72) * mm, v(-13.04, 41.52) * mm, v(-12.9, 41.61) * mm]});
            skFitSpline(sketch, "E2386", {"points": [v(-12.9, 41.61) * mm, v(-12.75, 41.7) * mm, v(-12.2, 41.3) * mm, v(-11.67, 40.73) * mm]});
            skFitSpline(sketch, "E2387", {"points": [v(-11.67, 40.73) * mm, v(-11.02, 40.03) * mm, v(-10.96, 39.91) * mm, v(-11.48, 40.37) * mm]});
            skFitSpline(sketch, "E2388", {"points": [v(-11.48, 40.37) * mm, v(-12.45, 41.22) * mm, v(-12.5, 40.81) * mm, v(-11.54, 39.82) * mm]});
            skFitSpline(sketch, "E2389", {"points": [v(-11.54, 39.82) * mm, v(-11.03, 39.29) * mm, v(-10.95, 39.07) * mm, v(-11.25, 39.07) * mm]});
            skFitSpline(sketch, "E2390", {"points": [v(-11.25, 39.07) * mm, v(-11.48, 39.07) * mm, v(-12.09, 39.52) * mm, v(-12.6, 40.07) * mm]});
            skFitSpline(sketch, "E2391", {"points": [v(-12.6, 40.07) * mm, v(-13.1, 40.62) * mm, v(-13.28, 40.88) * mm, v(-12.99, 40.66) * mm]});
            skFitSpline(sketch, "E2392", {"points": [v(-12.99, 40.66) * mm, v(-12.52, 40.3) * mm, v(-12.46, 40.3) * mm, v(-12.58, 40.65) * mm]});
            skFitSpline(sketch, "E2393", {"points": [v(-12.58, 40.65) * mm, v(-12.8, 41.3) * mm, v(-13.32, 41.32) * mm, v(-13.64, 40.71) * mm]});
            skFitSpline(sketch, "E2394", {"points": [v(-13.64, 40.71) * mm, v(-13.9, 40.24) * mm, v(-13.73, 39.93) * mm, v(-12.6, 38.67) * mm]});
            skFitSpline(sketch, "E2395", {"points": [v(-12.6, 38.67) * mm, v(-11.87, 37.85) * mm, v(-10.54, 36.72) * mm, v(-9.64, 36.15) * mm]});
            skFitSpline(sketch, "E2396", {"points": [v(-9.64, 36.15) * mm, v(-8.75, 35.59) * mm, v(-8.1, 35.03) * mm, v(-8.22, 34.92) * mm]});
            skFitSpline(sketch, "E2397", {"points": [v(-8.22, 34.92) * mm, v(-8.34, 34.8) * mm, v(-8.24, 34.79) * mm, v(-8, 34.88) * mm]});
            skFitSpline(sketch, "E2398", {"points": [v(-8, 34.88) * mm, v(-7.76, 34.97) * mm, v(-6.13, 34.2) * mm, v(-4.2, 33.08) * mm]});
            skFitSpline(sketch, "E2399", {"points": [v(-4.2, 33.08) * mm, v(-2.35, 32) * mm, v(-0.73, 31.1) * mm, v(-0.62, 31.1) * mm]});
            skFitSpline(sketch, "E2400", {"points": [v(-0.62, 31.1) * mm, v(-0.5, 31.08) * mm, v(0.2, 31.44) * mm, v(0.93, 31.9) * mm]});
            skLineSegment(sketch, "E2401", {"start": v(-12.4, 39.05) * mm, "end": v(-13.8, 40.53) * mm});
            skLineSegment(sketch, "E2402", {"start": v(-13.8, 40.53) * mm, "end": v(-12.33, 39.13) * mm});
            skFitSpline(sketch, "E2403", {"points": [v(-12.33, 39.13) * mm, v(-10.95, 37.83) * mm, v(-10.71, 37.57) * mm, v(-10.93, 37.57) * mm]});
            skFitSpline(sketch, "E2404", {"points": [v(-10.93, 37.57) * mm, v(-10.97, 37.57) * mm, v(-11.64, 38.23) * mm, v(-12.4, 39.05) * mm]});
            skFitSpline(sketch, "E2405", {"points": [v(10.04, 37.95) * mm, v(10.04, 38.01) * mm, v(10.26, 38.24) * mm, v(10.53, 38.45) * mm]});
            skFitSpline(sketch, "E2406", {"points": [v(10.53, 38.45) * mm, v(10.98, 38.8) * mm, v(11, 38.79) * mm, v(10.64, 38.34) * mm]});
            skFitSpline(sketch, "E2407", {"points": [v(10.64, 38.34) * mm, v(10.27, 37.87) * mm, v(10.04, 37.72) * mm, v(10.04, 37.95) * mm]});
            skFitSpline(sketch, "E2408", {"points": [v(-9.15, 38.4) * mm, v(-9.66, 38.73) * mm, v(-9.26, 39.6) * mm, v(-8.66, 39.49) * mm]});
            skFitSpline(sketch, "E2409", {"points": [v(-8.66, 39.49) * mm, v(-8.4, 39.44) * mm, v(-8.13, 39.19) * mm, v(-8.08, 38.94) * mm]});
            skFitSpline(sketch, "E2410", {"points": [v(-8.08, 38.94) * mm, v(-7.98, 38.4) * mm, v(-8.62, 38.08) * mm, v(-9.15, 38.4) * mm]});
            skFitSpline(sketch, "E2411", {"points": [v(-8.3, 39) * mm, v(-8.3, 39.14) * mm, v(-8.5, 39.26) * mm, v(-8.73, 39.26) * mm]});
            skFitSpline(sketch, "E2412", {"points": [v(-8.73, 39.26) * mm, v(-9.16, 39.26) * mm, v(-9.29, 38.93) * mm, v(-8.97, 38.6) * mm]});
            skFitSpline(sketch, "E2413", {"points": [v(-8.97, 38.6) * mm, v(-8.74, 38.38) * mm, v(-8.3, 38.64) * mm, v(-8.3, 39) * mm]});
            skFitSpline(sketch, "E2414", {"points": [v(7.13, 38.31) * mm, v(6.7, 38.75) * mm, v(6.95, 39.54) * mm, v(7.52, 39.54) * mm]});
            skFitSpline(sketch, "E2415", {"points": [v(7.52, 39.54) * mm, v(7.96, 39.54) * mm, v(8.08, 39.39) * mm, v(8.01, 38.93) * mm]});
            skFitSpline(sketch, "E2416", {"points": [v(8.01, 38.93) * mm, v(7.92, 38.3) * mm, v(7.47, 37.98) * mm, v(7.13, 38.31) * mm]});
            skFitSpline(sketch, "E2417", {"points": [v(7.78, 38.98) * mm, v(7.78, 39.13) * mm, v(7.66, 39.26) * mm, v(7.5, 39.26) * mm]});
            skFitSpline(sketch, "E2418", {"points": [v(7.5, 39.26) * mm, v(7.34, 39.26) * mm, v(7.22, 39.13) * mm, v(7.22, 38.98) * mm]});
            skFitSpline(sketch, "E2419", {"points": [v(7.22, 38.98) * mm, v(7.22, 38.82) * mm, v(7.34, 38.7) * mm, v(7.5, 38.7) * mm]});
            skFitSpline(sketch, "E2420", {"points": [v(7.5, 38.7) * mm, v(7.66, 38.7) * mm, v(7.78, 38.82) * mm, v(7.78, 38.98) * mm]});
            skLineSegment(sketch, "E2421", {"start": v(-11.85, 41.59) * mm, "end": v(-12.68, 42.5) * mm});
            skLineSegment(sketch, "E2422", {"start": v(-12.68, 42.5) * mm, "end": v(-11.76, 41.68) * mm});
            skFitSpline(sketch, "E2423", {"points": [v(-11.76, 41.68) * mm, v(-10.9, 40.9) * mm, v(-10.71, 40.67) * mm, v(-10.93, 40.67) * mm]});
            skFitSpline(sketch, "E2424", {"points": [v(-10.93, 40.67) * mm, v(-10.98, 40.67) * mm, v(-11.4, 41.08) * mm, v(-11.85, 41.59) * mm]});
            skFitSpline(sketch, "E2425", {"points": [v(-3.5, 32.34) * mm, v(-3.5, 32.41) * mm, v(-4.02, 32.74) * mm, v(-4.64, 33.05) * mm]});
            skFitSpline(sketch, "E2426", {"points": [v(-4.64, 33.05) * mm, v(-5.76, 33.63) * mm, v(-5.78, 33.63) * mm, v(-5.43, 33.07) * mm]});
            skFitSpline(sketch, "E2427", {"points": [v(-5.43, 33.07) * mm, v(-5.24, 32.76) * mm, v(-4.76, 32.46) * mm, v(-4.36, 32.4) * mm]});
            skFitSpline(sketch, "E2428", {"points": [v(-4.36, 32.4) * mm, v(-3.97, 32.34) * mm, v(-3.62, 32.27) * mm, v(-3.58, 32.25) * mm]});
            skFitSpline(sketch, "E2429", {"points": [v(-3.58, 32.25) * mm, v(-3.54, 32.22) * mm, v(-3.5, 32.26) * mm, v(-3.5, 32.34) * mm]});
            skFitSpline(sketch, "E2430", {"points": [v(15.4, 35.3) * mm, v(15.4, 35.46) * mm, v(15.2, 35.59) * mm, v(14.96, 35.59) * mm]});
            skFitSpline(sketch, "E2431", {"points": [v(14.96, 35.59) * mm, v(14.72, 35.59) * mm, v(14.6, 35.46) * mm, v(14.7, 35.3) * mm]});
            skFitSpline(sketch, "E2432", {"points": [v(14.7, 35.3) * mm, v(14.8, 35.15) * mm, v(15, 35.03) * mm, v(15.14, 35.03) * mm]});
            skFitSpline(sketch, "E2433", {"points": [v(15.14, 35.03) * mm, v(15.28, 35.03) * mm, v(15.4, 35.15) * mm, v(15.4, 35.3) * mm]});
            skFitSpline(sketch, "E2434", {"points": [v(19.92, 35.57) * mm, v(19.92, 36.09) * mm, v(19.45, 36.62) * mm, v(19.2, 36.38) * mm]});
            skFitSpline(sketch, "E2435", {"points": [v(19.2, 36.38) * mm, v(19.01, 36.19) * mm, v(19.4, 35.03) * mm, v(19.67, 35.03) * mm]});
            skFitSpline(sketch, "E2436", {"points": [v(19.67, 35.03) * mm, v(19.8, 35.03) * mm, v(19.92, 35.27) * mm, v(19.92, 35.57) * mm]});
            skFitSpline(sketch, "E2437", {"points": [v(2.46, 36.2) * mm, v(3.24, 36.54) * mm, v(3.75, 36.91) * mm, v(3.64, 37.08) * mm]});
            skFitSpline(sketch, "E2438", {"points": [v(3.64, 37.08) * mm, v(3.52, 37.27) * mm, v(3.64, 37.3) * mm, v(3.94, 37.2) * mm]});
            skFitSpline(sketch, "E2439", {"points": [v(3.94, 37.2) * mm, v(4.2, 37.1) * mm, v(4.36, 37.1) * mm, v(4.29, 37.23) * mm]});
            skFitSpline(sketch, "E2440", {"points": [v(4.29, 37.23) * mm, v(4.21, 37.35) * mm, v(4.58, 37.7) * mm, v(5.12, 37.98) * mm]});
            skFitSpline(sketch, "E2441", {"points": [v(5.12, 37.98) * mm, v(5.65, 38.27) * mm, v(6.09, 38.58) * mm, v(6.09, 38.67) * mm]});
            skFitSpline(sketch, "E2442", {"points": [v(6.09, 38.67) * mm, v(6.09, 38.76) * mm, v(5.1, 38.84) * mm, v(3.88, 38.84) * mm]});
            skFitSpline(sketch, "E2443", {"points": [v(3.88, 38.84) * mm, v(1.97, 38.84) * mm, v(1.68, 38.77) * mm, v(1.78, 38.37) * mm]});
            skFitSpline(sketch, "E2444", {"points": [v(1.78, 38.37) * mm, v(1.85, 38.12) * mm, v(1.77, 37.83) * mm, v(1.6, 37.72) * mm]});
            skFitSpline(sketch, "E2445", {"points": [v(1.6, 37.72) * mm, v(1.41, 37.6) * mm, v(1.36, 37.7) * mm, v(1.47, 37.98) * mm]});
            skFitSpline(sketch, "E2446", {"points": [v(1.47, 37.98) * mm, v(1.67, 38.52) * mm, v(1.17, 39.16) * mm, v(0.12, 39.7) * mm]});
            skFitSpline(sketch, "E2447", {"points": [v(0.12, 39.7) * mm, v(-0.61, 40.08) * mm, v(-0.76, 40.06) * mm, v(-1.66, 39.48) * mm]});
            skFitSpline(sketch, "E2448", {"points": [v(-1.66, 39.48) * mm, v(-2.7, 38.8) * mm, v(-2.9, 38.2) * mm, v(-2.3, 37.6) * mm]});
            skFitSpline(sketch, "E2449", {"points": [v(-2.3, 37.6) * mm, v(-2.02, 37.32) * mm, v(-2.05, 37.29) * mm, v(-2.45, 37.44) * mm]});
            skFitSpline(sketch, "E2450", {"points": [v(-2.45, 37.44) * mm, v(-2.73, 37.54) * mm, v(-2.94, 37.92) * mm, v(-2.94, 38.3) * mm]});
            skFitSpline(sketch, "E2451", {"points": [v(-2.94, 38.3) * mm, v(-2.94, 38.67) * mm, v(-3.1, 38.99) * mm, v(-3.3, 39) * mm]});
            skFitSpline(sketch, "E2452", {"points": [v(-3.3, 39) * mm, v(-3.49, 39) * mm, v(-3.15, 39.2) * mm, v(-2.55, 39.42) * mm]});
            skFitSpline(sketch, "E2453", {"points": [v(-2.55, 39.42) * mm, v(-1.94, 39.64) * mm, v(-1.29, 39.96) * mm, v(-1.09, 40.12) * mm]});
            skFitSpline(sketch, "E2454", {"points": [v(-1.09, 40.12) * mm, v(-0.83, 40.34) * mm, v(-0.4, 40.25) * mm, v(0.5, 39.78) * mm]});
            skFitSpline(sketch, "E2455", {"points": [v(0.5, 39.78) * mm, v(1.43, 39.3) * mm, v(2.2, 39.14) * mm, v(3.75, 39.13) * mm]});
            skFitSpline(sketch, "E2456", {"points": [v(3.75, 39.13) * mm, v(4.86, 39.12) * mm, v(5.9, 39.24) * mm, v(6.06, 39.4) * mm]});
            skFitSpline(sketch, "E2457", {"points": [v(6.06, 39.4) * mm, v(6.25, 39.59) * mm, v(5.57, 39.68) * mm, v(4.03, 39.68) * mm]});
            skFitSpline(sketch, "E2458", {"points": [v(4.03, 39.68) * mm, v(2.23, 39.68) * mm, v(1.46, 39.81) * mm, v(0.59, 40.27) * mm]});
            skLineSegment(sketch, "E2459", {"start": v(0.59, 40.27) * mm, "end": v(-0.54, 40.86) * mm});
            skLineSegment(sketch, "E2460", {"start": v(-0.54, 40.86) * mm, "end": v(-1.95, 40.2) * mm});
            skFitSpline(sketch, "E2461", {"points": [v(-1.95, 40.2) * mm, v(-3.03, 39.7) * mm, v(-3.87, 39.55) * mm, v(-5.46, 39.54) * mm]});
            skFitSpline(sketch, "E2462", {"points": [v(-5.46, 39.54) * mm, v(-7.94, 39.54) * mm, v(-7.93, 39.33) * mm, v(-5.45, 38.98) * mm]});
            skLineSegment(sketch, "E2463", {"start": v(-5.45, 38.98) * mm, "end": v(-3.65, 38.72) * mm});
            skLineSegment(sketch, "E2464", {"start": v(-3.65, 38.72) * mm, "end": v(-5.41, 38.82) * mm});
            skFitSpline(sketch, "E2465", {"points": [v(-5.41, 38.82) * mm, v(-6.38, 38.88) * mm, v(-7.18, 38.81) * mm, v(-7.18, 38.68) * mm]});
            skFitSpline(sketch, "E2466", {"points": [v(-7.18, 38.68) * mm, v(-7.18, 38.32) * mm, v(-6.16, 37.83) * mm, v(-5.9, 38.07) * mm]});
            skFitSpline(sketch, "E2467", {"points": [v(-5.9, 38.07) * mm, v(-5.77, 38.18) * mm, v(-5.74, 38.08) * mm, v(-5.83, 37.84) * mm]});
            skFitSpline(sketch, "E2468", {"points": [v(-5.83, 37.84) * mm, v(-5.92, 37.57) * mm, v(-5.8, 37.4) * mm, v(-5.52, 37.37) * mm]});
            skFitSpline(sketch, "E2469", {"points": [v(-5.52, 37.37) * mm, v(-5.27, 37.35) * mm, v(-4.74, 37.24) * mm, v(-4.35, 37.13) * mm]});
            skLineSegment(sketch, "E2470", {"start": v(-4.35, 37.13) * mm, "end": v(-3.65, 36.92) * mm});
            skLineSegment(sketch, "E2471", {"start": v(-3.65, 36.92) * mm, "end": v(-4.35, 37.74) * mm});
            skLineSegment(sketch, "E2472", {"start": v(-4.35, 37.74) * mm, "end": v(-5.06, 38.55) * mm});
            skLineSegment(sketch, "E2473", {"start": v(-5.06, 38.55) * mm, "end": v(-4.16, 37.75) * mm});
            skFitSpline(sketch, "E2474", {"points": [v(-4.16, 37.75) * mm, v(-3.6, 37.24) * mm, v(-3.13, 37.02) * mm, v(-2.9, 37.16) * mm]});
            skFitSpline(sketch, "E2475", {"points": [v(-2.9, 37.16) * mm, v(-2.69, 37.28) * mm, v(-2.61, 37.27) * mm, v(-2.73, 37.14) * mm]});
            skFitSpline(sketch, "E2476", {"points": [v(-2.73, 37.14) * mm, v(-2.84, 37.02) * mm, v(-2.71, 36.75) * mm, v(-2.44, 36.54) * mm]});
            skFitSpline(sketch, "E2477", {"points": [v(-2.44, 36.54) * mm, v(-1.72, 36) * mm, v(-2.42, 36.07) * mm, v(-4.12, 36.7) * mm]});
            skFitSpline(sketch, "E2478", {"points": [v(-4.12, 36.7) * mm, v(-4.92, 37.02) * mm, v(-5.43, 37.12) * mm, v(-5.26, 36.95) * mm]});
            skFitSpline(sketch, "E2479", {"points": [v(-5.26, 36.95) * mm, v(-5.08, 36.77) * mm, v(-4.08, 36.33) * mm, v(-3.02, 35.96) * mm]});
            skFitSpline(sketch, "E2480", {"points": [v(-3.02, 35.96) * mm, v(-0.86, 35.21) * mm, v(0.28, 35.26) * mm, v(2.46, 36.2) * mm]});
            skFitSpline(sketch, "E2481", {"points": [v(-0.55, 36.07) * mm, v(0.07, 36.14) * mm, v(0.74, 36.33) * mm, v(0.94, 36.5) * mm]});
            skFitSpline(sketch, "E2482", {"points": [v(0.94, 36.5) * mm, v(1.14, 36.66) * mm, v(1.39, 36.72) * mm, v(1.48, 36.62) * mm]});
            skFitSpline(sketch, "E2483", {"points": [v(1.48, 36.62) * mm, v(1.7, 36.4) * mm, v(2.6, 37.6) * mm, v(2.48, 37.94) * mm]});
            skFitSpline(sketch, "E2484", {"points": [v(2.48, 37.94) * mm, v(2.44, 38.07) * mm, v(2.54, 38.09) * mm, v(2.71, 37.98) * mm]});
            skFitSpline(sketch, "E2485", {"points": [v(2.71, 37.98) * mm, v(2.92, 37.85) * mm, v(2.85, 37.6) * mm, v(2.5, 37.22) * mm]});
            skFitSpline(sketch, "E2486", {"points": [v(2.5, 37.22) * mm, v(2, 36.66) * mm, v(2.01, 36.65) * mm, v(2.7, 36.82) * mm]});
            skFitSpline(sketch, "E2487", {"points": [v(2.7, 36.82) * mm, v(3.13, 36.93) * mm, v(3.02, 36.82) * mm, v(2.42, 36.54) * mm]});
            skFitSpline(sketch, "E2488", {"points": [v(2.42, 36.54) * mm, v(1.88, 36.3) * mm, v(0.73, 36.06) * mm, v(-0.12, 36.02) * mm]});
            skFitSpline(sketch, "E2489", {"points": [v(-0.12, 36.02) * mm, v(-0.97, 35.98) * mm, v(-1.17, 36) * mm, v(-0.55, 36.07) * mm]});
            skFitSpline(sketch, "E2490", {"points": [v(-1.45, 36.75) * mm, v(-1.1, 36.95) * mm, v(-1, 37.23) * mm, v(-1.13, 37.62) * mm]});
            skFitSpline(sketch, "E2491", {"points": [v(-1.13, 37.62) * mm, v(-1.27, 38.06) * mm, v(-1.22, 38.14) * mm, v(-0.93, 37.96) * mm]});
            skFitSpline(sketch, "E2492", {"points": [v(-0.93, 37.96) * mm, v(-0.68, 37.81) * mm, v(-0.72, 38) * mm, v(-1.04, 38.5) * mm]});
            skFitSpline(sketch, "E2493", {"points": [v(-1.04, 38.5) * mm, v(-1.32, 38.91) * mm, v(-1.42, 39.26) * mm, v(-1.28, 39.26) * mm]});
            skFitSpline(sketch, "E2494", {"points": [v(-1.28, 39.26) * mm, v(-1.13, 39.26) * mm, v(-0.96, 39.1) * mm, v(-0.9, 38.9) * mm]});
            skFitSpline(sketch, "E2495", {"points": [v(-0.9, 38.9) * mm, v(-0.8, 38.63) * mm, v(-0.65, 38.65) * mm, v(-0.24, 38.96) * mm]});
            skFitSpline(sketch, "E2496", {"points": [v(-0.24, 38.96) * mm, v(0.19, 39.28) * mm, v(0.23, 39.29) * mm, v(-0.05, 38.98) * mm]});
            skFitSpline(sketch, "E2497", {"points": [v(-0.05, 38.98) * mm, v(-0.46, 38.52) * mm, v(-0.53, 37.17) * mm, v(-0.14, 37.41) * mm]});
            skFitSpline(sketch, "E2498", {"points": [v(-0.14, 37.41) * mm, v(0, 37.5) * mm, v(0.22, 37.43) * mm, v(0.33, 37.24) * mm]});
            skFitSpline(sketch, "E2499", {"points": [v(0.33, 37.24) * mm, v(0.46, 37.04) * mm, v(0.4, 36.99) * mm, v(0.2, 37.12) * mm]});
            skFitSpline(sketch, "E2500", {"points": [v(0.2, 37.12) * mm, v(0.02, 37.23) * mm, v(-0.12, 37.15) * mm, v(-0.12, 36.95) * mm]});
            skFitSpline(sketch, "E2501", {"points": [v(-0.12, 36.95) * mm, v(-0.13, 36.65) * mm, v(-0.17, 36.64) * mm, v(-0.36, 36.94) * mm]});
            skFitSpline(sketch, "E2502", {"points": [v(-0.36, 36.94) * mm, v(-0.55, 37.24) * mm, v(-0.67, 37.22) * mm, v(-0.96, 36.87) * mm]});
            skFitSpline(sketch, "E2503", {"points": [v(-0.96, 36.87) * mm, v(-1.15, 36.63) * mm, v(-1.46, 36.44) * mm, v(-1.64, 36.45) * mm]});
            skFitSpline(sketch, "E2504", {"points": [v(-1.64, 36.45) * mm, v(-1.81, 36.45) * mm, v(-1.73, 36.59) * mm, v(-1.45, 36.75) * mm]});
            skFitSpline(sketch, "E2505", {"points": [v(0.32, 37.71) * mm, v(0.03, 37.94) * mm, v(-0.13, 38.21) * mm, v(-0.02, 38.32) * mm]});
            skFitSpline(sketch, "E2506", {"points": [v(-0.02, 38.32) * mm, v(0.3, 38.63) * mm, v(0.99, 38.67) * mm, v(1.17, 38.39) * mm]});
            skFitSpline(sketch, "E2507", {"points": [v(1.17, 38.39) * mm, v(1.25, 38.25) * mm, v(1.11, 38.13) * mm, v(0.85, 38.13) * mm]});
            skFitSpline(sketch, "E2508", {"points": [v(0.85, 38.13) * mm, v(0.46, 38.13) * mm, v(0.44, 38.05) * mm, v(0.73, 37.7) * mm]});
            skFitSpline(sketch, "E2509", {"points": [v(0.73, 37.7) * mm, v(1.17, 37.18) * mm, v(1.03, 37.18) * mm, v(0.32, 37.71) * mm]});
            skFitSpline(sketch, "E2510", {"points": [v(-2.02, 37.99) * mm, v(-2.48, 38.5) * mm, v(-2.47, 38.6) * mm, v(-1.95, 38.6) * mm]});
            skFitSpline(sketch, "E2511", {"points": [v(-1.95, 38.6) * mm, v(-1.72, 38.6) * mm, v(-1.53, 38.37) * mm, v(-1.53, 38.08) * mm]});
            skFitSpline(sketch, "E2512", {"points": [v(-1.53, 38.08) * mm, v(-1.53, 37.47) * mm, v(-1.56, 37.46) * mm, v(-2.02, 37.99) * mm]});
            skFitSpline(sketch, "E2513", {"points": [v(-26.73, 38.58) * mm, v(-26.82, 38.68) * mm, v(-27.06, 38.69) * mm, v(-27.27, 38.6) * mm]});
            skFitSpline(sketch, "E2514", {"points": [v(-27.27, 38.6) * mm, v(-27.5, 38.51) * mm, v(-27.42, 38.45) * mm, v(-27.1, 38.43) * mm]});
            skFitSpline(sketch, "E2515", {"points": [v(-27.1, 38.43) * mm, v(-26.8, 38.42) * mm, v(-26.63, 38.49) * mm, v(-26.73, 38.58) * mm]});
            skFitSpline(sketch, "E2516", {"points": [v(-11.4, 39.36) * mm, v(-11.4, 39.4) * mm, v(-11.7, 39.7) * mm, v(-12.04, 40) * mm]});
            skLineSegment(sketch, "E2517", {"start": v(-12.04, 40) * mm, "end": v(-12.68, 40.53) * mm});
            skLineSegment(sketch, "E2518", {"start": v(-12.68, 40.53) * mm, "end": v(-12.14, 39.9) * mm});
            skFitSpline(sketch, "E2519", {"points": [v(-12.14, 39.9) * mm, v(-11.64, 39.3) * mm, v(-11.4, 39.13) * mm, v(-11.4, 39.36) * mm]});
            skFitSpline(sketch, "E2520", {"points": [v(11.49, 39.75) * mm, v(11.84, 40.2) * mm, v(11.83, 40.21) * mm, v(11.38, 39.86) * mm]});
            skFitSpline(sketch, "E2521", {"points": [v(11.38, 39.86) * mm, v(10.91, 39.5) * mm, v(10.76, 39.26) * mm, v(11, 39.26) * mm]});
            skFitSpline(sketch, "E2522", {"points": [v(11, 39.26) * mm, v(11.05, 39.26) * mm, v(11.27, 39.48) * mm, v(11.49, 39.75) * mm]});
            skFitSpline(sketch, "E2523", {"points": [v(-2.44, 40.28) * mm, v(-1.5, 40.68) * mm, v(-1.45, 40.75) * mm, v(-1.95, 40.96) * mm]});
            skFitSpline(sketch, "E2524", {"points": [v(-1.95, 40.96) * mm, v(-2.46, 41.17) * mm, v(-2.44, 41.2) * mm, v(-1.77, 41.21) * mm]});
            skFitSpline(sketch, "E2525", {"points": [v(-1.77, 41.21) * mm, v(-0.42, 41.25) * mm, v(0.22, 42.07) * mm, v(0.44, 44.08) * mm]});
            skLineSegment(sketch, "E2526", {"start": v(0.44, 44.08) * mm, "end": v(0.65, 45.9) * mm});
            skLineSegment(sketch, "E2527", {"start": v(0.65, 45.9) * mm, "end": v(0.69, 44.4) * mm});
            skFitSpline(sketch, "E2528", {"points": [v(0.69, 44.4) * mm, v(0.7, 43.6) * mm, v(0.85, 42.93) * mm, v(1, 42.93) * mm]});
            skFitSpline(sketch, "E2529", {"points": [v(1, 42.93) * mm, v(1.52, 42.93) * mm, v(2.18, 44.63) * mm, v(2, 45.47) * mm]});
            skFitSpline(sketch, "E2530", {"points": [v(2, 45.47) * mm, v(1.78, 46.44) * mm, v(0.3, 48.57) * mm, v(-0.17, 48.57) * mm]});
            skFitSpline(sketch, "E2531", {"points": [v(-0.17, 48.57) * mm, v(-0.35, 48.57) * mm, v(-0.2, 48.22) * mm, v(0.18, 47.8) * mm]});
            skFitSpline(sketch, "E2532", {"points": [v(0.18, 47.8) * mm, v(0.84, 47.05) * mm, v(0.82, 47.06) * mm, v(-0.12, 47.87) * mm]});
            skFitSpline(sketch, "E2533", {"points": [v(-0.12, 47.87) * mm, v(-0.66, 48.33) * mm, v(-1.14, 48.73) * mm, v(-1.19, 48.75) * mm]});
            skFitSpline(sketch, "E2534", {"points": [v(-1.19, 48.75) * mm, v(-1.24, 48.77) * mm, v(-1.06, 48.87) * mm, v(-0.8, 48.97) * mm]});
            skFitSpline(sketch, "E2535", {"points": [v(-0.8, 48.97) * mm, v(-0.46, 49.1) * mm, v(0.05, 48.77) * mm, v(0.91, 47.86) * mm]});
            skFitSpline(sketch, "E2536", {"points": [v(0.91, 47.86) * mm, v(1.67, 47.08) * mm, v(2.2, 46.72) * mm, v(2.26, 46.94) * mm]});
            skFitSpline(sketch, "E2537", {"points": [v(2.26, 46.94) * mm, v(3.04, 49.48) * mm, v(2.32, 51.6) * mm, v(0.16, 53.18) * mm]});
            skLineSegment(sketch, "E2538", {"start": v(0.16, 53.18) * mm, "end": v(-0.54, 53.7) * mm});
            skLineSegment(sketch, "E2539", {"start": v(-0.54, 53.7) * mm, "end": v(0.22, 53.25) * mm});
            skFitSpline(sketch, "E2540", {"points": [v(0.22, 53.25) * mm, v(1.24, 52.66) * mm, v(1.37, 52.69) * mm, v(1, 53.44) * mm]});
            skFitSpline(sketch, "E2541", {"points": [v(1, 53.44) * mm, v(0.71, 54.04) * mm, v(0.72, 54.05) * mm, v(1.13, 53.54) * mm]});
            skFitSpline(sketch, "E2542", {"points": [v(1.13, 53.54) * mm, v(1.36, 53.25) * mm, v(1.49, 52.9) * mm, v(1.4, 52.76) * mm]});
            skFitSpline(sketch, "E2543", {"points": [v(1.4, 52.76) * mm, v(1.32, 52.63) * mm, v(1.36, 52.52) * mm, v(1.49, 52.53) * mm]});
            skFitSpline(sketch, "E2544", {"points": [v(1.49, 52.53) * mm, v(1.83, 52.53) * mm, v(2.42, 53.95) * mm, v(2.42, 54.8) * mm]});
            skFitSpline(sketch, "E2545", {"points": [v(2.42, 54.8) * mm, v(2.42, 55.9) * mm, v(1.87, 57.3) * mm, v(1.32, 57.59) * mm]});
            skFitSpline(sketch, "E2546", {"points": [v(1.32, 57.59) * mm, v(1.05, 57.73) * mm, v(0.27, 57.77) * mm, v(-0.42, 57.67) * mm]});
            skFitSpline(sketch, "E2547", {"points": [v(-0.42, 57.67) * mm, v(-1.5, 57.52) * mm, v(-1.58, 57.47) * mm, v(-0.97, 57.3) * mm]});
            skLineSegment(sketch, "E2548", {"start": v(-0.97, 57.3) * mm, "end": v(-0.26, 57.1) * mm});
            skLineSegment(sketch, "E2549", {"start": v(-0.26, 57.1) * mm, "end": v(-0.98, 57.07) * mm});
            skFitSpline(sketch, "E2550", {"points": [v(-0.98, 57.07) * mm, v(-1.93, 57.03) * mm, v(-2.37, 56.55) * mm, v(-2.41, 55.5) * mm]});
            skLineSegment(sketch, "E2551", {"start": v(-2.41, 55.5) * mm, "end": v(-2.44, 54.64) * mm});
            skLineSegment(sketch, "E2552", {"start": v(-2.44, 54.64) * mm, "end": v(-2.64, 55.49) * mm});
            skFitSpline(sketch, "E2553", {"points": [v(-2.64, 55.49) * mm, v(-2.74, 55.95) * mm, v(-2.7, 56.54) * mm, v(-2.56, 56.8) * mm]});
            skFitSpline(sketch, "E2554", {"points": [v(-2.56, 56.8) * mm, v(-2.18, 57.44) * mm, v(-0.86, 58.17) * mm, v(-0.1, 58.17) * mm]});
            skFitSpline(sketch, "E2555", {"points": [v(-0.1, 58.17) * mm, v(0.4, 58.17) * mm, v(0.48, 58.25) * mm, v(0.24, 58.49) * mm]});
            skFitSpline(sketch, "E2556", {"points": [v(0.24, 58.49) * mm, v(-0.5, 59.22) * mm, v(-2.96, 57.7) * mm, v(-3.67, 56.07) * mm]});
            skFitSpline(sketch, "E2557", {"points": [v(-3.67, 56.07) * mm, v(-3.97, 55.4) * mm, v(-4.05, 55.33) * mm, v(-4.06, 55.78) * mm]});
            skFitSpline(sketch, "E2558", {"points": [v(-4.06, 55.78) * mm, v(-4.07, 56.4) * mm, v(-2.42, 58.15) * mm, v(-1.25, 58.74) * mm]});
            skLineSegment(sketch, "E2559", {"start": v(-1.25, 58.74) * mm, "end": v(-0.55, 59.1) * mm});
            skLineSegment(sketch, "E2560", {"start": v(-0.55, 59.1) * mm, "end": v(-1.17, 59.38) * mm});
            skFitSpline(sketch, "E2561", {"points": [v(-1.17, 59.38) * mm, v(-1.92, 59.71) * mm, v(-3.5, 59.44) * mm, v(-4.23, 58.85) * mm]});
            skFitSpline(sketch, "E2562", {"points": [v(-4.23, 58.85) * mm, v(-4.53, 58.6) * mm, v(-4.59, 58.5) * mm, v(-4.35, 58.62) * mm]});
            skFitSpline(sketch, "E2563", {"points": [v(-4.35, 58.62) * mm, v(-4.07, 58.76) * mm, v(-4.1, 58.63) * mm, v(-4.47, 58.22) * mm]});
            skFitSpline(sketch, "E2564", {"points": [v(-4.47, 58.22) * mm, v(-5, 57.61) * mm, v(-5, 57.6) * mm, v(-4.47, 57.57) * mm]});
            skFitSpline(sketch, "E2565", {"points": [v(-4.47, 57.57) * mm, v(-4.15, 57.55) * mm, v(-4.26, 57.46) * mm, v(-4.74, 57.36) * mm]});
            skFitSpline(sketch, "E2566", {"points": [v(-4.74, 57.36) * mm, v(-5.19, 57.26) * mm, v(-5.74, 56.9) * mm, v(-5.97, 56.56) * mm]});
            skFitSpline(sketch, "E2567", {"points": [v(-5.97, 56.56) * mm, v(-6.37, 55.95) * mm, v(-6.36, 55.94) * mm, v(-5.3, 56.06) * mm]});
            skLineSegment(sketch, "E2568", {"start": v(-5.3, 56.06) * mm, "end": v(-4.21, 56.18) * mm});
            skLineSegment(sketch, "E2569", {"start": v(-4.21, 56.18) * mm, "end": v(-5.34, 55.9) * mm});
            skFitSpline(sketch, "E2570", {"points": [v(-5.34, 55.9) * mm, v(-6.83, 55.52) * mm, v(-7.34, 55) * mm, v(-6.04, 55.2) * mm]});
            skFitSpline(sketch, "E2571", {"points": [v(-6.04, 55.2) * mm, v(-5.13, 55.34) * mm, v(-5.11, 55.33) * mm, v(-5.85, 55.08) * mm]});
            skFitSpline(sketch, "E2572", {"points": [v(-5.85, 55.08) * mm, v(-6.94, 54.72) * mm, v(-7.51, 54.2) * mm, v(-7.33, 53.73) * mm]});
            skFitSpline(sketch, "E2573", {"points": [v(-7.33, 53.73) * mm, v(-7.25, 53.52) * mm, v(-7.3, 53.42) * mm, v(-7.46, 53.51) * mm]});
            skFitSpline(sketch, "E2574", {"points": [v(-7.46, 53.51) * mm, v(-7.63, 53.62) * mm, v(-7.69, 53.2) * mm, v(-7.6, 52.42) * mm]});
            skFitSpline(sketch, "E2575", {"points": [v(-7.6, 52.42) * mm, v(-7.52, 51.54) * mm, v(-7.6, 51.06) * mm, v(-7.9, 50.82) * mm]});
            skFitSpline(sketch, "E2576", {"points": [v(-7.9, 50.82) * mm, v(-8.12, 50.63) * mm, v(-8.3, 50.2) * mm, v(-8.3, 49.85) * mm]});
            skFitSpline(sketch, "E2577", {"points": [v(-8.3, 49.85) * mm, v(-8.3, 49.5) * mm, v(-8.5, 48.82) * mm, v(-8.75, 48.33) * mm]});
            skFitSpline(sketch, "E2578", {"points": [v(-8.75, 48.33) * mm, v(-9.11, 47.6) * mm, v(-9.13, 47.26) * mm, v(-8.87, 46.45) * mm]});
            skFitSpline(sketch, "E2579", {"points": [v(-8.87, 46.45) * mm, v(-8.5, 45.32) * mm, v(-8.12, 45.18) * mm, v(-7.93, 46.1) * mm]});
            skFitSpline(sketch, "E2580", {"points": [v(-7.93, 46.1) * mm, v(-7.86, 46.45) * mm, v(-7.87, 45.88) * mm, v(-7.95, 44.82) * mm]});
            skFitSpline(sketch, "E2581", {"points": [v(-7.95, 44.82) * mm, v(-8.09, 43.11) * mm, v(-8.03, 42.84) * mm, v(-7.47, 42.24) * mm]});
            skFitSpline(sketch, "E2582", {"points": [v(-7.47, 42.24) * mm, v(-6.42, 41.12) * mm, v(-5.36, 40.81) * mm, v(-4.05, 41.24) * mm]});
            skFitSpline(sketch, "E2583", {"points": [v(-4.05, 41.24) * mm, v(-3.44, 41.44) * mm, v(-2.86, 41.52) * mm, v(-2.75, 41.42) * mm]});
            skFitSpline(sketch, "E2584", {"points": [v(-2.75, 41.42) * mm, v(-2.65, 41.32) * mm, v(-2.84, 41.23) * mm, v(-3.18, 41.23) * mm]});
            skFitSpline(sketch, "E2585", {"points": [v(-3.18, 41.23) * mm, v(-3.51, 41.23) * mm, v(-3.79, 41.1) * mm, v(-3.79, 40.95) * mm]});
            skFitSpline(sketch, "E2586", {"points": [v(-3.79, 40.95) * mm, v(-3.79, 40.8) * mm, v(-4.25, 40.67) * mm, v(-4.8, 40.67) * mm]});
            skFitSpline(sketch, "E2587", {"points": [v(-4.8, 40.67) * mm, v(-5.98, 40.67) * mm, v(-8.02, 41.7) * mm, v(-8.02, 42.3) * mm]});
            skFitSpline(sketch, "E2588", {"points": [v(-8.02, 42.3) * mm, v(-8.02, 42.56) * mm, v(-8.19, 42.64) * mm, v(-8.49, 42.53) * mm]});
            skFitSpline(sketch, "E2589", {"points": [v(-8.49, 42.53) * mm, v(-8.87, 42.38) * mm, v(-8.89, 42.42) * mm, v(-8.6, 42.78) * mm]});
            skFitSpline(sketch, "E2590", {"points": [v(-8.6, 42.78) * mm, v(-8.38, 43.03) * mm, v(-8.32, 43.5) * mm, v(-8.43, 43.94) * mm]});
            skFitSpline(sketch, "E2591", {"points": [v(-8.43, 43.94) * mm, v(-8.61, 44.68) * mm, v(-8.62, 44.68) * mm, v(-9.23, 44.16) * mm]});
            skFitSpline(sketch, "E2592", {"points": [v(-9.23, 44.16) * mm, v(-9.69, 43.77) * mm, v(-9.75, 43.76) * mm, v(-9.49, 44.1) * mm]});
            skFitSpline(sketch, "E2593", {"points": [v(-9.49, 44.1) * mm, v(-9.18, 44.5) * mm, v(-9.22, 44.63) * mm, v(-9.7, 44.97) * mm]});
            skFitSpline(sketch, "E2594", {"points": [v(-9.7, 44.97) * mm, v(-10.02, 45.2) * mm, v(-10.18, 45.5) * mm, v(-10.07, 45.63) * mm]});
            skFitSpline(sketch, "E2595", {"points": [v(-10.07, 45.63) * mm, v(-9.95, 45.77) * mm, v(-10.16, 45.63) * mm, v(-10.53, 45.32) * mm]});
            skFitSpline(sketch, "E2596", {"points": [v(-10.53, 45.32) * mm, v(-10.9, 45.01) * mm, v(-11.43, 44.4) * mm, v(-11.7, 43.97) * mm]});
            skFitSpline(sketch, "E2597", {"points": [v(-11.7, 43.97) * mm, v(-12.18, 43.19) * mm, v(-12.17, 43.15) * mm, v(-11.5, 42.48) * mm]});
            skFitSpline(sketch, "E2598", {"points": [v(-11.5, 42.48) * mm, v(-11.13, 42.1) * mm, v(-10.58, 41.8) * mm, v(-10.29, 41.8) * mm]});
            skFitSpline(sketch, "E2599", {"points": [v(-10.29, 41.8) * mm, v(-10, 41.8) * mm, v(-9.52, 41.5) * mm, v(-9.24, 41.14) * mm]});
            skFitSpline(sketch, "E2600", {"points": [v(-9.24, 41.14) * mm, v(-8.95, 40.78) * mm, v(-8.34, 40.34) * mm, v(-7.88, 40.17) * mm]});
            skFitSpline(sketch, "E2601", {"points": [v(-7.88, 40.17) * mm, v(-6.59, 39.7) * mm, v(-3.63, 39.76) * mm, v(-2.44, 40.28) * mm]});
            skFitSpline(sketch, "E2602", {"points": [v(-1.81, 41.9) * mm, v(-1.81, 41.97) * mm, v(-1.62, 42.1) * mm, v(-1.38, 42.19) * mm]});
            skFitSpline(sketch, "E2603", {"points": [v(-1.38, 42.19) * mm, v(-1.12, 42.29) * mm, v(-1.01, 42.24) * mm, v(-1.1, 42.08) * mm]});
            skFitSpline(sketch, "E2604", {"points": [v(-1.1, 42.08) * mm, v(-1.28, 41.8) * mm, v(-1.81, 41.68) * mm, v(-1.81, 41.9) * mm]});
            skFitSpline(sketch, "E2605", {"points": [v(-4.2, 43.19) * mm, v(-4.34, 43.63) * mm, v(-4.18, 44.26) * mm, v(-3.67, 45.24) * mm]});
            skFitSpline(sketch, "E2606", {"points": [v(-3.67, 45.24) * mm, v(-2.96, 46.61) * mm, v(-2.72, 47.62) * mm, v(-3.17, 47.34) * mm]});
            skFitSpline(sketch, "E2607", {"points": [v(-3.17, 47.34) * mm, v(-3.29, 47.26) * mm, v(-3.34, 47.6) * mm, v(-3.28, 48.1) * mm]});
            skFitSpline(sketch, "E2608", {"points": [v(-3.28, 48.1) * mm, v(-3.23, 48.6) * mm, v(-3.42, 49.63) * mm, v(-3.73, 50.4) * mm]});
            skFitSpline(sketch, "E2609", {"points": [v(-3.73, 50.4) * mm, v(-4.03, 51.18) * mm, v(-4.22, 51.97) * mm, v(-4.15, 52.16) * mm]});
            skFitSpline(sketch, "E2610", {"points": [v(-4.15, 52.16) * mm, v(-4.02, 52.55) * mm, v(-4.84, 52.45) * mm, v(-5.73, 51.98) * mm]});
            skFitSpline(sketch, "E2611", {"points": [v(-5.73, 51.98) * mm, v(-6.83, 51.4) * mm, v(-6.74, 51.7) * mm, v(-5.63, 52.32) * mm]});
            skFitSpline(sketch, "E2612", {"points": [v(-5.63, 52.32) * mm, v(-5, 52.67) * mm, v(-4.45, 53.2) * mm, v(-4.4, 53.5) * mm]});
            skFitSpline(sketch, "E2613", {"points": [v(-4.4, 53.5) * mm, v(-4.3, 54) * mm, v(-4.34, 54.02) * mm, v(-4.81, 53.65) * mm]});
            skFitSpline(sketch, "E2614", {"points": [v(-4.81, 53.65) * mm, v(-5.31, 53.26) * mm, v(-5.32, 53.27) * mm, v(-4.88, 53.8) * mm]});
            skFitSpline(sketch, "E2615", {"points": [v(-4.88, 53.8) * mm, v(-4.63, 54.1) * mm, v(-4.36, 54.55) * mm, v(-4.27, 54.78) * mm]});
            skFitSpline(sketch, "E2616", {"points": [v(-4.27, 54.78) * mm, v(-4.19, 55.01) * mm, v(-4.1, 54.68) * mm, v(-4.1, 54.03) * mm]});
            skFitSpline(sketch, "E2617", {"points": [v(-4.1, 54.03) * mm, v(-4.08, 53.4) * mm, v(-3.8, 52) * mm, v(-3.47, 50.93) * mm]});
            skFitSpline(sketch, "E2618", {"points": [v(-3.47, 50.93) * mm, v(-2.57, 48.02) * mm, v(-2.36, 46.03) * mm, v(-2.87, 45.26) * mm]});
            skFitSpline(sketch, "E2619", {"points": [v(-2.87, 45.26) * mm, v(-3.1, 44.9) * mm, v(-3.45, 44.15) * mm, v(-3.65, 43.58) * mm]});
            skFitSpline(sketch, "E2620", {"points": [v(-3.65, 43.58) * mm, v(-3.97, 42.63) * mm, v(-4.02, 42.6) * mm, v(-4.2, 43.19) * mm]});
            skFitSpline(sketch, "E2621", {"points": [v(-2.66, 46.25) * mm, v(-2.66, 46.36) * mm, v(-2.92, 46.07) * mm, v(-3.22, 45.6) * mm]});
            skFitSpline(sketch, "E2622", {"points": [v(-3.22, 45.6) * mm, v(-3.53, 45.14) * mm, v(-3.79, 44.64) * mm, v(-3.79, 44.48) * mm]});
            skFitSpline(sketch, "E2623", {"points": [v(-3.79, 44.48) * mm, v(-3.79, 44.32) * mm, v(-3.53, 44.61) * mm, v(-3.22, 45.12) * mm]});
            skFitSpline(sketch, "E2624", {"points": [v(-3.22, 45.12) * mm, v(-2.91, 45.63) * mm, v(-2.66, 46.14) * mm, v(-2.66, 46.25) * mm]});
            skFitSpline(sketch, "E2625", {"points": [v(-2.33, 44.34) * mm, v(-2.33, 44.73) * mm, v(-2.27, 44.89) * mm, v(-2.2, 44.7) * mm]});
            skFitSpline(sketch, "E2626", {"points": [v(-2.2, 44.7) * mm, v(-2.11, 44.5) * mm, v(-2.11, 44.18) * mm, v(-2.2, 43.99) * mm]});
            skFitSpline(sketch, "E2627", {"points": [v(-2.2, 43.99) * mm, v(-2.27, 43.8) * mm, v(-2.33, 43.95) * mm, v(-2.33, 44.34) * mm]});
            skFitSpline(sketch, "E2628", {"points": [v(-6.47, 46.6) * mm, v(-6.19, 46.9) * mm, v(-5.9, 47.16) * mm, v(-5.82, 47.16) * mm]});
            skFitSpline(sketch, "E2629", {"points": [v(-5.82, 47.16) * mm, v(-5.74, 47.16) * mm, v(-5.9, 46.9) * mm, v(-6.19, 46.6) * mm]});
            skFitSpline(sketch, "E2630", {"points": [v(-6.19, 46.6) * mm, v(-6.47, 46.29) * mm, v(-6.76, 46.03) * mm, v(-6.84, 46.03) * mm]});
            skFitSpline(sketch, "E2631", {"points": [v(-6.84, 46.03) * mm, v(-6.92, 46.03) * mm, v(-6.75, 46.29) * mm, v(-6.47, 46.6) * mm]});
            skFitSpline(sketch, "E2632", {"points": [v(-1.71, 46.45) * mm, v(-1.8, 46.69) * mm, v(-1.99, 46.8) * mm, v(-2.12, 46.72) * mm]});
            skFitSpline(sketch, "E2633", {"points": [v(-2.12, 46.72) * mm, v(-2.26, 46.63) * mm, v(-2.38, 46.7) * mm, v(-2.38, 46.86) * mm]});
            skFitSpline(sketch, "E2634", {"points": [v(-2.38, 46.86) * mm, v(-2.38, 47.36) * mm, v(-1.85, 47.2) * mm, v(-1.53, 46.6) * mm]});
            skFitSpline(sketch, "E2635", {"points": [v(-1.53, 46.6) * mm, v(-1.36, 46.29) * mm, v(-1.3, 46.03) * mm, v(-1.39, 46.03) * mm]});
            skFitSpline(sketch, "E2636", {"points": [v(-1.39, 46.03) * mm, v(-1.48, 46.03) * mm, v(-1.62, 46.22) * mm, v(-1.71, 46.45) * mm]});
            skFitSpline(sketch, "E2637", {"points": [v(0.04, 46.51) * mm, v(-0.11, 46.92) * mm, v(-0.08, 46.95) * mm, v(0.2, 46.67) * mm]});
            skFitSpline(sketch, "E2638", {"points": [v(0.2, 46.67) * mm, v(0.4, 46.48) * mm, v(0.48, 46.25) * mm, v(0.4, 46.17) * mm]});
            skFitSpline(sketch, "E2639", {"points": [v(0.4, 46.17) * mm, v(0.3, 46.08) * mm, v(0.15, 46.24) * mm, v(0.04, 46.51) * mm]});
            skFitSpline(sketch, "E2640", {"points": [v(-1.35, 47.04) * mm, v(-1.8, 47.43) * mm, v(-2.1, 47.81) * mm, v(-2.04, 47.88) * mm]});
            skFitSpline(sketch, "E2641", {"points": [v(-2.04, 47.88) * mm, v(-1.97, 47.95) * mm, v(-1.55, 47.62) * mm, v(-1.1, 47.16) * mm]});
            skFitSpline(sketch, "E2642", {"points": [v(-1.1, 47.16) * mm, v(-0.12, 46.13) * mm, v(-0.25, 46.07) * mm, v(-1.35, 47.04) * mm]});
            skFitSpline(sketch, "E2643", {"points": [v(-0.97, 47.75) * mm, v(-1.57, 48.25) * mm, v(-1.59, 48.29) * mm, v(-1.05, 48.03) * mm]});
            skFitSpline(sketch, "E2644", {"points": [v(-1.05, 48.03) * mm, v(-0.71, 47.86) * mm, v(-0.36, 47.6) * mm, v(-0.26, 47.44) * mm]});
            skFitSpline(sketch, "E2645", {"points": [v(-0.26, 47.44) * mm, v(0, 47.03) * mm, v(-0.18, 47.1) * mm, v(-0.97, 47.75) * mm]});
            skFitSpline(sketch, "E2646", {"points": [v(-4.64, 47.83) * mm, v(-4.64, 47.9) * mm, v(-4.41, 48.11) * mm, v(-4.14, 48.33) * mm]});
            skFitSpline(sketch, "E2647", {"points": [v(-4.14, 48.33) * mm, v(-3.7, 48.68) * mm, v(-3.68, 48.67) * mm, v(-4.03, 48.22) * mm]});
            skFitSpline(sketch, "E2648", {"points": [v(-4.03, 48.22) * mm, v(-4.4, 47.75) * mm, v(-4.64, 47.6) * mm, v(-4.64, 47.83) * mm]});
            skFitSpline(sketch, "E2649", {"points": [v(-2.19, 48.48) * mm, v(-2.58, 48.87) * mm, v(-2.37, 49.7) * mm, v(-1.88, 49.7) * mm]});
            skFitSpline(sketch, "E2650", {"points": [v(-1.88, 49.7) * mm, v(-1.5, 49.7) * mm, v(-1.47, 49.64) * mm, v(-1.77, 49.45) * mm]});
            skFitSpline(sketch, "E2651", {"points": [v(-1.77, 49.45) * mm, v(-2.1, 49.24) * mm, v(-2.1, 49.18) * mm, v(-1.77, 49.05) * mm]});
            skFitSpline(sketch, "E2652", {"points": [v(-1.77, 49.05) * mm, v(-1.47, 48.93) * mm, v(-1.47, 48.9) * mm, v(-1.76, 48.88) * mm]});
            skFitSpline(sketch, "E2653", {"points": [v(-1.76, 48.88) * mm, v(-1.96, 48.86) * mm, v(-2.05, 48.73) * mm, v(-1.95, 48.57) * mm]});
            skFitSpline(sketch, "E2654", {"points": [v(-1.95, 48.57) * mm, v(-1.76, 48.25) * mm, v(-1.9, 48.2) * mm, v(-2.19, 48.48) * mm]});
            skFitSpline(sketch, "E2655", {"points": [v(-4.78, 49.14) * mm, v(-4.5, 49.45) * mm, v(-4.2, 49.7) * mm, v(-4.12, 49.7) * mm]});
            skFitSpline(sketch, "E2656", {"points": [v(-4.12, 49.7) * mm, v(-4.05, 49.7) * mm, v(-4.21, 49.45) * mm, v(-4.5, 49.14) * mm]});
            skFitSpline(sketch, "E2657", {"points": [v(-4.5, 49.14) * mm, v(-4.78, 48.83) * mm, v(-5.07, 48.57) * mm, v(-5.15, 48.57) * mm]});
            skFitSpline(sketch, "E2658", {"points": [v(-5.15, 48.57) * mm, v(-5.22, 48.57) * mm, v(-5.06, 48.83) * mm, v(-4.78, 49.14) * mm]});
            skFitSpline(sketch, "E2659", {"points": [v(-8.02, 48.96) * mm, v(-8.02, 49.02) * mm, v(-7.8, 49.24) * mm, v(-7.53, 49.45) * mm]});
            skFitSpline(sketch, "E2660", {"points": [v(-7.53, 49.45) * mm, v(-7.08, 49.8) * mm, v(-7.07, 49.8) * mm, v(-7.42, 49.35) * mm]});
            skFitSpline(sketch, "E2661", {"points": [v(-7.42, 49.35) * mm, v(-7.8, 48.88) * mm, v(-8.02, 48.73) * mm, v(-8.02, 48.96) * mm]});
            skLineSegment(sketch, "E2662", {"start": v(0, 49.77) * mm, "end": v(-0.54, 50.4) * mm});
            skLineSegment(sketch, "E2663", {"start": v(-0.54, 50.4) * mm, "end": v(0.1, 49.87) * mm});
            skFitSpline(sketch, "E2664", {"points": [v(0.1, 49.87) * mm, v(0.69, 49.36) * mm, v(0.86, 49.14) * mm, v(0.63, 49.14) * mm]});
            skFitSpline(sketch, "E2665", {"points": [v(0.63, 49.14) * mm, v(0.58, 49.14) * mm, v(0.3, 49.42) * mm, v(0, 49.77) * mm]});
            skFitSpline(sketch, "E2666", {"points": [v(1.62, 49.7) * mm, v(1.62, 50.09) * mm, v(1.68, 50.25) * mm, v(1.76, 50.05) * mm]});
            skFitSpline(sketch, "E2667", {"points": [v(1.76, 50.05) * mm, v(1.84, 49.86) * mm, v(1.84, 49.54) * mm, v(1.76, 49.35) * mm]});
            skFitSpline(sketch, "E2668", {"points": [v(1.76, 49.35) * mm, v(1.68, 49.15) * mm, v(1.62, 49.31) * mm, v(1.62, 49.7) * mm]});
            skFitSpline(sketch, "E2669", {"points": [v(-4.92, 49.8) * mm, v(-4.92, 49.87) * mm, v(-4.7, 50.09) * mm, v(-4.42, 50.3) * mm]});
            skFitSpline(sketch, "E2670", {"points": [v(-4.42, 50.3) * mm, v(-3.98, 50.65) * mm, v(-3.97, 50.64) * mm, v(-4.32, 50.2) * mm]});
            skFitSpline(sketch, "E2671", {"points": [v(-4.32, 50.2) * mm, v(-4.69, 49.72) * mm, v(-4.92, 49.58) * mm, v(-4.92, 49.8) * mm]});
            skFitSpline(sketch, "E2672", {"points": [v(-1.74, 50.83) * mm, v(-2.36, 51.2) * mm, v(-2.66, 51.27) * mm, v(-2.66, 51.04) * mm]});
            skFitSpline(sketch, "E2673", {"points": [v(-2.66, 51.04) * mm, v(-2.67, 50.56) * mm, v(-3.21, 51.42) * mm, v(-3.22, 51.91) * mm]});
            skFitSpline(sketch, "E2674", {"points": [v(-3.22, 51.91) * mm, v(-3.22, 52.16) * mm, v(-2.95, 52.07) * mm, v(-2.42, 51.63) * mm]});
            skFitSpline(sketch, "E2675", {"points": [v(-2.42, 51.63) * mm, v(-1.97, 51.27) * mm, v(-1.37, 50.82) * mm, v(-1.07, 50.63) * mm]});
            skFitSpline(sketch, "E2676", {"points": [v(-1.07, 50.63) * mm, v(-0.78, 50.45) * mm, v(-0.6, 50.3) * mm, v(-0.68, 50.28) * mm]});
            skFitSpline(sketch, "E2677", {"points": [v(-0.68, 50.28) * mm, v(-0.76, 50.27) * mm, v(-1.24, 50.52) * mm, v(-1.74, 50.83) * mm]});
            skFitSpline(sketch, "E2678", {"points": [v(1.05, 51.32) * mm, v(0.74, 52.04) * mm, v(0.75, 52.06) * mm, v(1.15, 51.55) * mm]});
            skFitSpline(sketch, "E2679", {"points": [v(1.15, 51.55) * mm, v(1.38, 51.25) * mm, v(1.57, 50.9) * mm, v(1.57, 50.78) * mm]});
            skFitSpline(sketch, "E2680", {"points": [v(1.57, 50.78) * mm, v(1.57, 50.35) * mm, v(1.38, 50.55) * mm, v(1.05, 51.32) * mm]});
            skFitSpline(sketch, "E2681", {"points": [v(-6.68, 52.73) * mm, v(-6.31, 53.08) * mm, v(-5.86, 53.37) * mm, v(-5.68, 53.36) * mm]});
            skFitSpline(sketch, "E2682", {"points": [v(-5.68, 53.36) * mm, v(-5.5, 53.36) * mm, v(-5.6, 53.21) * mm, v(-5.9, 53.04) * mm]});
            skFitSpline(sketch, "E2683", {"points": [v(-5.9, 53.04) * mm, v(-6.22, 52.87) * mm, v(-6.67, 52.59) * mm, v(-6.9, 52.41) * mm]});
            skFitSpline(sketch, "E2684", {"points": [v(-6.9, 52.41) * mm, v(-7.15, 52.24) * mm, v(-7.05, 52.39) * mm, v(-6.68, 52.73) * mm]});
            skFitSpline(sketch, "E2685", {"points": [v(-3.47, 53.8) * mm, v(-3.49, 54.57) * mm, v(-3.37, 55.4) * mm, v(-3.22, 55.63) * mm]});
            skFitSpline(sketch, "E2686", {"points": [v(-3.22, 55.63) * mm, v(-3, 55.96) * mm, v(-2.95, 55.9) * mm, v(-2.96, 55.35) * mm]});
            skFitSpline(sketch, "E2687", {"points": [v(-2.96, 55.35) * mm, v(-2.97, 54.96) * mm, v(-3.08, 54.13) * mm, v(-3.2, 53.51) * mm]});
            skLineSegment(sketch, "E2688", {"start": v(-3.2, 53.51) * mm, "end": v(-3.44, 52.38) * mm});
            skLineSegment(sketch, "E2689", {"start": v(-3.44, 52.38) * mm, "end": v(-3.47, 53.8) * mm});
            skLineSegment(sketch, "E2690", {"start": v(-1.42, 54.29) * mm, "end": v(-1.95, 54.92) * mm});
            skLineSegment(sketch, "E2691", {"start": v(-1.95, 54.92) * mm, "end": v(-1.32, 54.38) * mm});
            skFitSpline(sketch, "E2692", {"points": [v(-1.32, 54.38) * mm, v(-0.72, 53.88) * mm, v(-0.56, 53.65) * mm, v(-0.78, 53.65) * mm]});
            skFitSpline(sketch, "E2693", {"points": [v(-0.78, 53.65) * mm, v(-0.84, 53.65) * mm, v(-1.12, 53.94) * mm, v(-1.42, 54.29) * mm]});
            skLineSegment(sketch, "E2694", {"start": v(-0.14, 55) * mm, "end": v(-0.83, 55.77) * mm});
            skLineSegment(sketch, "E2695", {"start": v(-0.83, 55.77) * mm, "end": v(-0.05, 55.08) * mm});
            skFitSpline(sketch, "E2696", {"points": [v(-0.05, 55.08) * mm, v(0.68, 54.45) * mm, v(0.86, 54.22) * mm, v(0.63, 54.22) * mm]});
            skFitSpline(sketch, "E2697", {"points": [v(0.63, 54.22) * mm, v(0.58, 54.22) * mm, v(0.24, 54.57) * mm, v(-0.14, 55) * mm]});
            skFitSpline(sketch, "E2698", {"points": [v(0.73, 55.06) * mm, v(0.4, 55.53) * mm, v(0.19, 55.9) * mm, v(0.27, 55.9) * mm]});
            skFitSpline(sketch, "E2699", {"points": [v(0.27, 55.9) * mm, v(0.34, 55.9) * mm, v(0.68, 55.53) * mm, v(1, 55.06) * mm]});
            skFitSpline(sketch, "E2700", {"points": [v(1, 55.06) * mm, v(1.34, 54.6) * mm, v(1.55, 54.22) * mm, v(1.47, 54.22) * mm]});
            skFitSpline(sketch, "E2701", {"points": [v(1.47, 54.22) * mm, v(1.4, 54.22) * mm, v(1.06, 54.6) * mm, v(0.73, 55.06) * mm]});
            skLineSegment(sketch, "E2702", {"start": v(0.84, 56.26) * mm, "end": v(0.3, 56.9) * mm});
            skLineSegment(sketch, "E2703", {"start": v(0.3, 56.9) * mm, "end": v(0.94, 56.36) * mm});
            skFitSpline(sketch, "E2704", {"points": [v(0.94, 56.36) * mm, v(1.54, 55.85) * mm, v(1.7, 55.63) * mm, v(1.48, 55.63) * mm]});
            skFitSpline(sketch, "E2705", {"points": [v(1.48, 55.63) * mm, v(1.42, 55.63) * mm, v(1.14, 55.91) * mm, v(0.84, 56.26) * mm]});
            skFitSpline(sketch, "E2706", {"points": [v(-0.97, 56.33) * mm, v(-1.35, 56.56) * mm, v(-1.54, 56.74) * mm, v(-1.37, 56.75) * mm]});
            skFitSpline(sketch, "E2707", {"points": [v(-1.37, 56.75) * mm, v(-1.2, 56.75) * mm, v(-0.83, 56.57) * mm, v(-0.53, 56.34) * mm]});
            skFitSpline(sketch, "E2708", {"points": [v(-0.53, 56.34) * mm, v(0.17, 55.82) * mm, v(-0.05, 55.81) * mm, v(-0.97, 56.33) * mm]});
            skFitSpline(sketch, "E2709", {"points": [v(6.56, 40.12) * mm, v(7, 40.29) * mm, v(7.65, 40.73) * mm, v(8, 41.1) * mm]});
            skFitSpline(sketch, "E2710", {"points": [v(8, 41.1) * mm, v(8.36, 41.49) * mm, v(8.9, 41.8) * mm, v(9.21, 41.8) * mm]});
            skFitSpline(sketch, "E2711", {"points": [v(9.21, 41.8) * mm, v(9.52, 41.8) * mm, v(9.85, 41.98) * mm, v(9.93, 42.21) * mm]});
            skFitSpline(sketch, "E2712", {"points": [v(9.93, 42.21) * mm, v(10.02, 42.44) * mm, v(10.34, 42.7) * mm, v(10.63, 42.8) * mm]});
            skFitSpline(sketch, "E2713", {"points": [v(10.63, 42.8) * mm, v(11.15, 42.96) * mm, v(11.13, 43.03) * mm, v(10.4, 44.07) * mm]});
            skFitSpline(sketch, "E2714", {"points": [v(10.4, 44.07) * mm, v(9.5, 45.35) * mm, v(9.28, 45.46) * mm, v(8.25, 45.26) * mm]});
            skFitSpline(sketch, "E2715", {"points": [v(8.25, 45.26) * mm, v(7.6, 45.14) * mm, v(7.54, 45.05) * mm, v(7.84, 44.66) * mm]});
            skFitSpline(sketch, "E2716", {"points": [v(7.84, 44.66) * mm, v(8.1, 44.33) * mm, v(8.02, 44.35) * mm, v(7.58, 44.72) * mm]});
            skFitSpline(sketch, "E2717", {"points": [v(7.58, 44.72) * mm, v(6.87, 45.32) * mm, v(6.26, 45.09) * mm, v(6.47, 44.3) * mm]});
            skFitSpline(sketch, "E2718", {"points": [v(6.47, 44.3) * mm, v(6.58, 43.84) * mm, v(6.54, 43.8) * mm, v(6.2, 44.08) * mm]});
            skFitSpline(sketch, "E2719", {"points": [v(6.2, 44.08) * mm, v(5.82, 44.4) * mm, v(5.68, 44.24) * mm, v(5.8, 43.63) * mm]});
            skFitSpline(sketch, "E2720", {"points": [v(5.8, 43.63) * mm, v(5.82, 43.48) * mm, v(5.69, 43.5) * mm, v(5.49, 43.7) * mm]});
            skFitSpline(sketch, "E2721", {"points": [v(5.49, 43.7) * mm, v(5.07, 44.12) * mm, v(3.59, 44.17) * mm, v(2.65, 43.8) * mm]});
            skFitSpline(sketch, "E2722", {"points": [v(2.65, 43.8) * mm, v(2.3, 43.66) * mm, v(1.43, 43) * mm, v(0.75, 42.33) * mm]});
            skLineSegment(sketch, "E2723", {"start": v(0.75, 42.33) * mm, "end": v(-0.5, 41.12) * mm});
            skLineSegment(sketch, "E2724", {"start": v(-0.5, 41.12) * mm, "end": v(0.89, 40.47) * mm});
            skFitSpline(sketch, "E2725", {"points": [v(0.89, 40.47) * mm, v(2.42, 39.77) * mm, v(5.16, 39.6) * mm, v(6.56, 40.12) * mm]});
            skFitSpline(sketch, "E2726", {"points": [v(6.09, 42.65) * mm, v(5.92, 42.96) * mm, v(5.85, 43.2) * mm, v(5.93, 43.2) * mm]});
            skFitSpline(sketch, "E2727", {"points": [v(5.93, 43.2) * mm, v(6, 43.2) * mm, v(6.2, 42.96) * mm, v(6.37, 42.65) * mm]});
            skFitSpline(sketch, "E2728", {"points": [v(6.37, 42.65) * mm, v(6.54, 42.34) * mm, v(6.6, 42.08) * mm, v(6.53, 42.08) * mm]});
            skFitSpline(sketch, "E2729", {"points": [v(6.53, 42.08) * mm, v(6.45, 42.08) * mm, v(6.26, 42.34) * mm, v(6.09, 42.65) * mm]});
            skFitSpline(sketch, "E2730", {"points": [v(7.3, 43.84) * mm, v(6.87, 44.4) * mm, v(6.6, 44.9) * mm, v(6.75, 44.9) * mm]});
            skFitSpline(sketch, "E2731", {"points": [v(6.75, 44.9) * mm, v(6.81, 44.9) * mm, v(7.08, 44.59) * mm, v(7.33, 44.2) * mm]});
            skFitSpline(sketch, "E2732", {"points": [v(7.33, 44.2) * mm, v(7.8, 43.47) * mm, v(7.78, 43.22) * mm, v(7.3, 43.84) * mm]});
            skFitSpline(sketch, "E2733", {"points": [v(-32.83, 41.58) * mm, v(-34.33, 42.91) * mm, v(-34.9, 42.34) * mm, v(-33.5, 40.93) * mm]});
            skFitSpline(sketch, "E2734", {"points": [v(-33.5, 40.93) * mm, v(-32.9, 40.33) * mm, v(-32.63, 40.22) * mm, v(-32.33, 40.47) * mm]});
            skFitSpline(sketch, "E2735", {"points": [v(-32.33, 40.47) * mm, v(-32.02, 40.73) * mm, v(-32.11, 40.93) * mm, v(-32.83, 41.58) * mm]});
            skFitSpline(sketch, "E2736", {"points": [v(-13.3, 42.2) * mm, v(-12.83, 43.04) * mm, v(-12.73, 43.4) * mm, v(-13, 43.3) * mm]});
            skFitSpline(sketch, "E2737", {"points": [v(-13, 43.3) * mm, v(-13.6, 43.07) * mm, v(-14.6, 40.95) * mm, v(-14.11, 40.95) * mm]});
            skFitSpline(sketch, "E2738", {"points": [v(-14.11, 40.95) * mm, v(-14.05, 40.95) * mm, v(-13.68, 41.51) * mm, v(-13.3, 42.2) * mm]});
            skFitSpline(sketch, "E2739", {"points": [v(-18.14, 44.82) * mm, v(-17.72, 45.18) * mm, v(-17.58, 45.17) * mm, v(-16.92, 44.74) * mm]});
            skFitSpline(sketch, "E2740", {"points": [v(-16.92, 44.74) * mm, v(-16.33, 44.35) * mm, v(-15.8, 44.3) * mm, v(-14.23, 44.42) * mm]});
            skFitSpline(sketch, "E2741", {"points": [v(-14.23, 44.42) * mm, v(-12.14, 44.6) * mm, v(-11.3, 44.92) * mm, v(-10.88, 45.69) * mm]});
            skFitSpline(sketch, "E2742", {"points": [v(-10.88, 45.69) * mm, v(-10.65, 46.12) * mm, v(-10.76, 46.16) * mm, v(-11.86, 46.07) * mm]});
            skFitSpline(sketch, "E2743", {"points": [v(-11.86, 46.07) * mm, v(-12.55, 46.02) * mm, v(-13.33, 46.07) * mm, v(-13.6, 46.19) * mm]});
            skFitSpline(sketch, "E2744", {"points": [v(-13.6, 46.19) * mm, v(-14.17, 46.44) * mm, v(-14.15, 46.44) * mm, v(-15.08, 46.2) * mm]});
            skLineSegment(sketch, "E2745", {"start": v(-15.08, 46.2) * mm, "end": v(-15.78, 46.01) * mm});
            skLineSegment(sketch, "E2746", {"start": v(-15.78, 46.01) * mm, "end": v(-15.04, 46.44) * mm});
            skFitSpline(sketch, "E2747", {"points": [v(-15.04, 46.44) * mm, v(-14.64, 46.67) * mm, v(-14.23, 47.13) * mm, v(-14.14, 47.47) * mm]});
            skFitSpline(sketch, "E2748", {"points": [v(-14.14, 47.47) * mm, v(-13.99, 48.06) * mm, v(-14.04, 48.07) * mm, v(-15.57, 47.9) * mm]});
            skFitSpline(sketch, "E2749", {"points": [v(-15.57, 47.9) * mm, v(-16.44, 47.8) * mm, v(-17.73, 47.45) * mm, v(-18.44, 47.14) * mm]});
            skFitSpline(sketch, "E2750", {"points": [v(-18.44, 47.14) * mm, v(-19.15, 46.82) * mm, v(-19.58, 46.72) * mm, v(-19.4, 46.9) * mm]});
            skFitSpline(sketch, "E2751", {"points": [v(-19.4, 46.9) * mm, v(-19.22, 47.08) * mm, v(-18.41, 47.46) * mm, v(-17.61, 47.73) * mm]});
            skLineSegment(sketch, "E2752", {"start": v(-17.61, 47.73) * mm, "end": v(-16.16, 48.22) * mm});
            skLineSegment(sketch, "E2753", {"start": v(-16.16, 48.22) * mm, "end": v(-17.17, 48.4) * mm});
            skFitSpline(sketch, "E2754", {"points": [v(-17.17, 48.4) * mm, v(-17.73, 48.51) * mm, v(-18.18, 48.69) * mm, v(-18.18, 48.8) * mm]});
            skFitSpline(sketch, "E2755", {"points": [v(-18.18, 48.8) * mm, v(-18.18, 48.9) * mm, v(-18.97, 48.98) * mm, v(-19.95, 48.97) * mm]});
            skLineSegment(sketch, "E2756", {"start": v(-19.95, 48.97) * mm, "end": v(-21.7, 48.95) * mm});
            skLineSegment(sketch, "E2757", {"start": v(-21.7, 48.95) * mm, "end": v(-20.09, 49.05) * mm});
            skFitSpline(sketch, "E2758", {"points": [v(-20.09, 49.05) * mm, v(-18.62, 49.15) * mm, v(-18.46, 49.23) * mm, v(-18.46, 49.8) * mm]});
            skFitSpline(sketch, "E2759", {"points": [v(-18.46, 49.8) * mm, v(-18.46, 50.61) * mm, v(-18.97, 51.11) * mm, v(-19.78, 51.11) * mm]});
            skFitSpline(sketch, "E2760", {"points": [v(-19.78, 51.11) * mm, v(-20.2, 51.11) * mm, v(-20.37, 50.98) * mm, v(-20.27, 50.73) * mm]});
            skFitSpline(sketch, "E2761", {"points": [v(-20.27, 50.73) * mm, v(-20.16, 50.42) * mm, v(-20.4, 50.39) * mm, v(-21.57, 50.57) * mm]});
            skFitSpline(sketch, "E2762", {"points": [v(-21.57, 50.57) * mm, v(-22.89, 50.78) * mm, v(-24.4, 50.54) * mm, v(-24.4, 50.12) * mm]});
            skFitSpline(sketch, "E2763", {"points": [v(-24.4, 50.12) * mm, v(-24.4, 50.03) * mm, v(-24.19, 49.56) * mm, v(-23.94, 49.09) * mm]});
            skLineSegment(sketch, "E2764", {"start": v(-23.94, 49.09) * mm, "end": v(-23.5, 48.22) * mm});
            skLineSegment(sketch, "E2765", {"start": v(-23.5, 48.22) * mm, "end": v(-24.36, 48.35) * mm});
            skFitSpline(sketch, "E2766", {"points": [v(-24.36, 48.35) * mm, v(-25.18, 48.47) * mm, v(-25.2, 48.44) * mm, v(-24.78, 47.97) * mm]});
            skFitSpline(sketch, "E2767", {"points": [v(-24.78, 47.97) * mm, v(-24.17, 47.3) * mm, v(-23.02, 47.09) * mm, v(-21.62, 47.4) * mm]});
            skFitSpline(sketch, "E2768", {"points": [v(-21.62, 47.4) * mm, v(-20.29, 47.7) * mm, v(-20.04, 47.35) * mm, v(-21, 46.52) * mm]});
            skFitSpline(sketch, "E2769", {"points": [v(-21, 46.52) * mm, v(-21.87, 45.78) * mm, v(-21.72, 44.94) * mm, v(-20.65, 44.48) * mm]});
            skFitSpline(sketch, "E2770", {"points": [v(-20.65, 44.48) * mm, v(-19.67, 44.05) * mm, v(-18.89, 44.16) * mm, v(-18.14, 44.82) * mm]});
            skFitSpline(sketch, "E2771", {"points": [v(14.67, 45.36) * mm, v(15.27, 45.58) * mm, v(15.24, 46.22) * mm, v(14.63, 46.57) * mm]});
            skFitSpline(sketch, "E2772", {"points": [v(14.63, 46.57) * mm, v(13.62, 47.16) * mm, v(14.75, 46.85) * mm, v(16.09, 46.17) * mm]});
            skFitSpline(sketch, "E2773", {"points": [v(16.09, 46.17) * mm, v(17.43, 45.49) * mm, v(19.17, 45.26) * mm, v(19.8, 45.68) * mm]});
            skFitSpline(sketch, "E2774", {"points": [v(19.8, 45.68) * mm, v(19.98, 45.8) * mm, v(20.26, 46.17) * mm, v(20.45, 46.52) * mm]});
            skFitSpline(sketch, "E2775", {"points": [v(20.45, 46.52) * mm, v(20.74, 47.08) * mm, v(20.7, 47.17) * mm, v(20.07, 47.33) * mm]});
            skFitSpline(sketch, "E2776", {"points": [v(20.07, 47.33) * mm, v(19.67, 47.42) * mm, v(19.35, 47.6) * mm, v(19.35, 47.73) * mm]});
            skFitSpline(sketch, "E2777", {"points": [v(19.35, 47.73) * mm, v(19.35, 47.86) * mm, v(19.86, 47.76) * mm, v(20.49, 47.52) * mm]});
            skFitSpline(sketch, "E2778", {"points": [v(20.49, 47.52) * mm, v(21.45, 47.14) * mm, v(21.8, 47.13) * mm, v(22.81, 47.44) * mm]});
            skLineSegment(sketch, "E2779", {"start": v(22.81, 47.44) * mm, "end": v(24.01, 47.8) * mm});
            skLineSegment(sketch, "E2780", {"start": v(24.01, 47.8) * mm, "end": v(22.86, 48.14) * mm});
            skFitSpline(sketch, "E2781", {"points": [v(22.86, 48.14) * mm, v(22.23, 48.33) * mm, v(21.22, 48.82) * mm, v(20.6, 49.23) * mm]});
            skFitSpline(sketch, "E2782", {"points": [v(20.6, 49.23) * mm, v(20, 49.65) * mm, v(19.21, 49.98) * mm, v(18.86, 49.98) * mm]});
            skFitSpline(sketch, "E2783", {"points": [v(18.86, 49.98) * mm, v(18.5, 49.98) * mm, v(18.14, 50.16) * mm, v(18.05, 50.38) * mm]});
            skFitSpline(sketch, "E2784", {"points": [v(18.05, 50.38) * mm, v(17.76, 51.15) * mm, v(17.03, 51.11) * mm, v(15.55, 50.27) * mm]});
            skFitSpline(sketch, "E2785", {"points": [v(15.55, 50.27) * mm, v(13.75, 49.24) * mm, v(13.49, 49.22) * mm, v(13.27, 50.1) * mm]});
            skFitSpline(sketch, "E2786", {"points": [v(13.27, 50.1) * mm, v(13.03, 51.04) * mm, v(12.3, 50.72) * mm, v(12.3, 49.68) * mm]});
            skLineSegment(sketch, "E2787", {"start": v(12.3, 49.68) * mm, "end": v(12.3, 48.87) * mm});
            skLineSegment(sketch, "E2788", {"start": v(12.3, 48.87) * mm, "end": v(15.2, 48.8) * mm});
            skLineSegment(sketch, "E2789", {"start": v(15.2, 48.8) * mm, "end": v(18.08, 48.71) * mm});
            skLineSegment(sketch, "E2790", {"start": v(18.08, 48.71) * mm, "end": v(15.18, 48.46) * mm});
            skFitSpline(sketch, "E2791", {"points": [v(15.18, 48.46) * mm, v(13.6, 48.33) * mm, v(12.2, 48.08) * mm, v(12.1, 47.92) * mm]});
            skFitSpline(sketch, "E2792", {"points": [v(12.1, 47.92) * mm, v(12, 47.75) * mm, v(12.05, 47.57) * mm, v(12.2, 47.52) * mm]});
            skFitSpline(sketch, "E2793", {"points": [v(12.2, 47.52) * mm, v(12.37, 47.47) * mm, v(12.74, 47.23) * mm, v(13.03, 47) * mm]});
            skFitSpline(sketch, "E2794", {"points": [v(13.03, 47) * mm, v(13.51, 46.61) * mm, v(13.47, 46.61) * mm, v(12.69, 47) * mm]});
            skFitSpline(sketch, "E2795", {"points": [v(12.69, 47) * mm, v(11.86, 47.4) * mm, v(11.78, 47.38) * mm, v(11.19, 46.76) * mm]});
            skLineSegment(sketch, "E2796", {"start": v(11.19, 46.76) * mm, "end": v(10.56, 46.1) * mm});
            skLineSegment(sketch, "E2797", {"start": v(10.56, 46.1) * mm, "end": v(11.21, 45.64) * mm});
            skFitSpline(sketch, "E2798", {"points": [v(11.21, 45.64) * mm, v(11.85, 45.19) * mm, v(13.82, 45.03) * mm, v(14.67, 45.36) * mm]});
            skFitSpline(sketch, "E2799", {"points": [v(16.53, 47.18) * mm, v(15.68, 47.65) * mm, v(15.3, 47.94) * mm, v(15.68, 47.84) * mm]});
            skFitSpline(sketch, "E2800", {"points": [v(15.68, 47.84) * mm, v(16.4, 47.66) * mm, v(18.22, 46.65) * mm, v(18.22, 46.43) * mm]});
            skFitSpline(sketch, "E2801", {"points": [v(18.22, 46.43) * mm, v(18.22, 46.26) * mm, v(18.24, 46.26) * mm, v(16.53, 47.18) * mm]});
            skFitSpline(sketch, "E2802", {"points": [v(10.35, 46.63) * mm, v(11.39, 47.2) * mm, v(11.63, 47.5) * mm, v(11.82, 48.44) * mm]});
            skFitSpline(sketch, "E2803", {"points": [v(11.82, 48.44) * mm, v(11.95, 49.05) * mm, v(12.18, 50.16) * mm, v(12.34, 50.9) * mm]});
            skFitSpline(sketch, "E2804", {"points": [v(12.34, 50.9) * mm, v(12.67, 52.42) * mm, v(12.33, 53.84) * mm, v(11.45, 54.64) * mm]});
            skFitSpline(sketch, "E2805", {"points": [v(11.45, 54.64) * mm, v(10.82, 55.21) * mm, v(9.9, 55) * mm, v(10.15, 54.34) * mm]});
            skFitSpline(sketch, "E2806", {"points": [v(10.15, 54.34) * mm, v(10.24, 54.1) * mm, v(10.2, 53.97) * mm, v(10.07, 54.06) * mm]});
            skFitSpline(sketch, "E2807", {"points": [v(10.07, 54.06) * mm, v(9.78, 54.24) * mm, v(9.45, 53.54) * mm, v(9.58, 53.02) * mm]});
            skFitSpline(sketch, "E2808", {"points": [v(9.58, 53.02) * mm, v(9.63, 52.82) * mm, v(9.61, 52.76) * mm, v(9.55, 52.88) * mm]});
            skFitSpline(sketch, "E2809", {"points": [v(9.55, 52.88) * mm, v(9.32, 53.29) * mm, v(8.91, 52.76) * mm, v(8.88, 52.01) * mm]});
            skFitSpline(sketch, "E2810", {"points": [v(8.88, 52.01) * mm, v(8.86, 51.48) * mm, v(8.8, 51.4) * mm, v(8.71, 51.78) * mm]});
            skFitSpline(sketch, "E2811", {"points": [v(8.71, 51.78) * mm, v(8.6, 52.23) * mm, v(8.36, 52.1) * mm, v(7.13, 50.93) * mm]});
            skFitSpline(sketch, "E2812", {"points": [v(7.13, 50.93) * mm, v(5.55, 49.43) * mm, v(6.01, 50.13) * mm, v(8.13, 52.44) * mm]});
            skFitSpline(sketch, "E2813", {"points": [v(8.13, 52.44) * mm, v(10.04, 54.51) * mm, v(10.32, 55.5) * mm, v(9.37, 56.72) * mm]});
            skFitSpline(sketch, "E2814", {"points": [v(9.37, 56.72) * mm, v(9.12, 57.04) * mm, v(9.03, 56.99) * mm, v(8.87, 56.44) * mm]});
            skFitSpline(sketch, "E2815", {"points": [v(8.87, 56.44) * mm, v(8.7, 55.83) * mm, v(8.68, 55.85) * mm, v(8.66, 56.63) * mm]});
            skFitSpline(sketch, "E2816", {"points": [v(8.66, 56.63) * mm, v(8.64, 57.1) * mm, v(8.46, 57.73) * mm, v(8.25, 58.02) * mm]});
            skFitSpline(sketch, "E2817", {"points": [v(8.25, 58.02) * mm, v(7.9, 58.49) * mm, v(7.88, 58.44) * mm, v(7.96, 57.58) * mm]});
            skLineSegment(sketch, "E2818", {"start": v(7.96, 57.58) * mm, "end": v(8.05, 56.62) * mm});
            skLineSegment(sketch, "E2819", {"start": v(8.05, 56.62) * mm, "end": v(7.81, 57.53) * mm});
            skFitSpline(sketch, "E2820", {"points": [v(7.81, 57.53) * mm, v(7.5, 58.7) * mm, v(6.95, 59.36) * mm, v(6.45, 59.17) * mm]});
            skFitSpline(sketch, "E2821", {"points": [v(6.45, 59.17) * mm, v(6.24, 59.09) * mm, v(6.14, 59.15) * mm, v(6.23, 59.3) * mm]});
            skFitSpline(sketch, "E2822", {"points": [v(6.23, 59.3) * mm, v(6.47, 59.69) * mm, v(5.15, 60.14) * mm, v(3.8, 60.14) * mm]});
            skFitSpline(sketch, "E2823", {"points": [v(3.8, 60.14) * mm, v(2.38, 60.14) * mm, v(0.9, 59.42) * mm, v(1.13, 58.83) * mm]});
            skFitSpline(sketch, "E2824", {"points": [v(1.13, 58.83) * mm, v(1.22, 58.6) * mm, v(1.3, 58.26) * mm, v(1.3, 58.07) * mm]});
            skFitSpline(sketch, "E2825", {"points": [v(1.3, 58.07) * mm, v(1.3, 57.9) * mm, v(1.56, 58.06) * mm, v(1.87, 58.45) * mm]});
            skLineSegment(sketch, "E2826", {"start": v(1.87, 58.45) * mm, "end": v(2.44, 59.16) * mm});
            skLineSegment(sketch, "E2827", {"start": v(2.44, 59.16) * mm, "end": v(2.1, 58.38) * mm});
            skFitSpline(sketch, "E2828", {"points": [v(2.1, 58.38) * mm, v(1.67, 57.4) * mm, v(1.92, 57.14) * mm, v(2.75, 57.72) * mm]});
            skFitSpline(sketch, "E2829", {"points": [v(2.75, 57.72) * mm, v(3.1, 57.96) * mm, v(3.78, 58.15) * mm, v(4.25, 58.14) * mm]});
            skFitSpline(sketch, "E2830", {"points": [v(4.25, 58.14) * mm, v(5.04, 58.1) * mm, v(5.02, 58.09) * mm, v(4.02, 57.9) * mm]});
            skFitSpline(sketch, "E2831", {"points": [v(4.02, 57.9) * mm, v(2.62, 57.62) * mm, v(2.12, 57.1) * mm, v(2.44, 56.26) * mm]});
            skLineSegment(sketch, "E2832", {"start": v(2.44, 56.26) * mm, "end": v(2.69, 55.61) * mm});
            skLineSegment(sketch, "E2833", {"start": v(2.69, 55.61) * mm, "end": v(3.85, 56.35) * mm});
            skFitSpline(sketch, "E2834", {"points": [v(3.85, 56.35) * mm, v(4.5, 56.75) * mm, v(5.09, 57) * mm, v(5.18, 56.92) * mm]});
            skFitSpline(sketch, "E2835", {"points": [v(5.18, 56.92) * mm, v(5.27, 56.83) * mm, v(5.63, 56.95) * mm, v(6, 57.19) * mm]});
            skFitSpline(sketch, "E2836", {"points": [v(6, 57.19) * mm, v(6.75, 57.68) * mm, v(6.85, 57.56) * mm, v(6.21, 56.92) * mm]});
            skFitSpline(sketch, "E2837", {"points": [v(6.21, 56.92) * mm, v(5.97, 56.67) * mm, v(5.47, 56.47) * mm, v(5.1, 56.47) * mm]});
            skFitSpline(sketch, "E2838", {"points": [v(5.1, 56.47) * mm, v(3.9, 56.47) * mm, v(2.86, 55.28) * mm, v(2.49, 53.47) * mm]});
            skFitSpline(sketch, "E2839", {"points": [v(2.49, 53.47) * mm, v(2.14, 51.78) * mm, v(2.48, 49.53) * mm, v(3.03, 49.87) * mm]});
            skFitSpline(sketch, "E2840", {"points": [v(3.03, 49.87) * mm, v(3.16, 49.95) * mm, v(3.14, 50.26) * mm, v(2.98, 50.56) * mm]});
            skFitSpline(sketch, "E2841", {"points": [v(2.98, 50.56) * mm, v(2.74, 51) * mm, v(2.77, 51.07) * mm, v(3.14, 50.93) * mm]});
            skFitSpline(sketch, "E2842", {"points": [v(3.14, 50.93) * mm, v(3.4, 50.83) * mm, v(3.89, 51.04) * mm, v(4.34, 51.46) * mm]});
            skFitSpline(sketch, "E2843", {"points": [v(4.34, 51.46) * mm, v(4.76, 51.85) * mm, v(5.42, 52.32) * mm, v(5.8, 52.5) * mm]});
            skFitSpline(sketch, "E2844", {"points": [v(5.8, 52.5) * mm, v(6.4, 52.77) * mm, v(6.43, 52.76) * mm, v(5.97, 52.46) * mm]});
            skFitSpline(sketch, "E2845", {"points": [v(5.97, 52.46) * mm, v(3.55, 50.84) * mm, v(2.6, 49.07) * mm, v(3.27, 47.45) * mm]});
            skFitSpline(sketch, "E2846", {"points": [v(3.27, 47.45) * mm, v(3.82, 46.12) * mm, v(4.77, 45.72) * mm, v(7.1, 45.84) * mm]});
            skFitSpline(sketch, "E2847", {"points": [v(7.1, 45.84) * mm, v(8.55, 45.91) * mm, v(9.45, 46.13) * mm, v(10.35, 46.63) * mm]});
            skFitSpline(sketch, "E2848", {"points": [v(5.2, 46.8) * mm, v(4.86, 47.26) * mm, v(4.87, 47.27) * mm, v(5.31, 46.91) * mm]});
            skFitSpline(sketch, "E2849", {"points": [v(5.31, 46.91) * mm, v(5.78, 46.55) * mm, v(5.93, 46.31) * mm, v(5.7, 46.31) * mm]});
            skFitSpline(sketch, "E2850", {"points": [v(5.7, 46.31) * mm, v(5.64, 46.31) * mm, v(5.42, 46.54) * mm, v(5.2, 46.8) * mm]});
            skFitSpline(sketch, "E2851", {"points": [v(10.94, 48.71) * mm, v(10.95, 49.18) * mm, v(11.01, 49.34) * mm, v(11.08, 49.06) * mm]});
            skFitSpline(sketch, "E2852", {"points": [v(11.08, 49.06) * mm, v(11.15, 48.79) * mm, v(11.15, 48.4) * mm, v(11.07, 48.21) * mm]});
            skFitSpline(sketch, "E2853", {"points": [v(11.07, 48.21) * mm, v(11, 48.02) * mm, v(10.94, 48.25) * mm, v(10.94, 48.71) * mm]});
            skFitSpline(sketch, "E2854", {"points": [v(7.52, 48.74) * mm, v(7.54, 49.07) * mm, v(7.6, 49.13) * mm, v(7.7, 48.9) * mm]});
            skFitSpline(sketch, "E2855", {"points": [v(7.7, 48.9) * mm, v(7.77, 48.7) * mm, v(7.76, 48.46) * mm, v(7.67, 48.37) * mm]});
            skFitSpline(sketch, "E2856", {"points": [v(7.67, 48.37) * mm, v(7.58, 48.27) * mm, v(7.51, 48.44) * mm, v(7.52, 48.74) * mm]});
            skFitSpline(sketch, "E2857", {"points": [v(8.12, 49) * mm, v(8.13, 49.46) * mm, v(8.19, 49.62) * mm, v(8.26, 49.34) * mm]});
            skFitSpline(sketch, "E2858", {"points": [v(8.26, 49.34) * mm, v(8.33, 49.07) * mm, v(8.33, 48.69) * mm, v(8.25, 48.5) * mm]});
            skFitSpline(sketch, "E2859", {"points": [v(8.25, 48.5) * mm, v(8.17, 48.3) * mm, v(8.11, 48.53) * mm, v(8.12, 49) * mm]});
            skFitSpline(sketch, "E2860", {"points": [v(8.93, 48.74) * mm, v(8.95, 49.07) * mm, v(9.01, 49.13) * mm, v(9.1, 48.9) * mm]});
            skFitSpline(sketch, "E2861", {"points": [v(9.1, 48.9) * mm, v(9.19, 48.7) * mm, v(9.18, 48.46) * mm, v(9.08, 48.37) * mm]});
            skFitSpline(sketch, "E2862", {"points": [v(9.08, 48.37) * mm, v(8.99, 48.27) * mm, v(8.92, 48.44) * mm, v(8.93, 48.74) * mm]});
            skLineSegment(sketch, "E2863", {"start": v(8.93, 48.74) * mm, "end": v(8.93, 48.74) * mm});
            skFitSpline(sketch, "E2864", {"points": [v(3.57, 49.02) * mm, v(3.58, 49.35) * mm, v(3.65, 49.41) * mm, v(3.74, 49.19) * mm]});
            skFitSpline(sketch, "E2865", {"points": [v(3.74, 49.19) * mm, v(3.82, 48.99) * mm, v(3.81, 48.74) * mm, v(3.72, 48.65) * mm]});
            skFitSpline(sketch, "E2866", {"points": [v(3.72, 48.65) * mm, v(3.63, 48.55) * mm, v(3.56, 48.72) * mm, v(3.57, 49.02) * mm]});
            skFitSpline(sketch, "E2867", {"points": [v(7.26, 49.98) * mm, v(7.26, 50.37) * mm, v(7.33, 50.53) * mm, v(7.4, 50.34) * mm]});
            skFitSpline(sketch, "E2868", {"points": [v(7.4, 50.34) * mm, v(7.48, 50.14) * mm, v(7.48, 49.82) * mm, v(7.4, 49.63) * mm]});
            skFitSpline(sketch, "E2869", {"points": [v(7.4, 49.63) * mm, v(7.33, 49.44) * mm, v(7.26, 49.6) * mm, v(7.26, 49.98) * mm]});
            skFitSpline(sketch, "E2870", {"points": [v(9.18, 50.29) * mm, v(9, 50.61) * mm, v(8.92, 50.93) * mm, v(8.98, 51) * mm]});
            skFitSpline(sketch, "E2871", {"points": [v(8.98, 51) * mm, v(9.05, 51.06) * mm, v(9.25, 50.8) * mm, v(9.42, 50.4) * mm]});
            skFitSpline(sketch, "E2872", {"points": [v(9.42, 50.4) * mm, v(9.81, 49.55) * mm, v(9.62, 49.46) * mm, v(9.18, 50.29) * mm]});
            skFitSpline(sketch, "E2873", {"points": [v(4.68, 50.35) * mm, v(4.68, 50.4) * mm, v(5.1, 50.82) * mm, v(5.6, 51.27) * mm]});
            skLineSegment(sketch, "E2874", {"start": v(5.6, 51.27) * mm, "end": v(6.51, 52.1) * mm});
            skLineSegment(sketch, "E2875", {"start": v(6.51, 52.1) * mm, "end": v(5.68, 51.18) * mm});
            skFitSpline(sketch, "E2876", {"points": [v(5.68, 51.18) * mm, v(4.91, 50.33) * mm, v(4.68, 50.14) * mm, v(4.68, 50.35) * mm]});
            skFitSpline(sketch, "E2877", {"points": [v(2.44, 51.84) * mm, v(2.46, 52.17) * mm, v(2.52, 52.24) * mm, v(2.61, 52.01) * mm]});
            skFitSpline(sketch, "E2878", {"points": [v(2.61, 52.01) * mm, v(2.7, 51.8) * mm, v(2.68, 51.56) * mm, v(2.6, 51.47) * mm]});
            skFitSpline(sketch, "E2879", {"points": [v(2.6, 51.47) * mm, v(2.5, 51.38) * mm, v(2.43, 51.54) * mm, v(2.44, 51.84) * mm]});
            skFitSpline(sketch, "E2880", {"points": [v(7.5, 52.63) * mm, v(7.5, 52.69) * mm, v(7.72, 52.91) * mm, v(8, 53.12) * mm]});
            skFitSpline(sketch, "E2881", {"points": [v(8, 53.12) * mm, v(8.44, 53.47) * mm, v(8.45, 53.46) * mm, v(8.1, 53.02) * mm]});
            skFitSpline(sketch, "E2882", {"points": [v(8.1, 53.02) * mm, v(7.73, 52.55) * mm, v(7.5, 52.4) * mm, v(7.5, 52.63) * mm]});
            skFitSpline(sketch, "E2883", {"points": [v(6.65, 52.93) * mm, v(6.65, 53) * mm, v(6.9, 53.2) * mm, v(7.22, 53.37) * mm]});
            skFitSpline(sketch, "E2884", {"points": [v(7.22, 53.37) * mm, v(7.53, 53.54) * mm, v(7.78, 53.6) * mm, v(7.78, 53.53) * mm]});
            skFitSpline(sketch, "E2885", {"points": [v(7.78, 53.53) * mm, v(7.78, 53.45) * mm, v(7.53, 53.25) * mm, v(7.22, 53.09) * mm]});
            skFitSpline(sketch, "E2886", {"points": [v(7.22, 53.09) * mm, v(6.9, 52.92) * mm, v(6.65, 52.85) * mm, v(6.65, 52.93) * mm]});
            skFitSpline(sketch, "E2887", {"points": [v(10.85, 53.58) * mm, v(10.5, 54.03) * mm, v(10.5, 54.04) * mm, v(10.96, 53.69) * mm]});
            skFitSpline(sketch, "E2888", {"points": [v(10.96, 53.69) * mm, v(11.43, 53.32) * mm, v(11.58, 53.09) * mm, v(11.34, 53.09) * mm]});
            skFitSpline(sketch, "E2889", {"points": [v(11.34, 53.09) * mm, v(11.29, 53.09) * mm, v(11.06, 53.31) * mm, v(10.85, 53.58) * mm]});
            skFitSpline(sketch, "E2890", {"points": [v(10.6, 54.5) * mm, v(10.35, 54.66) * mm, v(10.32, 54.77) * mm, v(10.52, 54.78) * mm]});
            skFitSpline(sketch, "E2891", {"points": [v(10.52, 54.78) * mm, v(10.7, 54.78) * mm, v(10.93, 54.65) * mm, v(11.03, 54.5) * mm]});
            skFitSpline(sketch, "E2892", {"points": [v(11.03, 54.5) * mm, v(11.24, 54.15) * mm, v(11.15, 54.15) * mm, v(10.6, 54.5) * mm]});
            skFitSpline(sketch, "E2893", {"points": [v(3.97, 55.06) * mm, v(4.25, 55.37) * mm, v(4.55, 55.63) * mm, v(4.62, 55.63) * mm]});
            skFitSpline(sketch, "E2894", {"points": [v(4.62, 55.63) * mm, v(4.7, 55.63) * mm, v(4.54, 55.37) * mm, v(4.25, 55.06) * mm]});
            skFitSpline(sketch, "E2895", {"points": [v(4.25, 55.06) * mm, v(3.97, 54.75) * mm, v(3.68, 54.5) * mm, v(3.6, 54.5) * mm]});
            skFitSpline(sketch, "E2896", {"points": [v(3.6, 54.5) * mm, v(3.53, 54.5) * mm, v(3.7, 54.75) * mm, v(3.97, 55.06) * mm]});
            skFitSpline(sketch, "E2897", {"points": [v(7.78, 54.89) * mm, v(7.78, 54.95) * mm, v(8, 55.17) * mm, v(8.28, 55.38) * mm]});
            skFitSpline(sketch, "E2898", {"points": [v(8.28, 55.38) * mm, v(8.72, 55.73) * mm, v(8.73, 55.72) * mm, v(8.38, 55.27) * mm]});
            skFitSpline(sketch, "E2899", {"points": [v(8.38, 55.27) * mm, v(8.01, 54.8) * mm, v(7.78, 54.66) * mm, v(7.78, 54.89) * mm]});
            skFitSpline(sketch, "E2900", {"points": [v(6.94, 55.77) * mm, v(7.3, 56.16) * mm, v(7.66, 56.47) * mm, v(7.74, 56.47) * mm]});
            skFitSpline(sketch, "E2901", {"points": [v(7.74, 56.47) * mm, v(7.82, 56.47) * mm, v(7.58, 56.16) * mm, v(7.22, 55.77) * mm]});
            skFitSpline(sketch, "E2902", {"points": [v(7.22, 55.77) * mm, v(6.85, 55.38) * mm, v(6.5, 55.06) * mm, v(6.41, 55.06) * mm]});
            skFitSpline(sketch, "E2903", {"points": [v(6.41, 55.06) * mm, v(6.34, 55.06) * mm, v(6.57, 55.38) * mm, v(6.94, 55.77) * mm]});
            skFitSpline(sketch, "E2904", {"points": [v(5.55, 56.01) * mm, v(5.61, 56.07) * mm, v(5.98, 56.27) * mm, v(6.37, 56.45) * mm]});
            skFitSpline(sketch, "E2905", {"points": [v(6.37, 56.45) * mm, v(7.04, 56.77) * mm, v(7.05, 56.76) * mm, v(6.53, 56.35) * mm]});
            skFitSpline(sketch, "E2906", {"points": [v(6.53, 56.35) * mm, v(6.08, 55.99) * mm, v(5.16, 55.67) * mm, v(5.55, 56.01) * mm]});
            skFitSpline(sketch, "E2907", {"points": [v(1.3, 58.84) * mm, v(1.3, 58.9) * mm, v(1.51, 59.12) * mm, v(1.79, 59.33) * mm]});
            skFitSpline(sketch, "E2908", {"points": [v(1.79, 59.33) * mm, v(2.23, 59.68) * mm, v(2.24, 59.67) * mm, v(1.9, 59.23) * mm]});
            skFitSpline(sketch, "E2909", {"points": [v(1.9, 59.23) * mm, v(1.52, 58.76) * mm, v(1.3, 58.6) * mm, v(1.3, 58.84) * mm]});
            skFitSpline(sketch, "E2910", {"points": [v(-9.44, 47.7) * mm, v(-9.06, 48.43) * mm, v(-9.07, 48.65) * mm, v(-9.5, 48.4) * mm]});
            skFitSpline(sketch, "E2911", {"points": [v(-9.5, 48.4) * mm, v(-9.7, 48.28) * mm, v(-9.76, 48.3) * mm, v(-9.62, 48.46) * mm]});
            skFitSpline(sketch, "E2912", {"points": [v(-9.62, 48.46) * mm, v(-9.5, 48.6) * mm, v(-9.25, 48.71) * mm, v(-9.08, 48.71) * mm]});
            skFitSpline(sketch, "E2913", {"points": [v(-9.08, 48.71) * mm, v(-8.91, 48.71) * mm, v(-8.72, 48.9) * mm, v(-8.64, 49.1) * mm]});
            skFitSpline(sketch, "E2914", {"points": [v(-8.64, 49.1) * mm, v(-8.55, 49.4) * mm, v(-8.68, 49.46) * mm, v(-9.11, 49.35) * mm]});
            skFitSpline(sketch, "E2915", {"points": [v(-9.11, 49.35) * mm, v(-9.44, 49.26) * mm, v(-9.64, 49.3) * mm, v(-9.56, 49.45) * mm]});
            skFitSpline(sketch, "E2916", {"points": [v(-9.56, 49.45) * mm, v(-9.47, 49.59) * mm, v(-9.22, 49.7) * mm, v(-9, 49.7) * mm]});
            skFitSpline(sketch, "E2917", {"points": [v(-9, 49.7) * mm, v(-8.5, 49.7) * mm, v(-8.44, 50.54) * mm, v(-8.94, 50.57) * mm]});
            skFitSpline(sketch, "E2918", {"points": [v(-8.94, 50.57) * mm, v(-9.13, 50.58) * mm, v(-9.04, 50.7) * mm, v(-8.73, 50.85) * mm]});
            skFitSpline(sketch, "E2919", {"points": [v(-8.73, 50.85) * mm, v(-8.31, 51.05) * mm, v(-8.44, 51.08) * mm, v(-9.24, 50.96) * mm]});
            skFitSpline(sketch, "E2920", {"points": [v(-9.24, 50.96) * mm, v(-10.26, 50.8) * mm, v(-10.3, 50.83) * mm, v(-10, 51.38) * mm]});
            skFitSpline(sketch, "E2921", {"points": [v(-10, 51.38) * mm, v(-9.66, 52.02) * mm, v(-9.37, 52.17) * mm, v(-9.6, 51.58) * mm]});
            skFitSpline(sketch, "E2922", {"points": [v(-9.6, 51.58) * mm, v(-9.7, 51.3) * mm, v(-9.51, 51.24) * mm, v(-8.88, 51.33) * mm]});
            skFitSpline(sketch, "E2923", {"points": [v(-8.88, 51.33) * mm, v(-8.08, 51.45) * mm, v(-8.02, 51.54) * mm, v(-8.02, 52.67) * mm]});
            skFitSpline(sketch, "E2924", {"points": [v(-8.02, 52.67) * mm, v(-8.02, 53.38) * mm, v(-8.17, 53.95) * mm, v(-8.37, 54.03) * mm]});
            skFitSpline(sketch, "E2925", {"points": [v(-8.37, 54.03) * mm, v(-8.59, 54.11) * mm, v(-8.53, 54.18) * mm, v(-8.23, 54.2) * mm]});
            skFitSpline(sketch, "E2926", {"points": [v(-8.23, 54.2) * mm, v(-7.96, 54.2) * mm, v(-7.74, 54.34) * mm, v(-7.74, 54.5) * mm]});
            skFitSpline(sketch, "E2927", {"points": [v(-7.74, 54.5) * mm, v(-7.74, 54.88) * mm, v(-9.21, 54.86) * mm, v(-10.2, 54.46) * mm]});
            skFitSpline(sketch, "E2928", {"points": [v(-10.2, 54.46) * mm, v(-10.63, 54.28) * mm, v(-11.18, 54.1) * mm, v(-11.4, 54.05) * mm]});
            skFitSpline(sketch, "E2929", {"points": [v(-11.4, 54.05) * mm, v(-12.17, 53.9) * mm, v(-13.1, 52.53) * mm, v(-13.1, 51.56) * mm]});
            skFitSpline(sketch, "E2930", {"points": [v(-13.1, 51.56) * mm, v(-13.1, 50.58) * mm, v(-12.19, 49.41) * mm, v(-11.84, 49.96) * mm]});
            skFitSpline(sketch, "E2931", {"points": [v(-11.84, 49.96) * mm, v(-11.74, 50.13) * mm, v(-11.38, 50.4) * mm, v(-11.04, 50.58) * mm]});
            skLineSegment(sketch, "E2932", {"start": v(-11.04, 50.58) * mm, "end": v(-10.42, 50.9) * mm});
            skLineSegment(sketch, "E2933", {"start": v(-10.42, 50.9) * mm, "end": v(-11.06, 50.29) * mm});
            skFitSpline(sketch, "E2934", {"points": [v(-11.06, 50.29) * mm, v(-12.18, 49.2) * mm, v(-11.67, 47.16) * mm, v(-10.27, 47.16) * mm]});
            skFitSpline(sketch, "E2935", {"points": [v(-10.27, 47.16) * mm, v(-9.98, 47.16) * mm, v(-9.6, 47.4) * mm, v(-9.44, 47.7) * mm]});
            skFitSpline(sketch, "E2936", {"points": [v(-10.36, 50.3) * mm, v(-10.16, 50.5) * mm, v(-9.94, 50.58) * mm, v(-9.85, 50.5) * mm]});
            skFitSpline(sketch, "E2937", {"points": [v(-9.85, 50.5) * mm, v(-9.76, 50.4) * mm, v(-9.92, 50.25) * mm, v(-10.2, 50.14) * mm]});
            skFitSpline(sketch, "E2938", {"points": [v(-10.2, 50.14) * mm, v(-10.6, 49.99) * mm, v(-10.63, 50.02) * mm, v(-10.36, 50.3) * mm]});
            skFitSpline(sketch, "E2939", {"points": [v(-10.56, 51.94) * mm, v(-10.56, 52.09) * mm, v(-10.44, 52.29) * mm, v(-10.28, 52.38) * mm]});
            skFitSpline(sketch, "E2940", {"points": [v(-10.28, 52.38) * mm, v(-10.12, 52.48) * mm, v(-10.08, 52.37) * mm, v(-10.17, 52.11) * mm]});
            skFitSpline(sketch, "E2941", {"points": [v(-10.17, 52.11) * mm, v(-10.36, 51.63) * mm, v(-10.56, 51.54) * mm, v(-10.56, 51.94) * mm]});
            skFitSpline(sketch, "E2942", {"points": [v(-10.7, 53.09) * mm, v(-10.42, 53.4) * mm, v(-10.13, 53.65) * mm, v(-10.05, 53.65) * mm]});
            skFitSpline(sketch, "E2943", {"points": [v(-10.05, 53.65) * mm, v(-9.97, 53.65) * mm, v(-10.14, 53.4) * mm, v(-10.42, 53.09) * mm]});
            skFitSpline(sketch, "E2944", {"points": [v(-10.42, 53.09) * mm, v(-10.7, 52.78) * mm, v(-11, 52.52) * mm, v(-11.07, 52.52) * mm]});
            skFitSpline(sketch, "E2945", {"points": [v(-11.07, 52.52) * mm, v(-11.15, 52.52) * mm, v(-10.98, 52.78) * mm, v(-10.7, 53.09) * mm]});
            skFitSpline(sketch, "E2946", {"points": [v(-8.64, 55.06) * mm, v(-8.2, 55.06) * mm, v(-7.71, 54.93) * mm, v(-7.55, 54.76) * mm]});
            skFitSpline(sketch, "E2947", {"points": [v(-7.55, 54.76) * mm, v(-7.32, 54.54) * mm, v(-7.18, 54.55) * mm, v(-7.02, 54.8) * mm]});
            skFitSpline(sketch, "E2948", {"points": [v(-7.02, 54.8) * mm, v(-6.87, 55.04) * mm, v(-6.92, 55.08) * mm, v(-7.18, 54.92) * mm]});
            skFitSpline(sketch, "E2949", {"points": [v(-7.18, 54.92) * mm, v(-7.45, 54.75) * mm, v(-7.5, 54.82) * mm, v(-7.37, 55.16) * mm]});
            skFitSpline(sketch, "E2950", {"points": [v(-7.37, 55.16) * mm, v(-7.25, 55.48) * mm, v(-7.35, 55.64) * mm, v(-7.68, 55.66) * mm]});
            skFitSpline(sketch, "E2951", {"points": [v(-7.68, 55.66) * mm, v(-7.94, 55.68) * mm, v(-7.8, 55.77) * mm, v(-7.34, 55.87) * mm]});
            skFitSpline(sketch, "E2952", {"points": [v(-7.34, 55.87) * mm, v(-6.31, 56.1) * mm, v(-6.03, 56.75) * mm, v(-6.94, 56.79) * mm]});
            skFitSpline(sketch, "E2953", {"points": [v(-6.94, 56.79) * mm, v(-7.47, 56.8) * mm, v(-7.43, 56.85) * mm, v(-6.73, 57.02) * mm]});
            skFitSpline(sketch, "E2954", {"points": [v(-6.73, 57.02) * mm, v(-5.13, 57.4) * mm, v(-4.7, 58.1) * mm, v(-5.7, 58.73) * mm]});
            skFitSpline(sketch, "E2955", {"points": [v(-5.7, 58.73) * mm, v(-6.12, 59) * mm, v(-6.1, 59.02) * mm, v(-5.55, 58.87) * mm]});
            skFitSpline(sketch, "E2956", {"points": [v(-5.55, 58.87) * mm, v(-4.58, 58.6) * mm, v(-4.8, 59.2) * mm, v(-5.8, 59.55) * mm]});
            skFitSpline(sketch, "E2957", {"points": [v(-5.8, 59.55) * mm, v(-7.52, 60.15) * mm, v(-8.54, 59.95) * mm, v(-9.67, 58.8) * mm]});
            skFitSpline(sketch, "E2958", {"points": [v(-9.67, 58.8) * mm, v(-10.24, 58.22) * mm, v(-11.18, 57.39) * mm, v(-11.76, 56.95) * mm]});
            skFitSpline(sketch, "E2959", {"points": [v(-11.76, 56.95) * mm, v(-12.54, 56.38) * mm, v(-12.82, 55.96) * mm, v(-12.82, 55.39) * mm]});
            skFitSpline(sketch, "E2960", {"points": [v(-12.82, 55.39) * mm, v(-12.82, 54.12) * mm, v(-12.4, 53.94) * mm, v(-10.82, 54.53) * mm]});
            skFitSpline(sketch, "E2961", {"points": [v(-10.82, 54.53) * mm, v(-10.05, 54.83) * mm, v(-9.07, 55.06) * mm, v(-8.64, 55.06) * mm]});
            skFitSpline(sketch, "E2962", {"points": [v(-8.92, 56.95) * mm, v(-8.72, 57.03) * mm, v(-8.47, 57.02) * mm, v(-8.38, 56.93) * mm]});
            skFitSpline(sketch, "E2963", {"points": [v(-8.38, 56.93) * mm, v(-8.29, 56.83) * mm, v(-8.45, 56.77) * mm, v(-8.75, 56.78) * mm]});
            skFitSpline(sketch, "E2964", {"points": [v(-8.75, 56.78) * mm, v(-9.08, 56.8) * mm, v(-9.15, 56.86) * mm, v(-8.92, 56.95) * mm]});
            skFitSpline(sketch, "E2965", {"points": [v(-8.36, 57.51) * mm, v(-8.15, 57.6) * mm, v(-7.91, 57.59) * mm, v(-7.82, 57.5) * mm]});
            skFitSpline(sketch, "E2966", {"points": [v(-7.82, 57.5) * mm, v(-7.72, 57.4) * mm, v(-7.89, 57.33) * mm, v(-8.19, 57.34) * mm]});
            skFitSpline(sketch, "E2967", {"points": [v(-8.19, 57.34) * mm, v(-8.52, 57.36) * mm, v(-8.58, 57.42) * mm, v(-8.36, 57.51) * mm]});
            skFitSpline(sketch, "E2968", {"points": [v(-6.33, 57.89) * mm, v(-6.56, 58.04) * mm, v(-6.63, 58.16) * mm, v(-6.47, 58.16) * mm]});
            skFitSpline(sketch, "E2969", {"points": [v(-6.47, 58.16) * mm, v(-6.31, 58.16) * mm, v(-6, 58.04) * mm, v(-5.76, 57.89) * mm]});
            skFitSpline(sketch, "E2970", {"points": [v(-5.76, 57.89) * mm, v(-5.53, 57.74) * mm, v(-5.47, 57.61) * mm, v(-5.62, 57.61) * mm]});
            skFitSpline(sketch, "E2971", {"points": [v(-5.62, 57.61) * mm, v(-5.78, 57.61) * mm, v(-6.1, 57.74) * mm, v(-6.33, 57.89) * mm]});
            skFitSpline(sketch, "E2972", {"points": [v(-2.3, -53.41) * mm, v(-1.7, -53.24) * mm, v(-1.64, -52.46) * mm, v(-2.23, -52.46) * mm]});
            skFitSpline(sketch, "E2973", {"points": [v(-2.23, -52.46) * mm, v(-2.48, -52.46) * mm, v(-2.58, -52.3) * mm, v(-2.48, -52.04) * mm]});
            skFitSpline(sketch, "E2974", {"points": [v(-2.48, -52.04) * mm, v(-2.4, -51.8) * mm, v(-2.46, -51.62) * mm, v(-2.64, -51.62) * mm]});
            skFitSpline(sketch, "E2975", {"points": [v(-2.64, -51.62) * mm, v(-3.25, -51.62) * mm, v(-4.35, -50.24) * mm, v(-4.35, -49.48) * mm]});
            skFitSpline(sketch, "E2976", {"points": [v(-4.35, -49.48) * mm, v(-4.35, -48.98) * mm, v(-3.98, -48.36) * mm, v(-3.26, -47.63) * mm]});
            skFitSpline(sketch, "E2977", {"points": [v(-3.26, -47.63) * mm, v(-2.08, -46.45) * mm, v(-1.16, -46.25) * mm, v(-0.24, -46.96) * mm]});
            skFitSpline(sketch, "E2978", {"points": [v(-0.24, -46.96) * mm, v(0.3, -47.38) * mm, v(0.3, -47.4) * mm, v(-0.37, -47.95) * mm]});
            skLineSegment(sketch, "E2979", {"start": v(-0.37, -47.95) * mm, "end": v(-1.05, -48.53) * mm});
            skLineSegment(sketch, "E2980", {"start": v(-1.05, -48.53) * mm, "end": v(-1.45, -47.95) * mm});
            skFitSpline(sketch, "E2981", {"points": [v(-1.45, -47.95) * mm, v(-2.28, -46.76) * mm, v(-3.39, -47.67) * mm, v(-2.88, -49.13) * mm]});
            skFitSpline(sketch, "E2982", {"points": [v(-2.88, -49.13) * mm, v(-2.57, -50.03) * mm, v(-1.16, -50.9) * mm, v(-0.46, -50.64) * mm]});
            skFitSpline(sketch, "E2983", {"points": [v(-0.46, -50.64) * mm, v(-0.1, -50.5) * mm, v(-0.1, -50.57) * mm, v(-0.53, -51.04) * mm]});
            skFitSpline(sketch, "E2984", {"points": [v(-0.53, -51.04) * mm, v(-0.82, -51.36) * mm, v(-1.25, -51.62) * mm, v(-1.49, -51.62) * mm]});
            skFitSpline(sketch, "E2985", {"points": [v(-1.49, -51.62) * mm, v(-1.82, -51.62) * mm, v(-1.8, -51.7) * mm, v(-1.37, -52.02) * mm]});
            skFitSpline(sketch, "E2986", {"points": [v(-1.37, -52.02) * mm, v(-0.94, -52.35) * mm, v(-0.89, -52.53) * mm, v(-1.14, -52.94) * mm]});
            skFitSpline(sketch, "E2987", {"points": [v(-1.14, -52.94) * mm, v(-1.3, -53.22) * mm, v(-1.75, -53.47) * mm, v(-2.12, -53.5) * mm]});
            skFitSpline(sketch, "E2988", {"points": [v(-2.12, -53.5) * mm, v(-2.54, -53.53) * mm, v(-2.6, -53.5) * mm, v(-2.3, -53.41) * mm]});
            skFitSpline(sketch, "E2989", {"points": [v(-22.58, -51.63) * mm, v(-23.35, -51.31) * mm, v(-24.63, -49.78) * mm, v(-24.85, -48.9) * mm]});
            skFitSpline(sketch, "E2990", {"points": [v(-24.85, -48.9) * mm, v(-24.95, -48.51) * mm, v(-24.95, -47.73) * mm, v(-24.86, -47.16) * mm]});
            skFitSpline(sketch, "E2991", {"points": [v(-24.86, -47.16) * mm, v(-24.54, -45.16) * mm, v(-21.42, -43.1) * mm, v(-19.46, -43.6) * mm]});
            skFitSpline(sketch, "E2992", {"points": [v(-19.46, -43.6) * mm, v(-18.54, -43.83) * mm, v(-18.54, -44.48) * mm, v(-19.46, -44.9) * mm]});
            skFitSpline(sketch, "E2993", {"points": [v(-19.46, -44.9) * mm, v(-20, -45.14) * mm, v(-20.25, -45.14) * mm, v(-20.5, -44.9) * mm]});
            skFitSpline(sketch, "E2994", {"points": [v(-20.5, -44.9) * mm, v(-21, -44.4) * mm, v(-22.27, -44.5) * mm, v(-22.8, -45.08) * mm]});
            skFitSpline(sketch, "E2995", {"points": [v(-22.8, -45.08) * mm, v(-23.46, -45.81) * mm, v(-23.4, -47.8) * mm, v(-22.67, -48.98) * mm]});
            skFitSpline(sketch, "E2996", {"points": [v(-22.67, -48.98) * mm, v(-21.97, -50.1) * mm, v(-21.35, -50.49) * mm, v(-20.18, -50.49) * mm]});
            skFitSpline(sketch, "E2997", {"points": [v(-20.18, -50.49) * mm, v(-19.49, -50.49) * mm, v(-19.29, -50.34) * mm, v(-19.13, -49.73) * mm]});
            skFitSpline(sketch, "E2998", {"points": [v(-19.13, -49.73) * mm, v(-18.98, -49.13) * mm, v(-19.1, -48.85) * mm, v(-19.7, -48.33) * mm]});
            skLineSegment(sketch, "E2999", {"start": v(-19.7, -48.33) * mm, "end": v(-20.45, -47.68) * mm});
            skLineSegment(sketch, "E3000", {"start": v(-20.45, -47.68) * mm, "end": v(-19.61, -47.25) * mm});
            skFitSpline(sketch, "E3001", {"points": [v(-19.61, -47.25) * mm, v(-19.15, -47.01) * mm, v(-18.71, -46.82) * mm, v(-18.64, -46.82) * mm]});
            skFitSpline(sketch, "E3002", {"points": [v(-18.64, -46.82) * mm, v(-18.25, -46.82) * mm, v(-17.62, -47.8) * mm, v(-17.62, -48.38) * mm]});
            skFitSpline(sketch, "E3003", {"points": [v(-17.62, -48.38) * mm, v(-17.62, -49.24) * mm, v(-19.17, -51.02) * mm, v(-20.36, -51.52) * mm]});
            skFitSpline(sketch, "E3004", {"points": [v(-20.36, -51.52) * mm, v(-21.39, -51.95) * mm, v(-21.74, -51.96) * mm, v(-22.58, -51.63) * mm]});
            skFitSpline(sketch, "E3005", {"points": [v(-15.83, -51.56) * mm, v(-16.17, -51.4) * mm, v(-16.6, -50.9) * mm, v(-16.8, -50.44) * mm]});
            skFitSpline(sketch, "E3006", {"points": [v(-16.8, -50.44) * mm, v(-17.09, -49.72) * mm, v(-17.06, -49.5) * mm, v(-16.58, -48.86) * mm]});
            skFitSpline(sketch, "E3007", {"points": [v(-16.58, -48.86) * mm, v(-15.84, -47.87) * mm, v(-15.4, -47.76) * mm, v(-15.56, -48.6) * mm]});
            skFitSpline(sketch, "E3008", {"points": [v(-15.56, -48.6) * mm, v(-15.73, -49.47) * mm, v(-14.52, -50.94) * mm, v(-13.85, -50.69) * mm]});
            skFitSpline(sketch, "E3009", {"points": [v(-13.85, -50.69) * mm, v(-13.3, -50.47) * mm, v(-13.24, -49.15) * mm, v(-13.75, -48.49) * mm]});
            skFitSpline(sketch, "E3010", {"points": [v(-13.75, -48.49) * mm, v(-14.24, -47.85) * mm, v(-15.31, -47.33) * mm, v(-15.72, -47.53) * mm]});
            skFitSpline(sketch, "E3011", {"points": [v(-15.72, -47.53) * mm, v(-15.9, -47.63) * mm, v(-15.77, -47.44) * mm, v(-15.4, -47.12) * mm]});
            skFitSpline(sketch, "E3012", {"points": [v(-15.4, -47.12) * mm, v(-14.13, -46) * mm, v(-12.42, -46.68) * mm, v(-12.08, -48.42) * mm]});
            skFitSpline(sketch, "E3013", {"points": [v(-12.08, -48.42) * mm, v(-11.94, -49.19) * mm, v(-12.06, -49.47) * mm, v(-13, -50.44) * mm]});
            skFitSpline(sketch, "E3014", {"points": [v(-13, -50.44) * mm, v(-14.22, -51.71) * mm, v(-14.93, -52) * mm, v(-15.83, -51.56) * mm]});
            skFitSpline(sketch, "E3015", {"points": [v(-10.56, -50.5) * mm, v(-10.56, -48.81) * mm, v(-10.99, -47.56) * mm, v(-11.48, -47.81) * mm]});
            skFitSpline(sketch, "E3016", {"points": [v(-11.48, -47.81) * mm, v(-11.67, -47.9) * mm, v(-11.45, -47.66) * mm, v(-10.99, -47.26) * mm]});
            skFitSpline(sketch, "E3017", {"points": [v(-10.99, -47.26) * mm, v(-9.82, -46.27) * mm, v(-9.47, -46.35) * mm, v(-9.26, -47.69) * mm]});
            skLineSegment(sketch, "E3018", {"start": v(-9.26, -47.69) * mm, "end": v(-9.07, -48.83) * mm});
            skLineSegment(sketch, "E3019", {"start": v(-9.07, -48.83) * mm, "end": v(-7.9, -47.69) * mm});
            skFitSpline(sketch, "E3020", {"points": [v(-7.9, -47.69) * mm, v(-7.26, -47.05) * mm, v(-6.57, -46.54) * mm, v(-6.38, -46.54) * mm]});
            skFitSpline(sketch, "E3021", {"points": [v(-6.38, -46.54) * mm, v(-5.93, -46.54) * mm, v(-5.61, -47.42) * mm, v(-5.37, -49.32) * mm]});
            skFitSpline(sketch, "E3022", {"points": [v(-5.37, -49.32) * mm, v(-5.2, -50.59) * mm, v(-5.25, -50.9) * mm, v(-5.68, -51.21) * mm]});
            skFitSpline(sketch, "E3023", {"points": [v(-5.68, -51.21) * mm, v(-6.45, -51.8) * mm, v(-6.53, -51.72) * mm, v(-6.68, -50.32) * mm]});
            skFitSpline(sketch, "E3024", {"points": [v(-6.68, -50.32) * mm, v(-6.76, -49.61) * mm, v(-6.96, -48.9) * mm, v(-7.12, -48.74) * mm]});
            skFitSpline(sketch, "E3025", {"points": [v(-7.12, -48.74) * mm, v(-7.66, -48.2) * mm, v(-8.61, -48.85) * mm, v(-9.47, -50.37) * mm]});
            skFitSpline(sketch, "E3026", {"points": [v(-9.47, -50.37) * mm, v(-9.95, -51.21) * mm, v(-10.39, -51.9) * mm, v(-10.45, -51.9) * mm]});
            skFitSpline(sketch, "E3027", {"points": [v(-10.45, -51.9) * mm, v(-10.51, -51.9) * mm, v(-10.56, -51.27) * mm, v(-10.56, -50.5) * mm]});
            skFitSpline(sketch, "E3028", {"points": [v(1.07, -51.46) * mm, v(0.73, -51.22) * mm, v(0.44, -50.85) * mm, v(0.44, -50.63) * mm]});
            skFitSpline(sketch, "E3029", {"points": [v(0.44, -50.63) * mm, v(0.44, -50.1) * mm, v(1.71, -49.15) * mm, v(2.74, -48.93) * mm]});
            skFitSpline(sketch, "E3030", {"points": [v(2.74, -48.93) * mm, v(3.55, -48.75) * mm, v(3.57, -48.72) * mm, v(3.1, -48.2) * mm]});
            skFitSpline(sketch, "E3031", {"points": [v(3.1, -48.2) * mm, v(2.83, -47.9) * mm, v(2.41, -47.66) * mm, v(2.16, -47.66) * mm]});
            skFitSpline(sketch, "E3032", {"points": [v(2.16, -47.66) * mm, v(1.84, -47.65) * mm, v(1.9, -47.5) * mm, v(2.42, -47.1) * mm]});
            skFitSpline(sketch, "E3033", {"points": [v(2.42, -47.1) * mm, v(2.8, -46.8) * mm, v(3.28, -46.55) * mm, v(3.46, -46.54) * mm]});
            skFitSpline(sketch, "E3034", {"points": [v(3.46, -46.54) * mm, v(3.85, -46.54) * mm, v(4.8, -47.77) * mm, v(5.9, -49.7) * mm]});
            skFitSpline(sketch, "E3035", {"points": [v(5.9, -49.7) * mm, v(6.65, -51.01) * mm, v(6.66, -51.03) * mm, v(6.1, -51.33) * mm]});
            skFitSpline(sketch, "E3036", {"points": [v(6.1, -51.33) * mm, v(5.6, -51.6) * mm, v(5.37, -51.47) * mm, v(4.44, -50.5) * mm]});
            skFitSpline(sketch, "E3037", {"points": [v(4.44, -50.5) * mm, v(3.37, -49.38) * mm, v(2.66, -49.13) * mm, v(1.89, -49.61) * mm]});
            skFitSpline(sketch, "E3038", {"points": [v(1.89, -49.61) * mm, v(1.34, -49.96) * mm, v(2.78, -50.89) * mm, v(3.55, -50.69) * mm]});
            skFitSpline(sketch, "E3039", {"points": [v(3.55, -50.69) * mm, v(4.37, -50.47) * mm, v(4.24, -50.7) * mm, v(3.2, -51.34) * mm]});
            skFitSpline(sketch, "E3040", {"points": [v(3.2, -51.34) * mm, v(2.09, -52.01) * mm, v(1.88, -52.02) * mm, v(1.07, -51.46) * mm]});
            skFitSpline(sketch, "E3041", {"points": [v(11.56, -50.2) * mm, v(11.14, -49.25) * mm, v(10.5, -48.24) * mm, v(10.12, -47.95) * mm]});
            skLineSegment(sketch, "E3042", {"start": v(10.12, -47.95) * mm, "end": v(9.44, -47.42) * mm});
            skLineSegment(sketch, "E3043", {"start": v(9.44, -47.42) * mm, "end": v(10.25, -47) * mm});
            skFitSpline(sketch, "E3044", {"points": [v(10.25, -47) * mm, v(11.27, -46.47) * mm, v(11.53, -46.63) * mm, v(12.54, -48.5) * mm]});
            skLineSegment(sketch, "E3045", {"start": v(12.54, -48.5) * mm, "end": v(13.37, -50) * mm});
            skLineSegment(sketch, "E3046", {"start": v(13.37, -50) * mm, "end": v(13.85, -49.26) * mm});
            skFitSpline(sketch, "E3047", {"points": [v(13.85, -49.26) * mm, v(14.4, -48.42) * mm, v(14.25, -47.67) * mm, v(13.54, -47.67) * mm]});
            skFitSpline(sketch, "E3048", {"points": [v(13.54, -47.67) * mm, v(13.18, -47.67) * mm, v(13.24, -47.53) * mm, v(13.79, -47.1) * mm]});
            skFitSpline(sketch, "E3049", {"points": [v(13.79, -47.1) * mm, v(14.37, -46.64) * mm, v(14.65, -46.59) * mm, v(15.25, -46.82) * mm]});
            skFitSpline(sketch, "E3050", {"points": [v(15.25, -46.82) * mm, v(15.74, -47) * mm, v(15.93, -47.22) * mm, v(15.79, -47.45) * mm]});
            skFitSpline(sketch, "E3051", {"points": [v(15.79, -47.45) * mm, v(15.43, -48.06) * mm, v(12.52, -51.9) * mm, v(12.42, -51.9) * mm]});
            skFitSpline(sketch, "E3052", {"points": [v(12.42, -51.9) * mm, v(12.37, -51.9) * mm, v(11.98, -51.13) * mm, v(11.56, -50.2) * mm]});
            skFitSpline(sketch, "E3053", {"points": [v(17.52, -51.57) * mm, v(16.2, -50.86) * mm, v(15.83, -49.24) * mm, v(16.69, -48) * mm]});
            skFitSpline(sketch, "E3054", {"points": [v(16.69, -48) * mm, v(17.2, -47.28) * mm, v(18.52, -46.54) * mm, v(19.3, -46.54) * mm]});
            skFitSpline(sketch, "E3055", {"points": [v(19.3, -46.54) * mm, v(20, -46.54) * mm, v(20.54, -47.18) * mm, v(20.32, -47.77) * mm]});
            skFitSpline(sketch, "E3056", {"points": [v(20.32, -47.77) * mm, v(20.14, -48.22) * mm, v(18.5, -49.37) * mm, v(18.05, -49.35) * mm]});
            skFitSpline(sketch, "E3057", {"points": [v(18.05, -49.35) * mm, v(17.91, -49.35) * mm, v(18.02, -49.21) * mm, v(18.3, -49.05) * mm]});
            skFitSpline(sketch, "E3058", {"points": [v(18.3, -49.05) * mm, v(18.57, -48.9) * mm, v(18.79, -48.5) * mm, v(18.79, -48.2) * mm]});
            skFitSpline(sketch, "E3059", {"points": [v(18.79, -48.2) * mm, v(18.79, -47.34) * mm, v(17.55, -47.6) * mm, v(17.43, -48.47) * mm]});
            skFitSpline(sketch, "E3060", {"points": [v(17.43, -48.47) * mm, v(17.29, -49.46) * mm, v(18.39, -50.49) * mm, v(19.58, -50.49) * mm]});
            skLineSegment(sketch, "E3061", {"start": v(19.58, -50.49) * mm, "end": v(20.56, -50.49) * mm});
            skLineSegment(sketch, "E3062", {"start": v(20.56, -50.49) * mm, "end": v(19.89, -51.01) * mm});
            skFitSpline(sketch, "E3063", {"points": [v(19.89, -51.01) * mm, v(18.94, -51.75) * mm, v(18.18, -51.93) * mm, v(17.52, -51.57) * mm]});
            skFitSpline(sketch, "E3064", {"points": [v(21.9, -51.7) * mm, v(20.94, -51.33) * mm, v(20.83, -50.63) * mm, v(21.65, -50.18) * mm]});
            skFitSpline(sketch, "E3065", {"points": [v(21.65, -50.18) * mm, v(22.15, -49.92) * mm, v(22.3, -49.94) * mm, v(22.51, -50.31) * mm]});
            skFitSpline(sketch, "E3066", {"points": [v(22.51, -50.31) * mm, v(22.82, -50.85) * mm, v(24.26, -50.95) * mm, v(24.08, -50.42) * mm]});
            skFitSpline(sketch, "E3067", {"points": [v(24.08, -50.42) * mm, v(24.02, -50.22) * mm, v(23.4, -49.86) * mm, v(22.72, -49.6) * mm]});
            skFitSpline(sketch, "E3068", {"points": [v(22.72, -49.6) * mm, v(21, -48.98) * mm, v(20.92, -48.23) * mm, v(22.43, -47.23) * mm]});
            skFitSpline(sketch, "E3069", {"points": [v(22.43, -47.23) * mm, v(23.25, -46.68) * mm, v(23.77, -46.52) * mm, v(24.28, -46.65) * mm]});
            skFitSpline(sketch, "E3070", {"points": [v(24.28, -46.65) * mm, v(25.13, -46.86) * mm, v(25.2, -47.4) * mm, v(24.46, -47.87) * mm]});
            skFitSpline(sketch, "E3071", {"points": [v(24.46, -47.87) * mm, v(24.03, -48.14) * mm, v(23.85, -48.12) * mm, v(23.58, -47.8) * mm]});
            skFitSpline(sketch, "E3072", {"points": [v(23.58, -47.8) * mm, v(23.21, -47.36) * mm, v(22.46, -47.23) * mm, v(22.46, -47.6) * mm]});
            skFitSpline(sketch, "E3073", {"points": [v(22.46, -47.6) * mm, v(22.46, -48) * mm, v(23.11, -48.51) * mm, v(23.61, -48.51) * mm]});
            skFitSpline(sketch, "E3074", {"points": [v(23.61, -48.51) * mm, v(24.35, -48.51) * mm, v(25.34, -49.44) * mm, v(25.14, -49.95) * mm]});
            skFitSpline(sketch, "E3075", {"points": [v(25.14, -49.95) * mm, v(24.77, -50.92) * mm, v(22.74, -52) * mm, v(21.9, -51.7) * mm]});
            skFitSpline(sketch, "E3076", {"points": [v(33.62, -51.64) * mm, v(33.53, -51.5) * mm, v(33.56, -51.3) * mm, v(33.7, -51.23) * mm]});
            skFitSpline(sketch, "E3077", {"points": [v(33.7, -51.23) * mm, v(33.83, -51.14) * mm, v(33.94, -51.26) * mm, v(33.94, -51.49) * mm]});
            skFitSpline(sketch, "E3078", {"points": [v(33.94, -51.49) * mm, v(33.94, -51.96) * mm, v(33.85, -52) * mm, v(33.62, -51.64) * mm]});
            skFitSpline(sketch, "E3079", {"points": [v(7.16, -48.16) * mm, v(7.1, -45.58) * mm, v(6.99, -44.72) * mm, v(6.72, -44.77) * mm]});
            skFitSpline(sketch, "E3080", {"points": [v(6.72, -44.77) * mm, v(6.53, -44.81) * mm, v(6.37, -44.74) * mm, v(6.37, -44.6) * mm]});
            skFitSpline(sketch, "E3081", {"points": [v(6.37, -44.6) * mm, v(6.37, -44.32) * mm, v(8.27, -43.26) * mm, v(8.45, -43.44) * mm]});
            skFitSpline(sketch, "E3082", {"points": [v(8.45, -43.44) * mm, v(8.52, -43.52) * mm, v(8.62, -45.2) * mm, v(8.67, -47.2) * mm]});
            skFitSpline(sketch, "E3083", {"points": [v(8.67, -47.2) * mm, v(8.76, -50.52) * mm, v(8.73, -50.85) * mm, v(8.22, -51.22) * mm]});
            skFitSpline(sketch, "E3084", {"points": [v(8.22, -51.22) * mm, v(7.92, -51.44) * mm, v(7.58, -51.62) * mm, v(7.45, -51.62) * mm]});
            skFitSpline(sketch, "E3085", {"points": [v(7.45, -51.62) * mm, v(7.33, -51.62) * mm, v(7.2, -50.06) * mm, v(7.16, -48.16) * mm]});
            skFitSpline(sketch, "E3086", {"points": [v(-34.97, -51.05) * mm, v(-35.07, -50.9) * mm, v(-35.05, -50.77) * mm, v(-34.94, -50.77) * mm]});
            skFitSpline(sketch, "E3087", {"points": [v(-34.94, -50.77) * mm, v(-34.82, -50.77) * mm, v(-35.1, -50.4) * mm, v(-35.53, -49.93) * mm]});
            skFitSpline(sketch, "E3088", {"points": [v(-35.53, -49.93) * mm, v(-36.32, -49.1) * mm, v(-36.33, -49.07) * mm, v(-35.82, -48.51) * mm]});
            skFitSpline(sketch, "E3089", {"points": [v(-35.82, -48.51) * mm, v(-35.36, -48) * mm, v(-35.26, -47.99) * mm, v(-34.84, -48.37) * mm]});
            skFitSpline(sketch, "E3090", {"points": [v(-34.84, -48.37) * mm, v(-34, -49.12) * mm, v(-33.85, -48.82) * mm, v(-34.65, -48) * mm]});
            skFitSpline(sketch, "E3091", {"points": [v(-34.65, -48) * mm, v(-35.3, -47.3) * mm, v(-35.36, -47.14) * mm, v(-35.01, -46.85) * mm]});
            skFitSpline(sketch, "E3092", {"points": [v(-35.01, -46.85) * mm, v(-34.73, -46.62) * mm, v(-34.54, -46.6) * mm, v(-34.42, -46.8) * mm]});
            skFitSpline(sketch, "E3093", {"points": [v(-34.42, -46.8) * mm, v(-34.32, -46.97) * mm, v(-34.1, -47.1) * mm, v(-33.92, -47.1) * mm]});
            skFitSpline(sketch, "E3094", {"points": [v(-33.92, -47.1) * mm, v(-33.75, -47.1) * mm, v(-33.9, -46.8) * mm, v(-34.24, -46.43) * mm]});
            skFitSpline(sketch, "E3095", {"points": [v(-34.24, -46.43) * mm, v(-34.65, -45.99) * mm, v(-34.77, -45.68) * mm, v(-34.57, -45.56) * mm]});
            skFitSpline(sketch, "E3096", {"points": [v(-34.57, -45.56) * mm, v(-34.4, -45.45) * mm, v(-34.33, -45.26) * mm, v(-34.4, -45.13) * mm]});
            skFitSpline(sketch, "E3097", {"points": [v(-34.4, -45.13) * mm, v(-34.5, -45) * mm, v(-34.45, -44.81) * mm, v(-34.31, -44.73) * mm]});
            skFitSpline(sketch, "E3098", {"points": [v(-34.31, -44.73) * mm, v(-34.17, -44.64) * mm, v(-34.1, -44.26) * mm, v(-34.14, -43.88) * mm]});
            skFitSpline(sketch, "E3099", {"points": [v(-34.14, -43.88) * mm, v(-34.18, -43.5) * mm, v(-34.03, -43.02) * mm, v(-33.8, -42.83) * mm]});
            skFitSpline(sketch, "E3100", {"points": [v(-33.8, -42.83) * mm, v(-33.58, -42.64) * mm, v(-33.41, -42.6) * mm, v(-33.44, -42.75) * mm]});
            skFitSpline(sketch, "E3101", {"points": [v(-33.44, -42.75) * mm, v(-33.47, -42.9) * mm, v(-33.46, -43.1) * mm, v(-33.42, -43.22) * mm]});
            skFitSpline(sketch, "E3102", {"points": [v(-33.42, -43.22) * mm, v(-33.38, -43.34) * mm, v(-33.34, -43.55) * mm, v(-33.32, -43.7) * mm]});
            skFitSpline(sketch, "E3103", {"points": [v(-33.32, -43.7) * mm, v(-33.3, -43.85) * mm, v(-33.03, -44.17) * mm, v(-32.72, -44.4) * mm]});
            skFitSpline(sketch, "E3104", {"points": [v(-32.72, -44.4) * mm, v(-32.28, -44.74) * mm, v(-32.27, -44.8) * mm, v(-32.63, -44.68) * mm]});
            skFitSpline(sketch, "E3105", {"points": [v(-32.63, -44.68) * mm, v(-33, -44.55) * mm, v(-33.1, -44.64) * mm, v(-33, -45.08) * mm]});
            skFitSpline(sketch, "E3106", {"points": [v(-33, -45.08) * mm, v(-32.93, -45.46) * mm, v(-33.02, -45.61) * mm, v(-33.25, -45.52) * mm]});
            skFitSpline(sketch, "E3107", {"points": [v(-33.25, -45.52) * mm, v(-33.45, -45.45) * mm, v(-33.61, -45.58) * mm, v(-33.61, -45.83) * mm]});
            skFitSpline(sketch, "E3108", {"points": [v(-33.61, -45.83) * mm, v(-33.61, -46.08) * mm, v(-33.46, -46.22) * mm, v(-33.28, -46.15) * mm]});
            skFitSpline(sketch, "E3109", {"points": [v(-33.28, -46.15) * mm, v(-33.1, -46.08) * mm, v(-32.95, -46.2) * mm, v(-32.95, -46.4) * mm]});
            skFitSpline(sketch, "E3110", {"points": [v(-32.95, -46.4) * mm, v(-32.95, -46.6) * mm, v(-33.12, -46.7) * mm, v(-33.32, -46.62) * mm]});
            skFitSpline(sketch, "E3111", {"points": [v(-33.32, -46.62) * mm, v(-33.56, -46.53) * mm, v(-33.64, -46.68) * mm, v(-33.57, -47.06) * mm]});
            skFitSpline(sketch, "E3112", {"points": [v(-33.57, -47.06) * mm, v(-33.5, -47.45) * mm, v(-33.58, -47.59) * mm, v(-33.84, -47.49) * mm]});
            skFitSpline(sketch, "E3113", {"points": [v(-33.84, -47.49) * mm, v(-34.42, -47.27) * mm, v(-34.2, -48.16) * mm, v(-33.55, -48.65) * mm]});
            skFitSpline(sketch, "E3114", {"points": [v(-33.55, -48.65) * mm, v(-33.02, -49.07) * mm, v(-33.02, -49.07) * mm, v(-33.54, -48.89) * mm]});
            skFitSpline(sketch, "E3115", {"points": [v(-33.54, -48.89) * mm, v(-33.9, -48.76) * mm, v(-34.02, -48.8) * mm, v(-33.88, -49.03) * mm]});
            skFitSpline(sketch, "E3116", {"points": [v(-33.88, -49.03) * mm, v(-33.74, -49.25) * mm, v(-33.83, -49.3) * mm, v(-34.16, -49.17) * mm]});
            skFitSpline(sketch, "E3117", {"points": [v(-34.16, -49.17) * mm, v(-34.5, -49.03) * mm, v(-34.58, -49.08) * mm, v(-34.42, -49.34) * mm]});
            skFitSpline(sketch, "E3118", {"points": [v(-34.42, -49.34) * mm, v(-34.29, -49.55) * mm, v(-34.49, -49.5) * mm, v(-34.91, -49.23) * mm]});
            skFitSpline(sketch, "E3119", {"points": [v(-34.91, -49.23) * mm, v(-35.45, -48.88) * mm, v(-35.68, -48.85) * mm, v(-35.84, -49.1) * mm]});
            skFitSpline(sketch, "E3120", {"points": [v(-35.84, -49.1) * mm, v(-35.95, -49.3) * mm, v(-35.93, -49.38) * mm, v(-35.8, -49.29) * mm]});
            skFitSpline(sketch, "E3121", {"points": [v(-35.8, -49.29) * mm, v(-35.65, -49.2) * mm, v(-35.16, -49.44) * mm, v(-34.7, -49.82) * mm]});
            skFitSpline(sketch, "E3122", {"points": [v(-34.7, -49.82) * mm, v(-34.23, -50.2) * mm, v(-34.06, -50.43) * mm, v(-34.33, -50.33) * mm]});
            skFitSpline(sketch, "E3123", {"points": [v(-34.33, -50.33) * mm, v(-34.7, -50.2) * mm, v(-34.79, -50.29) * mm, v(-34.7, -50.74) * mm]});
            skFitSpline(sketch, "E3124", {"points": [v(-34.7, -50.74) * mm, v(-34.57, -51.38) * mm, v(-34.7, -51.5) * mm, v(-34.97, -51.05) * mm]});
            skFitSpline(sketch, "E3125", {"points": [v(-34.83, -50.1) * mm, v(-34.83, -50.04) * mm, v(-35.06, -49.82) * mm, v(-35.33, -49.6) * mm]});
            skFitSpline(sketch, "E3126", {"points": [v(-35.33, -49.6) * mm, v(-35.77, -49.25) * mm, v(-35.78, -49.26) * mm, v(-35.43, -49.71) * mm]});
            skFitSpline(sketch, "E3127", {"points": [v(-35.43, -49.71) * mm, v(-35.06, -50.18) * mm, v(-34.83, -50.33) * mm, v(-34.83, -50.1) * mm]});
            skFitSpline(sketch, "E3128", {"points": [v(-34.55, -48.97) * mm, v(-34.55, -48.91) * mm, v(-34.77, -48.69) * mm, v(-35.04, -48.48) * mm]});
            skFitSpline(sketch, "E3129", {"points": [v(-35.04, -48.48) * mm, v(-35.5, -48.13) * mm, v(-35.5, -48.14) * mm, v(-35.15, -48.58) * mm]});
            skFitSpline(sketch, "E3130", {"points": [v(-35.15, -48.58) * mm, v(-34.78, -49.05) * mm, v(-34.55, -49.2) * mm, v(-34.55, -48.97) * mm]});
            skFitSpline(sketch, "E3131", {"points": [v(-34.41, -47.45) * mm, v(-34.47, -47.18) * mm, v(-34.52, -46.92) * mm, v(-34.53, -46.87) * mm]});
            skFitSpline(sketch, "E3132", {"points": [v(-34.53, -46.87) * mm, v(-34.54, -46.82) * mm, v(-34.68, -46.87) * mm, v(-34.85, -46.97) * mm]});
            skFitSpline(sketch, "E3133", {"points": [v(-34.85, -46.97) * mm, v(-35.05, -47.1) * mm, v(-35.04, -47.28) * mm, v(-34.81, -47.55) * mm]});
            skFitSpline(sketch, "E3134", {"points": [v(-34.81, -47.55) * mm, v(-34.38, -48.07) * mm, v(-34.3, -48.05) * mm, v(-34.41, -47.45) * mm]});
            skFitSpline(sketch, "E3135", {"points": [v(-33.85, -45.96) * mm, v(-33.9, -45.64) * mm, v(-33.79, -45.31) * mm, v(-33.58, -45.23) * mm]});
            skFitSpline(sketch, "E3136", {"points": [v(-33.58, -45.23) * mm, v(-33.27, -45.11) * mm, v(-33.18, -44.38) * mm, v(-33.44, -44.07) * mm]});
            skFitSpline(sketch, "E3137", {"points": [v(-33.44, -44.07) * mm, v(-33.47, -44.03) * mm, v(-33.5, -43.88) * mm, v(-33.53, -43.74) * mm]});
            skFitSpline(sketch, "E3138", {"points": [v(-33.53, -43.74) * mm, v(-33.6, -43.2) * mm, v(-33.87, -43.2) * mm, v(-33.9, -43.73) * mm]});
            skFitSpline(sketch, "E3139", {"points": [v(-33.9, -43.73) * mm, v(-33.93, -44.03) * mm, v(-33.8, -44.28) * mm, v(-33.62, -44.29) * mm]});
            skFitSpline(sketch, "E3140", {"points": [v(-33.62, -44.29) * mm, v(-33.43, -44.3) * mm, v(-33.5, -44.43) * mm, v(-33.78, -44.59) * mm]});
            skFitSpline(sketch, "E3141", {"points": [v(-33.78, -44.59) * mm, v(-34.06, -44.75) * mm, v(-34.21, -44.99) * mm, v(-34.13, -45.12) * mm]});
            skFitSpline(sketch, "E3142", {"points": [v(-34.13, -45.12) * mm, v(-34.05, -45.26) * mm, v(-34.11, -45.45) * mm, v(-34.28, -45.55) * mm]});
            skFitSpline(sketch, "E3143", {"points": [v(-34.28, -45.55) * mm, v(-34.49, -45.68) * mm, v(-34.48, -45.86) * mm, v(-34.25, -46.14) * mm]});
            skFitSpline(sketch, "E3144", {"points": [v(-34.25, -46.14) * mm, v(-33.8, -46.68) * mm, v(-33.72, -46.64) * mm, v(-33.85, -45.96) * mm]});
            skLineSegment(sketch, "E3145", {"start": v(-33.85, -45.96) * mm, "end": v(-33.85, -45.96) * mm});
            skFitSpline(sketch, "E3146", {"points": [v(33.71, -46.04) * mm, v(33.36, -45.6) * mm, v(33.37, -45.59) * mm, v(33.82, -45.94) * mm]});
            skFitSpline(sketch, "E3147", {"points": [v(33.82, -45.94) * mm, v(34.29, -46.3) * mm, v(34.44, -46.54) * mm, v(34.2, -46.54) * mm]});
            skFitSpline(sketch, "E3148", {"points": [v(34.2, -46.54) * mm, v(34.15, -46.54) * mm, v(33.92, -46.31) * mm, v(33.71, -46.04) * mm]});
            skFitSpline(sketch, "E3149", {"points": [v(-29.06, -40.48) * mm, v(-28.76, -40.24) * mm, v(-28.4, -40.05) * mm, v(-28.24, -40.05) * mm]});
            skFitSpline(sketch, "E3150", {"points": [v(-28.24, -40.05) * mm, v(-27.88, -40.05) * mm, v(-28.04, -40.18) * mm, v(-28.9, -40.59) * mm]});
            skFitSpline(sketch, "E3151", {"points": [v(-28.9, -40.59) * mm, v(-29.57, -40.9) * mm, v(-29.58, -40.9) * mm, v(-29.06, -40.48) * mm]});
            skSolve(sketch);
        }
        {
            var Q0;
            Q0=makeQuery(id+"F0.imprint","IMPRINT",FACE,{"disambiguationData":[TD([[makeQuery(id+"F0.imprint","IMPRINT",EDGE,{"derivedFrom":sQuery(id+"F0.wireOp",EDGE,"E2989")}),-1.0]])]});
            var Q1;
            Q1=makeQuery(id+"F0.imprint","IMPRINT",FACE,{"disambiguationData":[TD([[makeQuery(id+"F0.imprint","IMPRINT",EDGE,{"derivedFrom":sQuery(id+"F0.wireOp",EDGE,"E3005")}),-1.0]])]});
            var Q2;
            Q2=makeQuery(id+"F0.imprint","IMPRINT",FACE,{"disambiguationData":[TD([[makeQuery(id+"F0.imprint","IMPRINT",EDGE,{"derivedFrom":sQuery(id+"F0.wireOp",EDGE,"E3015")}),-1.0]])]});
            var Q3;
            Q3=makeQuery(id+"F0.imprint","IMPRINT",FACE,{"disambiguationData":[TD([[makeQuery(id+"F0.imprint","IMPRINT",EDGE,{"derivedFrom":sQuery(id+"F0.wireOp",EDGE,"E2972")}),-1.0]])]});
            var Q4;
            Q4=makeQuery(id+"F0.imprint","IMPRINT",FACE,{"disambiguationData":[TD([[makeQuery(id+"F0.imprint","IMPRINT",EDGE,{"derivedFrom":sQuery(id+"F0.wireOp",EDGE,"E3028")}),-1.0]])]});
            var Q5;
            Q5=makeQuery(id+"F0.imprint","IMPRINT",FACE,{"disambiguationData":[TD([[makeQuery(id+"F0.imprint","IMPRINT",EDGE,{"derivedFrom":sQuery(id+"F0.wireOp",EDGE,"E3079")}),-1.0]])]});
            var Q6;
            Q6=makeQuery(id+"F0.imprint","IMPRINT",FACE,{"disambiguationData":[TD([[makeQuery(id+"F0.imprint","IMPRINT",EDGE,{"derivedFrom":sQuery(id+"F0.wireOp",EDGE,"E3041")}),-1.0]])]});
            var Q7;
            Q7=makeQuery(id+"F0.imprint","IMPRINT",FACE,{"disambiguationData":[TD([[makeQuery(id+"F0.imprint","IMPRINT",EDGE,{"derivedFrom":sQuery(id+"F0.wireOp",EDGE,"E3053")}),-1.0]])]});
            var Q8;
            Q8=makeQuery(id+"F0.imprint","IMPRINT",FACE,{"disambiguationData":[TD([[makeQuery(id+"F0.imprint","IMPRINT",EDGE,{"derivedFrom":sQuery(id+"F0.wireOp",EDGE,"E3064")}),-1.0]])]});
            extrude(context, id + "F1", {"entities" : qUnion([Q0, Q1, Q2, Q3, Q4, Q5, Q6, Q7, Q8]), "depth" : 12.7 * mm});
        }
        {
            var Q0;
            Q0=makeQuery(id+"F0.imprint","IMPRINT",FACE,{"disambiguationData":[TD([[makeQuery(id+"F0.imprint","IMPRINT",EDGE,{"derivedFrom":sQuery(id+"F0.wireOp",EDGE,"E713")}),-1.0]])]});
            var Q1;
            Q1=makeQuery(id+"F0.imprint","IMPRINT",FACE,{"disambiguationData":[TD([[makeQuery(id+"F0.imprint","IMPRINT",EDGE,{"derivedFrom":sQuery(id+"F0.wireOp",EDGE,"E604")}),-1.0]])]});
            extrude(context, id + "F2", {"entities" : qUnion([Q0, Q1]), "depth" : 12.7 * mm});
        }
        {
            var Q0;
            Q0=makeQuery(id+"F0.imprint","IMPRINT",FACE,{"disambiguationData":[TD([[makeQuery(id+"F0.imprint","IMPRINT",EDGE,{"derivedFrom":sQuery(id+"F0.wireOp",EDGE,"E0")}),-1.0]])]});
            extrude(context, id + "F3", {"entities" : qUnion([Q0]), "depth" : 6.35 * mm});
        }
        {
            var Q0;
            Q0=makeQuery(id+"F0.imprint","IMPRINT",FACE,{"disambiguationData":[TD([[makeQuery(id+"F0.imprint","IMPRINT",EDGE,{"derivedFrom":sQuery(id+"F0.wireOp",EDGE,"E1492")}),-1.0]])]});
            var Q1;
            Q1=makeQuery(id+"F0.imprint","IMPRINT",FACE,{"disambiguationData":[TD([[makeQuery(id+"F0.imprint","IMPRINT",EDGE,{"derivedFrom":sQuery(id+"F0.wireOp",EDGE,"E1510")}),-1.0]])]});
            var Q2;
            Q2=makeQuery(id+"F0.imprint","IMPRINT",FACE,{"disambiguationData":[TD([[makeQuery(id+"F0.imprint","IMPRINT",EDGE,{"derivedFrom":sQuery(id+"F0.wireOp",EDGE,"E1516")}),-1.0]])]});
            var Q3;
            Q3=makeQuery(id+"F0.imprint","IMPRINT",FACE,{"disambiguationData":[TD([[makeQuery(id+"F0.imprint","IMPRINT",EDGE,{"derivedFrom":sQuery(id+"F0.wireOp",EDGE,"E1503")}),-1.0]])]});
            var Q4;
            Q4=makeQuery(id+"F0.imprint","IMPRINT",FACE,{"disambiguationData":[TD([[makeQuery(id+"F0.imprint","IMPRINT",EDGE,{"derivedFrom":sQuery(id+"F0.wireOp",EDGE,"E1542")}),-1.0]])]});
            var Q5;
            Q5=makeQuery(id+"F0.imprint","IMPRINT",FACE,{"disambiguationData":[TD([[makeQuery(id+"F0.imprint","IMPRINT",EDGE,{"derivedFrom":sQuery(id+"F0.wireOp",EDGE,"E1539")}),-1.0]])]});
            var Q6;
            Q6=makeQuery(id+"F0.imprint","IMPRINT",FACE,{"disambiguationData":[TD([[makeQuery(id+"F0.imprint","IMPRINT",EDGE,{"derivedFrom":sQuery(id+"F0.wireOp",EDGE,"E1532")}),-1.0]])]});
            var Q7;
            Q7=makeQuery(id+"F0.imprint","IMPRINT",FACE,{"disambiguationData":[TD([[makeQuery(id+"F0.imprint","IMPRINT",EDGE,{"derivedFrom":sQuery(id+"F0.wireOp",EDGE,"E1536")}),-1.0]])]});
            var Q8;
            Q8=makeQuery(id+"F0.imprint","IMPRINT",FACE,{"disambiguationData":[TD([[makeQuery(id+"F0.imprint","IMPRINT",EDGE,{"derivedFrom":sQuery(id+"F0.wireOp",EDGE,"E1529")}),-1.0]])]});
            var Q9;
            Q9=makeQuery(id+"F0.imprint","IMPRINT",FACE,{"disambiguationData":[TD([[makeQuery(id+"F0.imprint","IMPRINT",EDGE,{"derivedFrom":sQuery(id+"F0.wireOp",EDGE,"E1523")}),-1.0]])]});
            var Q10;
            Q10=makeQuery(id+"F0.imprint","IMPRINT",FACE,{"disambiguationData":[TD([[makeQuery(id+"F0.imprint","IMPRINT",EDGE,{"derivedFrom":sQuery(id+"F0.wireOp",EDGE,"E1526")}),-1.0]])]});
            var Q11;
            Q11=makeQuery(id+"F0.imprint","IMPRINT",FACE,{"disambiguationData":[TD([[makeQuery(id+"F0.imprint","IMPRINT",EDGE,{"derivedFrom":sQuery(id+"F0.wireOp",EDGE,"E1520")}),-1.0]])]});
            var Q12;
            Q12=makeQuery(id+"F0.imprint","IMPRINT",FACE,{"disambiguationData":[TD([[makeQuery(id+"F0.imprint","IMPRINT",EDGE,{"derivedFrom":sQuery(id+"F0.wireOp",EDGE,"E1513")}),-1.0]])]});
            var Q13;
            Q13=makeQuery(id+"F0.imprint","IMPRINT",FACE,{"disambiguationData":[TD([[makeQuery(id+"F0.imprint","IMPRINT",EDGE,{"derivedFrom":sQuery(id+"F0.wireOp",EDGE,"E1500")}),-1.0]])]});
            var Q14;
            Q14=makeQuery(id+"F0.imprint","IMPRINT",FACE,{"disambiguationData":[TD([[makeQuery(id+"F0.imprint","IMPRINT",EDGE,{"derivedFrom":sQuery(id+"F0.wireOp",EDGE,"E1507")}),-1.0]])]});
            var Q15;
            Q15=makeQuery(id+"F0.imprint","IMPRINT",FACE,{"disambiguationData":[TD([[makeQuery(id+"F0.imprint","IMPRINT",EDGE,{"derivedFrom":sQuery(id+"F0.wireOp",EDGE,"E1497")}),-1.0]])]});
            var Q16;
            Q16=makeQuery(id+"F0.imprint","IMPRINT",FACE,{"disambiguationData":[TD([[makeQuery(id+"F0.imprint","IMPRINT",EDGE,{"derivedFrom":sQuery(id+"F0.wireOp",EDGE,"E1551")}),-1.0]])]});
            var Q17;
            Q17=makeQuery(id+"F0.imprint","IMPRINT",FACE,{"disambiguationData":[TD([[makeQuery(id+"F0.imprint","IMPRINT",EDGE,{"derivedFrom":sQuery(id+"F0.wireOp",EDGE,"E1554")}),-1.0]])]});
            var Q18;
            Q18=makeQuery(id+"F0.imprint","IMPRINT",FACE,{"disambiguationData":[TD([[makeQuery(id+"F0.imprint","IMPRINT",EDGE,{"derivedFrom":sQuery(id+"F0.wireOp",EDGE,"E1560")}),-1.0]])]});
            var Q19;
            Q19=makeQuery(id+"F0.imprint","IMPRINT",FACE,{"disambiguationData":[TD([[makeQuery(id+"F0.imprint","IMPRINT",EDGE,{"derivedFrom":sQuery(id+"F0.wireOp",EDGE,"E1557")}),-1.0]])]});
            var Q20;
            Q20=makeQuery(id+"F0.imprint","IMPRINT",FACE,{"disambiguationData":[TD([[makeQuery(id+"F0.imprint","IMPRINT",EDGE,{"derivedFrom":sQuery(id+"F0.wireOp",EDGE,"E1548")}),-1.0]])]});
            var Q21;
            Q21=makeQuery(id+"F0.imprint","IMPRINT",FACE,{"disambiguationData":[TD([[makeQuery(id+"F0.imprint","IMPRINT",EDGE,{"derivedFrom":sQuery(id+"F0.wireOp",EDGE,"E1568")}),-1.0]])]});
            var Q22;
            Q22=makeQuery(id+"F0.imprint","IMPRINT",FACE,{"disambiguationData":[TD([[makeQuery(id+"F0.imprint","IMPRINT",EDGE,{"derivedFrom":sQuery(id+"F0.wireOp",EDGE,"E1574")}),-1.0]])]});
            var Q23;
            Q23=makeQuery(id+"F0.imprint","IMPRINT",FACE,{"disambiguationData":[TD([[makeQuery(id+"F0.imprint","IMPRINT",EDGE,{"derivedFrom":sQuery(id+"F0.wireOp",EDGE,"E1565")}),-1.0]])]});
            var Q24;
            Q24=makeQuery(id+"F0.imprint","IMPRINT",FACE,{"disambiguationData":[TD([[makeQuery(id+"F0.imprint","IMPRINT",EDGE,{"derivedFrom":sQuery(id+"F0.wireOp",EDGE,"E1571")}),-1.0]])]});
            var Q25;
            Q25=makeQuery(id+"F0.imprint","IMPRINT",FACE,{"disambiguationData":[TD([[makeQuery(id+"F0.imprint","IMPRINT",EDGE,{"derivedFrom":sQuery(id+"F0.wireOp",EDGE,"E1577")}),-1.0]])]});
            var Q26;
            Q26=makeQuery(id+"F0.imprint","IMPRINT",FACE,{"disambiguationData":[TD([[makeQuery(id+"F0.imprint","IMPRINT",EDGE,{"derivedFrom":sQuery(id+"F0.wireOp",EDGE,"E1109")}),-1.0]])]});
            var Q27;
            Q27=makeQuery(id+"F0.imprint","IMPRINT",FACE,{"disambiguationData":[TD([[makeQuery(id+"F0.imprint","IMPRINT",EDGE,{"derivedFrom":sQuery(id+"F0.wireOp",EDGE,"E1105")}),-1.0]])]});
            var Q28;
            Q28=makeQuery(id+"F0.imprint","IMPRINT",FACE,{"disambiguationData":[TD([[makeQuery(id+"F0.imprint","IMPRINT",EDGE,{"derivedFrom":sQuery(id+"F0.wireOp",EDGE,"E1100")}),-1.0]])]});
            var Q29;
            Q29=makeQuery(id+"F0.imprint","IMPRINT",FACE,{"disambiguationData":[TD([[makeQuery(id+"F0.imprint","IMPRINT",EDGE,{"derivedFrom":sQuery(id+"F0.wireOp",EDGE,"E1097")}),-1.0]])]});
            var Q30;
            Q30=makeQuery(id+"F0.imprint","IMPRINT",FACE,{"disambiguationData":[TD([[makeQuery(id+"F0.imprint","IMPRINT",EDGE,{"derivedFrom":sQuery(id+"F0.wireOp",EDGE,"E1753")}),-1.0]])]});
            var Q31;
            Q31=makeQuery(id+"F0.imprint","IMPRINT",FACE,{"disambiguationData":[TD([[makeQuery(id+"F0.imprint","IMPRINT",EDGE,{"derivedFrom":sQuery(id+"F0.wireOp",EDGE,"E1770")}),-1.0]])]});
            var Q32;
            Q32=makeQuery(id+"F0.imprint","IMPRINT",FACE,{"disambiguationData":[TD([[makeQuery(id+"F0.imprint","IMPRINT",EDGE,{"derivedFrom":sQuery(id+"F0.wireOp",EDGE,"E1776")}),-1.0]])]});
            var Q33;
            Q33=makeQuery(id+"F0.imprint","IMPRINT",FACE,{"disambiguationData":[TD([[makeQuery(id+"F0.imprint","IMPRINT",EDGE,{"derivedFrom":sQuery(id+"F0.wireOp",EDGE,"E1764")}),-1.0]])]});
            var Q34;
            Q34=makeQuery(id+"F0.imprint","IMPRINT",FACE,{"disambiguationData":[TD([[makeQuery(id+"F0.imprint","IMPRINT",EDGE,{"derivedFrom":sQuery(id+"F0.wireOp",EDGE,"E2065")}),-1.0]])]});
            var Q35;
            Q35=makeQuery(id+"F0.imprint","IMPRINT",FACE,{"disambiguationData":[TD([[makeQuery(id+"F0.imprint","IMPRINT",EDGE,{"derivedFrom":sQuery(id+"F0.wireOp",EDGE,"E1930")}),-1.0]])]});
            var Q36;
            Q36=makeQuery(id+"F0.imprint","IMPRINT",FACE,{"disambiguationData":[TD([[makeQuery(id+"F0.imprint","IMPRINT",EDGE,{"derivedFrom":sQuery(id+"F0.wireOp",EDGE,"E1750")}),-1.0]])]});
            var Q37;
            Q37=makeQuery(id+"F0.imprint","IMPRINT",FACE,{"disambiguationData":[TD([[makeQuery(id+"F0.imprint","IMPRINT",EDGE,{"derivedFrom":sQuery(id+"F0.wireOp",EDGE,"E1767")}),-1.0]])]});
            var Q38;
            Q38=makeQuery(id+"F0.imprint","IMPRINT",FACE,{"disambiguationData":[TD([[makeQuery(id+"F0.imprint","IMPRINT",EDGE,{"derivedFrom":sQuery(id+"F0.wireOp",EDGE,"E1792")}),-1.0]])]});
            var Q39;
            Q39=makeQuery(id+"F0.imprint","IMPRINT",FACE,{"disambiguationData":[TD([[makeQuery(id+"F0.imprint","IMPRINT",EDGE,{"derivedFrom":sQuery(id+"F0.wireOp",EDGE,"E1789")}),-1.0]])]});
            var Q40;
            Q40=makeQuery(id+"F0.imprint","IMPRINT",FACE,{"disambiguationData":[TD([[makeQuery(id+"F0.imprint","IMPRINT",EDGE,{"derivedFrom":sQuery(id+"F0.wireOp",EDGE,"E1780")}),-1.0]])]});
            var Q41;
            Q41=makeQuery(id+"F0.imprint","IMPRINT",FACE,{"disambiguationData":[TD([[makeQuery(id+"F0.imprint","IMPRINT",EDGE,{"derivedFrom":sQuery(id+"F0.wireOp",EDGE,"E1795")}),-1.0]])]});
            var Q42;
            Q42=makeQuery(id+"F0.imprint","IMPRINT",FACE,{"disambiguationData":[TD([[makeQuery(id+"F0.imprint","IMPRINT",EDGE,{"derivedFrom":sQuery(id+"F0.wireOp",EDGE,"E1784")}),-1.0]])]});
            var Q43;
            Q43=makeQuery(id+"F0.imprint","IMPRINT",FACE,{"disambiguationData":[TD([[makeQuery(id+"F0.imprint","IMPRINT",EDGE,{"derivedFrom":sQuery(id+"F0.wireOp",EDGE,"E2799")}),-1.0]])]});
            var Q44;
            Q44=makeQuery(id+"F0.imprint","IMPRINT",FACE,{"disambiguationData":[TD([[makeQuery(id+"F0.imprint","IMPRINT",EDGE,{"derivedFrom":sQuery(id+"F0.wireOp",EDGE,"E2851")}),-1.0]])]});
            var Q45;
            Q45=makeQuery(id+"F0.imprint","IMPRINT",FACE,{"disambiguationData":[TD([[makeQuery(id+"F0.imprint","IMPRINT",EDGE,{"derivedFrom":sQuery(id+"F0.wireOp",EDGE,"E2860")}),-1.0]])]});
            var Q46;
            Q46=makeQuery(id+"F0.imprint","IMPRINT",FACE,{"disambiguationData":[TD([[makeQuery(id+"F0.imprint","IMPRINT",EDGE,{"derivedFrom":sQuery(id+"F0.wireOp",EDGE,"E2857")}),-1.0]])]});
            var Q47;
            Q47=makeQuery(id+"F0.imprint","IMPRINT",FACE,{"disambiguationData":[TD([[makeQuery(id+"F0.imprint","IMPRINT",EDGE,{"derivedFrom":sQuery(id+"F0.wireOp",EDGE,"E2870")}),-1.0]])]});
            var Q48;
            Q48=makeQuery(id+"F0.imprint","IMPRINT",FACE,{"disambiguationData":[TD([[makeQuery(id+"F0.imprint","IMPRINT",EDGE,{"derivedFrom":sQuery(id+"F0.wireOp",EDGE,"E2867")}),-1.0]])]});
            var Q49;
            Q49=makeQuery(id+"F0.imprint","IMPRINT",FACE,{"disambiguationData":[TD([[makeQuery(id+"F0.imprint","IMPRINT",EDGE,{"derivedFrom":sQuery(id+"F0.wireOp",EDGE,"E2854")}),-1.0]])]});
            var Q50;
            Q50=makeQuery(id+"F0.imprint","IMPRINT",FACE,{"disambiguationData":[TD([[makeQuery(id+"F0.imprint","IMPRINT",EDGE,{"derivedFrom":sQuery(id+"F0.wireOp",EDGE,"E2848")}),-1.0]])]});
            var Q51;
            Q51=makeQuery(id+"F0.imprint","IMPRINT",FACE,{"disambiguationData":[TD([[makeQuery(id+"F0.imprint","IMPRINT",EDGE,{"derivedFrom":sQuery(id+"F0.wireOp",EDGE,"E2730")}),-1.0]])]});
            var Q52;
            Q52=makeQuery(id+"F0.imprint","IMPRINT",FACE,{"disambiguationData":[TD([[makeQuery(id+"F0.imprint","IMPRINT",EDGE,{"derivedFrom":sQuery(id+"F0.wireOp",EDGE,"E2726")}),-1.0]])]});
            var Q53;
            Q53=makeQuery(id+"F0.imprint","IMPRINT",FACE,{"disambiguationData":[TD([[makeQuery(id+"F0.imprint","IMPRINT",EDGE,{"derivedFrom":sQuery(id+"F0.wireOp",EDGE,"E2681")}),-1.0]])]});
            var Q54;
            Q54=makeQuery(id+"F0.imprint","IMPRINT",FACE,{"disambiguationData":[TD([[makeQuery(id+"F0.imprint","IMPRINT",EDGE,{"derivedFrom":sQuery(id+"F0.wireOp",EDGE,"E2605")}),-1.0]])]});
            var Q55;
            Q55=makeQuery(id+"F0.imprint","IMPRINT",FACE,{"disambiguationData":[TD([[makeQuery(id+"F0.imprint","IMPRINT",EDGE,{"derivedFrom":sQuery(id+"F0.wireOp",EDGE,"E2685")}),-1.0]])]});
            var Q56;
            Q56=makeQuery(id+"F0.imprint","IMPRINT",FACE,{"disambiguationData":[TD([[makeQuery(id+"F0.imprint","IMPRINT",EDGE,{"derivedFrom":sQuery(id+"F0.wireOp",EDGE,"E2690")}),-1.0]])]});
            var Q57;
            Q57=makeQuery(id+"F0.imprint","IMPRINT",FACE,{"disambiguationData":[TD([[makeQuery(id+"F0.imprint","IMPRINT",EDGE,{"derivedFrom":sQuery(id+"F0.wireOp",EDGE,"E2694")}),-1.0]])]});
            var Q58;
            Q58=makeQuery(id+"F0.imprint","IMPRINT",FACE,{"disambiguationData":[TD([[makeQuery(id+"F0.imprint","IMPRINT",EDGE,{"derivedFrom":sQuery(id+"F0.wireOp",EDGE,"E2698")}),-1.0]])]});
            var Q59;
            Q59=makeQuery(id+"F0.imprint","IMPRINT",FACE,{"disambiguationData":[TD([[makeQuery(id+"F0.imprint","IMPRINT",EDGE,{"derivedFrom":sQuery(id+"F0.wireOp",EDGE,"E2877")}),-1.0]])]});
            var Q60;
            Q60=makeQuery(id+"F0.imprint","IMPRINT",FACE,{"disambiguationData":[TD([[makeQuery(id+"F0.imprint","IMPRINT",EDGE,{"derivedFrom":sQuery(id+"F0.wireOp",EDGE,"E2893")}),-1.0]])]});
            var Q61;
            Q61=makeQuery(id+"F0.imprint","IMPRINT",FACE,{"disambiguationData":[TD([[makeQuery(id+"F0.imprint","IMPRINT",EDGE,{"derivedFrom":sQuery(id+"F0.wireOp",EDGE,"E2897")}),-1.0]])]});
            var Q62;
            Q62=makeQuery(id+"F0.imprint","IMPRINT",FACE,{"disambiguationData":[TD([[makeQuery(id+"F0.imprint","IMPRINT",EDGE,{"derivedFrom":sQuery(id+"F0.wireOp",EDGE,"E2883")}),-1.0]])]});
            var Q63;
            Q63=makeQuery(id+"F0.imprint","IMPRINT",FACE,{"disambiguationData":[TD([[makeQuery(id+"F0.imprint","IMPRINT",EDGE,{"derivedFrom":sQuery(id+"F0.wireOp",EDGE,"E2880")}),-1.0]])]});
            var Q64;
            Q64=makeQuery(id+"F0.imprint","IMPRINT",FACE,{"disambiguationData":[TD([[makeQuery(id+"F0.imprint","IMPRINT",EDGE,{"derivedFrom":sQuery(id+"F0.wireOp",EDGE,"E2900")}),-1.0]])]});
            var Q65;
            Q65=makeQuery(id+"F0.imprint","IMPRINT",FACE,{"disambiguationData":[TD([[makeQuery(id+"F0.imprint","IMPRINT",EDGE,{"derivedFrom":sQuery(id+"F0.wireOp",EDGE,"E2904")}),-1.0]])]});
            var Q66;
            Q66=makeQuery(id+"F0.imprint","IMPRINT",FACE,{"disambiguationData":[TD([[makeQuery(id+"F0.imprint","IMPRINT",EDGE,{"derivedFrom":sQuery(id+"F0.wireOp",EDGE,"E2890")}),-1.0]])]});
            var Q67;
            Q67=makeQuery(id+"F0.imprint","IMPRINT",FACE,{"disambiguationData":[TD([[makeQuery(id+"F0.imprint","IMPRINT",EDGE,{"derivedFrom":sQuery(id+"F0.wireOp",EDGE,"E2887")}),-1.0]])]});
            var Q68;
            Q68=makeQuery(id+"F0.imprint","IMPRINT",FACE,{"disambiguationData":[TD([[makeQuery(id+"F0.imprint","IMPRINT",EDGE,{"derivedFrom":sQuery(id+"F0.wireOp",EDGE,"E2873")}),-1.0]])]});
            var Q69;
            Q69=makeQuery(id+"F0.imprint","IMPRINT",FACE,{"disambiguationData":[TD([[makeQuery(id+"F0.imprint","IMPRINT",EDGE,{"derivedFrom":sQuery(id+"F0.wireOp",EDGE,"E2864")}),-1.0]])]});
            var Q70;
            Q70=makeQuery(id+"F0.imprint","IMPRINT",FACE,{"disambiguationData":[TD([[makeQuery(id+"F0.imprint","IMPRINT",EDGE,{"derivedFrom":sQuery(id+"F0.wireOp",EDGE,"E2678")}),-1.0]])]});
            var Q71;
            Q71=makeQuery(id+"F0.imprint","IMPRINT",FACE,{"disambiguationData":[TD([[makeQuery(id+"F0.imprint","IMPRINT",EDGE,{"derivedFrom":sQuery(id+"F0.wireOp",EDGE,"E2666")}),-1.0]])]});
            var Q72;
            Q72=makeQuery(id+"F0.imprint","IMPRINT",FACE,{"disambiguationData":[TD([[makeQuery(id+"F0.imprint","IMPRINT",EDGE,{"derivedFrom":sQuery(id+"F0.wireOp",EDGE,"E2662")}),-1.0]])]});
            var Q73;
            Q73=makeQuery(id+"F0.imprint","IMPRINT",FACE,{"disambiguationData":[TD([[makeQuery(id+"F0.imprint","IMPRINT",EDGE,{"derivedFrom":sQuery(id+"F0.wireOp",EDGE,"E2649")}),-1.0]])]});
            var Q74;
            Q74=makeQuery(id+"F0.imprint","IMPRINT",FACE,{"disambiguationData":[TD([[makeQuery(id+"F0.imprint","IMPRINT",EDGE,{"derivedFrom":sQuery(id+"F0.wireOp",EDGE,"E2672")}),-1.0]])]});
            var Q75;
            Q75=makeQuery(id+"F0.imprint","IMPRINT",FACE,{"disambiguationData":[TD([[makeQuery(id+"F0.imprint","IMPRINT",EDGE,{"derivedFrom":sQuery(id+"F0.wireOp",EDGE,"E2632")}),-1.0]])]});
            var Q76;
            Q76=makeQuery(id+"F0.imprint","IMPRINT",FACE,{"disambiguationData":[TD([[makeQuery(id+"F0.imprint","IMPRINT",EDGE,{"derivedFrom":sQuery(id+"F0.wireOp",EDGE,"E2640")}),-1.0]])]});
            var Q77;
            Q77=makeQuery(id+"F0.imprint","IMPRINT",FACE,{"disambiguationData":[TD([[makeQuery(id+"F0.imprint","IMPRINT",EDGE,{"derivedFrom":sQuery(id+"F0.wireOp",EDGE,"E2643")}),-1.0]])]});
            var Q78;
            Q78=makeQuery(id+"F0.imprint","IMPRINT",FACE,{"disambiguationData":[TD([[makeQuery(id+"F0.imprint","IMPRINT",EDGE,{"derivedFrom":sQuery(id+"F0.wireOp",EDGE,"E2637")}),-1.0]])]});
            var Q79;
            Q79=makeQuery(id+"F0.imprint","IMPRINT",FACE,{"disambiguationData":[TD([[makeQuery(id+"F0.imprint","IMPRINT",EDGE,{"derivedFrom":sQuery(id+"F0.wireOp",EDGE,"E2602")}),-1.0]])]});
            var Q80;
            Q80=makeQuery(id+"F0.imprint","IMPRINT",FACE,{"disambiguationData":[TD([[makeQuery(id+"F0.imprint","IMPRINT",EDGE,{"derivedFrom":sQuery(id+"F0.wireOp",EDGE,"E2625")}),-1.0]])]});
            var Q81;
            Q81=makeQuery(id+"F0.imprint","IMPRINT",FACE,{"disambiguationData":[TD([[makeQuery(id+"F0.imprint","IMPRINT",EDGE,{"derivedFrom":sQuery(id+"F0.wireOp",EDGE,"E2646")}),-1.0]])]});
            var Q82;
            Q82=makeQuery(id+"F0.imprint","IMPRINT",FACE,{"disambiguationData":[TD([[makeQuery(id+"F0.imprint","IMPRINT",EDGE,{"derivedFrom":sQuery(id+"F0.wireOp",EDGE,"E2628")}),-1.0]])]});
            var Q83;
            Q83=makeQuery(id+"F0.imprint","IMPRINT",FACE,{"disambiguationData":[TD([[makeQuery(id+"F0.imprint","IMPRINT",EDGE,{"derivedFrom":sQuery(id+"F0.wireOp",EDGE,"E2655")}),-1.0]])]});
            var Q84;
            Q84=makeQuery(id+"F0.imprint","IMPRINT",FACE,{"disambiguationData":[TD([[makeQuery(id+"F0.imprint","IMPRINT",EDGE,{"derivedFrom":sQuery(id+"F0.wireOp",EDGE,"E2669")}),-1.0]])]});
            var Q85;
            Q85=makeQuery(id+"F0.imprint","IMPRINT",FACE,{"disambiguationData":[TD([[makeQuery(id+"F0.imprint","IMPRINT",EDGE,{"derivedFrom":sQuery(id+"F0.wireOp",EDGE,"E2659")}),-1.0]])]});
            var Q86;
            Q86=makeQuery(id+"F0.imprint","IMPRINT",FACE,{"disambiguationData":[TD([[makeQuery(id+"F0.imprint","IMPRINT",EDGE,{"derivedFrom":sQuery(id+"F0.wireOp",EDGE,"E2936")}),-1.0]])]});
            var Q87;
            Q87=makeQuery(id+"F0.imprint","IMPRINT",FACE,{"disambiguationData":[TD([[makeQuery(id+"F0.imprint","IMPRINT",EDGE,{"derivedFrom":sQuery(id+"F0.wireOp",EDGE,"E2939")}),-1.0]])]});
            var Q88;
            Q88=makeQuery(id+"F0.imprint","IMPRINT",FACE,{"disambiguationData":[TD([[makeQuery(id+"F0.imprint","IMPRINT",EDGE,{"derivedFrom":sQuery(id+"F0.wireOp",EDGE,"E2942")}),-1.0]])]});
            var Q89;
            Q89=makeQuery(id+"F0.imprint","IMPRINT",FACE,{"disambiguationData":[TD([[makeQuery(id+"F0.imprint","IMPRINT",EDGE,{"derivedFrom":sQuery(id+"F0.wireOp",EDGE,"E2962")}),-1.0]])]});
            var Q90;
            Q90=makeQuery(id+"F0.imprint","IMPRINT",FACE,{"disambiguationData":[TD([[makeQuery(id+"F0.imprint","IMPRINT",EDGE,{"derivedFrom":sQuery(id+"F0.wireOp",EDGE,"E2965")}),-1.0]])]});
            var Q91;
            Q91=makeQuery(id+"F0.imprint","IMPRINT",FACE,{"disambiguationData":[TD([[makeQuery(id+"F0.imprint","IMPRINT",EDGE,{"derivedFrom":sQuery(id+"F0.wireOp",EDGE,"E2968")}),-1.0]])]});
            var Q92;
            Q92=makeQuery(id+"F0.imprint","IMPRINT",FACE,{"disambiguationData":[TD([[makeQuery(id+"F0.imprint","IMPRINT",EDGE,{"derivedFrom":sQuery(id+"F0.wireOp",EDGE,"E2706")}),-1.0]])]});
            var Q93;
            Q93=makeQuery(id+"F0.imprint","IMPRINT",FACE,{"disambiguationData":[TD([[makeQuery(id+"F0.imprint","IMPRINT",EDGE,{"derivedFrom":sQuery(id+"F0.wireOp",EDGE,"E2702")}),-1.0]])]});
            var Q94;
            Q94=makeQuery(id+"F0.imprint","IMPRINT",FACE,{"disambiguationData":[TD([[makeQuery(id+"F0.imprint","IMPRINT",EDGE,{"derivedFrom":sQuery(id+"F0.wireOp",EDGE,"E2907")}),-1.0]])]});
            var Q95;
            Q95=makeQuery(id+"F0.imprint","IMPRINT",FACE,{"disambiguationData":[TD([[makeQuery(id+"F0.imprint","IMPRINT",EDGE,{"derivedFrom":sQuery(id+"F0.wireOp",EDGE,"E1171")}),-1.0]])]});
            var Q96;
            Q96=makeQuery(id+"F0.imprint","IMPRINT",FACE,{"disambiguationData":[TD([[makeQuery(id+"F0.imprint","IMPRINT",EDGE,{"derivedFrom":sQuery(id+"F0.wireOp",EDGE,"E1168")}),-1.0]])]});
            var Q97;
            Q97=makeQuery(id+"F0.imprint","IMPRINT",FACE,{"disambiguationData":[TD([[makeQuery(id+"F0.imprint","IMPRINT",EDGE,{"derivedFrom":sQuery(id+"F0.wireOp",EDGE,"E1165")}),-1.0]])]});
            extrude(context, id + "F4", {"entities" : qUnion([Q0, Q1, Q2, Q3, Q4, Q5, Q6, Q7, Q8, Q9, Q10, Q11, Q12, Q13, Q14, Q15, Q16, Q17, Q18, Q19, Q20, Q21, Q22, Q23, Q24, Q25, Q26, Q27, Q28, Q29, Q30, Q31, Q32, Q33, Q34, Q35, Q36, Q37, Q38, Q39, Q40, Q41, Q42, Q43, Q44, Q45, Q46, Q47, Q48, Q49, Q50, Q51, Q52, Q53, Q54, Q55, Q56, Q57, Q58, Q59, Q60, Q61, Q62, Q63, Q64, Q65, Q66, Q67, Q68, Q69, Q70, Q71, Q72, Q73, Q74, Q75, Q76, Q77, Q78, Q79, Q80, Q81, Q82, Q83, Q84, Q85, Q86, Q87, Q88, Q89, Q90, Q91, Q92, Q93, Q94, Q95, Q96, Q97]), "depth" : 5.08 * mm});
        }
        {
            var Q0;
            Q0=makeQuery(id+"F0.imprint","IMPRINT",FACE,{"disambiguationData":[TD([[makeQuery(id+"F0.imprint","IMPRINT",EDGE,{"derivedFrom":sQuery(id+"F0.wireOp",EDGE,"E998")}),-1.0]])]});
            var Q1;
            Q1=makeQuery(id+"F0.imprint","IMPRINT",FACE,{"disambiguationData":[TD([[makeQuery(id+"F0.imprint","IMPRINT",EDGE,{"derivedFrom":sQuery(id+"F0.wireOp",EDGE,"E992")}),-1.0]])]});
            var Q2;
            Q2=makeQuery(id+"F0.imprint","IMPRINT",FACE,{"disambiguationData":[TD([[makeQuery(id+"F0.imprint","IMPRINT",EDGE,{"derivedFrom":sQuery(id+"F0.wireOp",EDGE,"E989")}),-1.0]])]});
            var Q3;
            Q3=makeQuery(id+"F0.imprint","IMPRINT",FACE,{"disambiguationData":[TD([[makeQuery(id+"F0.imprint","IMPRINT",EDGE,{"derivedFrom":sQuery(id+"F0.wireOp",EDGE,"E1002")}),-1.0]])]});
            var Q4;
            Q4=makeQuery(id+"F0.imprint","IMPRINT",FACE,{"disambiguationData":[TD([[makeQuery(id+"F0.imprint","IMPRINT",EDGE,{"derivedFrom":sQuery(id+"F0.wireOp",EDGE,"E995")}),-1.0]])]});
            var Q5;
            Q5=makeQuery(id+"F0.imprint","IMPRINT",FACE,{"disambiguationData":[TD([[makeQuery(id+"F0.imprint","IMPRINT",EDGE,{"derivedFrom":sQuery(id+"F0.wireOp",EDGE,"E1028")}),-1.0]])]});
            var Q6;
            Q6=makeQuery(id+"F0.imprint","IMPRINT",FACE,{"disambiguationData":[TD([[makeQuery(id+"F0.imprint","IMPRINT",EDGE,{"derivedFrom":sQuery(id+"F0.wireOp",EDGE,"E1024")}),-1.0]])]});
            var Q7;
            Q7=makeQuery(id+"F0.imprint","IMPRINT",FACE,{"disambiguationData":[TD([[makeQuery(id+"F0.imprint","IMPRINT",EDGE,{"derivedFrom":sQuery(id+"F0.wireOp",EDGE,"E1018")}),-1.0]])]});
            var Q8;
            Q8=makeQuery(id+"F0.imprint","IMPRINT",FACE,{"disambiguationData":[TD([[makeQuery(id+"F0.imprint","IMPRINT",EDGE,{"derivedFrom":sQuery(id+"F0.wireOp",EDGE,"E1014")}),-1.0]])]});
            var Q9;
            Q9=makeQuery(id+"F0.imprint","IMPRINT",FACE,{"disambiguationData":[TD([[makeQuery(id+"F0.imprint","IMPRINT",EDGE,{"derivedFrom":sQuery(id+"F0.wireOp",EDGE,"E1021")}),-1.0]])]});
            extrude(context, id + "F5", {"entities" : qUnion([Q0, Q1, Q2, Q3, Q4, Q5, Q6, Q7, Q8, Q9]), "depth" : 5.08 * mm});
        }
    });
